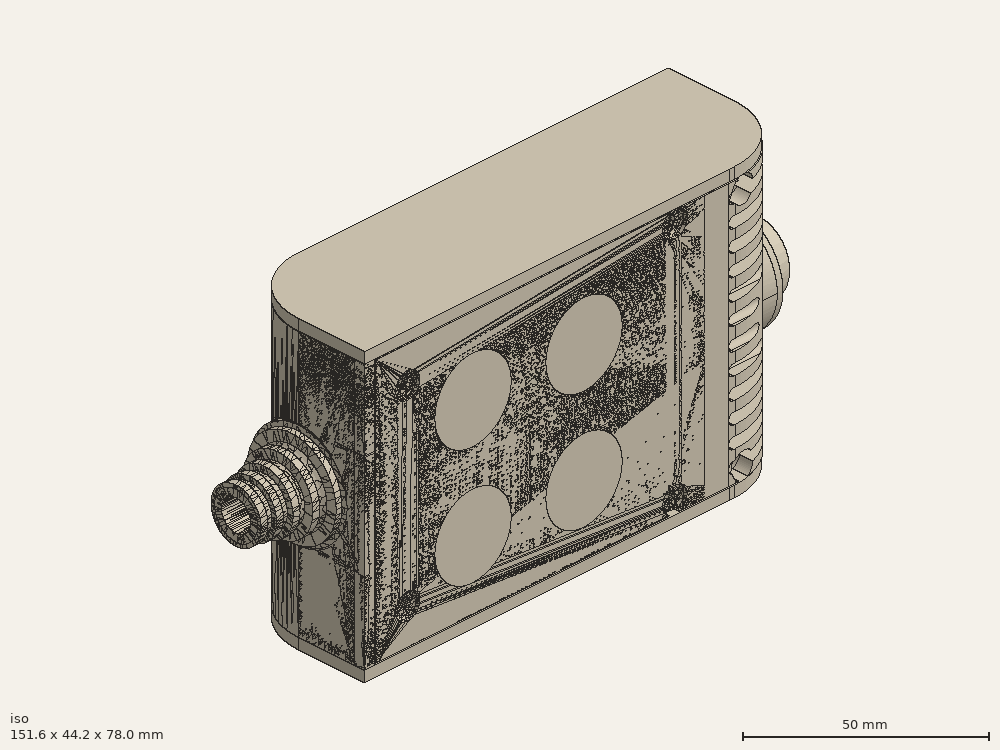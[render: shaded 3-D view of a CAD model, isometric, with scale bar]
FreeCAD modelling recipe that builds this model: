
FCSTD DOCUMENT  (FreeCAD 0.19R0.19.2)
Label: enclosure_195FCStd
License: All rights reserved
LicenseURL: http://en.wikipedia.org/wiki/All_rights_reserved
objects: Part::Revolution×152, Part::MultiFuse×146, Part::Feature×146, Sketcher::SketchObject×84, Part::Cut×70, Part::Cylinder×70, Part::Extrusion×67, Part::Fillet×58, Part::Box×36, App::MeasureDistance×4, PartDesign::Body×2, Image::ImagePlane×1
note: 831 computed .brp shape members not serialized (recipe doc carries the construction recipe); baked Part::Feature solids carry a one-line shape summary decoded from their .brp

FEATURE [Sketcher::SketchObject] Sketch  label="topSketch"
  FullyConstrained = true
  sketch-geometry (20):
    g0: LineSegment StartX=5.21097e-06 StartY=3 StartZ=0 EndX=5.21097e-06 EndY=19 EndZ=0
    g1: ArcOfCircle CenterX=19 CenterY=19 CenterZ=0 NormalX=0 NormalY=0 NormalZ=1 AngleXU=0 Radius=19 StartAngle=1.5708 EndAngle=3.14159
    g2: ArcOfCircle CenterX=19 CenterY=19 CenterZ=0 NormalX=0 NormalY=0 NormalZ=1 AngleXU=0 Radius=16 StartAngle=1.5708 EndAngle=3.14159
    g3: LineSegment StartX=114 StartY=35 StartZ=0 EndX=19 EndY=35 EndZ=0
    g4: LineSegment StartX=5.21097e-06 StartY=3 StartZ=0 EndX=5.21097e-06 EndY=0 EndZ=0
    g5: LineSegment StartX=3 StartY=0 StartZ=0 EndX=5.21097e-06 EndY=0 EndZ=0
    g6: LineSegment StartX=3 StartY=19 StartZ=0 EndX=3 EndY=0 EndZ=0
    g7: LineSegment StartX=19 StartY=38 StartZ=0 EndX=124 EndY=38 EndZ=0
    g8: Circle CenterX=119 CenterY=35 CenterZ=0 NormalX=0 NormalY=0 NormalZ=1 AngleXU=0 Radius=1
    g9: Circle CenterX=121 CenterY=35 CenterZ=0 NormalX=0 NormalY=0 NormalZ=1 AngleXU=0 Radius=1
    g10: Circle CenterX=121 CenterY=33 CenterZ=0 NormalX=0 NormalY=0 NormalZ=1 AngleXU=0 Radius=1
    g11: BSplineCurve PolesCount=3 KnotsCount=2 Degree=2 IsPeriodic=0
    g12: GeomPoint X=119 Y=35 Z=0
    g13: GeomPoint X=121 Y=33 Z=0
    g14: LineSegment StartX=119 StartY=35 StartZ=0 EndX=114 EndY=35 EndZ=0
    g15: ArcOfCircle CenterX=105 CenterY=19 CenterZ=0 NormalX=0 NormalY=0 NormalZ=1 AngleXU=0 Radius=19 StartAngle=5.7297 EndAngle=6.28319
    g16: ArcOfCircle CenterX=105 CenterY=19 CenterZ=0 NormalX=0 NormalY=0 NormalZ=1 AngleXU=0 Radius=16 StartAngle=5.60905 EndAngle=6.28319
    g17: LineSegment StartX=121 StartY=33 StartZ=0 EndX=121 EndY=19 EndZ=0
    g18: LineSegment StartX=124 StartY=38 StartZ=0 EndX=124 EndY=19 EndZ=0
    g19: LineSegment StartX=117.5 StartY=9.01251 StartZ=0 EndX=121.163 EndY=9.0125 EndZ=0
  constraints (46):
    c: Vertical(g0)
    c: Block(g0)
    c: Coincident(g1,g0)
    c: Block(g1)
    c: Coincident(g2,g1)
    c: Block(g2)
    c: Coincident(g3,g2)
    c: Horizontal(g3)
    c: Tangent(g3,g2)
    c: Coincident(g4,g0)
    c: Distance(g4) = 3
    c: Vertical(g4)
    c: Coincident(g5,g4)
    c: Horizontal(g5)
    c: Coincident(g6,g2)
    c: Coincident(g6,g5)
    c: Vertical(g6)
    c: Horizontal(g7)
    c: Distance(g7) = 105
    c: Coincident(g7,g1)
    c: Block(g3)
    c: Weight(g8) = 1
    c: Equal(g8,g9)
    c: Equal(g8,g10)
    c: InternalAlignment(g8,g11)
    c: InternalAlignment(g9,g11)
    c: InternalAlignment(g10,g11)
    c: InternalAlignment(g12,g11)
    c: InternalAlignment(g13,g11)
    c: Block(g11)
    c: Coincident(g14,g11)
    c: Coincident(g14,g3)
    c: Horizontal(g14)
    c: Block(g15)
    c: Coincident(g16,g15)
    c: Block(g16)
    c: Coincident(g17,g11)
    c: Coincident(g17,g16)
    c: Vertical(g17)
    c: Distance(g17) = 14
    c: Coincident(g18,g7)
    c: Coincident(g18,g15)
    c: Vertical(g18)
    c: Distance(g18) = 19
    c: Coincident(g19,g16)
    c: Coincident(g19,g15)
FEATURE [Sketcher::SketchObject] Sketch001  label="bottomSketch"
  FullyConstrained = true
  sketch-geometry (32):
    g0: LineSegment StartX=3.3 StartY=-6.03275e-07 StartZ=0 EndX=98 EndY=-6.03275e-07 EndZ=0
    g1: ArcOfCircle CenterX=98 CenterY=19 CenterZ=0 NormalX=0 NormalY=0 NormalZ=1 AngleXU=0 Radius=19 StartAngle=4.71239 EndAngle=5.71103
    g2: LineSegment StartX=6.3 StartY=8 StartZ=0 EndX=3.3 EndY=8 EndZ=0
    g3: LineSegment StartX=3.3 StartY=8 StartZ=0 EndX=3.3 EndY=-6.03275e-07 EndZ=0
    g4: ArcOfCircle CenterX=8.3 CenterY=5 CenterZ=0 NormalX=0 NormalY=0 NormalZ=1 AngleXU=0 Radius=2 StartAngle=3.14159 EndAngle=4.71239
    g5: LineSegment StartX=6.3 StartY=8 StartZ=0 EndX=6.3 EndY=5 EndZ=0
    g6: ArcOfCircle CenterX=98 CenterY=19 CenterZ=0 NormalX=0 NormalY=0 NormalZ=1 AngleXU=0 Radius=12.7 StartAngle=4.71239 EndAngle=6.28319
    g7: LineSegment StartX=94.7 StartY=3 StartZ=0 EndX=8.3 EndY=3 EndZ=0
    g8-g12: Circle x5 (B-spline internal-alignment scaffolding for g13; pole/knot coordinates omitted)
    g13: BSplineCurve PolesCount=5 KnotsCount=3 Degree=3 IsPeriodic=0
    g14: GeomPoint X=98 Y=6.3 Z=0
    g15: GeomPoint X=96.3938 Y=4.71946 Z=0
    g16: GeomPoint X=94.7 Y=3 Z=0
    g17-g23: Circle x7 (B-spline internal-alignment scaffolding for g24; pole/knot coordinates omitted)
    g24: BSplineCurve PolesCount=7 KnotsCount=5 Degree=3 IsPeriodic=0
    g25-g29: GeomPoint x5 (B-spline internal-alignment scaffolding for g24; pole/knot coordinates omitted)
    g30: ArcOfCircle CenterX=98 CenterY=19 CenterZ=0 NormalX=0 NormalY=0 NormalZ=1 AngleXU=0 Radius=15.7 StartAngle=5.81226 EndAngle=6.28319
    g31: LineSegment StartX=110.7 StartY=19 StartZ=0 EndX=113.7 EndY=19 EndZ=0
  constraints (41):
    c: Horizontal(g0)
    c: Coincident(g1,g0)
    c: Block(g1)
    c: Horizontal(g2)
    c: Distance(g2) = 3
    c: Coincident(g3,g2)
    c: Vertical(g3)
    c: Coincident(g3,g0)
    c: Block(g4)
    c: Block(g2)
    c: Coincident(g5,g2)
    c: Coincident(g5,g4)
    c: Vertical(g5)
    c: Coincident(g6,g1)
    c: Block(g6)
    c: Coincident(g7,g4)
    c: Horizontal(g7)
    c: Block(g0)
    c: Block(g7)
    c: Block(g3)
    c: Coincident(g13,g6)
    c: Weight(g8) = 1
    c: Equal(g8, g9-g12) x4
    c: Coincident(g13,g7)
    c: InternalAlignment(g8-g12 -> g13) x5
    c: InternalAlignment(g14,g13)
    c: InternalAlignment(g15,g13)
    c: InternalAlignment(g16,g13)
    c: Block(g13)
    c: Weight(g17) = 1
    c: Equal(g17, g18-g23) x6
    c: Coincident(g24,g1)
    c: InternalAlignment(g17-g23 -> g24) x7
    c: InternalAlignment(g25-g29 -> g24) x5
    c: Block(g24)
    c: Coincident(g30,g24)
    c: Coincident(g31,g6)
    c: Coincident(g31,g30)
    c: Horizontal(g31)
    c: Block(g31)
    c: Block(g30)
FEATURE [Part::Extrusion] Extrude  label="top"
  Base = -> Sketch
  Dir = (0,0,1)
  DirMode = 2
  FaceMakerClass = Part::FaceMakerBullseye
  LengthFwd = 72
  LengthRev = 0
  Solid = true
  Symmetric = false
FEATURE [Part::Extrusion] Extrude001  label="bottom"
  Base = -> Sketch001
  Dir = (0,0,1)
  DirMode = 2
  FaceMakerClass = Part::FaceMakerBullseye
  LengthFwd = 71.4
  LengthRev = 0
  Placement = pos=(0,0,0.3) rot=(0,0,1;0rad)
  Solid = true
  Symmetric = false
FEATURE [Sketcher::SketchObject] Sketch002  label="topSketch001"
  FullyConstrained = true
  sketch-geometry (8):
    g0: ArcOfCircle CenterX=19 CenterY=19.0975 CenterZ=0 NormalX=0 NormalY=0 NormalZ=1 AngleXU=0 Radius=18.9025 StartAngle=1.5708 EndAngle=3.14674
    g1: LineSegment StartX=0.0977805 StartY=19.0003 StartZ=0 EndX=0.0977805 EndY=0.000251602 EndZ=0
    g2: LineSegment StartX=19 StartY=38 StartZ=0 EndX=124 EndY=38 EndZ=0
    g3: LineSegment StartX=0.0977805 StartY=0.000251602 StartZ=0 EndX=105.098 EndY=0.000251602 EndZ=0
    g4: LineSegment StartX=124 StartY=38 StartZ=0 EndX=125.616 EndY=38 EndZ=0
    g5: LineSegment StartX=105.098 StartY=0.000251602 StartZ=0 EndX=106.713 EndY=0.000251602 EndZ=0
    g6: ArcOfCircle CenterX=106.616 CenterY=19 CenterZ=0 NormalX=0 NormalY=0 NormalZ=1 AngleXU=0 Radius=19 StartAngle=4.71754 EndAngle=6.28319
    g7: LineSegment StartX=125.616 StartY=38 StartZ=0 EndX=125.616 EndY=19 EndZ=0
  constraints (21):
    c: Block(g0)
    c: Coincident(g1,g0)
    c: Vertical(g1)
    c: Horizontal(g2)
    c: Distance(g2) = 105
    c: Coincident(g2,g0)
    c: Distance(g1) = 19
    c: Coincident(g3,g1)
    c: Horizontal(g3)
    c: Distance(g3) = 105
    c: Coincident(g4,g2)
    c: Horizontal(g4)
    c: Distance(g4) = 1.61553
    c: Horizontal(g5)
    c: Equal(g4,g5) = 1.61553
    c: Coincident(g5,g3)
    c: Block(g6)
    c: Coincident(g6,g5)
    c: Coincident(g7,g4)
    c: Coincident(g7,g6)
    c: Vertical(g7)
FEATURE [Part::Extrusion] Extrude002  label="sideA"
  Base = -> Sketch002
  Dir = (0,0,1)
  DirMode = 2
  FaceMakerClass = Part::FaceMakerBullseye
  LengthFwd = 3
  LengthRev = 0
  Placement = pos=(0,0,-3) rot=(0,0,1;0rad)
  Solid = true
  Symmetric = false
FEATURE [Sketcher::SketchObject] Sketch003  label="topSketch002"
  FullyConstrained = true
  sketch-geometry (6):
    g0: LineSegment StartX=19 StartY=38 StartZ=0 EndX=117 EndY=38 EndZ=0
    g1: ArcOfCircle CenterX=19 CenterY=19 CenterZ=0 NormalX=0 NormalY=0 NormalZ=1 AngleXU=0 Radius=19 StartAngle=1.5708 EndAngle=3.14159
    g2: LineSegment StartX=117 StartY=38 StartZ=0 EndX=117 EndY=19 EndZ=0
    g3: LineSegment StartX=98 StartY=1.0161e-12 StartZ=0 EndX=5.22862e-06 EndY=1.0161e-12 EndZ=0
    g4: LineSegment StartX=5.22862e-06 StartY=19 StartZ=0 EndX=5.22862e-06 EndY=1.0161e-12 EndZ=0
    g5: ArcOfCircle CenterX=98 CenterY=19 CenterZ=0 NormalX=0 NormalY=0 NormalZ=1 AngleXU=0 Radius=19 StartAngle=4.71239 EndAngle=6.28319
  constraints (16):
    c: Horizontal(g0)
    c: Distance(g0) = 98
    c: Coincident(g1,g0)
    c: Block(g1)
    c: Coincident(g2,g0)
    c: Vertical(g2)
    c: Distance(g2) = 19
    c: Horizontal(g3)
    c: Coincident(g4,g1)
    c: Vertical(g4)
    c: Coincident(g3,g4)
    c: Block(g3)
    c: Coincident(g5,g2)
    c: Coincident(g5,g3)
    c: Block(g0)
    c: Block(g5)
FEATURE [Sketcher::SketchObject] Sketch004
  FullyConstrained = true
  MapMode = 3
  Placement = pos=(0,0,0) rot=(1,0,0;1.5708rad)
  Support = -> [Extrude]
  sketch-geometry (8):
    g0: Circle CenterX=80.351 CenterY=-67.6202 CenterZ=0 NormalX=0 NormalY=0 NormalZ=1 AngleXU=0 Radius=2
    g1: Circle CenterX=80.351 CenterY=-67.6202 CenterZ=0 NormalX=0 NormalY=0 NormalZ=1 AngleXU=0 Radius=3
    g2: Circle CenterX=80.351 CenterY=-4.92017 CenterZ=0 NormalX=0 NormalY=0 NormalZ=1 AngleXU=0 Radius=2
    g3: Circle CenterX=80.351 CenterY=-4.92017 CenterZ=0 NormalX=0 NormalY=0 NormalZ=1 AngleXU=0 Radius=3
    g4: Circle CenterX=23.851 CenterY=-4.92017 CenterZ=0 NormalX=0 NormalY=0 NormalZ=1 AngleXU=0 Radius=2
    g5: Circle CenterX=23.851 CenterY=-4.92017 CenterZ=0 NormalX=0 NormalY=0 NormalZ=1 AngleXU=0 Radius=3
    g6: Circle CenterX=23.851 CenterY=-67.6202 CenterZ=0 NormalX=0 NormalY=0 NormalZ=1 AngleXU=0 Radius=2
    g7: Circle CenterX=23.851 CenterY=-67.6202 CenterZ=0 NormalX=0 NormalY=0 NormalZ=1 AngleXU=0 Radius=3
  constraints (8):
    c: Block(g3)
    c: Block(g2)
    c: Block(g1)
    c: Block(g0)
    c: Block(g6)
    c: Block(g7)
    c: Block(g4)
    c: Block(g5)
FEATURE [Part::Extrusion] Extrude004
  Base = -> Sketch004
  Dir = (0,-1,2e-16)
  DirMode = 2
  FaceMakerClass = Part::FaceMakerBullseye
  LengthFwd = 6
  LengthRev = 0
  Placement = pos=(0,9,0) rot=(0,0,1;0rad)
  Solid = true
  Symmetric = false
FEATURE [Sketcher::SketchObject] Sketch005
  FullyConstrained = true
  MapMode = 3
  Placement = pos=(0,0,0) rot=(1,0,0;1.5708rad)
  Support = -> [Extrude]
  sketch-geometry (8):
    g0: Circle CenterX=80.351 CenterY=-67.6202 CenterZ=0 NormalX=0 NormalY=0 NormalZ=1 AngleXU=0 Radius=3
    g1: Circle CenterX=80.351 CenterY=-4.92017 CenterZ=0 NormalX=0 NormalY=0 NormalZ=1 AngleXU=0 Radius=3
    g2: Circle CenterX=23.851 CenterY=-4.92017 CenterZ=0 NormalX=0 NormalY=0 NormalZ=1 AngleXU=0 Radius=3
    g3: Circle CenterX=23.851 CenterY=-67.6202 CenterZ=0 NormalX=0 NormalY=0 NormalZ=1 AngleXU=0 Radius=3
    g4: Circle CenterX=23.851 CenterY=-67.6202 CenterZ=0 NormalX=0 NormalY=0 NormalZ=1 AngleXU=0 Radius=5
    g5: Circle CenterX=80.351 CenterY=-67.6202 CenterZ=0 NormalX=0 NormalY=0 NormalZ=1 AngleXU=0 Radius=5
    g6: Circle CenterX=23.851 CenterY=-4.92017 CenterZ=0 NormalX=0 NormalY=0 NormalZ=1 AngleXU=0 Radius=5
    g7: Circle CenterX=80.351 CenterY=-4.92017 CenterZ=0 NormalX=0 NormalY=0 NormalZ=1 AngleXU=0 Radius=5
  constraints (8):
    c: Block(g1)
    c: Block(g0)
    c: Block(g3)
    c: Block(g2)
    c: Block(g5)
    c: Block(g4)
    c: Block(g6)
    c: Block(g7)
FEATURE [Part::Extrusion] Extrude005
  Base = -> Sketch005
  Dir = (0,-1,2e-16)
  DirMode = 2
  FaceMakerClass = Part::FaceMakerBullseye
  LengthFwd = 2
  LengthRev = 0
  Solid = true
  Symmetric = false
FEATURE [Sketcher::SketchObject] Sketch006
  FullyConstrained = true
  MapMode = 3
  Placement = pos=(0,0,0) rot=(1,0,0;1.5708rad)
  sketch-geometry (8):
    g0: Circle CenterX=80.351 CenterY=-67.6202 CenterZ=0 NormalX=0 NormalY=0 NormalZ=1 AngleXU=0 Radius=3
    g1: Circle CenterX=80.351 CenterY=-4.92017 CenterZ=0 NormalX=0 NormalY=0 NormalZ=1 AngleXU=0 Radius=3
    g2: Circle CenterX=23.851 CenterY=-4.92017 CenterZ=0 NormalX=0 NormalY=0 NormalZ=1 AngleXU=0 Radius=3
    g3: Circle CenterX=23.851 CenterY=-67.6202 CenterZ=0 NormalX=0 NormalY=0 NormalZ=1 AngleXU=0 Radius=3
    g4: Circle CenterX=23.851 CenterY=-67.6202 CenterZ=0 NormalX=0 NormalY=0 NormalZ=1 AngleXU=0 Radius=5
    g5: Circle CenterX=80.351 CenterY=-67.6202 CenterZ=0 NormalX=0 NormalY=0 NormalZ=1 AngleXU=0 Radius=5
    g6: Circle CenterX=23.851 CenterY=-4.92017 CenterZ=0 NormalX=0 NormalY=0 NormalZ=1 AngleXU=0 Radius=5
    g7: Circle CenterX=80.351 CenterY=-4.92017 CenterZ=0 NormalX=0 NormalY=0 NormalZ=1 AngleXU=0 Radius=5
  constraints (8):
    c: Block(g1)
    c: Block(g0)
    c: Block(g3)
    c: Block(g2)
    c: Block(g5)
    c: Block(g4)
    c: Block(g6)
    c: Block(g7)
FEATURE [Part::Extrusion] Extrude007
  Base = -> Sketch006
  Dir = (0,-1,2e-16)
  DirMode = 2
  FaceMakerClass = Part::FaceMakerBullseye
  LengthFwd = 2
  LengthRev = 0
  Solid = true
  Symmetric = false
FEATURE [Part::Fillet] Fillet
  Base = -> Extrude007
  Edges = 4 edges r=1.99: [Edge6,Edge12,Edge18,Edge24]
FEATURE [Part::Cut] Cut
  Base = -> Extrude005
  Placement = pos=(0,5,0) rot=(0,0,1;0rad)
  Tool = -> Fillet
FEATURE [Part::MultiFuse] Fusion  label="pCBScrews"
  Placement = pos=(-2.5,0,72.3) rot=(0,0,1;0rad)
  Shapes = -> [Extrude004,Cut]
FEATURE [App::MeasureDistance] Distance  label="Distance: 0.69 mm"
  Distance = 0.685967
  P1 = (24.0138,2.9647,0.3)
  P2 = (23.8901,3,-0.373787)
FEATURE [App::MeasureDistance] Distance001  label="Distance: 0.53 mm"
  Distance = 0.533607
  P1 = (80.2939,3,72.2334)
  P2 = (80.281,2.99661,71.7)
FEATURE [Part::Fillet] Fillet001
  Base = -> Extrude001
  Edges = 1 edges r=2.4: [Edge17]
FEATURE [Part::Fillet] Fillet002  label="bottom001"
  Base = -> Fillet001
  Edges = 1 edges r=2.4: [Edge36]
FEATURE [Part::Fillet] Fillet003  label="top001"
  Base = -> Extrude
  Edges = 1 edges r=2: [Edge1]
FEATURE [Sketcher::SketchObject] Sketch007
  FullyConstrained = true
  sketch-geometry (16):
    g0: LineSegment StartX=4 StartY=0 StartZ=0 EndX=4 EndY=2.4 EndZ=0
    g1: LineSegment StartX=4 StartY=2.4 StartZ=0 EndX=7 EndY=2.4 EndZ=0
    g2: LineSegment StartX=4 StartY=0 StartZ=0 EndX=5.7 EndY=0 EndZ=0
    g3: LineSegment StartX=5.7 StartY=0 StartZ=0 EndX=5.7 EndY=-5.6 EndZ=0
    g4-g8: Circle x5 (B-spline internal-alignment scaffolding for g9; pole/knot coordinates omitted)
    g9: BSplineCurve PolesCount=5 KnotsCount=3 Degree=3 IsPeriodic=0
    g10: GeomPoint X=7 Y=2.4 Z=0
    g11: GeomPoint X=10.4582 Y=-1.55472 Z=0
    g12: GeomPoint X=14 Y=-5.6 Z=0
    g13: LineSegment StartX=14 StartY=-5.6 StartZ=0 EndX=14 EndY=-14.1 EndZ=0
    g14: LineSegment StartX=14 StartY=-14.1 StartZ=0 EndX=6.5 EndY=-14.1 EndZ=0
    g15: LineSegment StartX=5.7 StartY=-5.6 StartZ=0 EndX=6.5 EndY=-14.1 EndZ=0
  constraints (28):
    c: Distance(g0) = 2.4
    c: Vertical(g0)
    c: Block(g0)
    c: Coincident(g1,g0)
    c: Horizontal(g1)
    c: Distance(g1) = 3
    c: Coincident(g2,g0)
    c: Horizontal(g2)
    c: Distance(g2) = 1.7
    c: Coincident(g3,g2)
    c: Vertical(g3)
    c: Distance(g3) = 5.6
    c: Coincident(g9,g1)
    c: Weight(g4) = 1
    c: Equal(g4, g5-g8) x4
    c: InternalAlignment(g4-g8 -> g9) x5
    c: InternalAlignment(g10,g9)
    c: InternalAlignment(g11,g9)
    c: InternalAlignment(g12,g9)
    c: Block(g9)
    c: Coincident(g13,g9)
    c: Vertical(g13)
    c: Distance(g13) = 8.5
    c: Coincident(g14,g13)
    c: Horizontal(g14)
    c: Distance(g14) = 7.5
    c: Coincident(g15,g3)
    c: Coincident(g15,g14)
FEATURE [Part::Feature] Face
  shape: bbox 10 x 16.5 x 2e-07 mm, 1 faces, 0 solids (baked)
FEATURE [Part::Revolution] Revolve  label="plugHousing"
  Angle = 360
  Axis = (0,1,0)
  Base = (0,0,0)
  FaceMakerClass = Part::FaceMakerBullseye
  Placement = pos=(0,0,36.15) rot=(0,0,1;0rad)
  Solid = false
  Source = -> Face
  Symmetric = false
FEATURE [Part::Feature] Face001
  shape: bbox 10 x 16.5 x 2e-07 mm, 1 faces, 0 solids (baked)
FEATURE [Part::Revolution] Revolve001  label="plugHousing001"
  Angle = 360
  Axis = (0,1,0)
  Base = (0,0,0)
  FaceMakerClass = Part::FaceMakerBullseye
  Placement = pos=(0,0,36.15) rot=(0,0,1;0rad)
  Solid = false
  Source = -> Face001
  Symmetric = false
FEATURE [Part::MultiFuse] Fusion001  label="plugHousing002"
  Placement = pos=(0,0,0) rot=(0,0,1;1.5708rad)
  Shapes = -> [Revolve001,Revolve]
FEATURE [Part::Feature] Face002
  shape: bbox 10 x 16.5 x 2e-07 mm, 1 faces, 0 solids (baked)
FEATURE [Part::Revolution] Revolve003  label="plugHousing005"
  Angle = 360
  Axis = (0,1,0)
  Base = (0,0,0)
  FaceMakerClass = Part::FaceMakerBullseye
  Placement = pos=(0,0,36.15) rot=(0,0,1;0rad)
  Solid = false
  Source = -> Face002
  Symmetric = false
FEATURE [Part::Feature] Face003
  shape: bbox 10 x 16.5 x 2e-07 mm, 1 faces, 0 solids (baked)
FEATURE [Part::Revolution] Revolve002  label="plugHousing003"
  Angle = 360
  Axis = (0,1,0)
  Base = (0,0,0)
  FaceMakerClass = Part::FaceMakerBullseye
  Placement = pos=(0,0,36.15) rot=(0,0,1;0rad)
  Solid = false
  Source = -> Face003
  Symmetric = false
FEATURE [Part::MultiFuse] Fusion002  label="plugHousing004"
  Placement = pos=(0,0,0) rot=(0,0,1;1.5708rad)
  Shapes = -> [Revolve002,Revolve003]
FEATURE [Part::MultiFuse] Fusion003  label="plugHousing006"
  Placement = pos=(0,19,0) rot=(0,0,1;3.14159rad)
  Shapes = -> [Fusion002,Fusion001]
FEATURE [Part::Feature] Face004
  shape: bbox 10 x 16.5 x 2e-07 mm, 1 faces, 0 solids (baked)
FEATURE [Part::Revolution] Revolve006  label="plugHousing010"
  Angle = 360
  Axis = (0,1,0)
  Base = (0,0,0)
  FaceMakerClass = Part::FaceMakerBullseye
  Placement = pos=(0,0,36.15) rot=(0,0,1;0rad)
  Solid = false
  Source = -> Face004
  Symmetric = false
FEATURE [Part::Feature] Face005
  shape: bbox 10 x 16.5 x 2e-07 mm, 1 faces, 0 solids (baked)
FEATURE [Part::Revolution] Revolve007  label="plugHousing011"
  Angle = 360
  Axis = (0,1,0)
  Base = (0,0,0)
  FaceMakerClass = Part::FaceMakerBullseye
  Placement = pos=(0,0,36.15) rot=(0,0,1;0rad)
  Solid = false
  Source = -> Face005
  Symmetric = false
FEATURE [Part::Feature] Face006
  shape: bbox 10 x 16.5 x 2e-07 mm, 1 faces, 0 solids (baked)
FEATURE [Part::Revolution] Revolve004  label="plugHousing007"
  Angle = 360
  Axis = (0,1,0)
  Base = (0,0,0)
  FaceMakerClass = Part::FaceMakerBullseye
  Placement = pos=(0,0,36.15) rot=(0,0,1;0rad)
  Solid = false
  Source = -> Face006
  Symmetric = false
FEATURE [Part::MultiFuse] Fusion004  label="plugHousing009"
  Placement = pos=(0,0,0) rot=(0,0,1;1.5708rad)
  Shapes = -> [Revolve004,Revolve007]
FEATURE [Part::Feature] Face007
  shape: bbox 10 x 16.5 x 2e-07 mm, 1 faces, 0 solids (baked)
FEATURE [Part::Revolution] Revolve005  label="plugHousing008"
  Angle = 360
  Axis = (0,1,0)
  Base = (0,0,0)
  FaceMakerClass = Part::FaceMakerBullseye
  Placement = pos=(0,0,36.15) rot=(0,0,1;0rad)
  Solid = false
  Source = -> Face007
  Symmetric = false
FEATURE [Part::MultiFuse] Fusion005  label="plugHousing012"
  Placement = pos=(0,0,0) rot=(0,0,1;1.5708rad)
  Shapes = -> [Revolve006,Revolve005]
FEATURE [Part::MultiFuse] Fusion006  label="plugHousing013"
  Placement = pos=(0,19,0) rot=(0,0,1;3.14159rad)
  Shapes = -> [Fusion005,Fusion004]
FEATURE [Part::MultiFuse] Fusion007  label="plugHousing014"
  Placement = pos=(122.621,0,-0.15) rot=(0,0,1;0rad)
  Shapes = -> [Fusion003,Fusion006]
FEATURE [Part::Cylinder] Cylinder002
  Angle = 360
  AttacherType = Attacher::AttachEngine3D
  Height = 20
  Placement = pos=(0,0,36.15) rot=(0,0,1;0rad)
  Radius = 4
FEATURE [Part::Cylinder] Cylinder003
  Angle = 360
  AttacherType = Attacher::AttachEngine3D
  Height = 10
  Placement = pos=(0,0,36.15) rot=(0,0,1;0rad)
  Radius = 4
FEATURE [Part::MultiFuse] Fusion009  label="removeToCreateHoleForPlugHousing"
  Placement = pos=(70,19,36.15) rot=(0,1,0;1.5708rad)
  Shapes = -> [Cylinder002,Cylinder003]
FEATURE [Part::Cylinder] Cylinder004
  Angle = 360
  AttacherType = Attacher::AttachEngine3D
  Height = 20
  Placement = pos=(0,0,36.15) rot=(0,0,1;0rad)
  Radius = 4
FEATURE [Part::Cylinder] Cylinder005
  Angle = 360
  AttacherType = Attacher::AttachEngine3D
  Height = 10
  Placement = pos=(0,0,36.15) rot=(0,0,1;0rad)
  Radius = 4
FEATURE [Part::MultiFuse] Fusion010  label="removeToCreateHoleForPlugHousing001"
  Placement = pos=(70,19,36.15) rot=(0,1,0;1.5708rad)
  Shapes = -> [Cylinder004,Cylinder005]
FEATURE [Part::Cut] Cut001
  Base = -> Fillet003
  Tool = -> Fusion010
FEATURE [Part::Cut] Cut002  label="Bottom"
  Base = -> Fillet002
  Tool = -> Fusion009
FEATURE [Part::Feature] Face008
  shape: bbox 10 x 16.5 x 2e-07 mm, 1 faces, 0 solids (baked)
FEATURE [Part::Revolution] Revolve011  label="plugHousing021"
  Angle = 360
  Axis = (0,1,0)
  Base = (0,0,0)
  FaceMakerClass = Part::FaceMakerBullseye
  Placement = pos=(0,0,36.15) rot=(0,0,1;0rad)
  Solid = false
  Source = -> Face008
  Symmetric = false
FEATURE [Part::Feature] Face009
  shape: bbox 10 x 16.5 x 2e-07 mm, 1 faces, 0 solids (baked)
FEATURE [Part::Revolution] Revolve012  label="plugHousing022"
  Angle = 360
  Axis = (0,1,0)
  Base = (0,0,0)
  FaceMakerClass = Part::FaceMakerBullseye
  Placement = pos=(0,0,36.15) rot=(0,0,1;0rad)
  Solid = false
  Source = -> Face009
  Symmetric = false
FEATURE [Part::Feature] Face010 .. Face013  x4 (patterned run collapsed; names and placements below)
  shape: bbox 10 x 16.5 x 2e-07 mm, 1 faces, 0 solids (baked)
FEATURE [Part::Revolution] Revolve015  label="plugHousing027"
  Angle = 360
  Axis = (0,1,0)
  Base = (0,0,0)
  FaceMakerClass = Part::FaceMakerBullseye
  Placement = pos=(0,0,36.15) rot=(0,0,1;0rad)
  Solid = false
  Source = -> Face013
  Symmetric = false
FEATURE [Part::Feature] Face014
  shape: bbox 10 x 16.5 x 2e-07 mm, 1 faces, 0 solids (baked)
FEATURE [Part::Feature] Face015
  shape: bbox 10 x 16.5 x 2e-07 mm, 1 faces, 0 solids (baked)
FEATURE [Part::Feature] Face016
  shape: bbox 10 x 16.5 x 2e-07 mm, 1 faces, 0 solids (baked)
FEATURE [Part::Revolution] Revolve019  label="plugHousing033"
  Angle = 360
  Axis = (0,1,0)
  Base = (0,0,0)
  FaceMakerClass = Part::FaceMakerBullseye
  Placement = pos=(0,0,36.15) rot=(0,0,1;0rad)
  Solid = false
  Source = -> Face016
  Symmetric = false
FEATURE [Part::Feature] Face017
  shape: bbox 10 x 16.5 x 2e-07 mm, 1 faces, 0 solids (baked)
FEATURE [Part::Revolution] Revolve020  label="plugHousing034"
  Angle = 360
  Axis = (0,1,0)
  Base = (0,0,0)
  FaceMakerClass = Part::FaceMakerBullseye
  Placement = pos=(0,0,36.15) rot=(0,0,1;0rad)
  Solid = false
  Source = -> Face017
  Symmetric = false
FEATURE [Part::Feature] Face018
  shape: bbox 10 x 16.5 x 2e-07 mm, 1 faces, 0 solids (baked)
FEATURE [Part::Revolution] Revolve016  label="plugHousing030"
  Angle = 360
  Axis = (0,1,0)
  Base = (0,0,0)
  FaceMakerClass = Part::FaceMakerBullseye
  Placement = pos=(0,0,36.15) rot=(0,0,1;0rad)
  Solid = false
  Source = -> Face018
  Symmetric = false
FEATURE [Part::MultiFuse] Fusion020  label="plugHousing038"
  Placement = pos=(0,0,0) rot=(0,0,1;1.5708rad)
  Shapes = -> [Revolve016,Revolve020]
FEATURE [Part::Feature] Face019
  shape: bbox 10 x 16.5 x 2e-07 mm, 1 faces, 0 solids (baked)
FEATURE [Part::Feature] Face020
  shape: bbox 10 x 16.5 x 2e-07 mm, 1 faces, 0 solids (baked)
FEATURE [Part::Revolution] Revolve017  label="plugHousing031"
  Angle = 360
  Axis = (0,1,0)
  Base = (0,0,0)
  FaceMakerClass = Part::FaceMakerBullseye
  Placement = pos=(0,0,36.15) rot=(0,0,1;0rad)
  Solid = false
  Source = -> Face020
  Symmetric = false
FEATURE [Part::MultiFuse] Fusion021  label="plugHousing039"
  Placement = pos=(0,0,0) rot=(0,0,1;1.5708rad)
  Shapes = -> [Revolve019,Revolve017]
FEATURE [Part::MultiFuse] Fusion023  label="plugHousing041"
  Placement = pos=(0,19,0) rot=(0,0,1;3.14159rad)
  Shapes = -> [Fusion021,Fusion020]
FEATURE [Part::Revolution] Revolve022  label="plugHousing043"
  Angle = 360
  Axis = (0,1,0)
  Base = (0,0,0)
  FaceMakerClass = Part::FaceMakerBullseye
  Placement = pos=(0,0,36.15) rot=(0,0,1;0rad)
  Solid = false
  Source = -> Face019
  Symmetric = false
FEATURE [Part::Feature] Face021
  shape: bbox 10 x 16.5 x 2e-07 mm, 1 faces, 0 solids (baked)
FEATURE [Part::Revolution] Revolve023  label="plugHousing044"
  Angle = 360
  Axis = (0,1,0)
  Base = (0,0,0)
  FaceMakerClass = Part::FaceMakerBullseye
  Placement = pos=(0,0,36.15) rot=(0,0,1;0rad)
  Solid = false
  Source = -> Face021
  Symmetric = false
FEATURE [Part::Feature] Face022
  shape: bbox 10 x 16.5 x 2e-07 mm, 1 faces, 0 solids (baked)
FEATURE [Part::Revolution] Revolve018  label="plugHousing032"
  Angle = 360
  Axis = (0,1,0)
  Base = (0,0,0)
  FaceMakerClass = Part::FaceMakerBullseye
  Placement = pos=(0,0,36.15) rot=(0,0,1;0rad)
  Solid = false
  Source = -> Face022
  Symmetric = false
FEATURE [Part::MultiFuse] Fusion022  label="plugHousing040"
  Placement = pos=(0,0,0) rot=(0,0,1;1.5708rad)
  Shapes = -> [Revolve018,Revolve023]
FEATURE [Part::Feature] Face023
  shape: bbox 10 x 16.5 x 2e-07 mm, 1 faces, 0 solids (baked)
FEATURE [Part::Revolution] Revolve021  label="plugHousing035"
  Angle = 360
  Axis = (0,1,0)
  Base = (0,0,0)
  FaceMakerClass = Part::FaceMakerBullseye
  Placement = pos=(0,0,36.15) rot=(0,0,1;0rad)
  Solid = false
  Source = -> Face023
  Symmetric = false
FEATURE [Part::MultiFuse] Fusion018  label="plugHousing036"
  Placement = pos=(0,0,0) rot=(0,0,1;1.5708rad)
  Shapes = -> [Revolve022,Revolve021]
FEATURE [Part::MultiFuse] Fusion019  label="plugHousing037"
  Placement = pos=(0,19,0) rot=(0,0,1;3.14159rad)
  Shapes = -> [Fusion018,Fusion022]
FEATURE [Part::MultiFuse] Fusion024  label="plugHousing042"
  Placement = pos=(122.621,0,-0.15) rot=(0,0,1;0rad)
  Shapes = -> [Fusion023,Fusion019]
FEATURE [Part::Cylinder] Cylinder006
  Angle = 360
  AttacherType = Attacher::AttachEngine3D
  Height = 20
  Placement = pos=(0,0,36.15) rot=(0,0,1;0rad)
  Radius = 14.3
FEATURE [Part::Cylinder] Cylinder007
  Angle = 360
  AttacherType = Attacher::AttachEngine3D
  Height = 10
  Placement = pos=(0,0,36.15) rot=(0,0,1;0rad)
  Radius = 4
FEATURE [Part::MultiFuse] Fusion026  label="removeToCreteHoleForPlugHousing"
  Placement = pos=(70,19,36) rot=(0,1,0;1.5708rad)
  Shapes = -> [Cylinder006,Cylinder007]
FEATURE [Part::Box] Box001  label="Cube001"
  AttacherType = Attacher::AttachEngine3D
  Height = 28
  Length = 3
  Placement = pos=(110.7,19,22) rot=(0,0,1;0rad)
  Width = 15.7
FEATURE [Part::Cut] Cut003  label="top002"
  Base = -> Cut001
  Tool = -> Fusion007
FEATURE [Part::Revolution] Revolve008  label="plugHousing015"
  Angle = 360
  Axis = (0,1,0)
  Base = (0,0,0)
  FaceMakerClass = Part::FaceMakerBullseye
  Placement = pos=(0,0,36.15) rot=(0,0,1;0rad)
  Solid = false
  Source = -> Face010
  Symmetric = false
FEATURE [Part::MultiFuse] Fusion013  label="plugHousing020"
  Placement = pos=(0,0,0) rot=(0,0,1;1.5708rad)
  Shapes = -> [Revolve008,Revolve012]
FEATURE [Part::Cut] Cut004  label="top003"
  Base = -> Cut003
  Placement = pos=(1,0,0) rot=(0,0,1;0rad)
  Tool = -> Fusion026
FEATURE [Part::Cylinder] Cylinder008
  Angle = 360
  AttacherType = Attacher::AttachEngine3D
  Height = 20
  Placement = pos=(0,0,36.15) rot=(0,0,1;0rad)
  Radius = 10.3
FEATURE [Part::Cylinder] Cylinder009
  Angle = 360
  AttacherType = Attacher::AttachEngine3D
  Height = 10
  Placement = pos=(0,0,36.15) rot=(0,0,1;0rad)
  Radius = 4
FEATURE [Part::MultiFuse] Fusion027  label="removeToCreteHoleForPlugHousing001"
  Placement = pos=(70,19,36) rot=(0,1,0;1.5708rad)
  Shapes = -> [Cylinder008,Cylinder009]
FEATURE [Part::Cut] Cut005  label="plugHousingTab"
  Base = -> Box001
  Tool = -> Fusion027
FEATURE [Part::MultiFuse] Fusion028  label="plugHousing045"
  Shapes = -> [Fusion024,Cut005]
FEATURE [Part::Box] Box002  label="Cube002"
  AttacherType = Attacher::AttachEngine3D
  Height = 28.8
  Length = 3
  Placement = pos=(107.3,28,21.6) rot=(0,0,1;0rad)
  Width = 7
FEATURE [Part::Box] Box003  label="Cube003"
  AttacherType = Attacher::AttachEngine3D
  Height = 3
  Length = 6.4
  Placement = pos=(107.3,28,18.6) rot=(0,0,1;0rad)
  Width = 7
FEATURE [Part::Box] Box004  label="Cube004"
  AttacherType = Attacher::AttachEngine3D
  Height = 3
  Length = 6.4
  Placement = pos=(107.3,28,50.4) rot=(0,0,1;0rad)
  Width = 7
FEATURE [Part::MultiFuse] Fusion029  label="plugHousingBracketHolder"
  Shapes = -> [Box004,Box002,Box003]
FEATURE [Part::Cylinder] Cylinder010
  Angle = 360
  AttacherType = Attacher::AttachEngine3D
  Height = 20
  Placement = pos=(0,0,36.15) rot=(0,0,1;0rad)
  Radius = 14.3
FEATURE [Part::Cylinder] Cylinder011
  Angle = 360
  AttacherType = Attacher::AttachEngine3D
  Height = 10
  Placement = pos=(0,0,36.15) rot=(0,0,1;0rad)
  Radius = 4
FEATURE [Part::MultiFuse] Fusion030  label="removeToCreteHoleForPlugHousing002"
  Placement = pos=(70,19,36) rot=(0,1,0;1.5708rad)
  Shapes = -> [Cylinder010,Cylinder011]
FEATURE [Part::Cut] Cut006  label="plugHousingBracketHolder001"
  Base = -> Fusion029
  Tool = -> Fusion030
FEATURE [Part::Cylinder] Cylinder012
  Angle = 360
  AttacherType = Attacher::AttachEngine3D
  Height = 20
  Placement = pos=(0,0,36.15) rot=(0,0,1;0rad)
  Radius = 7
FEATURE [Part::Cylinder] Cylinder013
  Angle = 360
  AttacherType = Attacher::AttachEngine3D
  Height = 10
  Placement = pos=(0,0,36.15) rot=(0,0,1;0rad)
  Radius = 4
FEATURE [Part::MultiFuse] Fusion032  label="removeToCreteHoleForPlugHousing003"
  Placement = pos=(70,19,36) rot=(0,1,0;1.5708rad)
  Shapes = -> [Cylinder012,Cylinder013]
FEATURE [Part::Cut] Cut007  label="bottom002"
  Base = -> Cut002
  Tool = -> Fusion032
FEATURE [Sketcher::SketchObject] Sketch008
  FullyConstrained = true
  sketch-geometry (54):
    g0: LineSegment StartX=-4.2 StartY=0 StartZ=0 EndX=-6.2 EndY=0 EndZ=0
    g1: LineSegment StartX=-14 StartY=-18 StartZ=0 EndX=-14 EndY=-26.5 EndZ=0
    g2: LineSegment StartX=-4.2 StartY=0 StartZ=0 EndX=-4.2 EndY=-13.4877 EndZ=0
    g3: Circle CenterX=-4.2 CenterY=-13.4877 CenterZ=0 NormalX=0 NormalY=0 NormalZ=1 AngleXU=0 Radius=1
    g4: Circle CenterX=-4.2 CenterY=-26.5 CenterZ=0 NormalX=0 NormalY=0 NormalZ=1 AngleXU=0 Radius=1
    g5: Circle CenterX=-8.2 CenterY=-26.5 CenterZ=0 NormalX=0 NormalY=0 NormalZ=1 AngleXU=0 Radius=1
    g6: BSplineCurve PolesCount=3 KnotsCount=2 Degree=2 IsPeriodic=0
    g7: GeomPoint X=-4.2 Y=-13.4877 Z=0
    g8: GeomPoint X=-8.2 Y=-26.5 Z=0
    g9: LineSegment StartX=-14 StartY=-26.5 StartZ=0 EndX=-8.2 EndY=-26.5 EndZ=0
    g10: LineSegment StartX=-10.15 StartY=-12 StartZ=0 EndX=-10.15 EndY=-14 EndZ=0
    g11: LineSegment StartX=-12.8401 StartY=-16 StartZ=0 EndX=-10.1571 EndY=-16 EndZ=0
    g12: LineSegment StartX=-10.15 StartY=-14 StartZ=0 EndX=-8.70761 EndY=-14 EndZ=0
    g13: LineSegment StartX=-12.8401 StartY=-16 StartZ=0 EndX=-12.8401 EndY=-17.6958 EndZ=0
    g14: LineSegment StartX=-10.15 StartY=-12 StartZ=0 EndX=-7.79258 EndY=-12 EndZ=0
    g15: Circle CenterX=-6.2215 CenterY=-2 CenterZ=0 NormalX=0 NormalY=0 NormalZ=1 AngleXU=0 Radius=1
    g16: Circle CenterX=-6.22762 CenterY=-2.58724 CenterZ=0 NormalX=0 NormalY=0 NormalZ=1 AngleXU=0 Radius=1
    g17: Circle CenterX=-6.32538 CenterY=-4 CenterZ=0 NormalX=0 NormalY=0 NormalZ=1 AngleXU=0 Radius=1
    g18: BSplineCurve PolesCount=3 KnotsCount=2 Degree=2 IsPeriodic=0
    g19: GeomPoint X=-6.2215 Y=-2 Z=0
    g20: GeomPoint X=-6.32538 Y=-4 Z=0
    g21: Circle CenterX=-6.48644 CenterY=-5.99526 CenterZ=0 NormalX=0 NormalY=0 NormalZ=1 AngleXU=0 Radius=1
    g22: Circle CenterX=-6.58486 CenterY=-6.99526 CenterZ=0 NormalX=0 NormalY=0 NormalZ=1 AngleXU=0 Radius=1
    g23: Circle CenterX=-6.77343 CenterY=-8 CenterZ=0 NormalX=0 NormalY=0 NormalZ=1 AngleXU=0 Radius=1
    g24: BSplineCurve PolesCount=3 KnotsCount=2 Degree=2 IsPeriodic=0
    g25: GeomPoint X=-6.48644 Y=-5.99526 Z=0
    g26: GeomPoint X=-6.77343 Y=-8 Z=0
    g27: Circle CenterX=-7.19003 CenterY=-10 CenterZ=0 NormalX=0 NormalY=0 NormalZ=1 AngleXU=0 Radius=1
    g28: Circle CenterX=-7.44407 CenterY=-11.0915 CenterZ=0 NormalX=0 NormalY=0 NormalZ=1 AngleXU=0 Radius=1
    g29: Circle CenterX=-7.79258 CenterY=-12 CenterZ=0 NormalX=0 NormalY=0 NormalZ=1 AngleXU=0 Radius=1
    g30: BSplineCurve PolesCount=3 KnotsCount=2 Degree=2 IsPeriodic=0
    g31: GeomPoint X=-7.19003 Y=-10 Z=0
    g32: GeomPoint X=-7.79258 Y=-12 Z=0
    g33: Circle CenterX=-8.70761 CenterY=-14 CenterZ=0 NormalX=0 NormalY=0 NormalZ=1 AngleXU=0 Radius=1
    g34: Circle CenterX=-9.33087 CenterY=-15.1837 CenterZ=0 NormalX=0 NormalY=0 NormalZ=1 AngleXU=0 Radius=1
    g35: Circle CenterX=-10.1571 CenterY=-16 CenterZ=0 NormalX=0 NormalY=0 NormalZ=1 AngleXU=0 Radius=1
    g36: BSplineCurve PolesCount=3 KnotsCount=2 Degree=2 IsPeriodic=0
    g37: GeomPoint X=-8.70761 Y=-14 Z=0
    g38: GeomPoint X=-10.1571 Y=-16 Z=0
    g39: Circle CenterX=-12.8401 CenterY=-17.6958 CenterZ=0 NormalX=0 NormalY=0 NormalZ=1 AngleXU=0 Radius=1
    g40: Circle CenterX=-13.3521 CenterY=-17.9027 CenterZ=0 NormalX=0 NormalY=0 NormalZ=1 AngleXU=0 Radius=1
    g41: Circle CenterX=-14 CenterY=-18 CenterZ=0 NormalX=0 NormalY=0 NormalZ=1 AngleXU=0 Radius=1
    g42: BSplineCurve PolesCount=3 KnotsCount=2 Degree=2 IsPeriodic=0
    g43: GeomPoint X=-12.8401 Y=-17.6958 Z=0
    g44: GeomPoint X=-14 Y=-18 Z=0
    g45: LineSegment StartX=-6.2 StartY=0 StartZ=0 EndX=-7.2 EndY=0 EndZ=0
    g46: LineSegment StartX=-7.2 StartY=0 StartZ=0 EndX=-7.2 EndY=-2 EndZ=0
    g47: LineSegment StartX=-7.2 StartY=-2 StartZ=0 EndX=-6.2215 EndY=-2 EndZ=0
    g48: LineSegment StartX=-6.32538 StartY=-4 StartZ=0 EndX=-7.65538 EndY=-4 EndZ=0
    g49: LineSegment StartX=-7.65538 StartY=-4 StartZ=0 EndX=-7.65538 EndY=-5.99526 EndZ=0
    g50: LineSegment StartX=-7.65538 StartY=-5.99526 StartZ=0 EndX=-6.48644 EndY=-5.99526 EndZ=0
    g51: LineSegment StartX=-6.77343 StartY=-8 StartZ=0 EndX=-8.43343 EndY=-8 EndZ=0
    g52: LineSegment StartX=-8.43343 StartY=-8 StartZ=0 EndX=-8.43343 EndY=-10 EndZ=0
    g53: LineSegment StartX=-8.43343 StartY=-10 StartZ=0 EndX=-7.19003 EndY=-10 EndZ=0
  constraints (112):
    c: Horizontal(g0)
    c: Distance(g0) = 2
    c: Block(g0)
    c: Vertical(g1)
    c: Coincident(g2,g0)
    c: Vertical(g2)
    c: Block(g2)
    c: Coincident(g6,g2)
    c: Weight(g3) = 1
    c: Equal(g3,g4)
    c: Equal(g3,g5)
    c: InternalAlignment(g3,g6)
    c: InternalAlignment(g4,g6)
    c: InternalAlignment(g5,g6)
    c: InternalAlignment(g7,g6)
    c: InternalAlignment(g8,g6)
    c: Block(g6)
    c: Coincident(g9,g1)
    c: Coincident(g9,g6)
    c: Horizontal(g9)
    c: Vertical(g10)
    c: Block(g10)
    c: Horizontal(g11)
    c: Block(g11)
    c: Coincident(g12,g10)
    c: Horizontal(g12)
    c: Block(g12)
    c: Coincident(g13,g11)
    c: Vertical(g13)
    c: Block(g13)
    c: Coincident(g14,g10)
    c: Horizontal(g14)
    c: Block(g14)
    c: Block(g9)
    c: Block(g1)
    c: Weight(g15) = 1
    c: Equal(g15,g16)
    c: Equal(g15,g17)
    c: InternalAlignment(g15,g18)
    c: InternalAlignment(g16,g18)
    c: InternalAlignment(g17,g18)
    c: InternalAlignment(g19,g18)
    c: InternalAlignment(g20,g18)
    c: Weight(g21) = 1
    c: Equal(g21,g22)
    c: Equal(g21,g23)
    c: InternalAlignment(g21,g24)
    c: InternalAlignment(g22,g24)
    c: InternalAlignment(g23,g24)
    c: InternalAlignment(g25,g24)
    c: InternalAlignment(g26,g24)
    c: Weight(g27) = 1
    c: Equal(g27,g28)
    c: Equal(g27,g29)
    c: Coincident(g30,g14)
    c: InternalAlignment(g27,g30)
    c: InternalAlignment(g28,g30)
    c: InternalAlignment(g29,g30)
    c: InternalAlignment(g31,g30)
    c: InternalAlignment(g32,g30)
    c: Coincident(g36,g12)
    c: Weight(g33) = 1
    c: Equal(g33,g34)
    c: Equal(g33,g35)
    c: Coincident(g36,g11)
    c: InternalAlignment(g33,g36)
    c: InternalAlignment(g34,g36)
    c: InternalAlignment(g35,g36)
    c: InternalAlignment(g37,g36)
    c: InternalAlignment(g38,g36)
    c: Coincident(g42,g13)
    c: Weight(g39) = 1
    c: Equal(g39,g40)
    c: Equal(g39,g41)
    c: Coincident(g42,g1)
    c: InternalAlignment(g39,g42)
    c: InternalAlignment(g40,g42)
    c: InternalAlignment(g41,g42)
    c: InternalAlignment(g43,g42)
    c: InternalAlignment(g44,g42)
    c: Block(g18)
    c: Block(g24)
    c: Block(g30)
    c: Block(g36)
    c: Block(g42)
    c: Horizontal(g45)
    c: Coincident(g45,g0)
    c: Vertical(g46)
    c: Coincident(g46,g45)
    c: Coincident(g47,g46)
    c: Coincident(g47,g18)
    c: Horizontal(g47)
    c: Block(g46)
    c: Coincident(g48,g18)
    c: Horizontal(g48)
    c: Distance(g48) = 1.33
    c: Vertical(g49)
    c: Coincident(g49,g48)
    c: Coincident(g50,g49)
    c: Coincident(g50,g24)
    c: Horizontal(g50)
    c: Tangent(g50,g22)
    c: Horizontal(g51)
    c: Coincident(g51,g24)
    c: Block(g51)
    c: Vertical(g52)
    c: Block(g52)
    c: Coincident(g52,g51)
    c: Coincident(g53,g52)
    c: Coincident(g53,g30)
    c: Horizontal(g53)
    c: Distance(g1) = 8.5
FEATURE [Part::Feature] Face024
  shape: bbox 9.8 x 26.5 x 2e-07 mm, 1 faces, 0 solids (baked)
FEATURE [Part::Revolution] Revolve024
  Angle = 360
  Axis = (0,1,0)
  Base = (0,0,0)
  FaceMakerClass = Part::FaceMakerBullseye
  Placement = pos=(0,0,0) rot=(0,0,1;1.5708rad)
  Solid = false
  Source = -> Face024
  Symmetric = false
FEATURE [Part::Feature] Face025
  shape: bbox 9.8 x 26.5 x 2e-07 mm, 1 faces, 0 solids (baked)
FEATURE [Part::Revolution] Revolve025
  Angle = 360
  Axis = (0,1,0)
  Base = (0,0,0)
  FaceMakerClass = Part::FaceMakerBullseye
  Placement = pos=(0,0,0) rot=(0,0,1;1.5708rad)
  Solid = false
  Source = -> Face025
  Symmetric = false
FEATURE [Part::MultiFuse] Fusion033
  Placement = pos=(-18,19,36) rot=(0,0,1;0rad)
  Shapes = -> [Revolve025,Revolve024]
FEATURE [Part::Cylinder] Cylinder014
  Angle = 360
  AttacherType = Attacher::AttachEngine3D
  Height = 20
  Placement = pos=(0,0,36.15) rot=(0,0,1;0rad)
  Radius = 14.3
FEATURE [Part::Cylinder] Cylinder015
  Angle = 360
  AttacherType = Attacher::AttachEngine3D
  Height = 10
  Placement = pos=(0,0,36.15) rot=(0,0,1;0rad)
  Radius = 4
FEATURE [Part::MultiFuse] Fusion034  label="removeToCreteHoleForPlugHousing004"
  Placement = pos=(-42,19,36) rot=(0,1,0;1.5708rad)
  Shapes = -> [Cylinder014,Cylinder015]
FEATURE [Part::Cut] Cut008  label="top004"
  Base = -> Cut004
  Placement = pos=(-1,0,0) rot=(0,0,1;0rad)
  Tool = -> Fusion034
FEATURE [Part::Box] Box005  label="Cube005"
  AttacherType = Attacher::AttachEngine3D
  Height = 28
  Length = 3
  Placement = pos=(110.7,19,22) rot=(0,0,1;0rad)
  Width = 15.7
FEATURE [Part::Cylinder] Cylinder016
  Angle = 360
  AttacherType = Attacher::AttachEngine3D
  Height = 10
  Placement = pos=(0,0,36.15) rot=(0,0,1;0rad)
  Radius = 4
FEATURE [Part::Cylinder] Cylinder017
  Angle = 360
  AttacherType = Attacher::AttachEngine3D
  Height = 20
  Placement = pos=(0,0,36.15) rot=(0,0,1;0rad)
  Radius = 10.3
FEATURE [Part::MultiFuse] Fusion035  label="removeToCreteHoleForPlugHousing005"
  Placement = pos=(70,19,36) rot=(0,1,0;1.5708rad)
  Shapes = -> [Cylinder017,Cylinder016]
FEATURE [Part::Cut] Cut009  label="plugHousingTab001"
  Base = -> Box005
  Placement = pos=(-107.4,-14,0) rot=(0,0,1;0rad)
  Tool = -> Fusion035
FEATURE [Part::Box] Box006  label="Cube006"
  AttacherType = Attacher::AttachEngine3D
  Height = 28
  Length = 3
  Placement = pos=(110.7,19,22) rot=(0,0,1;0rad)
  Width = 15.7
FEATURE [Part::Cylinder] Cylinder018
  Angle = 360
  AttacherType = Attacher::AttachEngine3D
  Height = 10
  Placement = pos=(0,0,36.15) rot=(0,0,1;0rad)
  Radius = 4
FEATURE [Part::Cylinder] Cylinder019
  Angle = 360
  AttacherType = Attacher::AttachEngine3D
  Height = 20
  Placement = pos=(0,0,36.15) rot=(0,0,1;0rad)
  Radius = 10.3
FEATURE [Part::MultiFuse] Fusion036  label="removeToCreteHoleForPlugHousing006"
  Placement = pos=(70,19,36) rot=(0,1,0;1.5708rad)
  Shapes = -> [Cylinder019,Cylinder018]
FEATURE [Part::Cut] Cut010  label="plugHousingTab002"
  Base = -> Box006
  Placement = pos=(-107.4,-14,0) rot=(0,0,1;0rad)
  Tool = -> Fusion036
FEATURE [Part::MultiFuse] Fusion037
  Placement = pos=(9.6,23,0) rot=(0,0,1;3.14159rad)
  Shapes = -> [Cut009,Cut010]
FEATURE [Part::Box] Box  label="Cube"
  AttacherType = Attacher::AttachEngine3D
  Height = 10
  Length = 3
  Placement = pos=(3.3,4,12) rot=(0,0,1;0rad)
  Width = 10
FEATURE [Part::Fillet] Fillet004
  Base = -> Fusion028
  Edges = 1 edges r=2: [Edge25]
FEATURE [Part::Fillet] Fillet005  label="plugHousing046"
  Base = -> Fillet004
  Edges = 1 edges r=2: [Edge8]
FEATURE [Part::Fillet] Fillet006
  Base = -> Box
  Edges = 1 edges r=2: [Edge11]
FEATURE [Part::Box] Box007  label="Cube007"
  AttacherType = Attacher::AttachEngine3D
  Height = 10
  Length = 3
  Placement = pos=(3.3,4,50) rot=(0,0,1;0rad)
  Width = 10
FEATURE [Part::Fillet] Fillet007
  Base = -> Box007
  Edges = 1 edges r=2: [Edge12]
FEATURE [Part::Box] Box008  label="Cube008"
  AttacherType = Attacher::AttachEngine3D
  Height = 28
  Length = 4
  Placement = pos=(5,0,22) rot=(0,0,1;0rad)
  Width = 10
FEATURE [Part::Fillet] Fillet008
  Base = -> Box008
  Edges = 1 edges r=1: [Edge7]
FEATURE [Part::Fillet] Fillet009
  Base = -> Fillet008
  Edges = 1 edges r=2: [Edge5]
FEATURE [Part::Fillet] Fillet010
  Base = -> Fillet009
  Edges = 1 edges r=2: [Edge2]
FEATURE [Sketcher::SketchObject] Sketch009  label="topSketch003"
  FullyConstrained = true
  sketch-geometry (4):
    g0: LineSegment StartX=16.8446 StartY=31.512 StartZ=0 EndX=16.3251 EndY=34.4666 EndZ=0
    g1: ArcOfCircle CenterX=19 CenterY=19.2524 CenterZ=0 NormalX=0 NormalY=0 NormalZ=1 AngleXU=0 Radius=15.4476 StartAngle=1.74483 EndAngle=2.72717
    g2: ArcOfCircle CenterX=19 CenterY=19.2524 CenterZ=0 NormalX=0 NormalY=0 NormalZ=1 AngleXU=0 Radius=12.4476 StartAngle=1.74483 EndAngle=2.73189
    g3: LineSegment StartX=4.86004 StartY=25.4725 StartZ=0 EndX=7.58253 EndY=24.2107 EndZ=0
  constraints (7):
    c: Block(g0)
    c: Coincident(g1,g0)
    c: Coincident(g2,g0)
    c: Coincident(g3,g1)
    c: Coincident(g3,g2)
    c: Block(g1)
    c: Block(g2)
FEATURE [Part::Extrusion] Extrude008
  Base = -> Sketch009
  Dir = (0,0,1)
  DirMode = 2
  FaceMakerClass = Part::FaceMakerBullseye
  LengthFwd = 10
  LengthRev = 0
  Placement = pos=(0,0,31) rot=(0,0,1;0rad)
  Solid = true
  Symmetric = false
FEATURE [Part::Cylinder] Cylinder020
  Angle = 360
  AttacherType = Attacher::AttachEngine3D
  Height = 20
  Placement = pos=(0,0,36.15) rot=(0,0,1;0rad)
  Radius = 8.2
FEATURE [Part::Cylinder] Cylinder021
  Angle = 360
  AttacherType = Attacher::AttachEngine3D
  Height = 10
  Placement = pos=(0,0,36.15) rot=(0,0,1;0rad)
  Radius = 4
FEATURE [Part::MultiFuse] Fusion038  label="removeToCreteHoleForPlugHousing007"
  Placement = pos=(-42,19,36) rot=(0,1,0;1.5708rad)
  Shapes = -> [Cylinder020,Cylinder021]
FEATURE [Part::Cut] Cut011
  Base = -> Extrude008
  Tool = -> Fusion038
FEATURE [Part::Fillet] Fillet011
  Base = -> Cut011
  Edges = 1 edges r=2: [Edge1]
FEATURE [Part::Fillet] Fillet012
  Base = -> Fillet011
  Edges = 1 edges r=2.5: [Edge1]
FEATURE [Part::Fillet] Fillet013
  Base = -> Fillet012
  Edges = 1 edges r=2.5: [Edge2]
FEATURE [Part::Box] Box010  label="Cube010"
  AttacherType = Attacher::AttachEngine3D
  Height = 16
  Length = 8
  Placement = pos=(12.7,31.52,28) rot=(0,0,1;0rad)
  Width = 4
FEATURE [Sketcher::SketchObject] Sketch010  label="topSketch004"
  FullyConstrained = true
  sketch-geometry (4):
    g0: LineSegment StartX=16.8446 StartY=31.512 StartZ=0 EndX=16.3251 EndY=34.4666 EndZ=0
    g1: ArcOfCircle CenterX=19 CenterY=19.2524 CenterZ=0 NormalX=0 NormalY=0 NormalZ=1 AngleXU=0 Radius=15.4476 StartAngle=1.74483 EndAngle=2.72717
    g2: ArcOfCircle CenterX=19 CenterY=19.2524 CenterZ=0 NormalX=0 NormalY=0 NormalZ=1 AngleXU=0 Radius=12.4476 StartAngle=1.74483 EndAngle=2.73189
    g3: LineSegment StartX=4.86004 StartY=25.4725 StartZ=0 EndX=7.58253 EndY=24.2107 EndZ=0
  constraints (7):
    c: Block(g0)
    c: Coincident(g1,g0)
    c: Coincident(g2,g0)
    c: Coincident(g3,g1)
    c: Coincident(g3,g2)
    c: Block(g1)
    c: Block(g2)
FEATURE [Part::Cylinder] Cylinder022
  Angle = 360
  AttacherType = Attacher::AttachEngine3D
  Height = 10
  Placement = pos=(0,0,36.15) rot=(0,0,1;0rad)
  Radius = 4
FEATURE [Sketcher::SketchObject] Sketch011  label="topSketch005"
  FullyConstrained = true
  sketch-geometry (4):
    g0: LineSegment StartX=16.8446 StartY=31.512 StartZ=0 EndX=16.3251 EndY=34.4666 EndZ=0
    g1: ArcOfCircle CenterX=19 CenterY=19.2524 CenterZ=0 NormalX=0 NormalY=0 NormalZ=1 AngleXU=0 Radius=15.4476 StartAngle=1.74483 EndAngle=2.72717
    g2: ArcOfCircle CenterX=19 CenterY=19.2524 CenterZ=0 NormalX=0 NormalY=0 NormalZ=1 AngleXU=0 Radius=12.4476 StartAngle=1.74483 EndAngle=2.73189
    g3: LineSegment StartX=4.86004 StartY=25.4725 StartZ=0 EndX=7.58253 EndY=24.2107 EndZ=0
  constraints (7):
    c: Block(g0)
    c: Coincident(g1,g0)
    c: Coincident(g2,g0)
    c: Coincident(g3,g1)
    c: Coincident(g3,g2)
    c: Block(g1)
    c: Block(g2)
FEATURE [Part::Extrusion] Extrude010
  Base = -> Sketch011
  Dir = (0,0,1)
  DirMode = 2
  FaceMakerClass = Part::FaceMakerBullseye
  LengthFwd = 10.6
  LengthRev = 0
  Placement = pos=(0,0,31) rot=(0,0,1;0rad)
  Solid = true
  Symmetric = false
FEATURE [Part::Cylinder] Cylinder023
  Angle = 360
  AttacherType = Attacher::AttachEngine3D
  Height = 20
  Placement = pos=(0,0,36.15) rot=(0,0,1;0rad)
  Radius = 8.2
FEATURE [Part::MultiFuse] Fusion039  label="removeToCreteHoleForPlugHousing008"
  Placement = pos=(-42,19,36) rot=(0,1,0;1.5708rad)
  Shapes = -> [Cylinder023,Cylinder022]
FEATURE [Part::Cut] Cut012
  Base = -> Extrude010
  Placement = pos=(0,0,-0.3) rot=(0,0,1;0rad)
  Tool = -> Fusion039
FEATURE [Part::Cut] Cut013
  Base = -> Box010
  Tool = -> Cut012
FEATURE [Part::Fillet] Fillet014
  Base = -> Cut013
  Edges = 1 edges r=0.7: [Edge13]
FEATURE [Part::Fillet] Fillet015
  Base = -> Fillet014
  Edges = 1 edges r=0.7: [Edge13]
FEATURE [Part::Fillet] Fillet016
  Base = -> Fillet015
  Edges = 1 edges r=0.7: [Edge16]
FEATURE [Part::Fillet] Fillet017
  Base = -> Fillet016
  Edges = 1 edges r=0.7: [Edge11]
FEATURE [Part::Fillet] Fillet018
  Base = -> Fillet017
  Edges = 1 edges r=0.7: [Edge10]
FEATURE [Part::Fillet] Fillet019
  Base = -> Fillet018
  Edges = 1 edges r=1.2: [Edge5]
FEATURE [Part::Fillet] Fillet020
  Base = -> Fillet019
  Edges = 1 edges r=1.2: [Edge12]
FEATURE [Part::Fillet] Fillet021
  Base = -> Fillet020
  Edges = 1 edges r=2: [Edge1]
  Placement = pos=(0.3,0,0) rot=(0,0,1;0rad)
FEATURE [Part::MultiFuse] Fusion040  label="top005"
  Shapes = -> [Cut008,Fillet021]
FEATURE [Part::MultiFuse] Fusion041  label="wireHolder"
  Shapes = -> [Fusion033,Fillet013]
FEATURE [Part::MultiFuse] Fusion042
  Shapes = -> [Fillet007,Fusion041]
FEATURE [Part::MultiFuse] Fusion043  label="wireHolder001"
  Shapes = -> [Fusion042,Fillet010]
FEATURE [Part::MultiFuse] Fusion044  label="wireHolder002"
  Shapes = -> [Fillet006,Fusion037,Fusion043]
FEATURE [Part::Feature] Face026
  shape: bbox 11 x 6 x 2e-07 mm, 1 faces, 0 solids (baked)
FEATURE [Part::Revolution] Revolve026
  Angle = 360
  Axis = (0,1,0)
  Base = (0,0,0)
  FaceMakerClass = Part::FaceMakerBullseye
  Placement = pos=(30.3,-1,19.7) rot=(0,0,1;0rad)
  Solid = false
  Source = -> Face026
  Symmetric = false
FEATURE [Sketcher::SketchObject] Sketch013  label="topSketch006"
  FullyConstrained = true
  sketch-geometry (13):
    g0: LineSegment StartX=117 StartY=19 StartZ=0 EndX=117 EndY=38 EndZ=0
    g1: ArcOfCircle CenterX=98 CenterY=19 CenterZ=0 NormalX=0 NormalY=0 NormalZ=1 AngleXU=0 Radius=19 StartAngle=5.7297 EndAngle=6.28319
    g2: LineSegment StartX=0 StartY=3 StartZ=0 EndX=0 EndY=19 EndZ=0
    g3: LineSegment StartX=19 StartY=38 StartZ=0 EndX=117 EndY=38 EndZ=0
    g4: ArcOfCircle CenterX=19 CenterY=19 CenterZ=0 NormalX=0 NormalY=0 NormalZ=1 AngleXU=0 Radius=19 StartAngle=1.5708 EndAngle=3.14159
    g5: ArcOfCircle CenterX=19 CenterY=19 CenterZ=0 NormalX=0 NormalY=0 NormalZ=1 AngleXU=0 Radius=16 StartAngle=1.5708 EndAngle=3.14159
    g6: ArcOfCircle CenterX=98 CenterY=19 CenterZ=0 NormalX=0 NormalY=0 NormalZ=1 AngleXU=0 Radius=16 StartAngle=5.60905 EndAngle=6.28319
    g7: LineSegment StartX=114 StartY=19 StartZ=0 EndX=114 EndY=35 EndZ=0
    g8: LineSegment StartX=110.5 StartY=9.01251 StartZ=0 EndX=114.163 EndY=9.01251 EndZ=0
    g9: LineSegment StartX=114 StartY=35 StartZ=0 EndX=19 EndY=35 EndZ=0
    g10: LineSegment StartX=0 StartY=3 StartZ=0 EndX=0 EndY=0 EndZ=0
    g11: LineSegment StartX=3 StartY=0 StartZ=0 EndX=0 EndY=0 EndZ=0
    g12: LineSegment StartX=3 StartY=19 StartZ=0 EndX=3 EndY=0 EndZ=0
  constraints (33):
    c: Vertical(g0)
    c: Distance(g0) = 19
    c: Block(g0)
    c: Coincident(g1,g0)
    c: Block(g1)
    c: Vertical(g2)
    c: Block(g2)
    c: Coincident(g3,g0)
    c: Horizontal(g3)
    c: Distance(g3) = 98
    c: Coincident(g4,g3)
    c: Coincident(g4,g2)
    c: Block(g4)
    c: Coincident(g5,g4)
    c: Coincident(g6,g1)
    c: Block(g6)
    c: Block(g5)
    c: Coincident(g7,g6)
    c: Vertical(g7)
    c: Coincident(g8,g6)
    c: Coincident(g8,g1)
    c: Coincident(g9,g7)
    c: Coincident(g9,g5)
    c: Horizontal(g9)
    c: Tangent(g9,g5)
    c: Coincident(g10,g2)
    c: Distance(g10) = 3
    c: Vertical(g10)
    c: Coincident(g11,g10)
    c: Horizontal(g11)
    c: Coincident(g12,g5)
    c: Coincident(g12,g11)
    c: Vertical(g12)
FEATURE [Part::Extrusion] Extrude011  label="top006"
  Base = -> Sketch013
  Dir = (0,0,1)
  DirMode = 2
  FaceMakerClass = Part::FaceMakerBullseye
  LengthFwd = 72
  LengthRev = 0
  Solid = true
  Symmetric = false
FEATURE [Sketcher::SketchObject] Sketch014
  FullyConstrained = true
  MapMode = 3
  Placement = pos=(0,0,0) rot=(1,0,0;1.5708rad)
  Support = -> [Extrude011]
  sketch-geometry (8):
    g0: Circle CenterX=80.351 CenterY=-67.6202 CenterZ=0 NormalX=0 NormalY=0 NormalZ=1 AngleXU=0 Radius=2
    g1: Circle CenterX=80.351 CenterY=-67.6202 CenterZ=0 NormalX=0 NormalY=0 NormalZ=1 AngleXU=0 Radius=3
    g2: Circle CenterX=80.351 CenterY=-4.92017 CenterZ=0 NormalX=0 NormalY=0 NormalZ=1 AngleXU=0 Radius=2
    g3: Circle CenterX=80.351 CenterY=-4.92017 CenterZ=0 NormalX=0 NormalY=0 NormalZ=1 AngleXU=0 Radius=3
    g4: Circle CenterX=23.851 CenterY=-4.92017 CenterZ=0 NormalX=0 NormalY=0 NormalZ=1 AngleXU=0 Radius=2
    g5: Circle CenterX=23.851 CenterY=-4.92017 CenterZ=0 NormalX=0 NormalY=0 NormalZ=1 AngleXU=0 Radius=3
    g6: Circle CenterX=23.851 CenterY=-67.6202 CenterZ=0 NormalX=0 NormalY=0 NormalZ=1 AngleXU=0 Radius=2
    g7: Circle CenterX=23.851 CenterY=-67.6202 CenterZ=0 NormalX=0 NormalY=0 NormalZ=1 AngleXU=0 Radius=3
  constraints (8):
    c: Block(g3)
    c: Block(g2)
    c: Block(g1)
    c: Block(g0)
    c: Block(g6)
    c: Block(g7)
    c: Block(g4)
    c: Block(g5)
FEATURE [Part::Feature] Face027
  shape: bbox 11 x 6 x 2e-07 mm, 1 faces, 0 solids (baked)
FEATURE [Part::Revolution] Revolve027
  Angle = 360
  Axis = (0,1,0)
  Base = (0,0,0)
  FaceMakerClass = Part::FaceMakerBullseye
  Placement = pos=(30.3,-1,51.7) rot=(0,0,1;0rad)
  Solid = false
  Source = -> Face027
  Symmetric = false
FEATURE [Part::Feature] Face028
  shape: bbox 11 x 6 x 2e-07 mm, 1 faces, 0 solids (baked)
FEATURE [Part::Revolution] Revolve028
  Angle = 360
  Axis = (0,1,0)
  Base = (0,0,0)
  FaceMakerClass = Part::FaceMakerBullseye
  Placement = pos=(62.3,-1,19.7) rot=(0,0,1;0rad)
  Solid = false
  Source = -> Face028
  Symmetric = false
FEATURE [Part::Feature] Face029
  shape: bbox 11 x 6 x 2e-07 mm, 1 faces, 0 solids (baked)
FEATURE [Part::Revolution] Revolve029
  Angle = 360
  Axis = (0,1,0)
  Base = (0,0,0)
  FaceMakerClass = Part::FaceMakerBullseye
  Placement = pos=(62.3,-1,51.7) rot=(0,0,1;0rad)
  Solid = false
  Source = -> Face029
  Symmetric = false
FEATURE [Part::Feature] Wire
  shape: bbox 11 x 5.2 x 2e-07 mm, 0 faces, 0 solids (baked)
FEATURE [Part::Revolution] Revolve030
  Angle = 360
  Axis = (0,1,0)
  Base = (0,0,0)
  FaceMakerClass = Part::FaceMakerBullseye
  Placement = pos=(30.3,38,19.7) rot=(0,0,1;0rad)
  Solid = true
  Source = -> Wire
  Symmetric = false
FEATURE [Part::Feature] Wire001
  shape: bbox 11 x 5.2 x 2e-07 mm, 0 faces, 0 solids (baked)
FEATURE [Part::Revolution] Revolve031
  Angle = 360
  Axis = (0,1,0)
  Base = (0,0,0)
  FaceMakerClass = Part::FaceMakerBullseye
  Placement = pos=(30.3,38,51.7) rot=(0,0,1;0rad)
  Solid = true
  Source = -> Wire001
  Symmetric = false
FEATURE [Part::Feature] Wire002
  shape: bbox 11 x 5.2 x 2e-07 mm, 0 faces, 0 solids (baked)
FEATURE [Part::Revolution] Revolve032
  Angle = 360
  Axis = (0,1,0)
  Base = (0,0,0)
  FaceMakerClass = Part::FaceMakerBullseye
  Placement = pos=(62.3,38,51.7) rot=(0,0,1;0rad)
  Solid = true
  Source = -> Wire002
  Symmetric = false
FEATURE [Part::Feature] Wire003
  shape: bbox 11 x 5.2 x 2e-07 mm, 0 faces, 0 solids (baked)
FEATURE [Part::Revolution] Revolve033
  Angle = 360
  Axis = (0,1,0)
  Base = (0,0,0)
  FaceMakerClass = Part::FaceMakerBullseye
  Placement = pos=(62.3,38,19.7) rot=(0,0,1;0rad)
  Solid = true
  Source = -> Wire003
  Symmetric = false
FEATURE [Part::MultiFuse] Fusion045  label="altRandScrewHousing"
  Shapes = -> [Revolve029,Revolve027,Revolve028,Revolve026]
FEATURE [Part::MultiFuse] Fusion046  label="fanScrewHousing"
  Shapes = -> [Revolve033,Revolve032,Revolve031,Revolve030]
FEATURE [Sketcher::SketchObject] Sketch015
  FullyConstrained = true
  sketch-geometry (17):
    g0: Circle CenterX=-3.5 CenterY=23.5 CenterZ=0 NormalX=0 NormalY=0 NormalZ=1 AngleXU=0 Radius=1
    g1: Circle CenterX=-1 CenterY=15.25 CenterZ=0 NormalX=0 NormalY=0 NormalZ=1 AngleXU=0 Radius=1
    g2: Circle CenterX=-3.5 CenterY=7 CenterZ=0 NormalX=0 NormalY=0 NormalZ=1 AngleXU=0 Radius=1
    g3: BSplineCurve PolesCount=3 KnotsCount=2 Degree=2 IsPeriodic=0
    g4: GeomPoint X=-3.5 Y=23.5 Z=0
    g5: GeomPoint X=-3.5 Y=7 Z=0
    g6: Circle CenterX=-4.8 CenterY=30.5 CenterZ=0 NormalX=0 NormalY=0 NormalZ=1 AngleXU=0 Radius=1
    g7: Circle CenterX=-3.5 CenterY=30.5 CenterZ=0 NormalX=0 NormalY=0 NormalZ=1 AngleXU=0 Radius=1
    g8: Circle CenterX=-3.5 CenterY=29.2 CenterZ=0 NormalX=0 NormalY=0 NormalZ=1 AngleXU=0 Radius=1
    g9: BSplineCurve PolesCount=3 KnotsCount=2 Degree=2 IsPeriodic=0
    g10: GeomPoint X=-4.8 Y=30.5 Z=0
    g11: GeomPoint X=-3.5 Y=29.2 Z=0
    g12: LineSegment StartX=-3.5 StartY=29.2 StartZ=0 EndX=-3.5 EndY=23.5 EndZ=0
    g13: LineSegment StartX=-4.8 StartY=30.5 StartZ=0 EndX=0 EndY=30.5 EndZ=0
    g14: LineSegment StartX=-3.5 StartY=0.3 StartZ=0 EndX=0 EndY=0.3 EndZ=0
    g15: LineSegment StartX=-3.5 StartY=0.3 StartZ=0 EndX=-3.5 EndY=7 EndZ=0
    g16: LineSegment StartX=0 StartY=0.3 StartZ=0 EndX=0 EndY=30.5 EndZ=0
  constraints (33):
    c: Weight(g0) = 1
    c: Equal(g0,g1)
    c: Equal(g0,g2)
    c: InternalAlignment(g0,g3)
    c: InternalAlignment(g1,g3)
    c: InternalAlignment(g2,g3)
    c: InternalAlignment(g4,g3)
    c: InternalAlignment(g5,g3)
    c: Block(g3)
    c: Weight(g6) = 1
    c: Equal(g6,g7)
    c: Equal(g6,g8)
    c: InternalAlignment(g6,g9)
    c: InternalAlignment(g7,g9)
    c: InternalAlignment(g8,g9)
    c: InternalAlignment(g10,g9)
    c: InternalAlignment(g11,g9)
    c: Block(g9)
    c: Coincident(g12,g9)
    c: Coincident(g12,g3)
    c: Vertical(g12)
    c: Coincident(g13,g9)
    c: Horizontal(g13)
    c: Distance(g13) = 4.8
    c: Horizontal(g14)
    c: Block(g14)
    c: Coincident(g15,g14)
    c: Coincident(g15,g3)
    c: Vertical(g15)
    c: Coincident(g16,g14)
    c: Coincident(g16,g13)
    c: Vertical(g16)
    c: Tangent(g16,g1)
FEATURE [Sketcher::SketchObject] Sketch016
  FullyConstrained = true
  sketch-geometry (16):
    g0: Circle CenterX=-3.5 CenterY=23.5 CenterZ=0 NormalX=0 NormalY=0 NormalZ=1 AngleXU=0 Radius=1
    g1: Circle CenterX=-1 CenterY=15.25 CenterZ=0 NormalX=0 NormalY=0 NormalZ=1 AngleXU=0 Radius=1
    g2: Circle CenterX=-3.5 CenterY=7 CenterZ=0 NormalX=0 NormalY=0 NormalZ=1 AngleXU=0 Radius=1
    g3: BSplineCurve PolesCount=3 KnotsCount=2 Degree=2 IsPeriodic=0
    g4: GeomPoint X=-3.5 Y=23.5 Z=0
    g5: GeomPoint X=-3.5 Y=7 Z=0
    g6: LineSegment StartX=-3.5 StartY=28.2 StartZ=0 EndX=-3.5 EndY=23.5 EndZ=0
    g7: LineSegment StartX=0 StartY=29.5 StartZ=0 EndX=0 EndY=30 EndZ=0
    g8: LineSegment StartX=-3.5 StartY=28.2 StartZ=0 EndX=-3.5 EndY=30 EndZ=0
    g9: LineSegment StartX=0 StartY=30 StartZ=0 EndX=0 EndY=30.5 EndZ=0
    g10: LineSegment StartX=0 StartY=30.5 StartZ=0 EndX=-3.5 EndY=30.5 EndZ=0
    g11: LineSegment StartX=-3.5 StartY=30.5 StartZ=0 EndX=-3.5 EndY=30 EndZ=0
    g12: LineSegment StartX=0 StartY=29.5 StartZ=0 EndX=0 EndY=5 EndZ=0
    g13: LineSegment StartX=-3.5 StartY=0.3 StartZ=0 EndX=-3.5 EndY=7 EndZ=0
    g14: LineSegment StartX=-3.5 StartY=0.3 StartZ=0 EndX=0 EndY=0.3 EndZ=0
    g15: LineSegment StartX=0 StartY=5 StartZ=0 EndX=0 EndY=0.3 EndZ=0
  constraints (39):
    c: Weight(g0) = 1
    c: Equal(g0,g1)
    c: Equal(g0,g2)
    c: InternalAlignment(g0,g3)
    c: InternalAlignment(g1,g3)
    c: InternalAlignment(g2,g3)
    c: InternalAlignment(g4,g3)
    c: InternalAlignment(g5,g3)
    c: Block(g3)
    c: Coincident(g6,g3)
    c: Vertical(g6)
    c: Vertical(g7)
    c: Distance(g7) = 0.5
    c: Coincident(g8,g6)
    c: Vertical(g8)
    c: Block(g6)
    c: Block(g7)
    c: Vertical(g9)
    c: Equal(g7,g9) = 0.5
    c: Block(g9)
    c: Coincident(g9,g7)
    c: Horizontal(g10)
    c: Coincident(g10,g9)
    c: Coincident(g11,g10)
    c: Coincident(g11,g8)
    c: Vertical(g11)
    c: Block(g11)
    c: Coincident(g12,g7)
    c: Vertical(g12)
    c: Coincident(g13,g3)
    c: Vertical(g13)
    c: Distance(g13) = 6.7
    c: Coincident(g14,g13)
    c: Horizontal(g14)
    c: Block(g14)
    c: Coincident(g15,g12)
    c: Coincident(g15,g14)
    c: Vertical(g15)
    c: Block(g15)
FEATURE [Sketcher::SketchObject] Sketch017
  FullyConstrained = true
  sketch-geometry (11):
    g0: LineSegment StartX=-3.5 StartY=1e-16 StartZ=0 EndX=-1.6 EndY=1e-16 EndZ=0
    g1: LineSegment StartX=-1.6 StartY=1e-16 StartZ=0 EndX=-1.6 EndY=1.5 EndZ=0
    g2: LineSegment StartX=-3.5 StartY=1.5 StartZ=0 EndX=-1.6 EndY=1.5 EndZ=0
    g3: LineSegment StartX=-3.5 StartY=1e-16 StartZ=0 EndX=-4.8 EndY=1e-16 EndZ=0
    g4: Circle CenterX=-3.5 CenterY=1.3 CenterZ=0 NormalX=0 NormalY=0 NormalZ=1 AngleXU=0 Radius=1
    g5: Circle CenterX=-3.5 CenterY=1e-16 CenterZ=0 NormalX=0 NormalY=0 NormalZ=1 AngleXU=0 Radius=1
    g6: Circle CenterX=-4.8 CenterY=1e-16 CenterZ=0 NormalX=0 NormalY=0 NormalZ=1 AngleXU=0 Radius=1
    g7: BSplineCurve PolesCount=3 KnotsCount=2 Degree=2 IsPeriodic=0
    g8: GeomPoint X=-3.5 Y=1.3 Z=0
    g9: GeomPoint X=-4.8 Y=1e-16 Z=0
    g10: LineSegment StartX=-3.5 StartY=1.3 StartZ=0 EndX=-3.5 EndY=1.5 EndZ=0
  constraints (24):
    c: Horizontal(g0)
    c: Distance(g0) = 1.9
    c: Block(g0)
    c: Coincident(g1,g0)
    c: Vertical(g1)
    c: Coincident(g2,g1)
    c: Horizontal(g2)
    c: Coincident(g3,g0)
    c: Horizontal(g3)
    c: Distance(g3) = 1.3
    c: Weight(g4) = 1
    c: Equal(g4,g5)
    c: Coincident(g5,g0)
    c: Equal(g4,g6)
    c: Coincident(g7,g3)
    c: InternalAlignment(g4,g7)
    c: InternalAlignment(g5,g7)
    c: InternalAlignment(g6,g7)
    c: InternalAlignment(g8,g7)
    c: InternalAlignment(g9,g7)
    c: Coincident(g10,g7)
    c: Coincident(g10,g2)
    c: Vertical(g10)
    c: Block(g10)
FEATURE [Part::Feature] Face035
  shape: bbox 3.2 x 1.5 x 2e-07 mm, 1 faces, 0 solids (baked)
FEATURE [Part::Revolution] Revolve039  label="backCaseScrewRetainer"
  Angle = 360
  Axis = (0,1,0)
  Base = (0,0,0)
  FaceMakerClass = Part::FaceMakerBullseye
  Placement = pos=(12.5,3,62) rot=(0,0,1;0rad)
  Solid = false
  Source = -> Face035
  Symmetric = false
FEATURE [Part::Feature] Face036
  shape: bbox 3.2 x 1.5 x 2e-07 mm, 1 faces, 0 solids (baked)
FEATURE [Part::Feature] Face039
  shape: bbox 4.8 x 30.2 x 2e-07 mm, 1 faces, 0 solids (baked)
FEATURE [Part::Revolution] Revolve043  label="frontCaseScrewPost002"
  Angle = 360
  Axis = (0,1,0)
  Base = (0,0,0)
  FaceMakerClass = Part::FaceMakerBullseye
  Placement = pos=(89.5,4.5,3.5) rot=(0,0,1;0rad)
  Solid = false
  Source = -> Face039
  Symmetric = false
FEATURE [Part::Feature] Face042
  shape: bbox 4.8 x 30.2 x 2e-07 mm, 1 faces, 0 solids (baked)
FEATURE [Part::Revolution] Revolve046  label="frontCaseScrewPost003"
  Angle = 360
  Axis = (0,1,0)
  Base = (0,0,0)
  FaceMakerClass = Part::FaceMakerBullseye
  Placement = pos=(89.5,4.5,68.5) rot=(0,0,1;0rad)
  Solid = false
  Source = -> Face042
  Symmetric = false
FEATURE [Part::Feature] Face043
  shape: bbox 3.2 x 1.5 x 2e-07 mm, 1 faces, 0 solids (baked)
FEATURE [Part::Revolution] Revolve047  label="frontCaseScrewRetainer002"
  Angle = 360
  Axis = (0,1,0)
  Base = (0,0,0)
  FaceMakerClass = Part::FaceMakerBullseye
  Placement = pos=(89.5,3,68.5) rot=(0,0,1;0rad)
  Solid = false
  Source = -> Face043
  Symmetric = false
FEATURE [Part::Feature] Face044
  shape: bbox 3.2 x 1.5 x 2e-07 mm, 1 faces, 0 solids (baked)
FEATURE [Part::Revolution] Revolve048  label="frontCaseScrewRetainer003"
  Angle = 360
  Axis = (0,1,0)
  Base = (0,0,0)
  FaceMakerClass = Part::FaceMakerBullseye
  Placement = pos=(89.5,3,3.5) rot=(0,0,1;0rad)
  Solid = false
  Source = -> Face044
  Symmetric = false
FEATURE [App::MeasureDistance] Distance002  label="Distance: 1.67 mm"
  Distance = 1.66921
  P1 = (99.2361,4.7524,71.7)
  P2 = (99.2347,6.42161,71.7)
FEATURE [Sketcher::SketchObject] Sketch018
  FullyConstrained = true
  sketch-geometry (7):
    g0: LineSegment StartX=0 StartY=0 StartZ=0 EndX=0 EndY=6 EndZ=0
    g1: Circle CenterX=0 CenterY=0 CenterZ=0 NormalX=0 NormalY=0 NormalZ=1 AngleXU=0 Radius=1
    g2: Circle CenterX=8 CenterY=6 CenterZ=0 NormalX=0 NormalY=0 NormalZ=1 AngleXU=0 Radius=1
    g3: BSplineCurve PolesCount=3 KnotsCount=2 Degree=2 IsPeriodic=0
    g4: GeomPoint X=0 Y=0 Z=0
    g5: GeomPoint X=8 Y=6 Z=0
    g6: LineSegment StartX=0 StartY=6 StartZ=0 EndX=8 EndY=6 EndZ=0
  constraints (14):
    c: Coincident(g0,g-1)
    c: Distance(g0) = 6
    c: Vertical(g0)
    c: Coincident(g3,g0)
    c: Weight(g1) = 1
    c: Equal(g1,g2)
    c: InternalAlignment(g1,g3)
    c: InternalAlignment(g2,g3)
    c: InternalAlignment(g4,g3)
    c: InternalAlignment(g5,g3)
    c: Block(g3)
    c: Coincident(g6,g0)
    c: Coincident(g6,g3)
    c: Horizontal(g6)
FEATURE [Part::Extrusion] Extrude012  label="caseScrewPillarBracket"
  Base = -> Sketch018
  Dir = (0,0,1)
  DirMode = 2
  FaceMakerClass = Part::FaceMakerBullseye
  LengthFwd = 2.4
  LengthRev = 0
  Placement = pos=(15.76,29,8.8) rot=(0,1,0;0rad)
  Solid = true
  Symmetric = false
FEATURE [Sketcher::SketchObject] Sketch019
  FullyConstrained = true
  sketch-geometry (7):
    g0: LineSegment StartX=0 StartY=0 StartZ=0 EndX=0 EndY=6 EndZ=0
    g1: Circle CenterX=0 CenterY=0 CenterZ=0 NormalX=0 NormalY=0 NormalZ=1 AngleXU=0 Radius=1
    g2: Circle CenterX=8 CenterY=6 CenterZ=0 NormalX=0 NormalY=0 NormalZ=1 AngleXU=0 Radius=1
    g3: BSplineCurve PolesCount=3 KnotsCount=2 Degree=2 IsPeriodic=0
    g4: GeomPoint X=0 Y=0 Z=0
    g5: GeomPoint X=8 Y=6 Z=0
    g6: LineSegment StartX=0 StartY=6 StartZ=0 EndX=8 EndY=6 EndZ=0
  constraints (14):
    c: Coincident(g0,g-1)
    c: Distance(g0) = 6
    c: Vertical(g0)
    c: Coincident(g3,g0)
    c: Weight(g1) = 1
    c: Equal(g1,g2)
    c: InternalAlignment(g1,g3)
    c: InternalAlignment(g2,g3)
    c: InternalAlignment(g4,g3)
    c: InternalAlignment(g5,g3)
    c: Block(g3)
    c: Coincident(g6,g0)
    c: Coincident(g6,g3)
    c: Horizontal(g6)
FEATURE [Part::Extrusion] Extrude013  label="caseScrewPillarBracket001"
  Base = -> Sketch019
  Dir = (0,0,1)
  DirMode = 2
  FaceMakerClass = Part::FaceMakerBullseye
  LengthFwd = 2.4
  LengthRev = 0
  Placement = pos=(15.76,29,60.8) rot=(0,0,1;0rad)
  Solid = true
  Symmetric = false
FEATURE [Sketcher::SketchObject] Sketch020
  FullyConstrained = true
  sketch-geometry (7):
    g0: LineSegment StartX=0 StartY=0 StartZ=0 EndX=0 EndY=6 EndZ=0
    g1: Circle CenterX=0 CenterY=0 CenterZ=0 NormalX=0 NormalY=0 NormalZ=1 AngleXU=0 Radius=1
    g2: Circle CenterX=8 CenterY=6 CenterZ=0 NormalX=0 NormalY=0 NormalZ=1 AngleXU=0 Radius=1
    g3: BSplineCurve PolesCount=3 KnotsCount=2 Degree=2 IsPeriodic=0
    g4: GeomPoint X=0 Y=0 Z=0
    g5: GeomPoint X=8 Y=6 Z=0
    g6: LineSegment StartX=0 StartY=6 StartZ=0 EndX=8 EndY=6 EndZ=0
  constraints (14):
    c: Coincident(g0,g-1)
    c: Distance(g0) = 6
    c: Vertical(g0)
    c: Coincident(g3,g0)
    c: Weight(g1) = 1
    c: Equal(g1,g2)
    c: InternalAlignment(g1,g3)
    c: InternalAlignment(g2,g3)
    c: InternalAlignment(g4,g3)
    c: InternalAlignment(g5,g3)
    c: Block(g3)
    c: Coincident(g6,g0)
    c: Coincident(g6,g3)
    c: Horizontal(g6)
FEATURE [Part::Extrusion] Extrude014  label="caseScrewPillarBracket002"
  Base = -> Sketch020
  Dir = (0,0,1)
  DirMode = 2
  FaceMakerClass = Part::FaceMakerBullseye
  LengthFwd = 2.4
  LengthRev = 0
  Placement = pos=(13.7,29,13.26) rot=(0,-1,0;1.5708rad)
  Solid = true
  Symmetric = false
FEATURE [Sketcher::SketchObject] Sketch021
  FullyConstrained = true
  sketch-geometry (7):
    g0: LineSegment StartX=0 StartY=0 StartZ=0 EndX=0 EndY=6 EndZ=0
    g1: Circle CenterX=0 CenterY=0 CenterZ=0 NormalX=0 NormalY=0 NormalZ=1 AngleXU=0 Radius=1
    g2: Circle CenterX=8 CenterY=6 CenterZ=0 NormalX=0 NormalY=0 NormalZ=1 AngleXU=0 Radius=1
    g3: BSplineCurve PolesCount=3 KnotsCount=2 Degree=2 IsPeriodic=0
    g4: GeomPoint X=0 Y=0 Z=0
    g5: GeomPoint X=8 Y=6 Z=0
    g6: LineSegment StartX=0 StartY=6 StartZ=0 EndX=8 EndY=6 EndZ=0
  constraints (14):
    c: Coincident(g0,g-1)
    c: Distance(g0) = 6
    c: Vertical(g0)
    c: Coincident(g3,g0)
    c: Weight(g1) = 1
    c: Equal(g1,g2)
    c: InternalAlignment(g1,g3)
    c: InternalAlignment(g2,g3)
    c: InternalAlignment(g4,g3)
    c: InternalAlignment(g5,g3)
    c: Block(g3)
    c: Coincident(g6,g0)
    c: Coincident(g6,g3)
    c: Horizontal(g6)
FEATURE [Part::Extrusion] Extrude015  label="caseScrewPillarBracket003"
  Base = -> Sketch021
  Dir = (0,0,1)
  DirMode = 2
  FaceMakerClass = Part::FaceMakerBullseye
  LengthFwd = 2.4
  LengthRev = 0
  Placement = pos=(11.3,29,58.74) rot=(0,1,0;1.5708rad)
  Solid = true
  Symmetric = false
FEATURE [Sketcher::SketchObject] Sketch022
  FullyConstrained = true
  sketch-geometry (7):
    g0: LineSegment StartX=0 StartY=0 StartZ=0 EndX=0 EndY=6 EndZ=0
    g1: Circle CenterX=0 CenterY=0 CenterZ=0 NormalX=0 NormalY=0 NormalZ=1 AngleXU=0 Radius=1
    g2: Circle CenterX=8 CenterY=6 CenterZ=0 NormalX=0 NormalY=0 NormalZ=1 AngleXU=0 Radius=1
    g3: BSplineCurve PolesCount=3 KnotsCount=2 Degree=2 IsPeriodic=0
    g4: GeomPoint X=0 Y=0 Z=0
    g5: GeomPoint X=8 Y=6 Z=0
    g6: LineSegment StartX=0 StartY=6 StartZ=0 EndX=8 EndY=6 EndZ=0
  constraints (14):
    c: Coincident(g0,g-1)
    c: Distance(g0) = 6
    c: Vertical(g0)
    c: Coincident(g3,g0)
    c: Weight(g1) = 1
    c: Equal(g1,g2)
    c: InternalAlignment(g1,g3)
    c: InternalAlignment(g2,g3)
    c: InternalAlignment(g4,g3)
    c: InternalAlignment(g5,g3)
    c: Block(g3)
    c: Coincident(g6,g0)
    c: Coincident(g6,g3)
    c: Horizontal(g6)
FEATURE [Part::Extrusion] Extrude016  label="caseScrewPillarBracket004"
  Base = -> Sketch022
  Dir = (0,0,1)
  DirMode = 2
  FaceMakerClass = Part::FaceMakerBullseye
  LengthFwd = 2.4
  LengthRev = 0
  Placement = pos=(88.3,29,65.23) rot=(0,1,0;1.5708rad)
  Solid = true
  Symmetric = false
FEATURE [Sketcher::SketchObject] Sketch023
  FullyConstrained = true
  sketch-geometry (7):
    g0: LineSegment StartX=0 StartY=0 StartZ=0 EndX=0 EndY=6 EndZ=0
    g1: Circle CenterX=0 CenterY=0 CenterZ=0 NormalX=0 NormalY=0 NormalZ=1 AngleXU=0 Radius=1
    g2: Circle CenterX=8 CenterY=6 CenterZ=0 NormalX=0 NormalY=0 NormalZ=1 AngleXU=0 Radius=1
    g3: BSplineCurve PolesCount=3 KnotsCount=2 Degree=2 IsPeriodic=0
    g4: GeomPoint X=0 Y=0 Z=0
    g5: GeomPoint X=8 Y=6 Z=0
    g6: LineSegment StartX=0 StartY=6 StartZ=0 EndX=8 EndY=6 EndZ=0
  constraints (14):
    c: Coincident(g0,g-1)
    c: Distance(g0) = 6
    c: Vertical(g0)
    c: Coincident(g3,g0)
    c: Weight(g1) = 1
    c: Equal(g1,g2)
    c: InternalAlignment(g1,g3)
    c: InternalAlignment(g2,g3)
    c: InternalAlignment(g4,g3)
    c: InternalAlignment(g5,g3)
    c: Block(g3)
    c: Coincident(g6,g0)
    c: Coincident(g6,g3)
    c: Horizontal(g6)
FEATURE [Part::Extrusion] Extrude017  label="caseScrewPillarBracket005"
  Base = -> Sketch023
  Dir = (0,0,1)
  DirMode = 2
  FaceMakerClass = Part::FaceMakerBullseye
  LengthFwd = 2.4
  LengthRev = 0
  Placement = pos=(90.7,29,6.77) rot=(0,-1,0;1.5708rad)
  Solid = true
  Symmetric = false
FEATURE [Sketcher::SketchObject] Sketch024
  FullyConstrained = true
  sketch-geometry (7):
    g0: LineSegment StartX=0 StartY=0 StartZ=0 EndX=0 EndY=6 EndZ=0
    g1: Circle CenterX=0 CenterY=0 CenterZ=0 NormalX=0 NormalY=0 NormalZ=1 AngleXU=0 Radius=1
    g2: Circle CenterX=8 CenterY=6 CenterZ=0 NormalX=0 NormalY=0 NormalZ=1 AngleXU=0 Radius=1
    g3: BSplineCurve PolesCount=3 KnotsCount=2 Degree=2 IsPeriodic=0
    g4: GeomPoint X=0 Y=0 Z=0
    g5: GeomPoint X=8 Y=6 Z=0
    g6: LineSegment StartX=0 StartY=6 StartZ=0 EndX=8 EndY=6 EndZ=0
  constraints (14):
    c: Coincident(g0,g-1)
    c: Distance(g0) = 6
    c: Vertical(g0)
    c: Coincident(g3,g0)
    c: Weight(g1) = 1
    c: Equal(g1,g2)
    c: InternalAlignment(g1,g3)
    c: InternalAlignment(g2,g3)
    c: InternalAlignment(g4,g3)
    c: InternalAlignment(g5,g3)
    c: Block(g3)
    c: Coincident(g6,g0)
    c: Coincident(g6,g3)
    c: Horizontal(g6)
FEATURE [Part::Extrusion] Extrude018  label="caseScrewPillarBracket006"
  Base = -> Sketch024
  Dir = (0,0,1)
  DirMode = 2
  FaceMakerClass = Part::FaceMakerBullseye
  LengthFwd = 2.4
  LengthRev = 0
  Placement = pos=(103.7,29,6.77) rot=(0,-1,0;1.5708rad)
  Solid = true
  Symmetric = false
FEATURE [Sketcher::SketchObject] Sketch025
  FullyConstrained = true
  sketch-geometry (7):
    g0: LineSegment StartX=0 StartY=0 StartZ=0 EndX=0 EndY=6 EndZ=0
    g1: Circle CenterX=0 CenterY=0 CenterZ=0 NormalX=0 NormalY=0 NormalZ=1 AngleXU=0 Radius=1
    g2: Circle CenterX=8 CenterY=6 CenterZ=0 NormalX=0 NormalY=0 NormalZ=1 AngleXU=0 Radius=1
    g3: BSplineCurve PolesCount=3 KnotsCount=2 Degree=2 IsPeriodic=0
    g4: GeomPoint X=0 Y=0 Z=0
    g5: GeomPoint X=8 Y=6 Z=0
    g6: LineSegment StartX=0 StartY=6 StartZ=0 EndX=8 EndY=6 EndZ=0
  constraints (14):
    c: Coincident(g0,g-1)
    c: Distance(g0) = 6
    c: Vertical(g0)
    c: Coincident(g3,g0)
    c: Weight(g1) = 1
    c: Equal(g1,g2)
    c: InternalAlignment(g1,g3)
    c: InternalAlignment(g2,g3)
    c: InternalAlignment(g4,g3)
    c: InternalAlignment(g5,g3)
    c: Block(g3)
    c: Coincident(g6,g0)
    c: Coincident(g6,g3)
    c: Horizontal(g6)
FEATURE [Part::Extrusion] Extrude019  label="caseScrewPillarBracket007"
  Base = -> Sketch025
  Dir = (0,0,1)
  DirMode = 2
  FaceMakerClass = Part::FaceMakerBullseye
  LengthFwd = 2.4
  LengthRev = 0
  Placement = pos=(101.3,29,65.23) rot=(0,1,0;1.5708rad)
  Solid = true
  Symmetric = false
FEATURE [Part::Box] Box011  label="frontCaseScrewPillarBracket"
  AttacherType = Attacher::AttachEngine3D
  Height = 2.4
  Length = 16
  Placement = pos=(87,28,2.3) rot=(0,0,1;0rad)
  Width = 7
FEATURE [Part::Box] Box012  label="frontCaseScrewPillarBracket001"
  AttacherType = Attacher::AttachEngine3D
  Height = 2.4
  Length = 16
  Placement = pos=(87,28,67.3) rot=(0,0,1;0rad)
  Width = 7
FEATURE [Sketcher::SketchObject] Sketch026
  FullyConstrained = true
  sketch-geometry (17):
    g0: Circle CenterX=-3.5 CenterY=23.5 CenterZ=0 NormalX=0 NormalY=0 NormalZ=1 AngleXU=0 Radius=1
    g1: Circle CenterX=-1 CenterY=15.25 CenterZ=0 NormalX=0 NormalY=0 NormalZ=1 AngleXU=0 Radius=1
    g2: Circle CenterX=-3.5 CenterY=7 CenterZ=0 NormalX=0 NormalY=0 NormalZ=1 AngleXU=0 Radius=1
    g3: BSplineCurve PolesCount=3 KnotsCount=2 Degree=2 IsPeriodic=0
    g4: GeomPoint X=-3.5 Y=23.5 Z=0
    g5: GeomPoint X=-3.5 Y=7 Z=0
    g6: Circle CenterX=-4.8 CenterY=30.5 CenterZ=0 NormalX=0 NormalY=0 NormalZ=1 AngleXU=0 Radius=1
    g7: Circle CenterX=-3.5 CenterY=30.5 CenterZ=0 NormalX=0 NormalY=0 NormalZ=1 AngleXU=0 Radius=1
    g8: Circle CenterX=-3.5 CenterY=29.2 CenterZ=0 NormalX=0 NormalY=0 NormalZ=1 AngleXU=0 Radius=1
    g9: BSplineCurve PolesCount=3 KnotsCount=2 Degree=2 IsPeriodic=0
    g10: GeomPoint X=-4.8 Y=30.5 Z=0
    g11: GeomPoint X=-3.5 Y=29.2 Z=0
    g12: LineSegment StartX=-3.5 StartY=29.2 StartZ=0 EndX=-3.5 EndY=23.5 EndZ=0
    g13: LineSegment StartX=-4.8 StartY=30.5 StartZ=0 EndX=0 EndY=30.5 EndZ=0
    g14: LineSegment StartX=-3.5 StartY=5 StartZ=0 EndX=-3.5 EndY=7 EndZ=0
    g15: LineSegment StartX=0 StartY=5 StartZ=0 EndX=0 EndY=30.5 EndZ=0
    g16: LineSegment StartX=-3.5 StartY=5 StartZ=0 EndX=0 EndY=5 EndZ=0
  constraints (33):
    c: Weight(g0) = 1
    c: Equal(g0,g1)
    c: Equal(g0,g2)
    c: InternalAlignment(g0,g3)
    c: InternalAlignment(g1,g3)
    c: InternalAlignment(g2,g3)
    c: InternalAlignment(g4,g3)
    c: InternalAlignment(g5,g3)
    c: Block(g3)
    c: Weight(g6) = 1
    c: Equal(g6,g7)
    c: Equal(g6,g8)
    c: InternalAlignment(g6,g9)
    c: InternalAlignment(g7,g9)
    c: InternalAlignment(g8,g9)
    c: InternalAlignment(g10,g9)
    c: InternalAlignment(g11,g9)
    c: Block(g9)
    c: Coincident(g12,g9)
    c: Coincident(g12,g3)
    c: Vertical(g12)
    c: Coincident(g13,g9)
    c: Horizontal(g13)
    c: Distance(g13) = 4.8
    c: Coincident(g14,g3)
    c: Vertical(g14)
    c: Coincident(g15,g13)
    c: Vertical(g15)
    c: Tangent(g15,g1)
    c: Distance(g14) = 2
    c: Coincident(g16,g14)
    c: Horizontal(g16)
    c: Coincident(g15,g16)
FEATURE [Part::Feature] Face050
  shape: bbox 4.8 x 25.5 x 2e-07 mm, 1 faces, 0 solids (baked)
FEATURE [Part::Revolution] Revolve054  label="moreFrontCaseScrewPost001"
  Angle = 360
  Axis = (0,1,0)
  Base = (0,0,0)
  FaceMakerClass = Part::FaceMakerBullseye
  Placement = pos=(102.5,4.5,3.5) rot=(0,0,1;0rad)
  Solid = false
  Source = -> Face050
  Symmetric = false
FEATURE [Part::Feature] Face051
  shape: bbox 4.8 x 25.5 x 2e-07 mm, 1 faces, 0 solids (baked)
FEATURE [Part::Revolution] Revolve055  label="moreFrontCaseScrewPost002"
  Angle = 360
  Axis = (0,1,0)
  Base = (0,0,0)
  FaceMakerClass = Part::FaceMakerBullseye
  Placement = pos=(102.5,4.5,68.5) rot=(0,0,1;0rad)
  Solid = false
  Source = -> Face051
  Symmetric = false
FEATURE [Sketcher::SketchObject] Sketch027
  FullyConstrained = true
  sketch-geometry (10):
    g0: LineSegment StartX=-1.6 StartY=4.7 StartZ=0 EndX=-1.6 EndY=1.7 EndZ=0
    g1: LineSegment StartX=-3.5 StartY=4.7 StartZ=0 EndX=-1.6 EndY=4.7 EndZ=0
    g2: LineSegment StartX=-1.6 StartY=1.7 StartZ=0 EndX=-1.6 EndY=1.5 EndZ=0
    g3: LineSegment StartX=-1.6 StartY=1.5 StartZ=0 EndX=-5.2 EndY=1.5 EndZ=0
    g4: Circle CenterX=-3.5 CenterY=4.7 CenterZ=0 NormalX=0 NormalY=0 NormalZ=1 AngleXU=0 Radius=1
    g5: Circle CenterX=-3.59627 CenterY=2.99743 CenterZ=0 NormalX=0 NormalY=0 NormalZ=1 AngleXU=0 Radius=1
    g6: Circle CenterX=-5.2 CenterY=1.5 CenterZ=0 NormalX=0 NormalY=0 NormalZ=1 AngleXU=0 Radius=1
    g7: BSplineCurve PolesCount=3 KnotsCount=2 Degree=2 IsPeriodic=0
    g8: GeomPoint X=-3.5 Y=4.7 Z=0
    g9: GeomPoint X=-5.2 Y=1.5 Z=0
  constraints (23):
    c: Vertical(g0)
    c: Distance(g0) = 3
    c: Coincident(g1,g0)
    c: Horizontal(g1)
    c: Block(g0)
    c: Block(g1)
    c: Coincident(g2,g0)
    c: Vertical(g2)
    c: Distance(g2) = 0.2
    c: Coincident(g3,g2)
    c: Horizontal(g3)
    c: Block(g3)
    c: Coincident(g7,g1)
    c: Weight(g4) = 1
    c: Equal(g4,g5)
    c: Equal(g4,g6)
    c: Coincident(g7,g3)
    c: InternalAlignment(g4,g7)
    c: InternalAlignment(g5,g7)
    c: InternalAlignment(g6,g7)
    c: InternalAlignment(g8,g7)
    c: InternalAlignment(g9,g7)
    c: Block(g7)
FEATURE [Sketcher::SketchObject] Sketch028
  FullyConstrained = true
  sketch-geometry (18):
    g0: LineSegment StartX=0 StartY=3e-16 StartZ=0 EndX=0 EndY=1.7 EndZ=0
    g1: LineSegment StartX=-3.5 StartY=0 StartZ=0 EndX=-3.5 EndY=0.9 EndZ=0
    g2: Circle CenterX=-2.7 CenterY=1.7 CenterZ=0 NormalX=0 NormalY=0 NormalZ=1 AngleXU=0 Radius=1
    g3: Circle CenterX=-3.5 CenterY=1.7 CenterZ=0 NormalX=0 NormalY=0 NormalZ=1 AngleXU=0 Radius=1
    g4: Circle CenterX=-3.5 CenterY=0.9 CenterZ=0 NormalX=0 NormalY=0 NormalZ=1 AngleXU=0 Radius=1
    g5: BSplineCurve PolesCount=3 KnotsCount=2 Degree=2 IsPeriodic=0
    g6: GeomPoint X=-2.7 Y=1.7 Z=0
    g7: GeomPoint X=-3.5 Y=0.9 Z=0
    g8: LineSegment StartX=-3.5 StartY=0 StartZ=0 EndX=-3.5 EndY=-7 EndZ=0
    g9: LineSegment StartX=0 StartY=3e-16 StartZ=0 EndX=0 EndY=-7 EndZ=0
    g10: LineSegment StartX=-3.5 StartY=-7 StartZ=0 EndX=0 EndY=-7 EndZ=0
    g11: LineSegment StartX=-2.7 StartY=1.7 StartZ=0 EndX=-1.6 EndY=1.7 EndZ=0
    g12: LineSegment StartX=0 StartY=1.7 StartZ=0 EndX=0 EndY=4.5 EndZ=0
    g13: LineSegment StartX=0 StartY=4.5 StartZ=0 EndX=0 EndY=10.8 EndZ=0
    g14: LineSegment StartX=0 StartY=10.8 StartZ=0 EndX=-2 EndY=10.8 EndZ=0
    g15: LineSegment StartX=-1.6 StartY=4.7 StartZ=0 EndX=-1.6 EndY=1.7 EndZ=0
    g16: LineSegment StartX=-1.6 StartY=4.7 StartZ=0 EndX=-2 EndY=4.7 EndZ=0
    g17: LineSegment StartX=-2 StartY=4.7 StartZ=0 EndX=-2 EndY=10.8 EndZ=0
  constraints (44):
    c: Vertical(g0)
    c: Vertical(g1)
    c: Distance(g1) = 0.9
    c: Block(g0)
    c: Distance(g0) = 1.7
    c: Weight(g2) = 1
    c: Equal(g2,g3)
    c: Equal(g2,g4)
    c: Coincident(g5,g1)
    c: InternalAlignment(g2,g5)
    c: InternalAlignment(g3,g5)
    c: InternalAlignment(g4,g5)
    c: InternalAlignment(g6,g5)
    c: InternalAlignment(g7,g5)
    c: Block(g5)
    c: Coincident(g8,g1)
    c: Vertical(g8)
    c: Distance(g8) = 7
    c: Vertical(g9)
    c: Equal(g8,g9) = 7
    c: Coincident(g9,g0)
    c: Coincident(g10,g8)
    c: Coincident(g10,g9)
    c: Horizontal(g10)
    c: Coincident(g11,g5)
    c: Horizontal(g11)
    c: Coincident(g12,g0)
    c: Vertical(g12)
    c: Distance(g12) = 2.8
    c: Coincident(g13,g12)
    c: Vertical(g13)
    c: Distance(g13) = 6.3
    c: Coincident(g14,g13)
    c: Horizontal(g14)
    c: Distance(g14) = 2
    c: Vertical(g15)
    c: Distance(g15) = 3
    c: Block(g11)
    c: Coincident(g15,g11)
    c: Coincident(g16,g15)
    c: Horizontal(g16)
    c: Coincident(g17,g16)
    c: Coincident(g17,g14)
    c: Vertical(g17)
FEATURE [Part::Revolution] Revolve040  label="backCaseScrewRetainer001"
  Angle = 360
  Axis = (0,1,0)
  Base = (0,0,0)
  FaceMakerClass = Part::FaceMakerBullseye
  Placement = pos=(12.5,3,10) rot=(0,0,1;0rad)
  Solid = false
  Source = -> Face036
  Symmetric = false
FEATURE [Part::Feature] Face055
  shape: bbox 3.5 x 30.2 x 2e-07 mm, 1 faces, 0 solids (baked)
FEATURE [Part::Revolution] Revolve059  label="backCaseScrewPost"
  Angle = 360
  Axis = (0,1,0)
  Base = (0,0,0)
  FaceMakerClass = Part::FaceMakerBullseye
  Placement = pos=(12.5,4.5,10) rot=(0,0,1;0rad)
  Solid = false
  Source = -> Face055
  Symmetric = false
FEATURE [Part::Feature] Face056
  shape: bbox 3.5 x 30.2 x 2e-07 mm, 1 faces, 0 solids (baked)
FEATURE [Part::Revolution] Revolve060  label="backCaseScrewPost001"
  Angle = 360
  Axis = (0,1,0)
  Base = (0,0,0)
  FaceMakerClass = Part::FaceMakerBullseye
  Placement = pos=(12.5,4.5,62) rot=(0,0,1;0rad)
  Solid = false
  Source = -> Face056
  Symmetric = false
FEATURE [Part::Feature] Face057
  shape: bbox 3.5 x 17.8 x 2e-07 mm, 1 faces, 0 solids (baked)
FEATURE [Part::Revolution] Revolve061  label="removeToCreateScrewAndThreadedInsertHole"
  Angle = 360
  Axis = (0,1,0)
  Base = (0,0,0)
  FaceMakerClass = Part::FaceMakerBullseye
  Placement = pos=(12.5,0,10) rot=(0,0,1;0rad)
  Solid = false
  Source = -> Face057
  Symmetric = false
FEATURE [Part::Feature] Face058
  shape: bbox 3.5 x 17.8 x 2e-07 mm, 1 faces, 0 solids (baked)
FEATURE [Part::Revolution] Revolve062  label="removeToCreateScrewAndThreadedInsertHole001"
  Angle = 360
  Axis = (0,1,0)
  Base = (0,0,0)
  FaceMakerClass = Part::FaceMakerBullseye
  Placement = pos=(12.5,0,62) rot=(0,0,1;0rad)
  Solid = false
  Source = -> Face058
  Symmetric = false
FEATURE [Part::Feature] Face059
  shape: bbox 3.5 x 17.8 x 2e-07 mm, 1 faces, 0 solids (baked)
FEATURE [Part::Revolution] Revolve063  label="removeToCreateScrewAndThreadedInsertHole002"
  Angle = 360
  Axis = (0,1,0)
  Base = (0,0,0)
  FaceMakerClass = Part::FaceMakerBullseye
  Placement = pos=(89.5,0,68.5) rot=(0,0,1;0rad)
  Solid = false
  Source = -> Face059
  Symmetric = false
FEATURE [Part::Feature] Face060
  shape: bbox 3.5 x 17.8 x 2e-07 mm, 1 faces, 0 solids (baked)
FEATURE [Part::Revolution] Revolve064  label="removeToCreateScrewAndThreadedInsertHole003"
  Angle = 360
  Axis = (0,1,0)
  Base = (0,0,0)
  FaceMakerClass = Part::FaceMakerBullseye
  Placement = pos=(89.5,0,3.5) rot=(0,0,1;0rad)
  Solid = false
  Source = -> Face060
  Symmetric = false
FEATURE [Part::Feature] Face061
  shape: bbox 3.5 x 17.8 x 2e-07 mm, 1 faces, 0 solids (baked)
FEATURE [Part::Revolution] Revolve065  label="removeToCreateScrewAndThreadedInsertHole004"
  Angle = 360
  Axis = (0,1,0)
  Base = (0,0,0)
  FaceMakerClass = Part::FaceMakerBullseye
  Placement = pos=(102.5,4.7,3.5) rot=(0,0,1;0rad)
  Solid = false
  Source = -> Face061
  Symmetric = false
FEATURE [Part::Feature] Face062
  shape: bbox 3.5 x 17.8 x 2e-07 mm, 1 faces, 0 solids (baked)
FEATURE [Part::Revolution] Revolve066  label="removeToCreateScrewAndThreadedInsertHole005"
  Angle = 360
  Axis = (0,1,0)
  Base = (0,0,0)
  FaceMakerClass = Part::FaceMakerBullseye
  Placement = pos=(102.5,4.7,68.5) rot=(0,0,1;0rad)
  Solid = false
  Source = -> Face062
  Symmetric = false
FEATURE [Part::MultiFuse] Fusion047  label="makeHoles"
  Shapes = -> [Revolve066,Revolve065,Revolve064,Revolve063,Revolve062,Revolve061]
FEATURE [Part::Feature] Face063
  shape: bbox 3.6 x 3.2 x 2e-07 mm, 1 faces, 0 solids (baked)
FEATURE [Part::Revolution] Revolve067  label="moreFrontCaseScrewRetainer002"
  Angle = 360
  Axis = (0,1,0)
  Base = (0,0,0)
  FaceMakerClass = Part::FaceMakerBullseye
  Placement = pos=(102.5,4.5,68.5) rot=(0,0,1;0rad)
  Solid = false
  Source = -> Face063
  Symmetric = false
FEATURE [Part::Feature] Face064
  shape: bbox 3.6 x 3.2 x 2e-07 mm, 1 faces, 0 solids (baked)
FEATURE [Part::Revolution] Revolve068  label="moreFrontCaseScrewRetainer003"
  Angle = 360
  Axis = (0,1,0)
  Base = (0,0,0)
  FaceMakerClass = Part::FaceMakerBullseye
  Placement = pos=(102.5,4.5,3.5) rot=(0,0,1;0rad)
  Solid = false
  Source = -> Face064
  Symmetric = false
FEATURE [Part::Feature] Face065
  shape: bbox 3.5 x 17.8 x 2e-07 mm, 1 faces, 0 solids (baked)
FEATURE [Part::Revolution] Revolve069  label="removeToCreateScrewAndThreadedInsertHole006"
  Angle = 360
  Axis = (0,1,0)
  Base = (0,0,0)
  FaceMakerClass = Part::FaceMakerBullseye
  Placement = pos=(12.5,0,10) rot=(0,0,1;0rad)
  Solid = false
  Source = -> Face065
  Symmetric = false
FEATURE [Part::Feature] Face066
  shape: bbox 3.5 x 17.8 x 2e-07 mm, 1 faces, 0 solids (baked)
FEATURE [Part::Revolution] Revolve070  label="removeToCreateScrewAndThreadedInsertHole007"
  Angle = 360
  Axis = (0,1,0)
  Base = (0,0,0)
  FaceMakerClass = Part::FaceMakerBullseye
  Placement = pos=(12.5,0,62) rot=(0,0,1;0rad)
  Solid = false
  Source = -> Face066
  Symmetric = false
FEATURE [Part::Feature] Face067
  shape: bbox 3.5 x 17.8 x 2e-07 mm, 1 faces, 0 solids (baked)
FEATURE [Part::Revolution] Revolve071  label="removeToCreateScrewAndThreadedInsertHole008"
  Angle = 360
  Axis = (0,1,0)
  Base = (0,0,0)
  FaceMakerClass = Part::FaceMakerBullseye
  Placement = pos=(89.5,0,68.5) rot=(0,0,1;0rad)
  Solid = false
  Source = -> Face067
  Symmetric = false
FEATURE [Part::Feature] Face068
  shape: bbox 3.5 x 17.8 x 2e-07 mm, 1 faces, 0 solids (baked)
FEATURE [Part::Revolution] Revolve072  label="removeToCreateScrewAndThreadedInsertHole009"
  Angle = 360
  Axis = (0,1,0)
  Base = (0,0,0)
  FaceMakerClass = Part::FaceMakerBullseye
  Placement = pos=(89.5,0,3.5) rot=(0,0,1;0rad)
  Solid = false
  Source = -> Face068
  Symmetric = false
FEATURE [Part::Feature] Face069
  shape: bbox 3.5 x 17.8 x 2e-07 mm, 1 faces, 0 solids (baked)
FEATURE [Part::Feature] Face070
  shape: bbox 3.5 x 17.8 x 2e-07 mm, 1 faces, 0 solids (baked)
FEATURE [Part::Revolution] Revolve073  label="removeToCreateScrewAndThreadedInsertHole010"
  Angle = 360
  Axis = (0,1,0)
  Base = (0,0,0)
  FaceMakerClass = Part::FaceMakerBullseye
  Placement = pos=(102.5,4.7,3.5) rot=(0,0,1;0rad)
  Solid = false
  Source = -> Face069
  Symmetric = false
FEATURE [Part::Revolution] Revolve074  label="removeToCreateScrewAndThreadedInsertHole011"
  Angle = 360
  Axis = (0,1,0)
  Base = (0,0,0)
  FaceMakerClass = Part::FaceMakerBullseye
  Placement = pos=(102.5,4.7,68.5) rot=(0,0,1;0rad)
  Solid = false
  Source = -> Face070
  Symmetric = false
FEATURE [Part::MultiFuse] Fusion048  label="makeHoles001"
  Shapes = -> [Revolve074,Revolve073,Revolve072,Revolve071,Revolve070,Revolve069]
FEATURE [Part::MultiFuse] Fusion049  label="caseScrewRetainers"
  Shapes = -> [Revolve067,Revolve068,Revolve048,Revolve047,Revolve039,Revolve040]
FEATURE [Part::Cut] Cut015  label="caseScrewRetainers001"
  Base = -> Fusion049
  Tool = -> Fusion048
FEATURE [Part::MultiFuse] Fusion050  label="casePillars"
  Shapes = -> [Revolve055,Revolve054,Revolve043,Revolve046,Revolve059,Revolve060]
FEATURE [Part::Feature] Face071 .. Face076  x6 (patterned run collapsed; names and placements below)
  shape: bbox 3.5 x 17.8 x 2e-07 mm, 1 faces, 0 solids (baked)
FEATURE [Part::Revolution] Revolve075  label="removeToCreateScrewAndThreadedInsertHole012"
  Angle = 360
  Axis = (0,1,0)
  Base = (0,0,0)
  FaceMakerClass = Part::FaceMakerBullseye
  Placement = pos=(12.5,0,10) rot=(0,0,1;0rad)
  Solid = false
  Source = -> Face071
  Symmetric = false
FEATURE [Part::Revolution] Revolve076  label="removeToCreateScrewAndThreadedInsertHole013"
  Angle = 360
  Axis = (0,1,0)
  Base = (0,0,0)
  FaceMakerClass = Part::FaceMakerBullseye
  Placement = pos=(12.5,0,62) rot=(0,0,1;0rad)
  Solid = false
  Source = -> Face072
  Symmetric = false
FEATURE [Part::Revolution] Revolve077  label="removeToCreateScrewAndThreadedInsertHole014"
  Angle = 360
  Axis = (0,1,0)
  Base = (0,0,0)
  FaceMakerClass = Part::FaceMakerBullseye
  Placement = pos=(89.5,0,68.5) rot=(0,0,1;0rad)
  Solid = false
  Source = -> Face073
  Symmetric = false
FEATURE [Part::Revolution] Revolve078  label="removeToCreateScrewAndThreadedInsertHole015"
  Angle = 360
  Axis = (0,1,0)
  Base = (0,0,0)
  FaceMakerClass = Part::FaceMakerBullseye
  Placement = pos=(89.5,0,3.5) rot=(0,0,1;0rad)
  Solid = false
  Source = -> Face074
  Symmetric = false
FEATURE [Part::Revolution] Revolve079  label="removeToCreateScrewAndThreadedInsertHole016"
  Angle = 360
  Axis = (0,1,0)
  Base = (0,0,0)
  FaceMakerClass = Part::FaceMakerBullseye
  Placement = pos=(102.5,4.7,3.5) rot=(0,0,1;0rad)
  Solid = false
  Source = -> Face075
  Symmetric = false
FEATURE [Part::Revolution] Revolve080  label="removeToCreateScrewAndThreadedInsertHole017"
  Angle = 360
  Axis = (0,1,0)
  Base = (0,0,0)
  FaceMakerClass = Part::FaceMakerBullseye
  Placement = pos=(102.5,4.7,68.5) rot=(0,0,1;0rad)
  Solid = false
  Source = -> Face076
  Symmetric = false
FEATURE [Part::MultiFuse] Fusion051  label="makeHoles002"
  Shapes = -> [Revolve080,Revolve079,Revolve078,Revolve077,Revolve076,Revolve075]
FEATURE [Part::Cut] Cut016  label="caesPillars"
  Base = -> Fusion050
  Tool = -> Fusion051
FEATURE [Part::Revolution] Revolve009  label="plugHousing016"
  Angle = 360
  Axis = (0,1,0)
  Base = (0,0,0)
  FaceMakerClass = Part::FaceMakerBullseye
  Placement = pos=(0,0,36.15) rot=(0,0,1;0rad)
  Solid = false
  Source = -> Face012
  Symmetric = false
FEATURE [Part::MultiFuse] Fusion014  label="plugHousing023"
  Placement = pos=(0,0,0) rot=(0,0,1;1.5708rad)
  Shapes = -> [Revolve011,Revolve009]
FEATURE [Part::Revolution] Revolve010  label="plugHousing017"
  Angle = 360
  Axis = (0,1,0)
  Base = (0,0,0)
  FaceMakerClass = Part::FaceMakerBullseye
  Placement = pos=(0,0,36.15) rot=(0,0,1;0rad)
  Solid = false
  Source = -> Face014
  Symmetric = false
FEATURE [Part::MultiFuse] Fusion015  label="plugHousing024"
  Placement = pos=(0,0,0) rot=(0,0,1;1.5708rad)
  Shapes = -> [Revolve010,Revolve015]
FEATURE [Part::Revolution] Revolve014  label="plugHousing026"
  Angle = 360
  Axis = (0,1,0)
  Base = (0,0,0)
  FaceMakerClass = Part::FaceMakerBullseye
  Placement = pos=(0,0,36.15) rot=(0,0,1;0rad)
  Solid = false
  Source = -> Face011
  Symmetric = false
FEATURE [Part::Revolution] Revolve013  label="plugHousing025"
  Angle = 360
  Axis = (0,1,0)
  Base = (0,0,0)
  FaceMakerClass = Part::FaceMakerBullseye
  Placement = pos=(0,0,36.15) rot=(0,0,1;0rad)
  Solid = false
  Source = -> Face015
  Symmetric = false
FEATURE [Part::MultiFuse] Fusion016  label="plugHousing028"
  Placement = pos=(0,19,0) rot=(0,0,1;3.14159rad)
  Shapes = -> [Fusion014,Fusion013]
FEATURE [Part::MultiFuse] Fusion011  label="plugHousing018"
  Placement = pos=(0,0,0) rot=(0,0,1;1.5708rad)
  Shapes = -> [Revolve014,Revolve013]
FEATURE [Part::MultiFuse] Fusion012  label="plugHousing019"
  Placement = pos=(0,19,0) rot=(0,0,1;3.14159rad)
  Shapes = -> [Fusion011,Fusion015]
FEATURE [Part::MultiFuse] Fusion017  label="plugHousing029"
  Placement = pos=(122.621,0,-0.15) rot=(0,0,1;0rad)
  Shapes = -> [Fusion016,Fusion012]
FEATURE [Part::MultiFuse] Fusion052  label="casePillarRetainers"
  Shapes = -> [Extrude012,Extrude013,Extrude014,Extrude015,Extrude016,Extrude017,Extrude018,Extrude019,Box011,Box012]
FEATURE [Part::Feature] Face077
  shape: bbox 3.5 x 17.8 x 2e-07 mm, 1 faces, 0 solids (baked)
FEATURE [Part::Revolution] Revolve081  label="removeToCreateScrewAndThreadedInsertHole018"
  Angle = 360
  Axis = (0,1,0)
  Base = (0,0,0)
  FaceMakerClass = Part::FaceMakerBullseye
  Placement = pos=(62.3,30.3,19.7) rot=(0,0,1;0rad)
  Solid = false
  Source = -> Face077
  Symmetric = false
FEATURE [Part::Feature] Face078
  shape: bbox 3.5 x 17.8 x 2e-07 mm, 1 faces, 0 solids (baked)
FEATURE [Part::Revolution] Revolve082  label="removeToCreateScrewAndThreadedInsertHole019"
  Angle = 360
  Axis = (0,1,0)
  Base = (0,0,0)
  FaceMakerClass = Part::FaceMakerBullseye
  Placement = pos=(62.3,30.3,51.7) rot=(0,0,1;0rad)
  Solid = false
  Source = -> Face078
  Symmetric = false
FEATURE [Part::Feature] Face079
  shape: bbox 3.5 x 17.8 x 2e-07 mm, 1 faces, 0 solids (baked)
FEATURE [Part::Revolution] Revolve083  label="removeToCreateScrewAndThreadedInsertHole020"
  Angle = 360
  Axis = (0,1,0)
  Base = (0,0,0)
  FaceMakerClass = Part::FaceMakerBullseye
  Placement = pos=(30.3,30.3,19.7) rot=(0,0,1;0rad)
  Solid = false
  Source = -> Face079
  Symmetric = false
FEATURE [Part::Feature] Face080
  shape: bbox 3.5 x 17.8 x 2e-07 mm, 1 faces, 0 solids (baked)
FEATURE [Part::Revolution] Revolve084  label="removeToCreateScrewAndThreadedInsertHole021"
  Angle = 360
  Axis = (0,1,0)
  Base = (0,0,0)
  FaceMakerClass = Part::FaceMakerBullseye
  Placement = pos=(30.3,30.3,51.7) rot=(0,0,1;0rad)
  Solid = false
  Source = -> Face080
  Symmetric = false
FEATURE [Part::MultiFuse] Fusion053  label="createThreadedInsertHolesForFan"
  Shapes = -> [Revolve081,Revolve082,Revolve083,Revolve084]
FEATURE [Part::Cut] Cut017  label="fanScrewHousing001"
  Base = -> Fusion046
  Tool = -> Fusion053
FEATURE [Part::Feature] Face081
  shape: bbox 3.5 x 17.8 x 2e-07 mm, 1 faces, 0 solids (baked)
FEATURE [Part::Revolution] Revolve085  label="removeToCreateScrewAndThreadedInsertHole022"
  Angle = 360
  Axis = (0,1,0)
  Base = (0,0,0)
  FaceMakerClass = Part::FaceMakerBullseye
  Placement = pos=(62.3,30.3,19.7) rot=(0,0,1;0rad)
  Solid = false
  Source = -> Face081
  Symmetric = false
FEATURE [Part::Feature] Face082
  shape: bbox 3.5 x 17.8 x 2e-07 mm, 1 faces, 0 solids (baked)
FEATURE [Part::Revolution] Revolve086  label="removeToCreateScrewAndThreadedInsertHole023"
  Angle = 360
  Axis = (0,1,0)
  Base = (0,0,0)
  FaceMakerClass = Part::FaceMakerBullseye
  Placement = pos=(62.3,30.3,51.7) rot=(0,0,1;0rad)
  Solid = false
  Source = -> Face082
  Symmetric = false
FEATURE [Part::Feature] Face083
  shape: bbox 3.5 x 17.8 x 2e-07 mm, 1 faces, 0 solids (baked)
FEATURE [Part::Revolution] Revolve087  label="removeToCreateScrewAndThreadedInsertHole024"
  Angle = 360
  Axis = (0,1,0)
  Base = (0,0,0)
  FaceMakerClass = Part::FaceMakerBullseye
  Placement = pos=(30.3,30.3,19.7) rot=(0,0,1;0rad)
  Solid = false
  Source = -> Face083
  Symmetric = false
FEATURE [Part::Feature] Face084
  shape: bbox 3.5 x 17.8 x 2e-07 mm, 1 faces, 0 solids (baked)
FEATURE [Part::Revolution] Revolve088  label="removeToCreateScrewAndThreadedInsertHole025"
  Angle = 360
  Axis = (0,1,0)
  Base = (0,0,0)
  FaceMakerClass = Part::FaceMakerBullseye
  Placement = pos=(30.3,30.3,51.7) rot=(0,0,1;0rad)
  Solid = false
  Source = -> Face084
  Symmetric = false
FEATURE [Part::MultiFuse] Fusion054  label="createThreadedInsertHolesForFan001"
  Shapes = -> [Revolve085,Revolve086,Revolve087,Revolve088]
FEATURE [Part::Cut] Cut018  label="top007"
  Base = -> Fusion040
  Tool = -> Fusion054
FEATURE [Sketcher::SketchObject] Sketch029
  FullyConstrained = false
  Placement = pos=(0,0,0) rot=(1,0,0;1.5708rad)
  sketch-geometry (24):
    g0: ArcOfCircle CenterX=-4 CenterY=-10.5 CenterZ=0 NormalX=0 NormalY=0 NormalZ=1 AngleXU=0 Radius=1.5 StartAngle=6e-16 EndAngle=3.14159
    g1: ArcOfCircle CenterX=-34.2 CenterY=-10.5 CenterZ=0 NormalX=0 NormalY=0 NormalZ=1 AngleXU=0 Radius=1.5 StartAngle=0 EndAngle=3.14159
    g2: ArcOfCircle CenterX=-34.2 CenterY=-27.7 CenterZ=0 NormalX=0 NormalY=0 NormalZ=1 AngleXU=0 Radius=1.5 StartAngle=3.14159 EndAngle=6.28319
    g3: ArcOfCircle CenterX=-4 CenterY=-27.7 CenterZ=0 NormalX=0 NormalY=0 NormalZ=1 AngleXU=0 Radius=1.5 StartAngle=3.1416 EndAngle=6.28319
    g4: ArcOfCircle CenterX=-10 CenterY=-4.3 CenterZ=0 NormalX=0 NormalY=0 NormalZ=1 AngleXU=0 Radius=1.5 StartAngle=2e-16 EndAngle=3.14159
    g5: ArcOfCircle CenterX=-16.1 CenterY=-1.8 CenterZ=0 NormalX=0 NormalY=0 NormalZ=1 AngleXU=0 Radius=1.5 StartAngle=5e-16 EndAngle=3.14159
    g6: ArcOfCircle CenterX=-22.1 CenterY=-1.8 CenterZ=0 NormalX=0 NormalY=0 NormalZ=1 AngleXU=0 Radius=1.5 StartAngle=5e-16 EndAngle=3.14159
    g7: ArcOfCircle CenterX=-28.2 CenterY=-4.3 CenterZ=0 NormalX=0 NormalY=0 NormalZ=1 AngleXU=0 Radius=1.5 StartAngle=2e-16 EndAngle=3.14159
    g8: ArcOfCircle CenterX=-10 CenterY=-33.9 CenterZ=0 NormalX=0 NormalY=0 NormalZ=1 AngleXU=0 Radius=1.5 StartAngle=3.14159 EndAngle=6.28319
    g9: ArcOfCircle CenterX=-16.1 CenterY=-36.4 CenterZ=0 NormalX=0 NormalY=0 NormalZ=1 AngleXU=0 Radius=1.5 StartAngle=3.14159 EndAngle=6.28319
    g10: ArcOfCircle CenterX=-22.1 CenterY=-36.4 CenterZ=0 NormalX=0 NormalY=0 NormalZ=1 AngleXU=0 Radius=1.5 StartAngle=3.14159 EndAngle=6.28319
    g11: ArcOfCircle CenterX=-28.2 CenterY=-33.9 CenterZ=0 NormalX=0 NormalY=0 NormalZ=1 AngleXU=0 Radius=1.5 StartAngle=3.14159 EndAngle=6.28319
    g12: LineSegment StartX=-35.7 StartY=-10.5 StartZ=0 EndX=-35.7 EndY=-27.7 EndZ=0
    g13: LineSegment StartX=-32.7 StartY=-10.5 StartZ=0 EndX=-32.7 EndY=-27.7 EndZ=0
    g14: LineSegment StartX=-29.7 StartY=-33.9 StartZ=0 EndX=-29.7 EndY=-4.3 EndZ=0
    g15: LineSegment StartX=-26.7 StartY=-33.9 StartZ=0 EndX=-26.7 EndY=-4.3 EndZ=0
    g16: LineSegment StartX=-2.5 StartY=-10.5 StartZ=0 EndX=-2.5 EndY=-27.7 EndZ=0
    g17: LineSegment StartX=-8.5 StartY=-4.3 StartZ=0 EndX=-8.5 EndY=-33.9 EndZ=0
    g18: LineSegment StartX=-5.5 StartY=-10.5 StartZ=0 EndX=-5.5 EndY=-27.7 EndZ=0
    g19: LineSegment StartX=-11.5 StartY=-4.3 StartZ=0 EndX=-11.5 EndY=-33.9 EndZ=0
    g20: LineSegment StartX=-14.6 StartY=-1.8 StartZ=0 EndX=-14.6 EndY=-36.4 EndZ=0
    g21: LineSegment StartX=-17.6 StartY=-1.8 StartZ=0 EndX=-17.6 EndY=-36.4 EndZ=0
    g22: LineSegment StartX=-20.6 StartY=-36.4 StartZ=0 EndX=-20.6 EndY=-1.8 EndZ=0
    g23: LineSegment StartX=-23.6 StartY=-1.8 StartZ=0 EndX=-23.6 EndY=-36.4 EndZ=0
  constraints (48):
    c: Block(g0)
    c: Block(g1)
    c: Block(g2)
    c: Block(g3)
    c: Block(g4)
    c: Block(g5)
    c: Block(g6)
    c: Block(g7)
    c: Block(g8)
    c: Block(g9)
    c: Block(g10)
    c: Block(g11)
    c: Coincident(g12,g1)
    c: Coincident(g12,g2)
    c: Vertical(g12)
    c: Coincident(g13,g1)
    c: Coincident(g13,g2)
    c: Vertical(g13)
    c: Coincident(g14,g11)
    c: Coincident(g14,g7)
    c: Vertical(g14)
    c: Coincident(g15,g11)
    c: Coincident(g15,g7)
    c: Vertical(g15)
    c: Coincident(g16,g0)
    c: Coincident(g16,g3)
    c: Vertical(g16)
    c: Coincident(g17,g4)
    c: Coincident(g17,g8)
    c: Vertical(g17)
    c: Coincident(g18,g0)
    c: Coincident(g18,g3)
    c: Vertical(g18)
    c: Coincident(g19,g4)
    c: Coincident(g19,g8)
    c: Vertical(g19)
    c: Coincident(g20,g5)
    c: Coincident(g20,g9)
    c: Vertical(g20)
    c: Coincident(g21,g5)
    c: Coincident(g21,g9)
    c: Vertical(g21)
    c: Coincident(g22,g10)
    c: Coincident(g22,g6)
    c: Vertical(g22)
    c: Coincident(g23,g6)
    c: Coincident(g23,g10)
    c: Vertical(g23)
FEATURE [Part::Extrusion] Extrude020  label="removeToCreateFanGrillHoles"
  Base = -> Sketch029
  Dir = (0,-1,6e-16)
  DirMode = 2
  FaceMakerClass = Part::FaceMakerBullseye
  LengthFwd = 10
  LengthRev = 0
  Placement = pos=(65.4,44,54.82) rot=(0,0,1;0rad)
  Solid = true
  Symmetric = false
FEATURE [Part::MultiFuse] Fusion055  label="top008"
  Shapes = -> [Cut017,Cut018]
FEATURE [Part::Cut] Cut019  label="top009"
  Base = -> Fusion055
  Tool = -> Extrude020
FEATURE [App::MeasureDistance] Distance003  label="Distance: 71.95 mm"
  Distance = 71.9513
  P1 = (117,38,72)
  P2 = (117,38,0.0487319)
FEATURE [Sketcher::SketchObject] Sketch030
  FullyConstrained = true
  Placement = pos=(117,19,0) rot=(0.57735,0.57735,0.57735;2.0944rad)
  sketch-geometry (48):
    g0: LineSegment StartX=-49.19 StartY=69.25 StartZ=0 EndX=-49.19 EndY=66.25 EndZ=0
    g1: LineSegment StartX=-49.19 StartY=63.5 StartZ=0 EndX=-49.19 EndY=60.5 EndZ=0
    g2: LineSegment StartX=-49.19 StartY=57.75 StartZ=0 EndX=-49.19 EndY=54.75 EndZ=0
    g3: LineSegment StartX=-49.19 StartY=52 StartZ=0 EndX=-49.19 EndY=49 EndZ=0
    g4: LineSegment StartX=-49.19 StartY=46.25 StartZ=0 EndX=-49.19 EndY=43.25 EndZ=0
    g5: LineSegment StartX=-49.19 StartY=40.5 StartZ=0 EndX=-49.19 EndY=37.5 EndZ=0
    g6: LineSegment StartX=-49.19 StartY=34.5 StartZ=0 EndX=-49.19 EndY=31.5 EndZ=0
    g7: LineSegment StartX=-49.19 StartY=28.75 StartZ=0 EndX=-49.19 EndY=25.75 EndZ=0
    g8: LineSegment StartX=-49.19 StartY=23 StartZ=0 EndX=-49.19 EndY=20 EndZ=0
    g9: LineSegment StartX=-49.19 StartY=17.25 StartZ=0 EndX=-49.19 EndY=14.25 EndZ=0
    g10: LineSegment StartX=-49.19 StartY=11.5 StartZ=0 EndX=-49.19 EndY=8.5 EndZ=0
    g11: LineSegment StartX=-49.19 StartY=5.75 StartZ=0 EndX=-49.19 EndY=2.75 EndZ=0
    g12: ArcOfCircle CenterX=-1.5 CenterY=67.75 CenterZ=0 NormalX=0 NormalY=0 NormalZ=1 AngleXU=0 Radius=1.5 StartAngle=4.71239 EndAngle=7.85398
    g13: ArcOfCircle CenterX=-1.5 CenterY=62 CenterZ=0 NormalX=0 NormalY=0 NormalZ=1 AngleXU=0 Radius=1.5 StartAngle=4.71239 EndAngle=7.85398
    g14: ArcOfCircle CenterX=-1.5 CenterY=56.25 CenterZ=0 NormalX=0 NormalY=0 NormalZ=1 AngleXU=0 Radius=1.5 StartAngle=4.71239 EndAngle=7.85398
    g15: ArcOfCircle CenterX=-11.49 CenterY=50.5 CenterZ=0 NormalX=0 NormalY=0 NormalZ=1 AngleXU=0 Radius=1.5 StartAngle=4.71239 EndAngle=7.85398
    g16: ArcOfCircle CenterX=-16.28 CenterY=44.75 CenterZ=0 NormalX=0 NormalY=0 NormalZ=1 AngleXU=0 Radius=1.5 StartAngle=4.71239 EndAngle=7.85398
    g17: ArcOfCircle CenterX=-18.2337 CenterY=39 CenterZ=0 NormalX=0 NormalY=0 NormalZ=1 AngleXU=0 Radius=1.5 StartAngle=4.71485 EndAngle=7.85398
    g18: ArcOfCircle CenterX=-16.2837 CenterY=27.25 CenterZ=0 NormalX=0 NormalY=0 NormalZ=1 AngleXU=0 Radius=1.5 StartAngle=4.71485 EndAngle=7.85398
    g19: ArcOfCircle CenterX=-18.2337 CenterY=33 CenterZ=0 NormalX=0 NormalY=0 NormalZ=1 AngleXU=0 Radius=1.5 StartAngle=4.71485 EndAngle=7.85398
    g20: ArcOfCircle CenterX=-11.49 CenterY=21.5 CenterZ=0 NormalX=0 NormalY=0 NormalZ=1 AngleXU=0 Radius=1.5 StartAngle=4.71239 EndAngle=7.85398
    g21: ArcOfCircle CenterX=-1.5 CenterY=4.25 CenterZ=0 NormalX=0 NormalY=0 NormalZ=1 AngleXU=0 Radius=1.5 StartAngle=4.71239 EndAngle=7.85398
    g22: ArcOfCircle CenterX=-1.5 CenterY=10 CenterZ=0 NormalX=0 NormalY=0 NormalZ=1 AngleXU=0 Radius=1.5 StartAngle=4.71239 EndAngle=7.85398
    g23: ArcOfCircle CenterX=-1.5 CenterY=15.75 CenterZ=0 NormalX=0 NormalY=0 NormalZ=1 AngleXU=0 Radius=1.5 StartAngle=4.71239 EndAngle=7.85398
    g24: LineSegment StartX=-49.19 StartY=69.25 StartZ=0 EndX=-1.5 EndY=69.25 EndZ=0
    g25: LineSegment StartX=-49.19 StartY=66.25 StartZ=0 EndX=-1.5 EndY=66.25 EndZ=0
    g26: LineSegment StartX=-49.19 StartY=63.5 StartZ=0 EndX=-1.5 EndY=63.5 EndZ=0
    g27: LineSegment StartX=-49.19 StartY=60.5 StartZ=0 EndX=-1.5 EndY=60.5 EndZ=0
    g28: LineSegment StartX=-49.19 StartY=57.75 StartZ=0 EndX=-1.5 EndY=57.75 EndZ=0
    g29: LineSegment StartX=-49.19 StartY=54.75 StartZ=0 EndX=-1.5 EndY=54.75 EndZ=0
    g30: LineSegment StartX=-49.19 StartY=52 StartZ=0 EndX=-11.49 EndY=52 EndZ=0
    g31: LineSegment StartX=-49.19 StartY=49 StartZ=0 EndX=-11.49 EndY=49 EndZ=0
    g32: LineSegment StartX=-49.19 StartY=46.25 StartZ=0 EndX=-16.28 EndY=46.25 EndZ=0
    g33: LineSegment StartX=-49.19 StartY=43.25 StartZ=0 EndX=-16.28 EndY=43.25 EndZ=0
    g34: LineSegment StartX=-49.19 StartY=40.5 StartZ=0 EndX=-18.2337 EndY=40.5 EndZ=0
    g35: LineSegment StartX=-49.19 StartY=37.5 StartZ=0 EndX=-18.23 EndY=37.5 EndZ=0
    g36: LineSegment StartX=-49.19 StartY=34.5 StartZ=0 EndX=-18.2337 EndY=34.5 EndZ=0
    g37: LineSegment StartX=-49.19 StartY=31.5 StartZ=0 EndX=-18.23 EndY=31.5 EndZ=0
    g38: LineSegment StartX=-49.19 StartY=28.75 StartZ=0 EndX=-16.2837 EndY=28.75 EndZ=0
    g39: LineSegment StartX=-49.19 StartY=25.75 StartZ=0 EndX=-16.28 EndY=25.75 EndZ=0
    g40: LineSegment StartX=-49.19 StartY=23 StartZ=0 EndX=-11.49 EndY=23 EndZ=0
    g41: LineSegment StartX=-49.19 StartY=20 StartZ=0 EndX=-11.49 EndY=20 EndZ=0
    g42: LineSegment StartX=-49.19 StartY=17.25 StartZ=0 EndX=-1.5 EndY=17.25 EndZ=0
    g43: LineSegment StartX=-49.19 StartY=14.25 StartZ=0 EndX=-1.5 EndY=14.25 EndZ=0
    g44: LineSegment StartX=-49.19 StartY=11.5 StartZ=0 EndX=-1.5 EndY=11.5 EndZ=0
    g45: LineSegment StartX=-49.19 StartY=8.5 StartZ=0 EndX=-1.5 EndY=8.5 EndZ=0
    g46: LineSegment StartX=-49.19 StartY=5.75 StartZ=0 EndX=-1.5 EndY=5.75 EndZ=0
    g47: LineSegment StartX=-49.19 StartY=2.75 StartZ=0 EndX=-1.5 EndY=2.75 EndZ=0
  constraints (120):
    c: Vertical(g0)
    c: Distance(g0) = 3
    c: Block(g0)
    c: Vertical(g1)
    c: Distance(g1) = 3
    c: Vertical(g2)
    c: Equal(g0,g2) = 3
    c: Block(g2)
    c: Vertical(g3)
    c: Equal(g1,g3) = 3
    c: Vertical(g4)
    c: Equal(g0,g4) = 3
    c: Block(g4)
    c: Vertical(g5)
    c: Equal(g1,g5) = 3
    c: Vertical(g6)
    c: Equal(g0,g6) = 3
    c: Block(g6)
    c: Vertical(g7)
    c: Equal(g1,g7) = 3
    c: Vertical(g8)
    c: Equal(g0,g8) = 3
    c: Block(g8)
    c: Vertical(g9)
    c: Equal(g1,g9) = 3
    c: Vertical(g10)
    c: Equal(g0,g10) = 3
    c: Block(g10)
    c: Vertical(g11)
    c: Equal(g1,g11) = 3
    c: Block(g12)
    c: Block(g13)
    c: Block(g14)
    c: Block(g15)
    c: Block(g16)
    c: Block(g17)
    c: Block(g18)
    c: Block(g19)
    c: Block(g20)
    c: Block(g21)
    c: Block(g22)
    c: Block(g23)
    c: Block(g11)
    c: Block(g9)
    c: Block(g7)
    c: Block(g5)
    c: Block(g3)
    c: Block(g1)
    c: Coincident(g24,g0)
    c: Coincident(g24,g12)
    c: Horizontal(g24)
    c: Coincident(g25,g0)
    c: Coincident(g25,g12)
    c: Horizontal(g25)
    c: Coincident(g26,g1)
    c: Coincident(g26,g13)
    c: Horizontal(g26)
    c: Coincident(g27,g1)
    c: Coincident(g27,g13)
    c: Horizontal(g27)
    c: Coincident(g28,g2)
    c: Coincident(g28,g14)
    c: Horizontal(g28)
    c: Coincident(g29,g2)
    c: Coincident(g29,g14)
    c: Horizontal(g29)
    c: Coincident(g30,g3)
    c: Coincident(g30,g15)
    c: Horizontal(g30)
    c: Coincident(g31,g3)
    c: Coincident(g31,g15)
    c: Horizontal(g31)
    c: Coincident(g32,g4)
    c: Coincident(g32,g16)
    c: Horizontal(g32)
    c: Coincident(g33,g4)
    c: Coincident(g33,g16)
    c: Horizontal(g33)
    c: Coincident(g34,g5)
    c: Coincident(g34,g17)
    c: Horizontal(g34)
    c: Coincident(g35,g5)
    c: Coincident(g35,g17)
    c: Horizontal(g35)
    c: Coincident(g36,g6)
    c: Coincident(g36,g19)
    c: Horizontal(g36)
    c: Coincident(g37,g6)
    c: Coincident(g37,g19)
    c: Horizontal(g37)
    c: Coincident(g38,g7)
    c: Coincident(g38,g18)
    c: Horizontal(g38)
    c: Coincident(g39,g7)
    c: Coincident(g39,g18)
    c: Horizontal(g39)
    c: Coincident(g40,g8)
    c: Coincident(g40,g20)
    c: Horizontal(g40)
    c: Coincident(g41,g8)
    c: Coincident(g41,g20)
    c: Horizontal(g41)
    c: Coincident(g42,g9)
    c: Coincident(g42,g23)
    c: Horizontal(g42)
    c: Coincident(g43,g9)
    c: Coincident(g43,g23)
    c: Horizontal(g43)
    c: Coincident(g44,g10)
    c: Coincident(g44,g22)
    c: Horizontal(g44)
    c: Coincident(g45,g10)
    c: Coincident(g45,g22)
    c: Horizontal(g45)
    c: Coincident(g46,g11)
    c: Coincident(g46,g21)
    c: Horizontal(g46)
    c: Coincident(g47,g11)
    c: Coincident(g47,g21)
    c: Horizontal(g47)
FEATURE [Sketcher::SketchObject] Sketch031
  FullyConstrained = true
  Placement = pos=(117,19,0) rot=(0.57735,0.57735,0.57735;2.0944rad)
  sketch-geometry (24):
    g0: ArcOfCircle CenterX=-49.19 CenterY=67.75 CenterZ=0 NormalX=0 NormalY=0 NormalZ=1 AngleXU=0 Radius=1.5 StartAngle=1.5708 EndAngle=4.71239
    g1: ArcOfCircle CenterX=-49.19 CenterY=62 CenterZ=0 NormalX=0 NormalY=0 NormalZ=1 AngleXU=0 Radius=1.5 StartAngle=1.5708 EndAngle=4.71239
    g2: ArcOfCircle CenterX=-49.19 CenterY=56.25 CenterZ=0 NormalX=0 NormalY=0 NormalZ=1 AngleXU=0 Radius=1.5 StartAngle=1.5708 EndAngle=4.71239
    g3: ArcOfCircle CenterX=-49.19 CenterY=50.5 CenterZ=0 NormalX=0 NormalY=0 NormalZ=1 AngleXU=0 Radius=1.5 StartAngle=1.5708 EndAngle=4.71239
    g4: ArcOfCircle CenterX=-49.19 CenterY=44.75 CenterZ=0 NormalX=0 NormalY=0 NormalZ=1 AngleXU=0 Radius=1.5 StartAngle=1.5708 EndAngle=4.71239
    g5: ArcOfCircle CenterX=-49.19 CenterY=39 CenterZ=0 NormalX=0 NormalY=0 NormalZ=1 AngleXU=0 Radius=1.5 StartAngle=1.5708 EndAngle=4.71239
    g6: ArcOfCircle CenterX=-49.19 CenterY=33 CenterZ=0 NormalX=0 NormalY=0 NormalZ=1 AngleXU=0 Radius=1.5 StartAngle=1.5708 EndAngle=4.71239
    g7: ArcOfCircle CenterX=-49.19 CenterY=27.25 CenterZ=0 NormalX=0 NormalY=0 NormalZ=1 AngleXU=0 Radius=1.5 StartAngle=1.5708 EndAngle=4.71239
    g8: ArcOfCircle CenterX=-49.19 CenterY=21.5 CenterZ=0 NormalX=0 NormalY=0 NormalZ=1 AngleXU=0 Radius=1.5 StartAngle=1.5708 EndAngle=4.71239
    g9: ArcOfCircle CenterX=-49.19 CenterY=15.75 CenterZ=0 NormalX=0 NormalY=0 NormalZ=1 AngleXU=0 Radius=1.5 StartAngle=1.5708 EndAngle=4.71239
    g10: ArcOfCircle CenterX=-49.19 CenterY=10 CenterZ=0 NormalX=0 NormalY=0 NormalZ=1 AngleXU=0 Radius=1.5 StartAngle=1.5708 EndAngle=4.71239
    g11: ArcOfCircle CenterX=-49.19 CenterY=4.25 CenterZ=0 NormalX=0 NormalY=0 NormalZ=1 AngleXU=0 Radius=1.5 StartAngle=1.5708 EndAngle=4.71239
    g12: LineSegment StartX=-49.19 StartY=69.25 StartZ=0 EndX=-49.19 EndY=66.25 EndZ=0
    g13: LineSegment StartX=-49.19 StartY=63.5 StartZ=0 EndX=-49.19 EndY=60.5 EndZ=0
    g14: LineSegment StartX=-49.19 StartY=57.75 StartZ=0 EndX=-49.19 EndY=54.75 EndZ=0
    g15: LineSegment StartX=-49.19 StartY=52 StartZ=0 EndX=-49.19 EndY=49 EndZ=0
    g16: LineSegment StartX=-49.19 StartY=46.25 StartZ=0 EndX=-49.19 EndY=43.25 EndZ=0
    g17: LineSegment StartX=-49.19 StartY=40.5 StartZ=0 EndX=-49.19 EndY=37.5 EndZ=0
    g18: LineSegment StartX=-49.19 StartY=34.5 StartZ=0 EndX=-49.19 EndY=31.5 EndZ=0
    g19: LineSegment StartX=-49.19 StartY=28.75 StartZ=0 EndX=-49.19 EndY=25.75 EndZ=0
    g20: LineSegment StartX=-49.19 StartY=23 StartZ=0 EndX=-49.19 EndY=20 EndZ=0
    g21: LineSegment StartX=-49.19 StartY=17.25 StartZ=0 EndX=-49.19 EndY=14.25 EndZ=0
    g22: LineSegment StartX=-49.19 StartY=11.5 StartZ=0 EndX=-49.19 EndY=8.5 EndZ=0
    g23: LineSegment StartX=-49.19 StartY=5.75 StartZ=0 EndX=-49.19 EndY=2.75 EndZ=0
  constraints (48):
    c: Block(g0)
    c: Block(g1)
    c: Block(g2)
    c: Block(g3)
    c: Block(g4)
    c: Block(g5)
    c: Block(g6)
    c: Block(g7)
    c: Block(g8)
    c: Block(g9)
    c: Block(g10)
    c: Block(g11)
    c: Coincident(g12,g0)
    c: Coincident(g12,g0)
    c: Vertical(g12)
    c: Vertical(g13)
    c: Coincident(g13,g1)
    c: Vertical(g14)
    c: Coincident(g14,g2)
    c: Vertical(g15)
    c: Coincident(g15,g3)
    c: Vertical(g16)
    c: Coincident(g16,g4)
    c: Vertical(g17)
    c: Coincident(g17,g5)
    c: Vertical(g18)
    c: Coincident(g18,g6)
    c: Vertical(g19)
    c: Coincident(g19,g7)
    c: Vertical(g20)
    c: Coincident(g20,g8)
    c: Vertical(g21)
    c: Coincident(g21,g9)
    c: Vertical(g22)
    c: Coincident(g22,g10)
    c: Vertical(g23)
    c: Coincident(g23,g11)
    c: Block(g23)
    c: Block(g22)
    c: Block(g21)
    c: Block(g20)
    c: Block(g13)
    c: Block(g14)
    c: Block(g15)
    c: Block(g16)
    c: Block(g17)
    c: Block(g18)
    c: Block(g19)
FEATURE [Part::Extrusion] Extrude022
  Base = -> Sketch030
  Dir = (1,-2e-16,2e-16)
  DirMode = 2
  FaceMakerClass = Part::FaceMakerBullseye
  LengthFwd = 19
  LengthRev = 0
  Placement = pos=(-19,0,0) rot=(0,0,1;0rad)
  Solid = true
  Symmetric = false
FEATURE [Part::Fillet] Fillet022
  Base = -> Extrude022
  Edges = 24 edges r=1.49: [Edge6,Edge11,Edge18,Edge23,Edge30,Edge35,Edge42,Edge47,Edge54,Edge59,Edge66,Edge71,Edge78,Edge83,Edge90,Edge95,Edge102,Edge107,Edge114,Edge119,Edge126,Edge131,Edge138,Edge143]
FEATURE [Part::Cut] Cut020  label="top010"
  Base = -> Cut019
  Tool = -> Fillet022
FEATURE [Sketcher::SketchObject] Sketch032
  FullyConstrained = true
  Placement = pos=(117,19,0) rot=(0.57735,0.57735,0.57735;2.0944rad)
  sketch-geometry (48):
    g0: LineSegment StartX=-49.19 StartY=69.25 StartZ=0 EndX=-49.19 EndY=66.25 EndZ=0
    g1: LineSegment StartX=-49.19 StartY=63.5 StartZ=0 EndX=-49.19 EndY=60.5 EndZ=0
    g2: LineSegment StartX=-49.19 StartY=57.75 StartZ=0 EndX=-49.19 EndY=54.75 EndZ=0
    g3: LineSegment StartX=-49.19 StartY=52 StartZ=0 EndX=-49.19 EndY=49 EndZ=0
    g4: LineSegment StartX=-49.19 StartY=46.25 StartZ=0 EndX=-49.19 EndY=43.25 EndZ=0
    g5: LineSegment StartX=-49.19 StartY=40.5 StartZ=0 EndX=-49.19 EndY=37.5 EndZ=0
    g6: LineSegment StartX=-49.19 StartY=34.5 StartZ=0 EndX=-49.19 EndY=31.5 EndZ=0
    g7: LineSegment StartX=-49.19 StartY=28.75 StartZ=0 EndX=-49.19 EndY=25.75 EndZ=0
    g8: LineSegment StartX=-49.19 StartY=23 StartZ=0 EndX=-49.19 EndY=20 EndZ=0
    g9: LineSegment StartX=-49.19 StartY=17.25 StartZ=0 EndX=-49.19 EndY=14.25 EndZ=0
    g10: LineSegment StartX=-49.19 StartY=11.5 StartZ=0 EndX=-49.19 EndY=8.5 EndZ=0
    g11: LineSegment StartX=-49.19 StartY=5.75 StartZ=0 EndX=-49.19 EndY=2.75 EndZ=0
    g12: ArcOfCircle CenterX=-1.5 CenterY=67.75 CenterZ=0 NormalX=0 NormalY=0 NormalZ=1 AngleXU=0 Radius=1.5 StartAngle=4.71239 EndAngle=7.85398
    g13: ArcOfCircle CenterX=-1.5 CenterY=62 CenterZ=0 NormalX=0 NormalY=0 NormalZ=1 AngleXU=0 Radius=1.5 StartAngle=4.71239 EndAngle=7.85398
    g14: ArcOfCircle CenterX=-1.5 CenterY=56.25 CenterZ=0 NormalX=0 NormalY=0 NormalZ=1 AngleXU=0 Radius=1.5 StartAngle=4.71239 EndAngle=7.85398
    g15: ArcOfCircle CenterX=-11.49 CenterY=50.5 CenterZ=0 NormalX=0 NormalY=0 NormalZ=1 AngleXU=0 Radius=1.5 StartAngle=4.71239 EndAngle=7.85398
    g16: ArcOfCircle CenterX=-16.28 CenterY=44.75 CenterZ=0 NormalX=0 NormalY=0 NormalZ=1 AngleXU=0 Radius=1.5 StartAngle=4.71239 EndAngle=7.85398
    g17: ArcOfCircle CenterX=-18.2337 CenterY=39 CenterZ=0 NormalX=0 NormalY=0 NormalZ=1 AngleXU=0 Radius=1.5 StartAngle=4.71485 EndAngle=7.85398
    g18: ArcOfCircle CenterX=-16.2837 CenterY=27.25 CenterZ=0 NormalX=0 NormalY=0 NormalZ=1 AngleXU=0 Radius=1.5 StartAngle=4.71485 EndAngle=7.85398
    g19: ArcOfCircle CenterX=-18.2337 CenterY=33 CenterZ=0 NormalX=0 NormalY=0 NormalZ=1 AngleXU=0 Radius=1.5 StartAngle=4.71485 EndAngle=7.85398
    g20: ArcOfCircle CenterX=-11.49 CenterY=21.5 CenterZ=0 NormalX=0 NormalY=0 NormalZ=1 AngleXU=0 Radius=1.5 StartAngle=4.71239 EndAngle=7.85398
    g21: ArcOfCircle CenterX=-1.5 CenterY=4.25 CenterZ=0 NormalX=0 NormalY=0 NormalZ=1 AngleXU=0 Radius=1.5 StartAngle=4.71239 EndAngle=7.85398
    g22: ArcOfCircle CenterX=-1.5 CenterY=10 CenterZ=0 NormalX=0 NormalY=0 NormalZ=1 AngleXU=0 Radius=1.5 StartAngle=4.71239 EndAngle=7.85398
    g23: ArcOfCircle CenterX=-1.5 CenterY=15.75 CenterZ=0 NormalX=0 NormalY=0 NormalZ=1 AngleXU=0 Radius=1.5 StartAngle=4.71239 EndAngle=7.85398
    g24: LineSegment StartX=-49.19 StartY=69.25 StartZ=0 EndX=-1.5 EndY=69.25 EndZ=0
    g25: LineSegment StartX=-49.19 StartY=66.25 StartZ=0 EndX=-1.5 EndY=66.25 EndZ=0
    g26: LineSegment StartX=-49.19 StartY=63.5 StartZ=0 EndX=-1.5 EndY=63.5 EndZ=0
    g27: LineSegment StartX=-49.19 StartY=60.5 StartZ=0 EndX=-1.5 EndY=60.5 EndZ=0
    g28: LineSegment StartX=-49.19 StartY=57.75 StartZ=0 EndX=-1.5 EndY=57.75 EndZ=0
    g29: LineSegment StartX=-49.19 StartY=54.75 StartZ=0 EndX=-1.5 EndY=54.75 EndZ=0
    g30: LineSegment StartX=-49.19 StartY=52 StartZ=0 EndX=-11.49 EndY=52 EndZ=0
    g31: LineSegment StartX=-49.19 StartY=49 StartZ=0 EndX=-11.49 EndY=49 EndZ=0
    g32: LineSegment StartX=-49.19 StartY=46.25 StartZ=0 EndX=-16.28 EndY=46.25 EndZ=0
    g33: LineSegment StartX=-49.19 StartY=43.25 StartZ=0 EndX=-16.28 EndY=43.25 EndZ=0
    g34: LineSegment StartX=-49.19 StartY=40.5 StartZ=0 EndX=-18.2337 EndY=40.5 EndZ=0
    g35: LineSegment StartX=-49.19 StartY=37.5 StartZ=0 EndX=-18.23 EndY=37.5 EndZ=0
    g36: LineSegment StartX=-49.19 StartY=34.5 StartZ=0 EndX=-18.2337 EndY=34.5 EndZ=0
    g37: LineSegment StartX=-49.19 StartY=31.5 StartZ=0 EndX=-18.23 EndY=31.5 EndZ=0
    g38: LineSegment StartX=-49.19 StartY=28.75 StartZ=0 EndX=-16.2837 EndY=28.75 EndZ=0
    g39: LineSegment StartX=-49.19 StartY=25.75 StartZ=0 EndX=-16.28 EndY=25.75 EndZ=0
    g40: LineSegment StartX=-49.19 StartY=23 StartZ=0 EndX=-11.49 EndY=23 EndZ=0
    g41: LineSegment StartX=-49.19 StartY=20 StartZ=0 EndX=-11.49 EndY=20 EndZ=0
    g42: LineSegment StartX=-49.19 StartY=17.25 StartZ=0 EndX=-1.5 EndY=17.25 EndZ=0
    g43: LineSegment StartX=-49.19 StartY=14.25 StartZ=0 EndX=-1.5 EndY=14.25 EndZ=0
    g44: LineSegment StartX=-49.19 StartY=11.5 StartZ=0 EndX=-1.5 EndY=11.5 EndZ=0
    g45: LineSegment StartX=-49.19 StartY=8.5 StartZ=0 EndX=-1.5 EndY=8.5 EndZ=0
    g46: LineSegment StartX=-49.19 StartY=5.75 StartZ=0 EndX=-1.5 EndY=5.75 EndZ=0
    g47: LineSegment StartX=-49.19 StartY=2.75 StartZ=0 EndX=-1.5 EndY=2.75 EndZ=0
  constraints (120):
    c: Vertical(g0)
    c: Distance(g0) = 3
    c: Block(g0)
    c: Vertical(g1)
    c: Distance(g1) = 3
    c: Vertical(g2)
    c: Equal(g0,g2) = 3
    c: Block(g2)
    c: Vertical(g3)
    c: Equal(g1,g3) = 3
    c: Vertical(g4)
    c: Equal(g0,g4) = 3
    c: Block(g4)
    c: Vertical(g5)
    c: Equal(g1,g5) = 3
    c: Vertical(g6)
    c: Equal(g0,g6) = 3
    c: Block(g6)
    c: Vertical(g7)
    c: Equal(g1,g7) = 3
    c: Vertical(g8)
    c: Equal(g0,g8) = 3
    c: Block(g8)
    c: Vertical(g9)
    c: Equal(g1,g9) = 3
    c: Vertical(g10)
    c: Equal(g0,g10) = 3
    c: Block(g10)
    c: Vertical(g11)
    c: Equal(g1,g11) = 3
    c: Block(g12)
    c: Block(g13)
    c: Block(g14)
    c: Block(g15)
    c: Block(g16)
    c: Block(g17)
    c: Block(g18)
    c: Block(g19)
    c: Block(g20)
    c: Block(g21)
    c: Block(g22)
    c: Block(g23)
    c: Block(g11)
    c: Block(g9)
    c: Block(g7)
    c: Block(g5)
    c: Block(g3)
    c: Block(g1)
    c: Coincident(g24,g0)
    c: Coincident(g24,g12)
    c: Horizontal(g24)
    c: Coincident(g25,g0)
    c: Coincident(g25,g12)
    c: Horizontal(g25)
    c: Coincident(g26,g1)
    c: Coincident(g26,g13)
    c: Horizontal(g26)
    c: Coincident(g27,g1)
    c: Coincident(g27,g13)
    c: Horizontal(g27)
    c: Coincident(g28,g2)
    c: Coincident(g28,g14)
    c: Horizontal(g28)
    c: Coincident(g29,g2)
    c: Coincident(g29,g14)
    c: Horizontal(g29)
    c: Coincident(g30,g3)
    c: Coincident(g30,g15)
    c: Horizontal(g30)
    c: Coincident(g31,g3)
    c: Coincident(g31,g15)
    c: Horizontal(g31)
    c: Coincident(g32,g4)
    c: Coincident(g32,g16)
    c: Horizontal(g32)
    c: Coincident(g33,g4)
    c: Coincident(g33,g16)
    c: Horizontal(g33)
    c: Coincident(g34,g5)
    c: Coincident(g34,g17)
    c: Horizontal(g34)
    c: Coincident(g35,g5)
    c: Coincident(g35,g17)
    c: Horizontal(g35)
    c: Coincident(g36,g6)
    c: Coincident(g36,g19)
    c: Horizontal(g36)
    c: Coincident(g37,g6)
    c: Coincident(g37,g19)
    c: Horizontal(g37)
    c: Coincident(g38,g7)
    c: Coincident(g38,g18)
    c: Horizontal(g38)
    c: Coincident(g39,g7)
    c: Coincident(g39,g18)
    c: Horizontal(g39)
    c: Coincident(g40,g8)
    c: Coincident(g40,g20)
    c: Horizontal(g40)
    c: Coincident(g41,g8)
    c: Coincident(g41,g20)
    c: Horizontal(g41)
    c: Coincident(g42,g9)
    c: Coincident(g42,g23)
    c: Horizontal(g42)
    c: Coincident(g43,g9)
    c: Coincident(g43,g23)
    c: Horizontal(g43)
    c: Coincident(g44,g10)
    c: Coincident(g44,g22)
    c: Horizontal(g44)
    c: Coincident(g45,g10)
    c: Coincident(g45,g22)
    c: Horizontal(g45)
    c: Coincident(g46,g11)
    c: Coincident(g46,g21)
    c: Horizontal(g46)
    c: Coincident(g47,g11)
    c: Coincident(g47,g21)
    c: Horizontal(g47)
FEATURE [Part::Extrusion] Extrude023
  Base = -> Sketch032
  Dir = (1,-2e-16,2e-16)
  DirMode = 2
  FaceMakerClass = Part::FaceMakerBullseye
  LengthFwd = 19
  LengthRev = 0
  Placement = pos=(-19,0,0) rot=(0,0,1;0rad)
  Solid = true
  Symmetric = false
FEATURE [Part::Fillet] Fillet023
  Base = -> Extrude023
  Edges = <same value as first occurrence — deduplicated (x6 in doc)>
  Placement = pos=(0,0.05,0) rot=(0,0,1;0rad)
FEATURE [Part::Cut] Cut014  label="bottom003"
  Base = -> Cut007
  Tool = -> Fusion047
FEATURE [Part::Cut] Cut021  label="bottom004"
  Base = -> Cut014
  Tool = -> Fillet023
FEATURE [Sketcher::SketchObject] Sketch033
  FullyConstrained = true
  Placement = pos=(117,19,0) rot=(0.57735,0.57735,0.57735;2.0944rad)
  sketch-geometry (8):
    g0: LineSegment StartX=-49.19 StartY=69.25 StartZ=0 EndX=-49.19 EndY=66.25 EndZ=0
    g1: LineSegment StartX=-49.19 StartY=5.75 StartZ=0 EndX=-49.19 EndY=2.75 EndZ=0
    g2: ArcOfCircle CenterX=-1.5 CenterY=67.75 CenterZ=0 NormalX=0 NormalY=0 NormalZ=1 AngleXU=0 Radius=1.5 StartAngle=4.71239 EndAngle=7.85398
    g3: ArcOfCircle CenterX=-1.5 CenterY=4.25 CenterZ=0 NormalX=0 NormalY=0 NormalZ=1 AngleXU=0 Radius=1.5 StartAngle=4.71239 EndAngle=7.85398
    g4: LineSegment StartX=-49.19 StartY=69.25 StartZ=0 EndX=-1.5 EndY=69.25 EndZ=0
    g5: LineSegment StartX=-49.19 StartY=66.25 StartZ=0 EndX=-1.5 EndY=66.25 EndZ=0
    g6: LineSegment StartX=-49.19 StartY=5.75 StartZ=0 EndX=-1.5 EndY=5.75 EndZ=0
    g7: LineSegment StartX=-49.19 StartY=2.75 StartZ=0 EndX=-1.5 EndY=2.75 EndZ=0
  constraints (19):
    c: Vertical(g0)
    c: Distance(g0) = 3
    c: Block(g0)
    c: Vertical(g1)
    c: Block(g2)
    c: Block(g3)
    c: Block(g1)
    c: Coincident(g4,g0)
    c: Coincident(g4,g2)
    c: Horizontal(g4)
    c: Coincident(g5,g0)
    c: Coincident(g5,g2)
    c: Horizontal(g5)
    c: Coincident(g6,g1)
    c: Coincident(g6,g3)
    c: Horizontal(g6)
    c: Coincident(g7,g1)
    c: Coincident(g7,g3)
    c: Horizontal(g7)
FEATURE [Sketcher::SketchObject] Sketch034
  FullyConstrained = true
  Placement = pos=(117,19,0) rot=(0.57735,0.57735,0.57735;2.0944rad)
  sketch-geometry (8):
    g0: LineSegment StartX=-49.19 StartY=63.5 StartZ=0 EndX=-49.19 EndY=60.5 EndZ=0
    g1: LineSegment StartX=-49.19 StartY=11.5 StartZ=0 EndX=-49.19 EndY=8.5 EndZ=0
    g2: ArcOfCircle CenterX=-1.5 CenterY=62 CenterZ=0 NormalX=0 NormalY=0 NormalZ=1 AngleXU=0 Radius=1.5 StartAngle=4.71239 EndAngle=7.85398
    g3: ArcOfCircle CenterX=-1.5 CenterY=10 CenterZ=0 NormalX=0 NormalY=0 NormalZ=1 AngleXU=0 Radius=1.5 StartAngle=4.71239 EndAngle=7.85398
    g4: LineSegment StartX=-49.19 StartY=63.5 StartZ=0 EndX=-1.5 EndY=63.5 EndZ=0
    g5: LineSegment StartX=-49.19 StartY=60.5 StartZ=0 EndX=-1.5 EndY=60.5 EndZ=0
    g6: LineSegment StartX=-49.19 StartY=11.5 StartZ=0 EndX=-1.5 EndY=11.5 EndZ=0
    g7: LineSegment StartX=-49.19 StartY=8.5 StartZ=0 EndX=-1.5 EndY=8.5 EndZ=0
  constraints (19):
    c: Vertical(g0)
    c: Distance(g0) = 3
    c: Vertical(g1)
    c: Block(g1)
    c: Block(g2)
    c: Block(g3)
    c: Block(g0)
    c: Coincident(g4,g0)
    c: Coincident(g4,g2)
    c: Horizontal(g4)
    c: Coincident(g5,g0)
    c: Coincident(g5,g2)
    c: Horizontal(g5)
    c: Coincident(g6,g1)
    c: Coincident(g6,g3)
    c: Horizontal(g6)
    c: Coincident(g7,g1)
    c: Coincident(g7,g3)
    c: Horizontal(g7)
FEATURE [Part::Extrusion] Extrude024
  Base = -> Sketch033
  Dir = (1,0,0)
  DirMode = 2
  FaceMakerClass = Part::FaceMakerBullseye
  LengthFwd = 10
  LengthRev = 0
  Solid = true
  Symmetric = false
FEATURE [Part::Extrusion] Extrude025
  Base = -> Sketch034
  Dir = (1,0,0)
  DirMode = 2
  FaceMakerClass = Part::FaceMakerBullseye
  LengthFwd = 10
  LengthRev = 0
  Solid = true
  Symmetric = false
FEATURE [Part::Fillet] Fillet024  label="removeFromtMoreFrontCaseScrewRetainers"
  Base = -> Extrude024
  Edges = 4 edges r=1.49: [Edge6,Edge11,Edge18,Edge23]
  Placement = pos=(-11,0,0) rot=(0,0,1;0rad)
FEATURE [Part::Fillet] Fillet025  label="removeFromtMoreFrontCaseScrewRetainers001"
  Base = -> Extrude025
  Edges = 4 edges r=1.49: [Edge6,Edge11,Edge18,Edge23]
  Placement = pos=(-19,0,0) rot=(0,0,1;0rad)
FEATURE [Part::Cut] Cut022
  Base = -> Cut015
  Tool = -> Fillet025
FEATURE [Part::Cut] Cut023  label="screwRetainers"
  Base = -> Cut022
  Tool = -> Fillet024
FEATURE [Part::MultiFuse] Fusion056  label="bottom005"
  Shapes = -> [Fusion044,Cut021]
FEATURE [Part::MultiFuse] Fusion057  label="casePillars001"
  Shapes = -> [Cut016,Fusion052]
FEATURE [Part::MultiFuse] Fusion058  label="bottom006"
  Shapes = -> [Fusion056,Cut023]
FEATURE [Part::MultiFuse] Fusion059  label="bottom007"
  Shapes = -> [Fusion058,Fillet005]
FEATURE [Part::MultiFuse] Fusion060  label="bottom008"
  Shapes = -> [Fusion059,Fusion]
FEATURE [Part::MultiFuse] Fusion061  label="top011"
  Shapes = -> [Cut006,Cut020]
FEATURE [Part::MultiFuse] Fusion062  label="top012"
  Shapes = -> [Fusion057,Fusion061]
FEATURE [Sketcher::SketchObject] Sketch035  label="topSketch007"
  FullyConstrained = true
  sketch-geometry (6):
    g0: LineSegment StartX=19 StartY=38 StartZ=0 EndX=117 EndY=38 EndZ=0
    g1: ArcOfCircle CenterX=19 CenterY=19 CenterZ=0 NormalX=0 NormalY=0 NormalZ=1 AngleXU=0 Radius=19 StartAngle=1.5708 EndAngle=3.14159
    g2: LineSegment StartX=117 StartY=38 StartZ=0 EndX=117 EndY=19 EndZ=0
    g3: LineSegment StartX=98 StartY=1.0161e-12 StartZ=0 EndX=5.22862e-06 EndY=1.0161e-12 EndZ=0
    g4: LineSegment StartX=5.22862e-06 StartY=19 StartZ=0 EndX=5.22862e-06 EndY=1.0161e-12 EndZ=0
    g5: ArcOfCircle CenterX=98 CenterY=19 CenterZ=0 NormalX=0 NormalY=0 NormalZ=1 AngleXU=0 Radius=19 StartAngle=4.71239 EndAngle=6.28319
  constraints (16):
    c: Horizontal(g0)
    c: Distance(g0) = 98
    c: Coincident(g1,g0)
    c: Block(g1)
    c: Coincident(g2,g0)
    c: Vertical(g2)
    c: Distance(g2) = 19
    c: Horizontal(g3)
    c: Coincident(g4,g1)
    c: Vertical(g4)
    c: Coincident(g3,g4)
    c: Block(g3)
    c: Coincident(g5,g2)
    c: Coincident(g5,g3)
    c: Block(g0)
    c: Block(g5)
FEATURE [Part::Extrusion] Extrude026  label="sideA001"
  Base = -> Sketch035
  Dir = (0,0,1)
  DirMode = 2
  FaceMakerClass = Part::FaceMakerBullseye
  LengthFwd = 3
  LengthRev = 0
  Placement = pos=(0,0,-2.7) rot=(0,0,1;0rad)
  Solid = true
  Symmetric = false
FEATURE [Sketcher::SketchObject] Sketch036  label="topSketch008"
  FullyConstrained = true
  sketch-geometry (6):
    g0: LineSegment StartX=19 StartY=38 StartZ=0 EndX=117 EndY=38 EndZ=0
    g1: ArcOfCircle CenterX=19 CenterY=19 CenterZ=0 NormalX=0 NormalY=0 NormalZ=1 AngleXU=0 Radius=19 StartAngle=1.5708 EndAngle=3.14159
    g2: LineSegment StartX=117 StartY=38 StartZ=0 EndX=117 EndY=19 EndZ=0
    g3: LineSegment StartX=98 StartY=1.0161e-12 StartZ=0 EndX=5.22862e-06 EndY=1.0161e-12 EndZ=0
    g4: LineSegment StartX=5.22862e-06 StartY=19 StartZ=0 EndX=5.22862e-06 EndY=1.0161e-12 EndZ=0
    g5: ArcOfCircle CenterX=98 CenterY=19 CenterZ=0 NormalX=0 NormalY=0 NormalZ=1 AngleXU=0 Radius=19 StartAngle=4.71239 EndAngle=6.28319
  constraints (16):
    c: Horizontal(g0)
    c: Distance(g0) = 98
    c: Coincident(g1,g0)
    c: Block(g1)
    c: Coincident(g2,g0)
    c: Vertical(g2)
    c: Distance(g2) = 19
    c: Horizontal(g3)
    c: Coincident(g4,g1)
    c: Vertical(g4)
    c: Coincident(g3,g4)
    c: Block(g3)
    c: Coincident(g5,g2)
    c: Coincident(g5,g3)
    c: Block(g0)
    c: Block(g5)
FEATURE [Part::Extrusion] Extrude027  label="sideB001"
  Base = -> Sketch036
  Dir = (0,0,1)
  DirMode = 2
  FaceMakerClass = Part::FaceMakerBullseye
  LengthFwd = 3
  LengthRev = 0
  Placement = pos=(0,0,71.7) rot=(0,0,1;0rad)
  Solid = true
  Symmetric = false
FEATURE [Part::MultiFuse] Fusion064  label="removeFromBottom"
  Shapes = -> [Extrude026,Extrude027]
FEATURE [Part::Cut] Cut024  label="bottom009"
  Base = -> Fusion060
  Tool = -> Fusion064
FEATURE [Sketcher::SketchObject] Sketch037  label="topSketch009"
  FullyConstrained = true
  sketch-geometry (8):
    g0: ArcOfCircle CenterX=19 CenterY=19.1201 CenterZ=0 NormalX=0 NormalY=0 NormalZ=1 AngleXU=0 Radius=18.8799 StartAngle=1.5708 EndAngle=3.14793
    g1: LineSegment StartX=0.120501 StartY=19.0004 StartZ=0 EndX=0.120501 EndY=0.000382114 EndZ=0
    g2: LineSegment StartX=19 StartY=38 StartZ=0 EndX=124 EndY=38 EndZ=0
    g3: LineSegment StartX=0.120501 StartY=0.000382114 StartZ=0 EndX=105.121 EndY=0.000382114 EndZ=0
    g4: LineSegment StartX=124 StartY=38 StartZ=0 EndX=125.616 EndY=38 EndZ=0
    g5: LineSegment StartX=105.121 StartY=0.000382114 StartZ=0 EndX=106.736 EndY=0.000382114 EndZ=0
    g6: ArcOfCircle CenterX=106.616 CenterY=19 CenterZ=0 NormalX=0 NormalY=0 NormalZ=1 AngleXU=0 Radius=19 StartAngle=4.71873 EndAngle=6.28319
    g7: LineSegment StartX=125.616 StartY=38 StartZ=0 EndX=125.616 EndY=19 EndZ=0
  constraints (21):
    c: Block(g0)
    c: Coincident(g1,g0)
    c: Vertical(g1)
    c: Horizontal(g2)
    c: Distance(g2) = 105
    c: Coincident(g2,g0)
    c: Distance(g1) = 19
    c: Coincident(g3,g1)
    c: Horizontal(g3)
    c: Distance(g3) = 105
    c: Coincident(g4,g2)
    c: Horizontal(g4)
    c: Distance(g4) = 1.61553
    c: Horizontal(g5)
    c: Equal(g4,g5) = 1.61553
    c: Coincident(g5,g3)
    c: Block(g6)
    c: Coincident(g6,g5)
    c: Coincident(g7,g4)
    c: Coincident(g7,g6)
    c: Vertical(g7)
FEATURE [Part::Extrusion] Extrude028  label="sideB"
  Base = -> Sketch037
  Dir = (0,0,1)
  DirMode = 2
  FaceMakerClass = Part::FaceMakerBullseye
  LengthFwd = 3
  LengthRev = 0
  Placement = pos=(0,0,72) rot=(0,0,1;0rad)
  Solid = true
  Symmetric = false
FEATURE [Sketcher::SketchObject] Sketch038  label="topSketch010"
  FullyConstrained = true
  sketch-geometry (22):
    g0: LineSegment StartX=5.21097e-06 StartY=3 StartZ=0 EndX=5.21097e-06 EndY=19 EndZ=0
    g1: ArcOfCircle CenterX=19 CenterY=19 CenterZ=0 NormalX=0 NormalY=0 NormalZ=1 AngleXU=0 Radius=19 StartAngle=1.5708 EndAngle=3.14159
    g2: ArcOfCircle CenterX=19 CenterY=19 CenterZ=0 NormalX=0 NormalY=0 NormalZ=1 AngleXU=0 Radius=16 StartAngle=1.5708 EndAngle=3.14159
    g3: LineSegment StartX=114 StartY=35 StartZ=0 EndX=19 EndY=35 EndZ=0
    g4: LineSegment StartX=5.21097e-06 StartY=3 StartZ=0 EndX=5.21097e-06 EndY=0 EndZ=0
    g5: LineSegment StartX=3 StartY=0 StartZ=0 EndX=5.21097e-06 EndY=0 EndZ=0
    g6: LineSegment StartX=3 StartY=19 StartZ=0 EndX=3 EndY=0 EndZ=0
    g7: LineSegment StartX=19 StartY=38 StartZ=0 EndX=124 EndY=38 EndZ=0
    g8: Circle CenterX=119 CenterY=35 CenterZ=0 NormalX=0 NormalY=0 NormalZ=1 AngleXU=0 Radius=1
    g9: Circle CenterX=121 CenterY=35 CenterZ=0 NormalX=0 NormalY=0 NormalZ=1 AngleXU=0 Radius=1
    g10: Circle CenterX=121 CenterY=33 CenterZ=0 NormalX=0 NormalY=0 NormalZ=1 AngleXU=0 Radius=1
    g11: BSplineCurve PolesCount=3 KnotsCount=2 Degree=2 IsPeriodic=0
    g12: GeomPoint X=119 Y=35 Z=0
    g13: GeomPoint X=121 Y=33 Z=0
    g14: LineSegment StartX=119 StartY=35 StartZ=0 EndX=114 EndY=35 EndZ=0
    g15: ArcOfCircle CenterX=105 CenterY=19 CenterZ=0 NormalX=0 NormalY=0 NormalZ=1 AngleXU=0 Radius=16 StartAngle=5.60905 EndAngle=6.28319
    g16: LineSegment StartX=121 StartY=33 StartZ=0 EndX=121 EndY=19 EndZ=0
    g17: LineSegment StartX=117.5 StartY=9.01251 StartZ=0 EndX=121.163 EndY=9.0125 EndZ=0
    g18: ArcOfCircle CenterX=105 CenterY=19 CenterZ=0 NormalX=0 NormalY=0 NormalZ=1 AngleXU=0 Radius=20.6155 StartAngle=5.7297 EndAngle=6.28319
    g19: LineSegment StartX=121.163 StartY=9.0125 StartZ=0 EndX=122.538 EndY=8.16329 EndZ=0
    g20: LineSegment StartX=124 StartY=38 StartZ=0 EndX=125.616 EndY=38 EndZ=0
    g21: LineSegment StartX=125.616 StartY=19 StartZ=0 EndX=125.616 EndY=38 EndZ=0
  constraints (49):
    c: Vertical(g0)
    c: Block(g0)
    c: Coincident(g1,g0)
    c: Block(g1)
    c: Coincident(g2,g1)
    c: Block(g2)
    c: Coincident(g3,g2)
    c: Horizontal(g3)
    c: Tangent(g3,g2)
    c: Coincident(g4,g0)
    c: Distance(g4) = 3
    c: Vertical(g4)
    c: Coincident(g5,g4)
    c: Horizontal(g5)
    c: Coincident(g6,g2)
    c: Coincident(g6,g5)
    c: Vertical(g6)
    c: Horizontal(g7)
    c: Distance(g7) = 105
    c: Coincident(g7,g1)
    c: Block(g3)
    c: Weight(g8) = 1
    c: Equal(g8,g9)
    c: Equal(g8,g10)
    c: InternalAlignment(g8,g11)
    c: InternalAlignment(g9,g11)
    c: InternalAlignment(g10,g11)
    c: InternalAlignment(g12,g11)
    c: InternalAlignment(g13,g11)
    c: Block(g11)
    c: Coincident(g14,g11)
    c: Coincident(g14,g3)
    c: Horizontal(g14)
    c: Block(g15)
    c: Coincident(g16,g11)
    c: Coincident(g16,g15)
    c: Vertical(g16)
    c: Distance(g16) = 14
    c: Coincident(g17,g15)
    c: Block(g18)
    c: Coincident(g19,g18)
    c: Coincident(g20,g7)
    c: Horizontal(g20)
    c: Vertical(g21)
    c: Coincident(g20,g21)
    c: Block(g20)
    c: Block(g21)
    c: Block(g19)
    c: Block(g17)
FEATURE [Part::Extrusion] Extrude029
  Base = -> Sketch038
  Dir = (0,0,1)
  DirMode = 2
  FaceMakerClass = Part::FaceMakerBullseye
  LengthFwd = 72
  LengthRev = 0
  Solid = true
  Symmetric = false
FEATURE [Part::Feature] Face085
  shape: bbox 4.8 x 25.5 x 2e-07 mm, 1 faces, 0 solids (baked)
FEATURE [Part::Revolution] Revolve089  label="moreFrontCaseScrewPost003"
  Angle = 360
  Axis = (0,1,0)
  Base = (0,0,0)
  FaceMakerClass = Part::FaceMakerBullseye
  Placement = pos=(109.5,4.5,3.5) rot=(0,0,1;0rad)
  Solid = false
  Source = -> Face085
  Symmetric = false
FEATURE [Part::Feature] Face086
  shape: bbox 4.8 x 25.5 x 2e-07 mm, 1 faces, 0 solids (baked)
FEATURE [Part::Revolution] Revolve090  label="moreFrontCaseScrewPost004"
  Angle = 360
  Axis = (0,1,0)
  Base = (0,0,0)
  FaceMakerClass = Part::FaceMakerBullseye
  Placement = pos=(109.5,4.5,68.5) rot=(0,0,1;0rad)
  Solid = false
  Source = -> Face086
  Symmetric = false
FEATURE [Part::Fillet] Fillet026  label="top013"
  Base = -> Extrude029
  Edges = 1 edges r=2: [Edge35]
FEATURE [Sketcher::SketchObject] Sketch039
  FullyConstrained = true
  sketch-geometry (7):
    g0: LineSegment StartX=0 StartY=0 StartZ=0 EndX=0 EndY=6 EndZ=0
    g1: Circle CenterX=0 CenterY=0 CenterZ=0 NormalX=0 NormalY=0 NormalZ=1 AngleXU=0 Radius=1
    g2: Circle CenterX=8 CenterY=6 CenterZ=0 NormalX=0 NormalY=0 NormalZ=1 AngleXU=0 Radius=1
    g3: BSplineCurve PolesCount=3 KnotsCount=2 Degree=2 IsPeriodic=0
    g4: GeomPoint X=0 Y=0 Z=0
    g5: GeomPoint X=8 Y=6 Z=0
    g6: LineSegment StartX=0 StartY=6 StartZ=0 EndX=8 EndY=6 EndZ=0
  constraints (14):
    c: Coincident(g0,g-1)
    c: Distance(g0) = 6
    c: Vertical(g0)
    c: Coincident(g3,g0)
    c: Weight(g1) = 1
    c: Equal(g1,g2)
    c: InternalAlignment(g1,g3)
    c: InternalAlignment(g2,g3)
    c: InternalAlignment(g4,g3)
    c: InternalAlignment(g5,g3)
    c: Block(g3)
    c: Coincident(g6,g0)
    c: Coincident(g6,g3)
    c: Horizontal(g6)
FEATURE [Sketcher::SketchObject] Sketch040
  FullyConstrained = true
  sketch-geometry (7):
    g0: LineSegment StartX=0 StartY=0 StartZ=0 EndX=0 EndY=6 EndZ=0
    g1: Circle CenterX=0 CenterY=0 CenterZ=0 NormalX=0 NormalY=0 NormalZ=1 AngleXU=0 Radius=1
    g2: Circle CenterX=8 CenterY=6 CenterZ=0 NormalX=0 NormalY=0 NormalZ=1 AngleXU=0 Radius=1
    g3: BSplineCurve PolesCount=3 KnotsCount=2 Degree=2 IsPeriodic=0
    g4: GeomPoint X=0 Y=0 Z=0
    g5: GeomPoint X=8 Y=6 Z=0
    g6: LineSegment StartX=0 StartY=6 StartZ=0 EndX=8 EndY=6 EndZ=0
  constraints (14):
    c: Coincident(g0,g-1)
    c: Distance(g0) = 6
    c: Vertical(g0)
    c: Coincident(g3,g0)
    c: Weight(g1) = 1
    c: Equal(g1,g2)
    c: InternalAlignment(g1,g3)
    c: InternalAlignment(g2,g3)
    c: InternalAlignment(g4,g3)
    c: InternalAlignment(g5,g3)
    c: Block(g3)
    c: Coincident(g6,g0)
    c: Coincident(g6,g3)
    c: Horizontal(g6)
FEATURE [Sketcher::SketchObject] Sketch041
  FullyConstrained = true
  sketch-geometry (7):
    g0: LineSegment StartX=0 StartY=0 StartZ=0 EndX=0 EndY=6 EndZ=0
    g1: Circle CenterX=0 CenterY=0 CenterZ=0 NormalX=0 NormalY=0 NormalZ=1 AngleXU=0 Radius=1
    g2: Circle CenterX=8 CenterY=6 CenterZ=0 NormalX=0 NormalY=0 NormalZ=1 AngleXU=0 Radius=1
    g3: BSplineCurve PolesCount=3 KnotsCount=2 Degree=2 IsPeriodic=0
    g4: GeomPoint X=0 Y=0 Z=0
    g5: GeomPoint X=8 Y=6 Z=0
    g6: LineSegment StartX=0 StartY=6 StartZ=0 EndX=8 EndY=6 EndZ=0
  constraints (14):
    c: Coincident(g0,g-1)
    c: Distance(g0) = 6
    c: Vertical(g0)
    c: Coincident(g3,g0)
    c: Weight(g1) = 1
    c: Equal(g1,g2)
    c: InternalAlignment(g1,g3)
    c: InternalAlignment(g2,g3)
    c: InternalAlignment(g4,g3)
    c: InternalAlignment(g5,g3)
    c: Block(g3)
    c: Coincident(g6,g0)
    c: Coincident(g6,g3)
    c: Horizontal(g6)
FEATURE [Sketcher::SketchObject] Sketch042
  FullyConstrained = true
  sketch-geometry (7):
    g0: LineSegment StartX=0 StartY=0 StartZ=0 EndX=0 EndY=6 EndZ=0
    g1: Circle CenterX=0 CenterY=0 CenterZ=0 NormalX=0 NormalY=0 NormalZ=1 AngleXU=0 Radius=1
    g2: Circle CenterX=8 CenterY=6 CenterZ=0 NormalX=0 NormalY=0 NormalZ=1 AngleXU=0 Radius=1
    g3: BSplineCurve PolesCount=3 KnotsCount=2 Degree=2 IsPeriodic=0
    g4: GeomPoint X=0 Y=0 Z=0
    g5: GeomPoint X=8 Y=6 Z=0
    g6: LineSegment StartX=0 StartY=6 StartZ=0 EndX=8 EndY=6 EndZ=0
  constraints (14):
    c: Coincident(g0,g-1)
    c: Distance(g0) = 6
    c: Vertical(g0)
    c: Coincident(g3,g0)
    c: Weight(g1) = 1
    c: Equal(g1,g2)
    c: InternalAlignment(g1,g3)
    c: InternalAlignment(g2,g3)
    c: InternalAlignment(g4,g3)
    c: InternalAlignment(g5,g3)
    c: Block(g3)
    c: Coincident(g6,g0)
    c: Coincident(g6,g3)
    c: Horizontal(g6)
FEATURE [Part::Extrusion] Extrude030  label="caseScrewPillarBracket008"
  Base = -> Sketch039
  Dir = (0,0,1)
  DirMode = 2
  FaceMakerClass = Part::FaceMakerBullseye
  LengthFwd = 2.4
  LengthRev = 0
  Placement = pos=(15.76,29,8.8) rot=(0,1,0;0rad)
  Solid = true
  Symmetric = false
FEATURE [Part::Extrusion] Extrude031  label="caseScrewPillarBracket009"
  Base = -> Sketch040
  Dir = (0,0,1)
  DirMode = 2
  FaceMakerClass = Part::FaceMakerBullseye
  LengthFwd = 2.4
  LengthRev = 0
  Placement = pos=(15.76,29,60.8) rot=(0,0,1;0rad)
  Solid = true
  Symmetric = false
FEATURE [Part::Extrusion] Extrude032  label="caseScrewPillarBracket010"
  Base = -> Sketch041
  Dir = (0,0,1)
  DirMode = 2
  FaceMakerClass = Part::FaceMakerBullseye
  LengthFwd = 2.4
  LengthRev = 0
  Placement = pos=(13.7,29,13.26) rot=(0,-1,0;1.5708rad)
  Solid = true
  Symmetric = false
FEATURE [Part::Extrusion] Extrude033  label="caseScrewPillarBracket011"
  Base = -> Sketch042
  Dir = (0,0,1)
  DirMode = 2
  FaceMakerClass = Part::FaceMakerBullseye
  LengthFwd = 2.4
  LengthRev = 0
  Placement = pos=(11.3,29,58.74) rot=(0,1,0;1.5708rad)
  Solid = true
  Symmetric = false
FEATURE [Sketcher::SketchObject] Sketch043
  FullyConstrained = true
  sketch-geometry (7):
    g0: LineSegment StartX=0 StartY=0 StartZ=0 EndX=0 EndY=6 EndZ=0
    g1: Circle CenterX=0 CenterY=0 CenterZ=0 NormalX=0 NormalY=0 NormalZ=1 AngleXU=0 Radius=1
    g2: Circle CenterX=8 CenterY=6 CenterZ=0 NormalX=0 NormalY=0 NormalZ=1 AngleXU=0 Radius=1
    g3: BSplineCurve PolesCount=3 KnotsCount=2 Degree=2 IsPeriodic=0
    g4: GeomPoint X=0 Y=0 Z=0
    g5: GeomPoint X=8 Y=6 Z=0
    g6: LineSegment StartX=0 StartY=6 StartZ=0 EndX=8 EndY=6 EndZ=0
  constraints (14):
    c: Coincident(g0,g-1)
    c: Distance(g0) = 6
    c: Vertical(g0)
    c: Coincident(g3,g0)
    c: Weight(g1) = 1
    c: Equal(g1,g2)
    c: InternalAlignment(g1,g3)
    c: InternalAlignment(g2,g3)
    c: InternalAlignment(g4,g3)
    c: InternalAlignment(g5,g3)
    c: Block(g3)
    c: Coincident(g6,g0)
    c: Coincident(g6,g3)
    c: Horizontal(g6)
FEATURE [Part::Extrusion] Extrude034  label="caseScrewPillarBracket012"
  Base = -> Sketch043
  Dir = (0,0,1)
  DirMode = 2
  FaceMakerClass = Part::FaceMakerBullseye
  LengthFwd = 2.4
  LengthRev = 0
  Placement = pos=(88.3,29,65.23) rot=(0,1,0;1.5708rad)
  Solid = true
  Symmetric = false
FEATURE [Sketcher::SketchObject] Sketch044
  FullyConstrained = true
  sketch-geometry (7):
    g0: LineSegment StartX=0 StartY=0 StartZ=0 EndX=0 EndY=6 EndZ=0
    g1: Circle CenterX=0 CenterY=0 CenterZ=0 NormalX=0 NormalY=0 NormalZ=1 AngleXU=0 Radius=1
    g2: Circle CenterX=8 CenterY=6 CenterZ=0 NormalX=0 NormalY=0 NormalZ=1 AngleXU=0 Radius=1
    g3: BSplineCurve PolesCount=3 KnotsCount=2 Degree=2 IsPeriodic=0
    g4: GeomPoint X=0 Y=0 Z=0
    g5: GeomPoint X=8 Y=6 Z=0
    g6: LineSegment StartX=0 StartY=6 StartZ=0 EndX=8 EndY=6 EndZ=0
  constraints (14):
    c: Coincident(g0,g-1)
    c: Distance(g0) = 6
    c: Vertical(g0)
    c: Coincident(g3,g0)
    c: Weight(g1) = 1
    c: Equal(g1,g2)
    c: InternalAlignment(g1,g3)
    c: InternalAlignment(g2,g3)
    c: InternalAlignment(g4,g3)
    c: InternalAlignment(g5,g3)
    c: Block(g3)
    c: Coincident(g6,g0)
    c: Coincident(g6,g3)
    c: Horizontal(g6)
FEATURE [Part::Extrusion] Extrude035  label="caseScrewPillarBracket013"
  Base = -> Sketch044
  Dir = (0,0,1)
  DirMode = 2
  FaceMakerClass = Part::FaceMakerBullseye
  LengthFwd = 2.4
  LengthRev = 0
  Placement = pos=(90.7,29,6.77) rot=(0,-1,0;1.5708rad)
  Solid = true
  Symmetric = false
FEATURE [Sketcher::SketchObject] Sketch045
  FullyConstrained = true
  sketch-geometry (7):
    g0: LineSegment StartX=0 StartY=0 StartZ=0 EndX=0 EndY=6 EndZ=0
    g1: Circle CenterX=0 CenterY=0 CenterZ=0 NormalX=0 NormalY=0 NormalZ=1 AngleXU=0 Radius=1
    g2: Circle CenterX=8 CenterY=6 CenterZ=0 NormalX=0 NormalY=0 NormalZ=1 AngleXU=0 Radius=1
    g3: BSplineCurve PolesCount=3 KnotsCount=2 Degree=2 IsPeriodic=0
    g4: GeomPoint X=0 Y=0 Z=0
    g5: GeomPoint X=8 Y=6 Z=0
    g6: LineSegment StartX=0 StartY=6 StartZ=0 EndX=8 EndY=6 EndZ=0
  constraints (14):
    c: Coincident(g0,g-1)
    c: Distance(g0) = 6
    c: Vertical(g0)
    c: Coincident(g3,g0)
    c: Weight(g1) = 1
    c: Equal(g1,g2)
    c: InternalAlignment(g1,g3)
    c: InternalAlignment(g2,g3)
    c: InternalAlignment(g4,g3)
    c: InternalAlignment(g5,g3)
    c: Block(g3)
    c: Coincident(g6,g0)
    c: Coincident(g6,g3)
    c: Horizontal(g6)
FEATURE [Sketcher::SketchObject] Sketch046
  FullyConstrained = true
  sketch-geometry (7):
    g0: LineSegment StartX=0 StartY=0 StartZ=0 EndX=0 EndY=6 EndZ=0
    g1: Circle CenterX=0 CenterY=0 CenterZ=0 NormalX=0 NormalY=0 NormalZ=1 AngleXU=0 Radius=1
    g2: Circle CenterX=8 CenterY=6 CenterZ=0 NormalX=0 NormalY=0 NormalZ=1 AngleXU=0 Radius=1
    g3: BSplineCurve PolesCount=3 KnotsCount=2 Degree=2 IsPeriodic=0
    g4: GeomPoint X=0 Y=0 Z=0
    g5: GeomPoint X=8 Y=6 Z=0
    g6: LineSegment StartX=0 StartY=6 StartZ=0 EndX=8 EndY=6 EndZ=0
  constraints (14):
    c: Coincident(g0,g-1)
    c: Distance(g0) = 6
    c: Vertical(g0)
    c: Coincident(g3,g0)
    c: Weight(g1) = 1
    c: Equal(g1,g2)
    c: InternalAlignment(g1,g3)
    c: InternalAlignment(g2,g3)
    c: InternalAlignment(g4,g3)
    c: InternalAlignment(g5,g3)
    c: Block(g3)
    c: Coincident(g6,g0)
    c: Coincident(g6,g3)
    c: Horizontal(g6)
FEATURE [Part::Extrusion] Extrude036  label="caseScrewPillarBracket014"
  Base = -> Sketch045
  Dir = (0,0,1)
  DirMode = 2
  FaceMakerClass = Part::FaceMakerBullseye
  LengthFwd = 2.4
  LengthRev = 0
  Placement = pos=(110.7,29,6.77) rot=(0,-1,0;1.5708rad)
  Solid = true
  Symmetric = false
FEATURE [Part::Extrusion] Extrude037  label="caseScrewPillarBracket015"
  Base = -> Sketch046
  Dir = (0,0,1)
  DirMode = 2
  FaceMakerClass = Part::FaceMakerBullseye
  LengthFwd = 2.4
  LengthRev = 0
  Placement = pos=(108.3,29,65.23) rot=(0,1,0;1.5708rad)
  Solid = true
  Symmetric = false
FEATURE [Part::Box] Box013  label="frontCaseScrewPillarBracket002"
  AttacherType = Attacher::AttachEngine3D
  Height = 2.4
  Length = 22
  Placement = pos=(87,28,2.3) rot=(0,0,1;0rad)
  Width = 7
FEATURE [Part::Box] Box014  label="frontCaseScrewPillarBracket003"
  AttacherType = Attacher::AttachEngine3D
  Height = 2.4
  Length = 22
  Placement = pos=(87,28,67.3) rot=(0,0,1;0rad)
  Width = 7
FEATURE [Part::Feature] Face087
  shape: bbox 4.8 x 30.2 x 2e-07 mm, 1 faces, 0 solids (baked)
FEATURE [Part::Revolution] Revolve091  label="frontCaseScrewPost004"
  Angle = 360
  Axis = (0,1,0)
  Base = (0,0,0)
  FaceMakerClass = Part::FaceMakerBullseye
  Placement = pos=(89.5,4.5,3.5) rot=(0,0,1;0rad)
  Solid = false
  Source = -> Face087
  Symmetric = false
FEATURE [Part::Feature] Face088
  shape: bbox 4.8 x 30.2 x 2e-07 mm, 1 faces, 0 solids (baked)
FEATURE [Part::Revolution] Revolve092  label="frontCaseScrewPost005"
  Angle = 360
  Axis = (0,1,0)
  Base = (0,0,0)
  FaceMakerClass = Part::FaceMakerBullseye
  Placement = pos=(89.5,4.5,68.5) rot=(0,0,1;0rad)
  Solid = false
  Source = -> Face088
  Symmetric = false
FEATURE [Part::Feature] Face089
  shape: bbox 3.5 x 30.2 x 2e-07 mm, 1 faces, 0 solids (baked)
FEATURE [Part::Revolution] Revolve093  label="backCaseScrewPost002"
  Angle = 360
  Axis = (0,1,0)
  Base = (0,0,0)
  FaceMakerClass = Part::FaceMakerBullseye
  Placement = pos=(12.5,4.5,10) rot=(0,0,1;0rad)
  Solid = false
  Source = -> Face089
  Symmetric = false
FEATURE [Part::Feature] Face090
  shape: bbox 3.5 x 30.2 x 2e-07 mm, 1 faces, 0 solids (baked)
FEATURE [Part::Revolution] Revolve094  label="backCaseScrewPost003"
  Angle = 360
  Axis = (0,1,0)
  Base = (0,0,0)
  FaceMakerClass = Part::FaceMakerBullseye
  Placement = pos=(12.5,4.5,62) rot=(0,0,1;0rad)
  Solid = false
  Source = -> Face090
  Symmetric = false
FEATURE [Part::Box] Box015  label="Cube011"
  AttacherType = Attacher::AttachEngine3D
  Height = 28.8
  Length = 3
  Placement = pos=(107.3,28,21.6) rot=(0,0,1;0rad)
  Width = 7
FEATURE [Part::Box] Box016  label="Cube012"
  AttacherType = Attacher::AttachEngine3D
  Height = 3
  Length = 7.4
  Placement = pos=(107.3,28,18.6) rot=(0,0,1;0rad)
  Width = 7
FEATURE [Part::Box] Box017  label="Cube013"
  AttacherType = Attacher::AttachEngine3D
  Height = 3
  Length = 7.4
  Placement = pos=(107.3,28,50.4) rot=(0,0,1;0rad)
  Width = 7
FEATURE [Part::Cylinder] Cylinder024
  Angle = 360
  AttacherType = Attacher::AttachEngine3D
  Height = 20
  Placement = pos=(0,0,36.15) rot=(0,0,1;0rad)
  Radius = 14.3
FEATURE [Part::Cylinder] Cylinder025
  Angle = 360
  AttacherType = Attacher::AttachEngine3D
  Height = 10
  Placement = pos=(0,0,36.15) rot=(0,0,1;0rad)
  Radius = 4
FEATURE [Part::MultiFuse] Fusion066  label="removeToCreteHoleForPlugHousing009"
  Placement = pos=(70,19,36) rot=(0,1,0;1.5708rad)
  Shapes = -> [Cylinder024,Cylinder025]
FEATURE [Part::MultiFuse] Fusion065  label="plugHousingBracketHolder002"
  Shapes = -> [Box017,Box015,Box016]
FEATURE [Part::Cut] Cut025  label="plugHousingBracketHolder003"
  Base = -> Fusion065
  Placement = pos=(7,0,0) rot=(0,0,1;0rad)
  Tool = -> Fusion066
FEATURE [Sketcher::SketchObject] Sketch047
  FullyConstrained = false
  Placement = pos=(0,0,0) rot=(1,0,0;1.5708rad)
  sketch-geometry (24):
    g0: ArcOfCircle CenterX=-4 CenterY=-10.5 CenterZ=0 NormalX=0 NormalY=0 NormalZ=1 AngleXU=0 Radius=1.5 StartAngle=6e-16 EndAngle=3.14159
    g1: ArcOfCircle CenterX=-34.2 CenterY=-10.5 CenterZ=0 NormalX=0 NormalY=0 NormalZ=1 AngleXU=0 Radius=1.5 StartAngle=0 EndAngle=3.14159
    g2: ArcOfCircle CenterX=-34.2 CenterY=-27.7 CenterZ=0 NormalX=0 NormalY=0 NormalZ=1 AngleXU=0 Radius=1.5 StartAngle=3.14159 EndAngle=6.28319
    g3: ArcOfCircle CenterX=-4 CenterY=-27.7 CenterZ=0 NormalX=0 NormalY=0 NormalZ=1 AngleXU=0 Radius=1.5 StartAngle=3.1416 EndAngle=6.28319
    g4: ArcOfCircle CenterX=-10 CenterY=-4.3 CenterZ=0 NormalX=0 NormalY=0 NormalZ=1 AngleXU=0 Radius=1.5 StartAngle=2e-16 EndAngle=3.14159
    g5: ArcOfCircle CenterX=-16.1 CenterY=-1.8 CenterZ=0 NormalX=0 NormalY=0 NormalZ=1 AngleXU=0 Radius=1.5 StartAngle=5e-16 EndAngle=3.14159
    g6: ArcOfCircle CenterX=-22.1 CenterY=-1.8 CenterZ=0 NormalX=0 NormalY=0 NormalZ=1 AngleXU=0 Radius=1.5 StartAngle=5e-16 EndAngle=3.14159
    g7: ArcOfCircle CenterX=-28.2 CenterY=-4.3 CenterZ=0 NormalX=0 NormalY=0 NormalZ=1 AngleXU=0 Radius=1.5 StartAngle=2e-16 EndAngle=3.14159
    g8: ArcOfCircle CenterX=-10 CenterY=-33.9 CenterZ=0 NormalX=0 NormalY=0 NormalZ=1 AngleXU=0 Radius=1.5 StartAngle=3.14159 EndAngle=6.28319
    g9: ArcOfCircle CenterX=-16.1 CenterY=-36.4 CenterZ=0 NormalX=0 NormalY=0 NormalZ=1 AngleXU=0 Radius=1.5 StartAngle=3.14159 EndAngle=6.28319
    g10: ArcOfCircle CenterX=-22.1 CenterY=-36.4 CenterZ=0 NormalX=0 NormalY=0 NormalZ=1 AngleXU=0 Radius=1.5 StartAngle=3.14159 EndAngle=6.28319
    g11: ArcOfCircle CenterX=-28.2 CenterY=-33.9 CenterZ=0 NormalX=0 NormalY=0 NormalZ=1 AngleXU=0 Radius=1.5 StartAngle=3.14159 EndAngle=6.28319
    g12: LineSegment StartX=-35.7 StartY=-10.5 StartZ=0 EndX=-35.7 EndY=-27.7 EndZ=0
    g13: LineSegment StartX=-32.7 StartY=-10.5 StartZ=0 EndX=-32.7 EndY=-27.7 EndZ=0
    g14: LineSegment StartX=-29.7 StartY=-33.9 StartZ=0 EndX=-29.7 EndY=-4.3 EndZ=0
    g15: LineSegment StartX=-26.7 StartY=-33.9 StartZ=0 EndX=-26.7 EndY=-4.3 EndZ=0
    g16: LineSegment StartX=-2.5 StartY=-10.5 StartZ=0 EndX=-2.5 EndY=-27.7 EndZ=0
    g17: LineSegment StartX=-8.5 StartY=-4.3 StartZ=0 EndX=-8.5 EndY=-33.9 EndZ=0
    g18: LineSegment StartX=-5.5 StartY=-10.5 StartZ=0 EndX=-5.5 EndY=-27.7 EndZ=0
    g19: LineSegment StartX=-11.5 StartY=-4.3 StartZ=0 EndX=-11.5 EndY=-33.9 EndZ=0
    g20: LineSegment StartX=-14.6 StartY=-1.8 StartZ=0 EndX=-14.6 EndY=-36.4 EndZ=0
    g21: LineSegment StartX=-17.6 StartY=-1.8 StartZ=0 EndX=-17.6 EndY=-36.4 EndZ=0
    g22: LineSegment StartX=-20.6 StartY=-36.4 StartZ=0 EndX=-20.6 EndY=-1.8 EndZ=0
    g23: LineSegment StartX=-23.6 StartY=-1.8 StartZ=0 EndX=-23.6 EndY=-36.4 EndZ=0
  constraints (48):
    c: Block(g0)
    c: Block(g1)
    c: Block(g2)
    c: Block(g3)
    c: Block(g4)
    c: Block(g5)
    c: Block(g6)
    c: Block(g7)
    c: Block(g8)
    c: Block(g9)
    c: Block(g10)
    c: Block(g11)
    c: Coincident(g12,g1)
    c: Coincident(g12,g2)
    c: Vertical(g12)
    c: Coincident(g13,g1)
    c: Coincident(g13,g2)
    c: Vertical(g13)
    c: Coincident(g14,g11)
    c: Coincident(g14,g7)
    c: Vertical(g14)
    c: Coincident(g15,g11)
    c: Coincident(g15,g7)
    c: Vertical(g15)
    c: Coincident(g16,g0)
    c: Coincident(g16,g3)
    c: Vertical(g16)
    c: Coincident(g17,g4)
    c: Coincident(g17,g8)
    c: Vertical(g17)
    c: Coincident(g18,g0)
    c: Coincident(g18,g3)
    c: Vertical(g18)
    c: Coincident(g19,g4)
    c: Coincident(g19,g8)
    c: Vertical(g19)
    c: Coincident(g20,g5)
    c: Coincident(g20,g9)
    c: Vertical(g20)
    c: Coincident(g21,g5)
    c: Coincident(g21,g9)
    c: Vertical(g21)
    c: Coincident(g22,g10)
    c: Coincident(g22,g6)
    c: Vertical(g22)
    c: Coincident(g23,g6)
    c: Coincident(g23,g10)
    c: Vertical(g23)
FEATURE [Part::Extrusion] Extrude038  label="removeToCreateFanGrillHoles001"
  Base = -> Sketch047
  Dir = (0,-1,6e-16)
  DirMode = 2
  FaceMakerClass = Part::FaceMakerBullseye
  LengthFwd = 10
  LengthRev = 0
  Placement = pos=(65.4,44,54.82) rot=(0,0,1;0rad)
  Solid = true
  Symmetric = false
FEATURE [Part::Feature] Wire004
  shape: bbox 11 x 5.2 x 2e-07 mm, 0 faces, 0 solids (baked)
FEATURE [Part::Revolution] Revolve095
  Angle = 360
  Axis = (0,1,0)
  Base = (0,0,0)
  FaceMakerClass = Part::FaceMakerBullseye
  Placement = pos=(30.3,38,19.7) rot=(0,0,1;0rad)
  Solid = true
  Source = -> Wire004
  Symmetric = false
FEATURE [Part::Feature] Wire005
  shape: bbox 11 x 5.2 x 2e-07 mm, 0 faces, 0 solids (baked)
FEATURE [Part::Revolution] Revolve096
  Angle = 360
  Axis = (0,1,0)
  Base = (0,0,0)
  FaceMakerClass = Part::FaceMakerBullseye
  Placement = pos=(30.3,38,51.7) rot=(0,0,1;0rad)
  Solid = true
  Source = -> Wire005
  Symmetric = false
FEATURE [Part::Feature] Wire006
  shape: bbox 11 x 5.2 x 2e-07 mm, 0 faces, 0 solids (baked)
FEATURE [Part::Revolution] Revolve097
  Angle = 360
  Axis = (0,1,0)
  Base = (0,0,0)
  FaceMakerClass = Part::FaceMakerBullseye
  Placement = pos=(62.3,38,51.7) rot=(0,0,1;0rad)
  Solid = true
  Source = -> Wire006
  Symmetric = false
FEATURE [Part::Feature] Wire007
  shape: bbox 11 x 5.2 x 2e-07 mm, 0 faces, 0 solids (baked)
FEATURE [Part::Revolution] Revolve098
  Angle = 360
  Axis = (0,1,0)
  Base = (0,0,0)
  FaceMakerClass = Part::FaceMakerBullseye
  Placement = pos=(62.3,38,19.7) rot=(0,0,1;0rad)
  Solid = true
  Source = -> Wire007
  Symmetric = false
FEATURE [Part::MultiFuse] Fusion067  label="fanScrewHousing002"
  Shapes = -> [Revolve098,Revolve097,Revolve096,Revolve095]
FEATURE [Part::Feature] Face091 .. Face094  x4 (patterned run collapsed; names and placements below)
  shape: bbox 3.5 x 17.8 x 2e-07 mm, 1 faces, 0 solids (baked)
FEATURE [Part::Revolution] Revolve099  label="removeToCreateScrewAndThreadedInsertHole026"
  Angle = 360
  Axis = (0,1,0)
  Base = (0,0,0)
  FaceMakerClass = Part::FaceMakerBullseye
  Placement = pos=(62.3,30.3,19.7) rot=(0,0,1;0rad)
  Solid = false
  Source = -> Face091
  Symmetric = false
FEATURE [Part::Revolution] Revolve100  label="removeToCreateScrewAndThreadedInsertHole027"
  Angle = 360
  Axis = (0,1,0)
  Base = (0,0,0)
  FaceMakerClass = Part::FaceMakerBullseye
  Placement = pos=(62.3,30.3,51.7) rot=(0,0,1;0rad)
  Solid = false
  Source = -> Face092
  Symmetric = false
FEATURE [Part::Revolution] Revolve101  label="removeToCreateScrewAndThreadedInsertHole028"
  Angle = 360
  Axis = (0,1,0)
  Base = (0,0,0)
  FaceMakerClass = Part::FaceMakerBullseye
  Placement = pos=(30.3,30.3,19.7) rot=(0,0,1;0rad)
  Solid = false
  Source = -> Face093
  Symmetric = false
FEATURE [Part::Revolution] Revolve102  label="removeToCreateScrewAndThreadedInsertHole029"
  Angle = 360
  Axis = (0,1,0)
  Base = (0,0,0)
  FaceMakerClass = Part::FaceMakerBullseye
  Placement = pos=(30.3,30.3,51.7) rot=(0,0,1;0rad)
  Solid = false
  Source = -> Face094
  Symmetric = false
FEATURE [Part::MultiFuse] Fusion068  label="createThreadedInsertHolesForFan002"
  Shapes = -> [Revolve099,Revolve100,Revolve101,Revolve102]
FEATURE [Part::Cut] Cut026  label="fanScrewHousing003"
  Base = -> Fusion067
  Tool = -> Fusion068
FEATURE [Sketcher::SketchObject] Sketch048
  FullyConstrained = false
  Placement = pos=(0,0,0) rot=(1,0,0;1.5708rad)
  sketch-geometry (24):
    g0: ArcOfCircle CenterX=-4 CenterY=-10.5 CenterZ=0 NormalX=0 NormalY=0 NormalZ=1 AngleXU=0 Radius=1.5 StartAngle=6e-16 EndAngle=3.14159
    g1: ArcOfCircle CenterX=-34.2 CenterY=-10.5 CenterZ=0 NormalX=0 NormalY=0 NormalZ=1 AngleXU=0 Radius=1.5 StartAngle=0 EndAngle=3.14159
    g2: ArcOfCircle CenterX=-34.2 CenterY=-27.7 CenterZ=0 NormalX=0 NormalY=0 NormalZ=1 AngleXU=0 Radius=1.5 StartAngle=3.14159 EndAngle=6.28319
    g3: ArcOfCircle CenterX=-4 CenterY=-27.7 CenterZ=0 NormalX=0 NormalY=0 NormalZ=1 AngleXU=0 Radius=1.5 StartAngle=3.1416 EndAngle=6.28319
    g4: ArcOfCircle CenterX=-10 CenterY=-4.3 CenterZ=0 NormalX=0 NormalY=0 NormalZ=1 AngleXU=0 Radius=1.5 StartAngle=2e-16 EndAngle=3.14159
    g5: ArcOfCircle CenterX=-16.1 CenterY=-1.8 CenterZ=0 NormalX=0 NormalY=0 NormalZ=1 AngleXU=0 Radius=1.5 StartAngle=5e-16 EndAngle=3.14159
    g6: ArcOfCircle CenterX=-22.1 CenterY=-1.8 CenterZ=0 NormalX=0 NormalY=0 NormalZ=1 AngleXU=0 Radius=1.5 StartAngle=5e-16 EndAngle=3.14159
    g7: ArcOfCircle CenterX=-28.2 CenterY=-4.3 CenterZ=0 NormalX=0 NormalY=0 NormalZ=1 AngleXU=0 Radius=1.5 StartAngle=2e-16 EndAngle=3.14159
    g8: ArcOfCircle CenterX=-10 CenterY=-33.9 CenterZ=0 NormalX=0 NormalY=0 NormalZ=1 AngleXU=0 Radius=1.5 StartAngle=3.14159 EndAngle=6.28319
    g9: ArcOfCircle CenterX=-16.1 CenterY=-36.4 CenterZ=0 NormalX=0 NormalY=0 NormalZ=1 AngleXU=0 Radius=1.5 StartAngle=3.14159 EndAngle=6.28319
    g10: ArcOfCircle CenterX=-22.1 CenterY=-36.4 CenterZ=0 NormalX=0 NormalY=0 NormalZ=1 AngleXU=0 Radius=1.5 StartAngle=3.14159 EndAngle=6.28319
    g11: ArcOfCircle CenterX=-28.2 CenterY=-33.9 CenterZ=0 NormalX=0 NormalY=0 NormalZ=1 AngleXU=0 Radius=1.5 StartAngle=3.14159 EndAngle=6.28319
    g12: LineSegment StartX=-35.7 StartY=-10.5 StartZ=0 EndX=-35.7 EndY=-27.7 EndZ=0
    g13: LineSegment StartX=-32.7 StartY=-10.5 StartZ=0 EndX=-32.7 EndY=-27.7 EndZ=0
    g14: LineSegment StartX=-29.7 StartY=-33.9 StartZ=0 EndX=-29.7 EndY=-4.3 EndZ=0
    g15: LineSegment StartX=-26.7 StartY=-33.9 StartZ=0 EndX=-26.7 EndY=-4.3 EndZ=0
    g16: LineSegment StartX=-2.5 StartY=-10.5 StartZ=0 EndX=-2.5 EndY=-27.7 EndZ=0
    g17: LineSegment StartX=-8.5 StartY=-4.3 StartZ=0 EndX=-8.5 EndY=-33.9 EndZ=0
    g18: LineSegment StartX=-5.5 StartY=-10.5 StartZ=0 EndX=-5.5 EndY=-27.7 EndZ=0
    g19: LineSegment StartX=-11.5 StartY=-4.3 StartZ=0 EndX=-11.5 EndY=-33.9 EndZ=0
    g20: LineSegment StartX=-14.6 StartY=-1.8 StartZ=0 EndX=-14.6 EndY=-36.4 EndZ=0
    g21: LineSegment StartX=-17.6 StartY=-1.8 StartZ=0 EndX=-17.6 EndY=-36.4 EndZ=0
    g22: LineSegment StartX=-20.6 StartY=-36.4 StartZ=0 EndX=-20.6 EndY=-1.8 EndZ=0
    g23: LineSegment StartX=-23.6 StartY=-1.8 StartZ=0 EndX=-23.6 EndY=-36.4 EndZ=0
  constraints (48):
    c: Block(g0)
    c: Block(g1)
    c: Block(g2)
    c: Block(g3)
    c: Block(g4)
    c: Block(g5)
    c: Block(g6)
    c: Block(g7)
    c: Block(g8)
    c: Block(g9)
    c: Block(g10)
    c: Block(g11)
    c: Coincident(g12,g1)
    c: Coincident(g12,g2)
    c: Vertical(g12)
    c: Coincident(g13,g1)
    c: Coincident(g13,g2)
    c: Vertical(g13)
    c: Coincident(g14,g11)
    c: Coincident(g14,g7)
    c: Vertical(g14)
    c: Coincident(g15,g11)
    c: Coincident(g15,g7)
    c: Vertical(g15)
    c: Coincident(g16,g0)
    c: Coincident(g16,g3)
    c: Vertical(g16)
    c: Coincident(g17,g4)
    c: Coincident(g17,g8)
    c: Vertical(g17)
    c: Coincident(g18,g0)
    c: Coincident(g18,g3)
    c: Vertical(g18)
    c: Coincident(g19,g4)
    c: Coincident(g19,g8)
    c: Vertical(g19)
    c: Coincident(g20,g5)
    c: Coincident(g20,g9)
    c: Vertical(g20)
    c: Coincident(g21,g5)
    c: Coincident(g21,g9)
    c: Vertical(g21)
    c: Coincident(g22,g10)
    c: Coincident(g22,g6)
    c: Vertical(g22)
    c: Coincident(g23,g6)
    c: Coincident(g23,g10)
    c: Vertical(g23)
FEATURE [Part::Extrusion] Extrude039  label="removeToCreateFanGrillHoles002"
  Base = -> Sketch048
  Dir = (0,-1,6e-16)
  DirMode = 2
  FaceMakerClass = Part::FaceMakerBullseye
  LengthFwd = 10
  LengthRev = 0
  Placement = pos=(65.4,44,54.82) rot=(0,0,1;0rad)
  Solid = true
  Symmetric = false
FEATURE [Part::Cut] Cut027  label="fanScrewHousing004"
  Base = -> Cut026
  Tool = -> Extrude038
FEATURE [Part::Cut] Cut028  label="top014"
  Base = -> Fillet026
  Tool = -> Extrude039
FEATURE [Part::Feature] Face095 .. Face098  x4 (patterned run collapsed; names and placements below)
  shape: bbox 3.5 x 17.8 x 2e-07 mm, 1 faces, 0 solids (baked)
FEATURE [Part::Revolution] Revolve103  label="removeToCreateScrewAndThreadedInsertHole030"
  Angle = 360
  Axis = (0,1,0)
  Base = (0,0,0)
  FaceMakerClass = Part::FaceMakerBullseye
  Placement = pos=(62.3,30.3,19.7) rot=(0,0,1;0rad)
  Solid = false
  Source = -> Face095
  Symmetric = false
FEATURE [Part::Revolution] Revolve104  label="removeToCreateScrewAndThreadedInsertHole031"
  Angle = 360
  Axis = (0,1,0)
  Base = (0,0,0)
  FaceMakerClass = Part::FaceMakerBullseye
  Placement = pos=(62.3,30.3,51.7) rot=(0,0,1;0rad)
  Solid = false
  Source = -> Face096
  Symmetric = false
FEATURE [Part::Revolution] Revolve105  label="removeToCreateScrewAndThreadedInsertHole032"
  Angle = 360
  Axis = (0,1,0)
  Base = (0,0,0)
  FaceMakerClass = Part::FaceMakerBullseye
  Placement = pos=(30.3,30.3,19.7) rot=(0,0,1;0rad)
  Solid = false
  Source = -> Face097
  Symmetric = false
FEATURE [Part::Revolution] Revolve106  label="removeToCreateScrewAndThreadedInsertHole033"
  Angle = 360
  Axis = (0,1,0)
  Base = (0,0,0)
  FaceMakerClass = Part::FaceMakerBullseye
  Placement = pos=(30.3,30.3,51.7) rot=(0,0,1;0rad)
  Solid = false
  Source = -> Face098
  Symmetric = false
FEATURE [Part::MultiFuse] Fusion069  label="createThreadedInsertHolesForFan003"
  Shapes = -> [Revolve103,Revolve104,Revolve105,Revolve106]
FEATURE [Part::Cut] Cut029  label="top015"
  Base = -> Cut028
  Tool = -> Fusion054
FEATURE [Part::Cut] Cut030  label="fanScrewHousing005"
  Base = -> Cut027
  Tool = -> Fusion069
FEATURE [Part::Cylinder] Cylinder026  label="removeToCreteHoleForPlugHousing010"
  Angle = 360
  AttacherType = Attacher::AttachEngine3D
  Height = 20
  Placement = pos=(-2,19,36) rot=(0,1,0;1.5708rad)
  Radius = 14.3
FEATURE [Part::Box] Box018  label="removeToCreteHoleForPlugHousing011"
  AttacherType = Attacher::AttachEngine3D
  Height = 28.6
  Length = 10
  Placement = pos=(-2,0,21.7) rot=(0,0,1;0rad)
  Width = 19
FEATURE [Part::Box] Box019  label="wireHolderBottomCaseBit"
  AttacherType = Attacher::AttachEngine3D
  Height = 28
  Length = 3
  Placement = pos=(0,0,22) rot=(0,0,1;0rad)
  Width = 21
FEATURE [Part::Cylinder] Cylinder027  label="removeToCreteHoleForPlugHousing012"
  Angle = 360
  AttacherType = Attacher::AttachEngine3D
  Height = 20
  Placement = pos=(-2,19,36) rot=(0,1,0;1.5708rad)
  Radius = 14.3
FEATURE [Part::Cut] Cut031  label="wireHolderBottomCaseBit001"
  Base = -> Box019
  Tool = -> Cylinder027
FEATURE [Part::MultiFuse] Fusion070  label="removeToCreteHoleForPlugHousing013"
  Shapes = -> [Box018,Cylinder026]
FEATURE [Part::Cut] Cut032  label="top016"
  Base = -> Cut029
  Tool = -> Fusion070
FEATURE [Part::Cylinder] Cylinder028
  Angle = 360
  AttacherType = Attacher::AttachEngine3D
  Height = 20
  Placement = pos=(0,0,36.15) rot=(0,0,1;0rad)
  Radius = 14.3
FEATURE [Part::Cylinder] Cylinder029
  Angle = 360
  AttacherType = Attacher::AttachEngine3D
  Height = 10
  Placement = pos=(0,0,36.15) rot=(0,0,1;0rad)
  Radius = 4
FEATURE [Part::MultiFuse] Fusion071  label="removeToCreteHoleForPlugHousing014"
  Placement = pos=(70,19,36) rot=(0,1,0;1.5708rad)
  Shapes = -> [Cylinder028,Cylinder029]
FEATURE [Sketcher::SketchObject] Sketch049  label="topSketch011"
  FullyConstrained = true
  sketch-geometry (4):
    g0: ArcOfCircle CenterX=105 CenterY=19 CenterZ=0 NormalX=0 NormalY=0 NormalZ=1 AngleXU=0 Radius=20.6155 StartAngle=5.54125 EndAngle=6.28319
    g1: ArcOfCircle CenterX=105 CenterY=19 CenterZ=0 NormalX=0 NormalY=0 NormalZ=1 AngleXU=0 Radius=13 StartAngle=5.54125 EndAngle=6.28319
    g2: LineSegment StartX=118 StartY=19 StartZ=0 EndX=125.616 EndY=19 EndZ=0
    g3: LineSegment StartX=114.583 StartY=10.2157 StartZ=0 EndX=120.197 EndY=5.06982 EndZ=0
  constraints (7):
    c: Block(g0)
    c: Block(g1)
    c: Coincident(g2,g1)
    c: Coincident(g2,g0)
    c: Horizontal(g2)
    c: Coincident(g3,g1)
    c: Coincident(g3,g0)
FEATURE [Part::Box] Box020  label="removeToCreteHoleForPlugHousing015"
  AttacherType = Attacher::AttachEngine3D
  Height = 28.6
  Length = 20
  Placement = pos=(106.15,0,21.7) rot=(0,0,1;0rad)
  Width = 19
FEATURE [Part::MultiFuse] Fusion072  label="removeToCreteHoleForPlugHousing016"
  Shapes = -> [Box020,Fusion071]
FEATURE [Part::Cut] Cut033  label="removeToCreteHoleForPlugHousing017"
  Base = -> Cut032
  Tool = -> Fusion072
FEATURE [Part::Cylinder] Cylinder030
  Angle = 360
  AttacherType = Attacher::AttachEngine3D
  Height = 20
  Placement = pos=(0,0,36.15) rot=(0,0,1;0rad)
  Radius = 14.3
FEATURE [Part::Cylinder] Cylinder031
  Angle = 360
  AttacherType = Attacher::AttachEngine3D
  Height = 10
  Placement = pos=(0,0,36.15) rot=(0,0,1;0rad)
  Radius = 4
FEATURE [Part::Box] Box021  label="removeToCreteHoleForPlugHousing019"
  AttacherType = Attacher::AttachEngine3D
  Height = 28.6
  Length = 20
  Placement = pos=(106.15,0,21.7) rot=(0,0,1;0rad)
  Width = 19
FEATURE [Part::MultiFuse] Fusion074  label="removeToCreteHoleForPlugHousing020"
  Placement = pos=(70,19,36) rot=(0,1,0;1.5708rad)
  Shapes = -> [Cylinder030,Cylinder031]
FEATURE [Part::MultiFuse] Fusion073  label="removeToCreteHoleForPlugHousing018"
  Placement = pos=(0,0,28.3) rot=(0,0,1;0rad)
  Shapes = -> [Box021,Fusion074]
FEATURE [Part::Cylinder] Cylinder032
  Angle = 360
  AttacherType = Attacher::AttachEngine3D
  Height = 20
  Placement = pos=(0,0,36.15) rot=(0,0,1;0rad)
  Radius = 14.3
FEATURE [Part::Cylinder] Cylinder033
  Angle = 360
  AttacherType = Attacher::AttachEngine3D
  Height = 10
  Placement = pos=(0,0,36.15) rot=(0,0,1;0rad)
  Radius = 4
FEATURE [Part::Box] Box022  label="removeToCreteHoleForPlugHousing021"
  AttacherType = Attacher::AttachEngine3D
  Height = 28.6
  Length = 20
  Placement = pos=(106.15,0,21.7) rot=(0,0,1;0rad)
  Width = 19
FEATURE [Part::MultiFuse] Fusion076  label="removeToCreteHoleForPlugHousing023"
  Placement = pos=(70,19,36) rot=(0,1,0;1.5708rad)
  Shapes = -> [Cylinder032,Cylinder033]
FEATURE [Part::MultiFuse] Fusion075  label="removeToCreteHoleForPlugHousing022"
  Placement = pos=(0,0,-28.3) rot=(0,0,1;0rad)
  Shapes = -> [Box022,Fusion076]
FEATURE [Part::MultiFuse] Fusion077  label="removeToCreatePlugHousingBottomBit"
  Shapes = -> [Fusion075,Fusion073]
FEATURE [Part::Cylinder] Cylinder034
  Angle = 360
  AttacherType = Attacher::AttachEngine3D
  Height = 20
  Placement = pos=(0,0,36.15) rot=(0,0,1;0rad)
  Radius = 14
FEATURE [Part::Cylinder] Cylinder035
  Angle = 360
  AttacherType = Attacher::AttachEngine3D
  Height = 10
  Placement = pos=(0,0,36.15) rot=(0,0,1;0rad)
  Radius = 4
FEATURE [Part::MultiFuse] Fusion078  label="removeToCreteHoleForPlugHousing024"
  Placement = pos=(70,19,36) rot=(0,1,0;1.5708rad)
  Shapes = -> [Cylinder034,Cylinder035]
FEATURE [Part::MultiFuse] Fusion079  label="removeToCreatePlugHousingBottomBit001"
  Shapes = -> [Fusion078,Fusion077]
FEATURE [Part::Extrusion] Extrude040  label="bottomPlugHousingBit"
  Base = -> Sketch049
  Dir = (0,0,1)
  DirMode = 2
  FaceMakerClass = Part::FaceMakerBullseye
  LengthFwd = 72
  LengthRev = 0
  Solid = true
  Symmetric = false
FEATURE [Part::Cut] Cut034  label="bottomPlugHousingBit001"
  Base = -> Extrude040
  Placement = pos=(-0.09,0,0) rot=(0,0,1;0rad)
  Tool = -> Fusion079
FEATURE [Part::Box] Box023  label="Cube014"
  AttacherType = Attacher::AttachEngine3D
  Height = 16
  Length = 8
  Placement = pos=(12.7,31.52,28) rot=(0,0,1;0rad)
  Width = 4
FEATURE [Part::Cylinder] Cylinder036
  Angle = 360
  AttacherType = Attacher::AttachEngine3D
  Height = 10
  Placement = pos=(0,0,36.15) rot=(0,0,1;0rad)
  Radius = 4
FEATURE [Part::Cylinder] Cylinder037
  Angle = 360
  AttacherType = Attacher::AttachEngine3D
  Height = 20
  Placement = pos=(0,0,36.15) rot=(0,0,1;0rad)
  Radius = 8.2
FEATURE [Part::MultiFuse] Fusion080  label="removeToCreteHoleForPlugHousing025"
  Placement = pos=(-42,19,36) rot=(0,1,0;1.5708rad)
  Shapes = -> [Cylinder037,Cylinder036]
FEATURE [Sketcher::SketchObject] Sketch050  label="topSketch012"
  FullyConstrained = true
  sketch-geometry (4):
    g0: LineSegment StartX=16.8446 StartY=31.512 StartZ=0 EndX=16.3251 EndY=34.4666 EndZ=0
    g1: ArcOfCircle CenterX=19 CenterY=19.2524 CenterZ=0 NormalX=0 NormalY=0 NormalZ=1 AngleXU=0 Radius=15.4476 StartAngle=1.74483 EndAngle=2.72717
    g2: ArcOfCircle CenterX=19 CenterY=19.2524 CenterZ=0 NormalX=0 NormalY=0 NormalZ=1 AngleXU=0 Radius=12.4476 StartAngle=1.74483 EndAngle=2.73189
    g3: LineSegment StartX=4.86004 StartY=25.4725 StartZ=0 EndX=7.58253 EndY=24.2107 EndZ=0
  constraints (7):
    c: Block(g0)
    c: Coincident(g1,g0)
    c: Coincident(g2,g0)
    c: Coincident(g3,g1)
    c: Coincident(g3,g2)
    c: Block(g1)
    c: Block(g2)
FEATURE [Part::Extrusion] Extrude041
  Base = -> Sketch050
  Dir = (0,0,1)
  DirMode = 2
  FaceMakerClass = Part::FaceMakerBullseye
  LengthFwd = 10.6
  LengthRev = 0
  Placement = pos=(0,0,31) rot=(0,0,1;0rad)
  Solid = true
  Symmetric = false
FEATURE [Part::Cut] Cut035
  Base = -> Extrude041
  Placement = pos=(0,0,-0.3) rot=(0,0,1;0rad)
  Tool = -> Fusion080
FEATURE [Part::Cut] Cut036
  Base = -> Box023
  Tool = -> Cut035
FEATURE [Part::Fillet] Fillet027
  Base = -> Cut036
  Edges = 1 edges r=0.7: [Edge13]
FEATURE [Part::Fillet] Fillet028
  Base = -> Fillet027
  Edges = 1 edges r=0.7: [Edge13]
FEATURE [Part::Fillet] Fillet029
  Base = -> Fillet028
  Edges = 1 edges r=0.7: [Edge16]
FEATURE [Part::Fillet] Fillet030
  Base = -> Fillet029
  Edges = 1 edges r=0.7: [Edge11]
FEATURE [Part::Fillet] Fillet031
  Base = -> Fillet030
  Edges = 1 edges r=0.7: [Edge10]
FEATURE [Part::Fillet] Fillet032
  Base = -> Fillet031
  Edges = 1 edges r=1.2: [Edge5]
FEATURE [Part::Fillet] Fillet033
  Base = -> Fillet032
  Edges = 1 edges r=1.2: [Edge12]
FEATURE [Part::Fillet] Fillet034  label="wireHousingRetainer"
  Base = -> Fillet033
  Edges = 1 edges r=2: [Edge1]
  Placement = pos=(0.3,0,0) rot=(0,0,1;0rad)
FEATURE [Part::Feature] Face099
  shape: bbox 3.5 x 17.8 x 2e-07 mm, 1 faces, 0 solids (baked)
FEATURE [Part::Revolution] Revolve107  label="removeToCreateScrewAndThreadedInsertHole034"
  Angle = 360
  Axis = (0,1,0)
  Base = (0,0,0)
  FaceMakerClass = Part::FaceMakerBullseye
  Placement = pos=(12.5,0,10) rot=(0,0,1;0rad)
  Solid = false
  Source = -> Face099
  Symmetric = false
FEATURE [Part::Feature] Face100
  shape: bbox 3.5 x 17.8 x 2e-07 mm, 1 faces, 0 solids (baked)
FEATURE [Part::Revolution] Revolve108  label="removeToCreateScrewAndThreadedInsertHole035"
  Angle = 360
  Axis = (0,1,0)
  Base = (0,0,0)
  FaceMakerClass = Part::FaceMakerBullseye
  Placement = pos=(12.5,0,62) rot=(0,0,1;0rad)
  Solid = false
  Source = -> Face100
  Symmetric = false
FEATURE [Part::Feature] Face101
  shape: bbox 3.5 x 17.8 x 2e-07 mm, 1 faces, 0 solids (baked)
FEATURE [Part::Revolution] Revolve109  label="removeToCreateScrewAndThreadedInsertHole036"
  Angle = 360
  Axis = (0,1,0)
  Base = (0,0,0)
  FaceMakerClass = Part::FaceMakerBullseye
  Placement = pos=(89.5,0,68.5) rot=(0,0,1;0rad)
  Solid = false
  Source = -> Face101
  Symmetric = false
FEATURE [Part::Feature] Face102
  shape: bbox 3.5 x 17.8 x 2e-07 mm, 1 faces, 0 solids (baked)
FEATURE [Part::Revolution] Revolve110  label="removeToCreateScrewAndThreadedInsertHole037"
  Angle = 360
  Axis = (0,1,0)
  Base = (0,0,0)
  FaceMakerClass = Part::FaceMakerBullseye
  Placement = pos=(89.5,0,3.5) rot=(0,0,1;0rad)
  Solid = false
  Source = -> Face102
  Symmetric = false
FEATURE [Part::Feature] Face103
  shape: bbox 3.5 x 17.8 x 2e-07 mm, 1 faces, 0 solids (baked)
FEATURE [Part::Revolution] Revolve111  label="removeToCreateScrewAndThreadedInsertHole038"
  Angle = 360
  Axis = (0,1,0)
  Base = (0,0,0)
  FaceMakerClass = Part::FaceMakerBullseye
  Placement = pos=(109.5,4.7,3.5) rot=(0,0,1;0rad)
  Solid = false
  Source = -> Face103
  Symmetric = false
FEATURE [Part::Feature] Face104
  shape: bbox 3.5 x 17.8 x 2e-07 mm, 1 faces, 0 solids (baked)
FEATURE [Part::Revolution] Revolve112  label="removeToCreateScrewAndThreadedInsertHole039"
  Angle = 360
  Axis = (0,1,0)
  Base = (0,0,0)
  FaceMakerClass = Part::FaceMakerBullseye
  Placement = pos=(109.5,4.7,68.5) rot=(0,0,1;0rad)
  Solid = false
  Source = -> Face104
  Symmetric = false
FEATURE [Part::MultiFuse] Fusion081  label="removeToCreateScrewAndThreadedInsertHole040"
  Shapes = -> [Revolve107,Revolve108,Revolve109,Revolve110,Revolve111,Revolve112]
FEATURE [Part::MultiFuse] Fusion082  label="casePillars002"
  Shapes = -> [Revolve094,Revolve092,Revolve090,Revolve089,Revolve091,Revolve093]
FEATURE [Part::Cut] Cut037  label="casePillars003"
  Base = -> Fusion082
  Tool = -> Fusion081
FEATURE [Sketcher::SketchObject] Sketch051
  FullyConstrained = true
  Placement = pos=(117,19,0) rot=(0.57735,0.57735,0.57735;2.0944rad)
  sketch-geometry (48):
    g0: LineSegment StartX=-49.19 StartY=69.25 StartZ=0 EndX=-49.19 EndY=66.25 EndZ=0
    g1: LineSegment StartX=-49.19 StartY=63.5 StartZ=0 EndX=-49.19 EndY=60.5 EndZ=0
    g2: LineSegment StartX=-49.19 StartY=57.75 StartZ=0 EndX=-49.19 EndY=54.75 EndZ=0
    g3: LineSegment StartX=-49.19 StartY=52 StartZ=0 EndX=-49.19 EndY=49 EndZ=0
    g4: LineSegment StartX=-49.19 StartY=46.25 StartZ=0 EndX=-49.19 EndY=43.25 EndZ=0
    g5: LineSegment StartX=-49.19 StartY=40.5 StartZ=0 EndX=-49.19 EndY=37.5 EndZ=0
    g6: LineSegment StartX=-49.19 StartY=34.5 StartZ=0 EndX=-49.19 EndY=31.5 EndZ=0
    g7: LineSegment StartX=-49.19 StartY=28.75 StartZ=0 EndX=-49.19 EndY=25.75 EndZ=0
    g8: LineSegment StartX=-49.19 StartY=23 StartZ=0 EndX=-49.19 EndY=20 EndZ=0
    g9: LineSegment StartX=-49.19 StartY=17.25 StartZ=0 EndX=-49.19 EndY=14.25 EndZ=0
    g10: LineSegment StartX=-49.19 StartY=11.5 StartZ=0 EndX=-49.19 EndY=8.5 EndZ=0
    g11: LineSegment StartX=-49.19 StartY=5.75 StartZ=0 EndX=-49.19 EndY=2.75 EndZ=0
    g12: ArcOfCircle CenterX=-1.5 CenterY=67.75 CenterZ=0 NormalX=0 NormalY=0 NormalZ=1 AngleXU=0 Radius=1.5 StartAngle=4.71239 EndAngle=7.85398
    g13: ArcOfCircle CenterX=-1.5 CenterY=62 CenterZ=0 NormalX=0 NormalY=0 NormalZ=1 AngleXU=0 Radius=1.5 StartAngle=4.71239 EndAngle=7.85398
    g14: ArcOfCircle CenterX=-1.5 CenterY=56.25 CenterZ=0 NormalX=0 NormalY=0 NormalZ=1 AngleXU=0 Radius=1.5 StartAngle=4.71239 EndAngle=7.85398
    g15: ArcOfCircle CenterX=-11.49 CenterY=50.5 CenterZ=0 NormalX=0 NormalY=0 NormalZ=1 AngleXU=0 Radius=1.5 StartAngle=4.71239 EndAngle=7.85398
    g16: ArcOfCircle CenterX=-16.28 CenterY=44.75 CenterZ=0 NormalX=0 NormalY=0 NormalZ=1 AngleXU=0 Radius=1.5 StartAngle=4.71239 EndAngle=7.85398
    g17: ArcOfCircle CenterX=-18.2337 CenterY=39 CenterZ=0 NormalX=0 NormalY=0 NormalZ=1 AngleXU=0 Radius=1.5 StartAngle=4.71485 EndAngle=7.85398
    g18: ArcOfCircle CenterX=-16.2837 CenterY=27.25 CenterZ=0 NormalX=0 NormalY=0 NormalZ=1 AngleXU=0 Radius=1.5 StartAngle=4.71485 EndAngle=7.85398
    g19: ArcOfCircle CenterX=-18.2337 CenterY=33 CenterZ=0 NormalX=0 NormalY=0 NormalZ=1 AngleXU=0 Radius=1.5 StartAngle=4.71485 EndAngle=7.85398
    g20: ArcOfCircle CenterX=-11.49 CenterY=21.5 CenterZ=0 NormalX=0 NormalY=0 NormalZ=1 AngleXU=0 Radius=1.5 StartAngle=4.71239 EndAngle=7.85398
    g21: ArcOfCircle CenterX=-1.5 CenterY=4.25 CenterZ=0 NormalX=0 NormalY=0 NormalZ=1 AngleXU=0 Radius=1.5 StartAngle=4.71239 EndAngle=7.85398
    g22: ArcOfCircle CenterX=-1.5 CenterY=10 CenterZ=0 NormalX=0 NormalY=0 NormalZ=1 AngleXU=0 Radius=1.5 StartAngle=4.71239 EndAngle=7.85398
    g23: ArcOfCircle CenterX=-1.5 CenterY=15.75 CenterZ=0 NormalX=0 NormalY=0 NormalZ=1 AngleXU=0 Radius=1.5 StartAngle=4.71239 EndAngle=7.85398
    g24: LineSegment StartX=-49.19 StartY=69.25 StartZ=0 EndX=-1.5 EndY=69.25 EndZ=0
    g25: LineSegment StartX=-49.19 StartY=66.25 StartZ=0 EndX=-1.5 EndY=66.25 EndZ=0
    g26: LineSegment StartX=-49.19 StartY=63.5 StartZ=0 EndX=-1.5 EndY=63.5 EndZ=0
    g27: LineSegment StartX=-49.19 StartY=60.5 StartZ=0 EndX=-1.5 EndY=60.5 EndZ=0
    g28: LineSegment StartX=-49.19 StartY=57.75 StartZ=0 EndX=-1.5 EndY=57.75 EndZ=0
    g29: LineSegment StartX=-49.19 StartY=54.75 StartZ=0 EndX=-1.5 EndY=54.75 EndZ=0
    g30: LineSegment StartX=-49.19 StartY=52 StartZ=0 EndX=-11.49 EndY=52 EndZ=0
    g31: LineSegment StartX=-49.19 StartY=49 StartZ=0 EndX=-11.49 EndY=49 EndZ=0
    g32: LineSegment StartX=-49.19 StartY=46.25 StartZ=0 EndX=-16.28 EndY=46.25 EndZ=0
    g33: LineSegment StartX=-49.19 StartY=43.25 StartZ=0 EndX=-16.28 EndY=43.25 EndZ=0
    g34: LineSegment StartX=-49.19 StartY=40.5 StartZ=0 EndX=-18.2337 EndY=40.5 EndZ=0
    g35: LineSegment StartX=-49.19 StartY=37.5 StartZ=0 EndX=-18.23 EndY=37.5 EndZ=0
    g36: LineSegment StartX=-49.19 StartY=34.5 StartZ=0 EndX=-18.2337 EndY=34.5 EndZ=0
    g37: LineSegment StartX=-49.19 StartY=31.5 StartZ=0 EndX=-18.23 EndY=31.5 EndZ=0
    g38: LineSegment StartX=-49.19 StartY=28.75 StartZ=0 EndX=-16.2837 EndY=28.75 EndZ=0
    g39: LineSegment StartX=-49.19 StartY=25.75 StartZ=0 EndX=-16.28 EndY=25.75 EndZ=0
    g40: LineSegment StartX=-49.19 StartY=23 StartZ=0 EndX=-11.49 EndY=23 EndZ=0
    g41: LineSegment StartX=-49.19 StartY=20 StartZ=0 EndX=-11.49 EndY=20 EndZ=0
    g42: LineSegment StartX=-49.19 StartY=17.25 StartZ=0 EndX=-1.5 EndY=17.25 EndZ=0
    g43: LineSegment StartX=-49.19 StartY=14.25 StartZ=0 EndX=-1.5 EndY=14.25 EndZ=0
    g44: LineSegment StartX=-49.19 StartY=11.5 StartZ=0 EndX=-1.5 EndY=11.5 EndZ=0
    g45: LineSegment StartX=-49.19 StartY=8.5 StartZ=0 EndX=-1.5 EndY=8.5 EndZ=0
    g46: LineSegment StartX=-49.19 StartY=5.75 StartZ=0 EndX=-1.5 EndY=5.75 EndZ=0
    g47: LineSegment StartX=-49.19 StartY=2.75 StartZ=0 EndX=-1.5 EndY=2.75 EndZ=0
  constraints (120):
    c: Vertical(g0)
    c: Distance(g0) = 3
    c: Block(g0)
    c: Vertical(g1)
    c: Distance(g1) = 3
    c: Vertical(g2)
    c: Equal(g0,g2) = 3
    c: Block(g2)
    c: Vertical(g3)
    c: Equal(g1,g3) = 3
    c: Vertical(g4)
    c: Equal(g0,g4) = 3
    c: Block(g4)
    c: Vertical(g5)
    c: Equal(g1,g5) = 3
    c: Vertical(g6)
    c: Equal(g0,g6) = 3
    c: Block(g6)
    c: Vertical(g7)
    c: Equal(g1,g7) = 3
    c: Vertical(g8)
    c: Equal(g0,g8) = 3
    c: Block(g8)
    c: Vertical(g9)
    c: Equal(g1,g9) = 3
    c: Vertical(g10)
    c: Equal(g0,g10) = 3
    c: Block(g10)
    c: Vertical(g11)
    c: Equal(g1,g11) = 3
    c: Block(g12)
    c: Block(g13)
    c: Block(g14)
    c: Block(g15)
    c: Block(g16)
    c: Block(g17)
    c: Block(g18)
    c: Block(g19)
    c: Block(g20)
    c: Block(g21)
    c: Block(g22)
    c: Block(g23)
    c: Block(g11)
    c: Block(g9)
    c: Block(g7)
    c: Block(g5)
    c: Block(g3)
    c: Block(g1)
    c: Coincident(g24,g0)
    c: Coincident(g24,g12)
    c: Horizontal(g24)
    c: Coincident(g25,g0)
    c: Coincident(g25,g12)
    c: Horizontal(g25)
    c: Coincident(g26,g1)
    c: Coincident(g26,g13)
    c: Horizontal(g26)
    c: Coincident(g27,g1)
    c: Coincident(g27,g13)
    c: Horizontal(g27)
    c: Coincident(g28,g2)
    c: Coincident(g28,g14)
    c: Horizontal(g28)
    c: Coincident(g29,g2)
    c: Coincident(g29,g14)
    c: Horizontal(g29)
    c: Coincident(g30,g3)
    c: Coincident(g30,g15)
    c: Horizontal(g30)
    c: Coincident(g31,g3)
    c: Coincident(g31,g15)
    c: Horizontal(g31)
    c: Coincident(g32,g4)
    c: Coincident(g32,g16)
    c: Horizontal(g32)
    c: Coincident(g33,g4)
    c: Coincident(g33,g16)
    c: Horizontal(g33)
    c: Coincident(g34,g5)
    c: Coincident(g34,g17)
    c: Horizontal(g34)
    c: Coincident(g35,g5)
    c: Coincident(g35,g17)
    c: Horizontal(g35)
    c: Coincident(g36,g6)
    c: Coincident(g36,g19)
    c: Horizontal(g36)
    c: Coincident(g37,g6)
    c: Coincident(g37,g19)
    c: Horizontal(g37)
    c: Coincident(g38,g7)
    c: Coincident(g38,g18)
    c: Horizontal(g38)
    c: Coincident(g39,g7)
    c: Coincident(g39,g18)
    c: Horizontal(g39)
    c: Coincident(g40,g8)
    c: Coincident(g40,g20)
    c: Horizontal(g40)
    c: Coincident(g41,g8)
    c: Coincident(g41,g20)
    c: Horizontal(g41)
    c: Coincident(g42,g9)
    c: Coincident(g42,g23)
    c: Horizontal(g42)
    c: Coincident(g43,g9)
    c: Coincident(g43,g23)
    c: Horizontal(g43)
    c: Coincident(g44,g10)
    c: Coincident(g44,g22)
    c: Horizontal(g44)
    c: Coincident(g45,g10)
    c: Coincident(g45,g22)
    c: Horizontal(g45)
    c: Coincident(g46,g11)
    c: Coincident(g46,g21)
    c: Horizontal(g46)
    c: Coincident(g47,g11)
    c: Coincident(g47,g21)
    c: Horizontal(g47)
FEATURE [Part::Extrusion] Extrude042
  Base = -> Sketch051
  Dir = (1,-2e-16,2e-16)
  DirMode = 2
  FaceMakerClass = Part::FaceMakerBullseye
  LengthFwd = 19
  LengthRev = 0
  Placement = pos=(-19,0,0) rot=(0,0,1;0rad)
  Solid = true
  Symmetric = false
FEATURE [Part::Fillet] Fillet035  label="removeToCreateVentalationHoles"
  Base = -> Extrude042
  Edges = <same value as first occurrence — deduplicated (x6 in doc)>
  Placement = pos=(7,0,0) rot=(0,0,1;0rad)
FEATURE [Part::Cut] Cut038  label="top017"
  Base = -> Cut033
  Tool = -> Fillet035
FEATURE [Sketcher::SketchObject] Sketch052  label="bottomSketch001"
  FullyConstrained = true
  sketch-geometry (45):
    g0: LineSegment StartX=6.29999 StartY=8 StartZ=0 EndX=3.29999 EndY=8 EndZ=0
    g1: LineSegment StartX=3.29999 StartY=8 StartZ=0 EndX=3.29999 EndY=-6.03275e-07 EndZ=0
    g2: ArcOfCircle CenterX=8.29999 CenterY=5 CenterZ=0 NormalX=0 NormalY=0 NormalZ=1 AngleXU=0 Radius=2 StartAngle=3.14159 EndAngle=4.71239
    g3: LineSegment StartX=6.29999 StartY=8 StartZ=0 EndX=6.29999 EndY=5 EndZ=0
    g4: ArcOfCircle CenterX=105 CenterY=19 CenterZ=0 NormalX=0 NormalY=0 NormalZ=1 AngleXU=0 Radius=12.7 StartAngle=4.71239 EndAngle=5.94289
    g5-g11: Circle x7 (B-spline internal-alignment scaffolding for g12; pole/knot coordinates omitted)
    g12: BSplineCurve PolesCount=7 KnotsCount=5 Degree=3 IsPeriodic=0
    g13-g17: GeomPoint x5 (B-spline internal-alignment scaffolding for g12; pole/knot coordinates omitted)
    g18: ArcOfCircle CenterX=105 CenterY=19 CenterZ=0 NormalX=0 NormalY=0 NormalZ=1 AngleXU=0 Radius=15.7 StartAngle=5.81226 EndAngle=6.28319
    g19: BSplineCurve PolesCount=5 KnotsCount=3 Degree=3 IsPeriodic=0
    g20: LineSegment StartX=8.29999 StartY=3 StartZ=0 EndX=101.7 EndY=3 EndZ=0
    g21: LineSegment StartX=3.29999 StartY=-6.03275e-07 StartZ=0 EndX=105 EndY=-6.03275e-07 EndZ=0
    g22: LineSegment StartX=120.974 StartY=8.71251 StartZ=0 EndX=122.332 EndY=7.83778 EndZ=0
    g23: LineSegment StartX=105 StartY=-6.03274e-07 StartZ=0 EndX=113 EndY=-6.03274e-07 EndZ=0
    g24: ArcOfCircle CenterX=105 CenterY=19 CenterZ=0 NormalX=0 NormalY=0 NormalZ=1 AngleXU=0 Radius=20.6155 StartAngle=5.11091 EndAngle=5.71103
    g25: ArcOfCircle CenterX=117.7 CenterY=19 CenterZ=0 NormalX=0 NormalY=0 NormalZ=1 AngleXU=0 Radius=3 StartAngle=1.2e-15 EndAngle=2.10468
    g26: Circle CenterX=116.345 CenterY=16.3232 CenterZ=0 NormalX=0 NormalY=0 NormalZ=1 AngleXU=0 Radius=1
    g27: Circle CenterX=117.24 CenterY=15.7584 CenterZ=0 NormalX=0 NormalY=0 NormalZ=1 AngleXU=0 Radius=1
    g28: Circle CenterX=116.972 CenterY=14.7612 CenterZ=0 NormalX=0 NormalY=0 NormalZ=1 AngleXU=0 Radius=1
    g29: BSplineCurve PolesCount=3 KnotsCount=2 Degree=2 IsPeriodic=0
    g30: GeomPoint X=116.345 Y=16.3232 Z=0
    g31: GeomPoint X=116.972 Y=14.7612 Z=0
    g32: Circle CenterX=115.828 CenterY=17.157 CenterZ=0 NormalX=0 NormalY=0 NormalZ=1 AngleXU=0 Radius=1
    g33: Circle CenterX=115.841 CenterY=16.639 CenterZ=0 NormalX=0 NormalY=0 NormalZ=1 AngleXU=0 Radius=1
    g34: Circle CenterX=116.345 CenterY=16.3232 CenterZ=0 NormalX=0 NormalY=0 NormalZ=1 AngleXU=0 Radius=1
    g35: BSplineCurve PolesCount=3 KnotsCount=2 Degree=2 IsPeriodic=0
    g36: GeomPoint X=115.828 Y=17.157 Z=0
    g37: GeomPoint X=116.345 Y=16.3232 Z=0
    g38: LineSegment StartX=115.828 StartY=17.157 StartZ=0 EndX=115.828 EndY=20.8307 EndZ=0
    g39: Circle CenterX=115.828 CenterY=20.8307 CenterZ=0 NormalX=0 NormalY=0 NormalZ=1 AngleXU=0 Radius=1
    g40: Circle CenterX=115.831 CenterY=21.3396 CenterZ=0 NormalX=0 NormalY=0 NormalZ=1 AngleXU=0 Radius=1
    g41: Circle CenterX=116.173 CenterY=21.5825 CenterZ=0 NormalX=0 NormalY=0 NormalZ=1 AngleXU=0 Radius=1
    g42: BSplineCurve PolesCount=3 KnotsCount=2 Degree=2 IsPeriodic=0
    g43: GeomPoint X=115.828 Y=20.8307 Z=0
    g44: GeomPoint X=116.173 Y=21.5825 Z=0
  constraints (70):
    c: Horizontal(g0)
    c: Distance(g0) = 3
    c: Coincident(g1,g0)
    c: Vertical(g1)
    c: Block(g2)
    c: Block(g0)
    c: Coincident(g3,g0)
    c: Coincident(g3,g2)
    c: Vertical(g3)
    c: Block(g1)
    c: Block(g4)
    c: Coincident(g19,g4)
    c: Block(g19)
    c: Equal(g5, g6-g11) x6
    c: InternalAlignment(g5-g11 -> g12) x7
    c: InternalAlignment(g13-g17 -> g12) x5
    c: Block(g12)
    c: Coincident(g18,g12)
    c: Block(g18)
    c: Coincident(g20,g2)
    c: Coincident(g20,g19)
    c: Horizontal(g20)
    c: Distance(g20) = 93.4
    c: Coincident(g21,g1)
    c: Horizontal(g21)
    c: Distance(g21) = 101.7
    c: Horizontal(g23)
    c: Distance(g23) = 8
    c: Coincident(g24,g23)
    c: Block(g23)
    c: Coincident(g22,g24)
    c: Block(g24)
    c: Block(g22)
    c: Distance(g22) = 1.61553
    c: Coincident(g25,g18)
    c: Block(g25)
    c: Weight(g26) = 1
    c: Equal(g26,g27)
    c: Equal(g26,g28)
    c: Coincident(g29,g4)
    c: InternalAlignment(g26,g29)
    c: InternalAlignment(g27,g29)
    c: InternalAlignment(g28,g29)
    c: InternalAlignment(g30,g29)
    c: InternalAlignment(g31,g29)
    c: Block(g29)
    c: Weight(g32) = 1
    c: Equal(g32,g33)
    c: Equal(g32,g34)
    c: Coincident(g35,g29)
    c: InternalAlignment(g32,g35)
    c: InternalAlignment(g33,g35)
    c: InternalAlignment(g34,g35)
    c: InternalAlignment(g36,g35)
    c: InternalAlignment(g37,g35)
    c: Block(g35)
    c: Coincident(g38,g35)
    c: Vertical(g38)
    c: Block(g38)
    c: Coincident(g42,g38)
    c: Weight(g39) = 1
    c: Equal(g39,g40)
    c: Equal(g39,g41)
    c: Coincident(g42,g25)
    c: InternalAlignment(g39,g42)
    c: InternalAlignment(g40,g42)
    c: InternalAlignment(g41,g42)
    c: InternalAlignment(g43,g42)
    c: InternalAlignment(g44,g42)
    c: Block(g42)
FEATURE [Part::Extrusion] Extrude043  label="bottom010"
  Base = -> Sketch052
  Dir = (0,0,1)
  DirMode = 2
  FaceMakerClass = Part::FaceMakerBullseye
  LengthFwd = 71.4
  LengthRev = 0
  Placement = pos=(0,0,0.3) rot=(0,0,1;0rad)
  Solid = true
  Symmetric = false
FEATURE [Sketcher::SketchObject] Sketch053  label="topSketch013"
  FullyConstrained = true
  sketch-geometry (22):
    g0: LineSegment StartX=5.21097e-06 StartY=3 StartZ=0 EndX=5.21097e-06 EndY=19 EndZ=0
    g1: ArcOfCircle CenterX=19 CenterY=19 CenterZ=0 NormalX=0 NormalY=0 NormalZ=1 AngleXU=0 Radius=19 StartAngle=1.5708 EndAngle=3.14159
    g2: ArcOfCircle CenterX=19 CenterY=19 CenterZ=0 NormalX=0 NormalY=0 NormalZ=1 AngleXU=0 Radius=16 StartAngle=1.5708 EndAngle=3.14159
    g3: LineSegment StartX=114 StartY=35 StartZ=0 EndX=19 EndY=35 EndZ=0
    g4: LineSegment StartX=5.21097e-06 StartY=3 StartZ=0 EndX=5.21097e-06 EndY=0 EndZ=0
    g5: LineSegment StartX=3 StartY=0 StartZ=0 EndX=5.21097e-06 EndY=0 EndZ=0
    g6: LineSegment StartX=3 StartY=19 StartZ=0 EndX=3 EndY=0 EndZ=0
    g7: LineSegment StartX=19 StartY=38 StartZ=0 EndX=124 EndY=38 EndZ=0
    g8: Circle CenterX=119 CenterY=35 CenterZ=0 NormalX=0 NormalY=0 NormalZ=1 AngleXU=0 Radius=1
    g9: Circle CenterX=121 CenterY=35 CenterZ=0 NormalX=0 NormalY=0 NormalZ=1 AngleXU=0 Radius=1
    g10: Circle CenterX=121 CenterY=33 CenterZ=0 NormalX=0 NormalY=0 NormalZ=1 AngleXU=0 Radius=1
    g11: BSplineCurve PolesCount=3 KnotsCount=2 Degree=2 IsPeriodic=0
    g12: GeomPoint X=119 Y=35 Z=0
    g13: GeomPoint X=121 Y=33 Z=0
    g14: LineSegment StartX=119 StartY=35 StartZ=0 EndX=114 EndY=35 EndZ=0
    g15: ArcOfCircle CenterX=105 CenterY=19 CenterZ=0 NormalX=0 NormalY=0 NormalZ=1 AngleXU=0 Radius=16 StartAngle=5.60905 EndAngle=6.28319
    g16: LineSegment StartX=121 StartY=33 StartZ=0 EndX=121 EndY=19 EndZ=0
    g17: LineSegment StartX=117.5 StartY=9.01251 StartZ=0 EndX=121.163 EndY=9.0125 EndZ=0
    g18: ArcOfCircle CenterX=105 CenterY=19 CenterZ=0 NormalX=0 NormalY=0 NormalZ=1 AngleXU=0 Radius=20.6155 StartAngle=5.7297 EndAngle=6.28319
    g19: LineSegment StartX=121.163 StartY=9.0125 StartZ=0 EndX=122.538 EndY=8.16329 EndZ=0
    g20: LineSegment StartX=124 StartY=38 StartZ=0 EndX=125.616 EndY=38 EndZ=0
    g21: LineSegment StartX=125.616 StartY=19 StartZ=0 EndX=125.616 EndY=38 EndZ=0
  constraints (50):
    c: Vertical(g0)
    c: Block(g0)
    c: Coincident(g1,g0)
    c: Block(g1)
    c: Coincident(g2,g1)
    c: Block(g2)
    c: Coincident(g3,g2)
    c: Horizontal(g3)
    c: Tangent(g3,g2)
    c: Coincident(g4,g0)
    c: Distance(g4) = 3
    c: Vertical(g4)
    c: Coincident(g5,g4)
    c: Horizontal(g5)
    c: Coincident(g6,g2)
    c: Coincident(g6,g5)
    c: Vertical(g6)
    c: Horizontal(g7)
    c: Distance(g7) = 105
    c: Coincident(g7,g1)
    c: Block(g3)
    c: Weight(g8) = 1
    c: Equal(g8,g9)
    c: Equal(g8,g10)
    c: InternalAlignment(g8,g11)
    c: InternalAlignment(g9,g11)
    c: InternalAlignment(g10,g11)
    c: InternalAlignment(g12,g11)
    c: InternalAlignment(g13,g11)
    c: Block(g11)
    c: Coincident(g14,g11)
    c: Coincident(g14,g3)
    c: Horizontal(g14)
    c: Block(g15)
    c: Coincident(g16,g11)
    c: Coincident(g16,g15)
    c: Vertical(g16)
    c: Distance(g16) = 14
    c: Coincident(g17,g15)
    c: Block(g18)
    c: Coincident(g19,g18)
    c: Coincident(g20,g7)
    c: Horizontal(g20)
    c: Vertical(g21)
    c: Coincident(g20,g21)
    c: Block(g20)
    c: Block(g21)
    c: Block(g19)
    c: Block(g17)
    c: Distance(g20) = 1.61553
FEATURE [Part::Extrusion] Extrude044
  Base = -> Sketch053
  Dir = (0,0,1)
  DirMode = 2
  FaceMakerClass = Part::FaceMakerBullseye
  LengthFwd = 72
  LengthRev = 0
  Solid = true
  Symmetric = false
FEATURE [Part::Fillet] Fillet036  label="top018"
  Base = -> Extrude044
  Edges = 1 edges r=2: [Edge41]
FEATURE [Sketcher::SketchObject] Sketch054
  FullyConstrained = false
  Placement = pos=(0,0,0) rot=(1,0,0;1.5708rad)
  sketch-geometry (24):
    g0: ArcOfCircle CenterX=-4 CenterY=-10.5 CenterZ=0 NormalX=0 NormalY=0 NormalZ=1 AngleXU=0 Radius=1.5 StartAngle=6e-16 EndAngle=3.14159
    g1: ArcOfCircle CenterX=-34.2 CenterY=-10.5 CenterZ=0 NormalX=0 NormalY=0 NormalZ=1 AngleXU=0 Radius=1.5 StartAngle=0 EndAngle=3.14159
    g2: ArcOfCircle CenterX=-34.2 CenterY=-27.7 CenterZ=0 NormalX=0 NormalY=0 NormalZ=1 AngleXU=0 Radius=1.5 StartAngle=3.14159 EndAngle=6.28319
    g3: ArcOfCircle CenterX=-4 CenterY=-27.7 CenterZ=0 NormalX=0 NormalY=0 NormalZ=1 AngleXU=0 Radius=1.5 StartAngle=3.1416 EndAngle=6.28319
    g4: ArcOfCircle CenterX=-10 CenterY=-4.3 CenterZ=0 NormalX=0 NormalY=0 NormalZ=1 AngleXU=0 Radius=1.5 StartAngle=2e-16 EndAngle=3.14159
    g5: ArcOfCircle CenterX=-16.1 CenterY=-1.8 CenterZ=0 NormalX=0 NormalY=0 NormalZ=1 AngleXU=0 Radius=1.5 StartAngle=5e-16 EndAngle=3.14159
    g6: ArcOfCircle CenterX=-22.1 CenterY=-1.8 CenterZ=0 NormalX=0 NormalY=0 NormalZ=1 AngleXU=0 Radius=1.5 StartAngle=5e-16 EndAngle=3.14159
    g7: ArcOfCircle CenterX=-28.2 CenterY=-4.3 CenterZ=0 NormalX=0 NormalY=0 NormalZ=1 AngleXU=0 Radius=1.5 StartAngle=2e-16 EndAngle=3.14159
    g8: ArcOfCircle CenterX=-10 CenterY=-33.9 CenterZ=0 NormalX=0 NormalY=0 NormalZ=1 AngleXU=0 Radius=1.5 StartAngle=3.14159 EndAngle=6.28319
    g9: ArcOfCircle CenterX=-16.1 CenterY=-36.4 CenterZ=0 NormalX=0 NormalY=0 NormalZ=1 AngleXU=0 Radius=1.5 StartAngle=3.14159 EndAngle=6.28319
    g10: ArcOfCircle CenterX=-22.1 CenterY=-36.4 CenterZ=0 NormalX=0 NormalY=0 NormalZ=1 AngleXU=0 Radius=1.5 StartAngle=3.14159 EndAngle=6.28319
    g11: ArcOfCircle CenterX=-28.2 CenterY=-33.9 CenterZ=0 NormalX=0 NormalY=0 NormalZ=1 AngleXU=0 Radius=1.5 StartAngle=3.14159 EndAngle=6.28319
    g12: LineSegment StartX=-35.7 StartY=-10.5 StartZ=0 EndX=-35.7 EndY=-27.7 EndZ=0
    g13: LineSegment StartX=-32.7 StartY=-10.5 StartZ=0 EndX=-32.7 EndY=-27.7 EndZ=0
    g14: LineSegment StartX=-29.7 StartY=-33.9 StartZ=0 EndX=-29.7 EndY=-4.3 EndZ=0
    g15: LineSegment StartX=-26.7 StartY=-33.9 StartZ=0 EndX=-26.7 EndY=-4.3 EndZ=0
    g16: LineSegment StartX=-2.5 StartY=-10.5 StartZ=0 EndX=-2.5 EndY=-27.7 EndZ=0
    g17: LineSegment StartX=-8.5 StartY=-4.3 StartZ=0 EndX=-8.5 EndY=-33.9 EndZ=0
    g18: LineSegment StartX=-5.5 StartY=-10.5 StartZ=0 EndX=-5.5 EndY=-27.7 EndZ=0
    g19: LineSegment StartX=-11.5 StartY=-4.3 StartZ=0 EndX=-11.5 EndY=-33.9 EndZ=0
    g20: LineSegment StartX=-14.6 StartY=-1.8 StartZ=0 EndX=-14.6 EndY=-36.4 EndZ=0
    g21: LineSegment StartX=-17.6 StartY=-1.8 StartZ=0 EndX=-17.6 EndY=-36.4 EndZ=0
    g22: LineSegment StartX=-20.6 StartY=-36.4 StartZ=0 EndX=-20.6 EndY=-1.8 EndZ=0
    g23: LineSegment StartX=-23.6 StartY=-1.8 StartZ=0 EndX=-23.6 EndY=-36.4 EndZ=0
  constraints (48):
    c: Block(g0)
    c: Block(g1)
    c: Block(g2)
    c: Block(g3)
    c: Block(g4)
    c: Block(g5)
    c: Block(g6)
    c: Block(g7)
    c: Block(g8)
    c: Block(g9)
    c: Block(g10)
    c: Block(g11)
    c: Coincident(g12,g1)
    c: Coincident(g12,g2)
    c: Vertical(g12)
    c: Coincident(g13,g1)
    c: Coincident(g13,g2)
    c: Vertical(g13)
    c: Coincident(g14,g11)
    c: Coincident(g14,g7)
    c: Vertical(g14)
    c: Coincident(g15,g11)
    c: Coincident(g15,g7)
    c: Vertical(g15)
    c: Coincident(g16,g0)
    c: Coincident(g16,g3)
    c: Vertical(g16)
    c: Coincident(g17,g4)
    c: Coincident(g17,g8)
    c: Vertical(g17)
    c: Coincident(g18,g0)
    c: Coincident(g18,g3)
    c: Vertical(g18)
    c: Coincident(g19,g4)
    c: Coincident(g19,g8)
    c: Vertical(g19)
    c: Coincident(g20,g5)
    c: Coincident(g20,g9)
    c: Vertical(g20)
    c: Coincident(g21,g5)
    c: Coincident(g21,g9)
    c: Vertical(g21)
    c: Coincident(g22,g10)
    c: Coincident(g22,g6)
    c: Vertical(g22)
    c: Coincident(g23,g6)
    c: Coincident(g23,g10)
    c: Vertical(g23)
FEATURE [Part::Extrusion] Extrude045  label="removeToCreateFanGrillHoles003"
  Base = -> Sketch054
  Dir = (0,-1,6e-16)
  DirMode = 2
  FaceMakerClass = Part::FaceMakerBullseye
  LengthFwd = 10
  LengthRev = 0
  Placement = pos=(65.4,44,54.82) rot=(0,0,1;0rad)
  Solid = true
  Symmetric = false
FEATURE [Part::Feature] Face105 .. Face108  x4 (patterned run collapsed; names and placements below)
  shape: bbox 3.5 x 17.8 x 2e-07 mm, 1 faces, 0 solids (baked)
FEATURE [Part::Revolution] Revolve113  label="removeToCreateScrewAndThreadedInsertHole041"
  Angle = 360
  Axis = (0,1,0)
  Base = (0,0,0)
  FaceMakerClass = Part::FaceMakerBullseye
  Placement = pos=(62.3,30.3,19.7) rot=(0,0,1;0rad)
  Solid = false
  Source = -> Face105
  Symmetric = false
FEATURE [Part::Revolution] Revolve114  label="removeToCreateScrewAndThreadedInsertHole042"
  Angle = 360
  Axis = (0,1,0)
  Base = (0,0,0)
  FaceMakerClass = Part::FaceMakerBullseye
  Placement = pos=(62.3,30.3,51.7) rot=(0,0,1;0rad)
  Solid = false
  Source = -> Face106
  Symmetric = false
FEATURE [Part::Revolution] Revolve115  label="removeToCreateScrewAndThreadedInsertHole043"
  Angle = 360
  Axis = (0,1,0)
  Base = (0,0,0)
  FaceMakerClass = Part::FaceMakerBullseye
  Placement = pos=(30.3,30.3,19.7) rot=(0,0,1;0rad)
  Solid = false
  Source = -> Face107
  Symmetric = false
FEATURE [Part::Revolution] Revolve116  label="removeToCreateScrewAndThreadedInsertHole044"
  Angle = 360
  Axis = (0,1,0)
  Base = (0,0,0)
  FaceMakerClass = Part::FaceMakerBullseye
  Placement = pos=(30.3,30.3,51.7) rot=(0,0,1;0rad)
  Solid = false
  Source = -> Face108
  Symmetric = false
FEATURE [Part::MultiFuse] Fusion083  label="createThreadedInsertHolesForFan004"
  Shapes = -> [Revolve113,Revolve114,Revolve115,Revolve116]
FEATURE [Part::Box] Box024  label="removeToCreteHoleForPlugHousing026"
  AttacherType = Attacher::AttachEngine3D
  Height = 28.6
  Length = 10
  Placement = pos=(-2,0,21.7) rot=(0,0,1;0rad)
  Width = 19
FEATURE [Part::Cylinder] Cylinder038  label="removeToCreteHoleForPlugHousing027"
  Angle = 360
  AttacherType = Attacher::AttachEngine3D
  Height = 20
  Placement = pos=(-2,19,36) rot=(0,1,0;1.5708rad)
  Radius = 14.3
FEATURE [Part::MultiFuse] Fusion084  label="removeToCreteHoleForPlugHousing028"
  Shapes = -> [Box024,Cylinder038]
FEATURE [Part::Cylinder] Cylinder039
  Angle = 360
  AttacherType = Attacher::AttachEngine3D
  Height = 20
  Placement = pos=(0,0,36.15) rot=(0,0,1;0rad)
  Radius = 14.3
FEATURE [Part::Cylinder] Cylinder040
  Angle = 360
  AttacherType = Attacher::AttachEngine3D
  Height = 10
  Placement = pos=(0,0,36.15) rot=(0,0,1;0rad)
  Radius = 4
FEATURE [Part::Box] Box025  label="removeToCreteHoleForPlugHousing030"
  AttacherType = Attacher::AttachEngine3D
  Height = 28.6
  Length = 20
  Placement = pos=(106.15,0,21.7) rot=(0,0,1;0rad)
  Width = 19
FEATURE [Part::MultiFuse] Fusion086  label="removeToCreteHoleForPlugHousing031"
  Placement = pos=(70,19,36) rot=(0,1,0;1.5708rad)
  Shapes = -> [Cylinder039,Cylinder040]
FEATURE [Part::MultiFuse] Fusion085  label="removeToCreteHoleForPlugHousing029"
  Shapes = -> [Box025,Fusion086]
FEATURE [Sketcher::SketchObject] Sketch055
  FullyConstrained = true
  Placement = pos=(117,19,0) rot=(0.57735,0.57735,0.57735;2.0944rad)
  sketch-geometry (48):
    g0: LineSegment StartX=-49.19 StartY=69.25 StartZ=0 EndX=-49.19 EndY=66.25 EndZ=0
    g1: LineSegment StartX=-49.19 StartY=63.5 StartZ=0 EndX=-49.19 EndY=60.5 EndZ=0
    g2: LineSegment StartX=-49.19 StartY=57.75 StartZ=0 EndX=-49.19 EndY=54.75 EndZ=0
    g3: LineSegment StartX=-49.19 StartY=52 StartZ=0 EndX=-49.19 EndY=49 EndZ=0
    g4: LineSegment StartX=-49.19 StartY=46.25 StartZ=0 EndX=-49.19 EndY=43.25 EndZ=0
    g5: LineSegment StartX=-49.19 StartY=40.5 StartZ=0 EndX=-49.19 EndY=37.5 EndZ=0
    g6: LineSegment StartX=-49.19 StartY=34.5 StartZ=0 EndX=-49.19 EndY=31.5 EndZ=0
    g7: LineSegment StartX=-49.19 StartY=28.75 StartZ=0 EndX=-49.19 EndY=25.75 EndZ=0
    g8: LineSegment StartX=-49.19 StartY=23 StartZ=0 EndX=-49.19 EndY=20 EndZ=0
    g9: LineSegment StartX=-49.19 StartY=17.25 StartZ=0 EndX=-49.19 EndY=14.25 EndZ=0
    g10: LineSegment StartX=-49.19 StartY=11.5 StartZ=0 EndX=-49.19 EndY=8.5 EndZ=0
    g11: LineSegment StartX=-49.19 StartY=5.75 StartZ=0 EndX=-49.19 EndY=2.75 EndZ=0
    g12: ArcOfCircle CenterX=-1.5 CenterY=67.75 CenterZ=0 NormalX=0 NormalY=0 NormalZ=1 AngleXU=0 Radius=1.5 StartAngle=4.71239 EndAngle=7.85398
    g13: ArcOfCircle CenterX=-1.5 CenterY=62 CenterZ=0 NormalX=0 NormalY=0 NormalZ=1 AngleXU=0 Radius=1.5 StartAngle=4.71239 EndAngle=7.85398
    g14: ArcOfCircle CenterX=-1.5 CenterY=56.25 CenterZ=0 NormalX=0 NormalY=0 NormalZ=1 AngleXU=0 Radius=1.5 StartAngle=4.71239 EndAngle=7.85398
    g15: ArcOfCircle CenterX=-11.49 CenterY=50.5 CenterZ=0 NormalX=0 NormalY=0 NormalZ=1 AngleXU=0 Radius=1.5 StartAngle=4.71239 EndAngle=7.85398
    g16: ArcOfCircle CenterX=-16.28 CenterY=44.75 CenterZ=0 NormalX=0 NormalY=0 NormalZ=1 AngleXU=0 Radius=1.5 StartAngle=4.71239 EndAngle=7.85398
    g17: ArcOfCircle CenterX=-18.2337 CenterY=39 CenterZ=0 NormalX=0 NormalY=0 NormalZ=1 AngleXU=0 Radius=1.5 StartAngle=4.71485 EndAngle=7.85398
    g18: ArcOfCircle CenterX=-16.2837 CenterY=27.25 CenterZ=0 NormalX=0 NormalY=0 NormalZ=1 AngleXU=0 Radius=1.5 StartAngle=4.71485 EndAngle=7.85398
    g19: ArcOfCircle CenterX=-18.2337 CenterY=33 CenterZ=0 NormalX=0 NormalY=0 NormalZ=1 AngleXU=0 Radius=1.5 StartAngle=4.71485 EndAngle=7.85398
    g20: ArcOfCircle CenterX=-11.49 CenterY=21.5 CenterZ=0 NormalX=0 NormalY=0 NormalZ=1 AngleXU=0 Radius=1.5 StartAngle=4.71239 EndAngle=7.85398
    g21: ArcOfCircle CenterX=-1.5 CenterY=4.25 CenterZ=0 NormalX=0 NormalY=0 NormalZ=1 AngleXU=0 Radius=1.5 StartAngle=4.71239 EndAngle=7.85398
    g22: ArcOfCircle CenterX=-1.5 CenterY=10 CenterZ=0 NormalX=0 NormalY=0 NormalZ=1 AngleXU=0 Radius=1.5 StartAngle=4.71239 EndAngle=7.85398
    g23: ArcOfCircle CenterX=-1.5 CenterY=15.75 CenterZ=0 NormalX=0 NormalY=0 NormalZ=1 AngleXU=0 Radius=1.5 StartAngle=4.71239 EndAngle=7.85398
    g24: LineSegment StartX=-49.19 StartY=69.25 StartZ=0 EndX=-1.5 EndY=69.25 EndZ=0
    g25: LineSegment StartX=-49.19 StartY=66.25 StartZ=0 EndX=-1.5 EndY=66.25 EndZ=0
    g26: LineSegment StartX=-49.19 StartY=63.5 StartZ=0 EndX=-1.5 EndY=63.5 EndZ=0
    g27: LineSegment StartX=-49.19 StartY=60.5 StartZ=0 EndX=-1.5 EndY=60.5 EndZ=0
    g28: LineSegment StartX=-49.19 StartY=57.75 StartZ=0 EndX=-1.5 EndY=57.75 EndZ=0
    g29: LineSegment StartX=-49.19 StartY=54.75 StartZ=0 EndX=-1.5 EndY=54.75 EndZ=0
    g30: LineSegment StartX=-49.19 StartY=52 StartZ=0 EndX=-11.49 EndY=52 EndZ=0
    g31: LineSegment StartX=-49.19 StartY=49 StartZ=0 EndX=-11.49 EndY=49 EndZ=0
    g32: LineSegment StartX=-49.19 StartY=46.25 StartZ=0 EndX=-16.28 EndY=46.25 EndZ=0
    g33: LineSegment StartX=-49.19 StartY=43.25 StartZ=0 EndX=-16.28 EndY=43.25 EndZ=0
    g34: LineSegment StartX=-49.19 StartY=40.5 StartZ=0 EndX=-18.2337 EndY=40.5 EndZ=0
    g35: LineSegment StartX=-49.19 StartY=37.5 StartZ=0 EndX=-18.23 EndY=37.5 EndZ=0
    g36: LineSegment StartX=-49.19 StartY=34.5 StartZ=0 EndX=-18.2337 EndY=34.5 EndZ=0
    g37: LineSegment StartX=-49.19 StartY=31.5 StartZ=0 EndX=-18.23 EndY=31.5 EndZ=0
    g38: LineSegment StartX=-49.19 StartY=28.75 StartZ=0 EndX=-16.2837 EndY=28.75 EndZ=0
    g39: LineSegment StartX=-49.19 StartY=25.75 StartZ=0 EndX=-16.28 EndY=25.75 EndZ=0
    g40: LineSegment StartX=-49.19 StartY=23 StartZ=0 EndX=-11.49 EndY=23 EndZ=0
    g41: LineSegment StartX=-49.19 StartY=20 StartZ=0 EndX=-11.49 EndY=20 EndZ=0
    g42: LineSegment StartX=-49.19 StartY=17.25 StartZ=0 EndX=-1.5 EndY=17.25 EndZ=0
    g43: LineSegment StartX=-49.19 StartY=14.25 StartZ=0 EndX=-1.5 EndY=14.25 EndZ=0
    g44: LineSegment StartX=-49.19 StartY=11.5 StartZ=0 EndX=-1.5 EndY=11.5 EndZ=0
    g45: LineSegment StartX=-49.19 StartY=8.5 StartZ=0 EndX=-1.5 EndY=8.5 EndZ=0
    g46: LineSegment StartX=-49.19 StartY=5.75 StartZ=0 EndX=-1.5 EndY=5.75 EndZ=0
    g47: LineSegment StartX=-49.19 StartY=2.75 StartZ=0 EndX=-1.5 EndY=2.75 EndZ=0
  constraints (120):
    c: Vertical(g0)
    c: Distance(g0) = 3
    c: Block(g0)
    c: Vertical(g1)
    c: Distance(g1) = 3
    c: Vertical(g2)
    c: Equal(g0,g2) = 3
    c: Block(g2)
    c: Vertical(g3)
    c: Equal(g1,g3) = 3
    c: Vertical(g4)
    c: Equal(g0,g4) = 3
    c: Block(g4)
    c: Vertical(g5)
    c: Equal(g1,g5) = 3
    c: Vertical(g6)
    c: Equal(g0,g6) = 3
    c: Block(g6)
    c: Vertical(g7)
    c: Equal(g1,g7) = 3
    c: Vertical(g8)
    c: Equal(g0,g8) = 3
    c: Block(g8)
    c: Vertical(g9)
    c: Equal(g1,g9) = 3
    c: Vertical(g10)
    c: Equal(g0,g10) = 3
    c: Block(g10)
    c: Vertical(g11)
    c: Equal(g1,g11) = 3
    c: Block(g12)
    c: Block(g13)
    c: Block(g14)
    c: Block(g15)
    c: Block(g16)
    c: Block(g17)
    c: Block(g18)
    c: Block(g19)
    c: Block(g20)
    c: Block(g21)
    c: Block(g22)
    c: Block(g23)
    c: Block(g11)
    c: Block(g9)
    c: Block(g7)
    c: Block(g5)
    c: Block(g3)
    c: Block(g1)
    c: Coincident(g24,g0)
    c: Coincident(g24,g12)
    c: Horizontal(g24)
    c: Coincident(g25,g0)
    c: Coincident(g25,g12)
    c: Horizontal(g25)
    c: Coincident(g26,g1)
    c: Coincident(g26,g13)
    c: Horizontal(g26)
    c: Coincident(g27,g1)
    c: Coincident(g27,g13)
    c: Horizontal(g27)
    c: Coincident(g28,g2)
    c: Coincident(g28,g14)
    c: Horizontal(g28)
    c: Coincident(g29,g2)
    c: Coincident(g29,g14)
    c: Horizontal(g29)
    c: Coincident(g30,g3)
    c: Coincident(g30,g15)
    c: Horizontal(g30)
    c: Coincident(g31,g3)
    c: Coincident(g31,g15)
    c: Horizontal(g31)
    c: Coincident(g32,g4)
    c: Coincident(g32,g16)
    c: Horizontal(g32)
    c: Coincident(g33,g4)
    c: Coincident(g33,g16)
    c: Horizontal(g33)
    c: Coincident(g34,g5)
    c: Coincident(g34,g17)
    c: Horizontal(g34)
    c: Coincident(g35,g5)
    c: Coincident(g35,g17)
    c: Horizontal(g35)
    c: Coincident(g36,g6)
    c: Coincident(g36,g19)
    c: Horizontal(g36)
    c: Coincident(g37,g6)
    c: Coincident(g37,g19)
    c: Horizontal(g37)
    c: Coincident(g38,g7)
    c: Coincident(g38,g18)
    c: Horizontal(g38)
    c: Coincident(g39,g7)
    c: Coincident(g39,g18)
    c: Horizontal(g39)
    c: Coincident(g40,g8)
    c: Coincident(g40,g20)
    c: Horizontal(g40)
    c: Coincident(g41,g8)
    c: Coincident(g41,g20)
    c: Horizontal(g41)
    c: Coincident(g42,g9)
    c: Coincident(g42,g23)
    c: Horizontal(g42)
    c: Coincident(g43,g9)
    c: Coincident(g43,g23)
    c: Horizontal(g43)
    c: Coincident(g44,g10)
    c: Coincident(g44,g22)
    c: Horizontal(g44)
    c: Coincident(g45,g10)
    c: Coincident(g45,g22)
    c: Horizontal(g45)
    c: Coincident(g46,g11)
    c: Coincident(g46,g21)
    c: Horizontal(g46)
    c: Coincident(g47,g11)
    c: Coincident(g47,g21)
    c: Horizontal(g47)
FEATURE [Part::Extrusion] Extrude046
  Base = -> Sketch055
  Dir = (1,0,0)
  DirMode = 2
  FaceMakerClass = Part::FaceMakerBullseye
  LengthFwd = 23
  LengthRev = 0
  Placement = pos=(-19,0,0) rot=(0,0,1;0rad)
  Solid = true
  Symmetric = false
FEATURE [Part::Fillet] Fillet038  label="removeToCreateVentalationHoles001"
  Base = -> Extrude046
  Edges = <same value as first occurrence — deduplicated (x6 in doc)>
  Placement = pos=(7,0,0) rot=(0,0,1;0rad)
FEATURE [Sketcher::SketchObject] Sketch056  label="topSketch014"
  FullyConstrained = true
  sketch-geometry (22):
    g0: LineSegment StartX=5.21097e-06 StartY=3 StartZ=0 EndX=5.21097e-06 EndY=19 EndZ=0
    g1: ArcOfCircle CenterX=19 CenterY=19 CenterZ=0 NormalX=0 NormalY=0 NormalZ=1 AngleXU=0 Radius=19 StartAngle=1.5708 EndAngle=3.14159
    g2: ArcOfCircle CenterX=19 CenterY=19 CenterZ=0 NormalX=0 NormalY=0 NormalZ=1 AngleXU=0 Radius=16 StartAngle=1.5708 EndAngle=3.14159
    g3: LineSegment StartX=114 StartY=35 StartZ=0 EndX=19 EndY=35 EndZ=0
    g4: LineSegment StartX=5.21097e-06 StartY=3 StartZ=0 EndX=5.21097e-06 EndY=0 EndZ=0
    g5: LineSegment StartX=3 StartY=0 StartZ=0 EndX=5.21097e-06 EndY=0 EndZ=0
    g6: LineSegment StartX=3 StartY=19 StartZ=0 EndX=3 EndY=0 EndZ=0
    g7: LineSegment StartX=19 StartY=38 StartZ=0 EndX=124 EndY=38 EndZ=0
    g8: Circle CenterX=119 CenterY=35 CenterZ=0 NormalX=0 NormalY=0 NormalZ=1 AngleXU=0 Radius=1
    g9: Circle CenterX=121 CenterY=35 CenterZ=0 NormalX=0 NormalY=0 NormalZ=1 AngleXU=0 Radius=1
    g10: Circle CenterX=121 CenterY=33 CenterZ=0 NormalX=0 NormalY=0 NormalZ=1 AngleXU=0 Radius=1
    g11: BSplineCurve PolesCount=3 KnotsCount=2 Degree=2 IsPeriodic=0
    g12: GeomPoint X=119 Y=35 Z=0
    g13: GeomPoint X=121 Y=33 Z=0
    g14: LineSegment StartX=119 StartY=35 StartZ=0 EndX=114 EndY=35 EndZ=0
    g15: ArcOfCircle CenterX=105 CenterY=19 CenterZ=0 NormalX=0 NormalY=0 NormalZ=1 AngleXU=0 Radius=16 StartAngle=5.60905 EndAngle=6.28319
    g16: LineSegment StartX=121 StartY=33 StartZ=0 EndX=121 EndY=19 EndZ=0
    g17: LineSegment StartX=117.5 StartY=9.01251 StartZ=0 EndX=121.163 EndY=9.0125 EndZ=0
    g18: ArcOfCircle CenterX=105 CenterY=19 CenterZ=0 NormalX=0 NormalY=0 NormalZ=1 AngleXU=0 Radius=20.6155 StartAngle=5.7297 EndAngle=6.28319
    g19: LineSegment StartX=121.163 StartY=9.0125 StartZ=0 EndX=122.538 EndY=8.16329 EndZ=0
    g20: LineSegment StartX=124 StartY=38 StartZ=0 EndX=125.616 EndY=38 EndZ=0
    g21: LineSegment StartX=125.616 StartY=19 StartZ=0 EndX=125.616 EndY=38 EndZ=0
  constraints (49):
    c: Vertical(g0)
    c: Block(g0)
    c: Coincident(g1,g0)
    c: Block(g1)
    c: Coincident(g2,g1)
    c: Block(g2)
    c: Coincident(g3,g2)
    c: Horizontal(g3)
    c: Tangent(g3,g2)
    c: Coincident(g4,g0)
    c: Distance(g4) = 3
    c: Vertical(g4)
    c: Coincident(g5,g4)
    c: Horizontal(g5)
    c: Coincident(g6,g2)
    c: Coincident(g6,g5)
    c: Vertical(g6)
    c: Horizontal(g7)
    c: Distance(g7) = 105
    c: Coincident(g7,g1)
    c: Block(g3)
    c: Weight(g8) = 1
    c: Equal(g8,g9)
    c: Equal(g8,g10)
    c: InternalAlignment(g8,g11)
    c: InternalAlignment(g9,g11)
    c: InternalAlignment(g10,g11)
    c: InternalAlignment(g12,g11)
    c: InternalAlignment(g13,g11)
    c: Block(g11)
    c: Coincident(g14,g11)
    c: Coincident(g14,g3)
    c: Horizontal(g14)
    c: Block(g15)
    c: Coincident(g16,g11)
    c: Coincident(g16,g15)
    c: Vertical(g16)
    c: Distance(g16) = 14
    c: Coincident(g17,g15)
    c: Block(g18)
    c: Coincident(g19,g18)
    c: Coincident(g20,g7)
    c: Horizontal(g20)
    c: Vertical(g21)
    c: Coincident(g20,g21)
    c: Block(g20)
    c: Block(g21)
    c: Block(g19)
    c: Block(g17)
FEATURE [Part::Box] Box026  label="removeToCreteHoleForPlugHousing032"
  AttacherType = Attacher::AttachEngine3D
  Height = 28.6
  Length = 10
  Placement = pos=(-2,0,21.7) rot=(0,0,1;0rad)
  Width = 19
FEATURE [Part::Feature] Face109 .. Face112  x4 (patterned run collapsed; names and placements below)
  shape: bbox 3.5 x 17.8 x 2e-07 mm, 1 faces, 0 solids (baked)
FEATURE [Part::Revolution] Revolve117  label="removeToCreateScrewAndThreadedInsertHole045"
  Angle = 360
  Axis = (0,1,0)
  Base = (0,0,0)
  FaceMakerClass = Part::FaceMakerBullseye
  Placement = pos=(62.3,30.3,19.7) rot=(0,0,1;0rad)
  Solid = false
  Source = -> Face109
  Symmetric = false
FEATURE [Part::Revolution] Revolve118  label="removeToCreateScrewAndThreadedInsertHole046"
  Angle = 360
  Axis = (0,1,0)
  Base = (0,0,0)
  FaceMakerClass = Part::FaceMakerBullseye
  Placement = pos=(62.3,30.3,51.7) rot=(0,0,1;0rad)
  Solid = false
  Source = -> Face110
  Symmetric = false
FEATURE [Part::Revolution] Revolve119  label="removeToCreateScrewAndThreadedInsertHole047"
  Angle = 360
  Axis = (0,1,0)
  Base = (0,0,0)
  FaceMakerClass = Part::FaceMakerBullseye
  Placement = pos=(30.3,30.3,19.7) rot=(0,0,1;0rad)
  Solid = false
  Source = -> Face111
  Symmetric = false
FEATURE [Part::Revolution] Revolve120  label="removeToCreateScrewAndThreadedInsertHole048"
  Angle = 360
  Axis = (0,1,0)
  Base = (0,0,0)
  FaceMakerClass = Part::FaceMakerBullseye
  Placement = pos=(30.3,30.3,51.7) rot=(0,0,1;0rad)
  Solid = false
  Source = -> Face112
  Symmetric = false
FEATURE [Part::MultiFuse] Fusion087  label="createThreadedInsertHolesForFan005"
  Shapes = -> [Revolve117,Revolve118,Revolve119,Revolve120]
FEATURE [Part::Extrusion] Extrude047
  Base = -> Sketch056
  Dir = (0,0,1)
  DirMode = 2
  FaceMakerClass = Part::FaceMakerBullseye
  LengthFwd = 72
  LengthRev = 0
  Solid = true
  Symmetric = false
FEATURE [Part::Fillet] Fillet039  label="top019"
  Base = -> Extrude047
  Edges = 1 edges r=2: [Edge35]
FEATURE [Sketcher::SketchObject] Sketch057
  FullyConstrained = false
  Placement = pos=(0,0,0) rot=(1,0,0;1.5708rad)
  sketch-geometry (24):
    g0: ArcOfCircle CenterX=-4 CenterY=-10.5 CenterZ=0 NormalX=0 NormalY=0 NormalZ=1 AngleXU=0 Radius=1.5 StartAngle=6e-16 EndAngle=3.14159
    g1: ArcOfCircle CenterX=-34.2 CenterY=-10.5 CenterZ=0 NormalX=0 NormalY=0 NormalZ=1 AngleXU=0 Radius=1.5 StartAngle=0 EndAngle=3.14159
    g2: ArcOfCircle CenterX=-34.2 CenterY=-27.7 CenterZ=0 NormalX=0 NormalY=0 NormalZ=1 AngleXU=0 Radius=1.5 StartAngle=3.14159 EndAngle=6.28319
    g3: ArcOfCircle CenterX=-4 CenterY=-27.7 CenterZ=0 NormalX=0 NormalY=0 NormalZ=1 AngleXU=0 Radius=1.5 StartAngle=3.1416 EndAngle=6.28319
    g4: ArcOfCircle CenterX=-10 CenterY=-4.3 CenterZ=0 NormalX=0 NormalY=0 NormalZ=1 AngleXU=0 Radius=1.5 StartAngle=2e-16 EndAngle=3.14159
    g5: ArcOfCircle CenterX=-16.1 CenterY=-1.8 CenterZ=0 NormalX=0 NormalY=0 NormalZ=1 AngleXU=0 Radius=1.5 StartAngle=5e-16 EndAngle=3.14159
    g6: ArcOfCircle CenterX=-22.1 CenterY=-1.8 CenterZ=0 NormalX=0 NormalY=0 NormalZ=1 AngleXU=0 Radius=1.5 StartAngle=5e-16 EndAngle=3.14159
    g7: ArcOfCircle CenterX=-28.2 CenterY=-4.3 CenterZ=0 NormalX=0 NormalY=0 NormalZ=1 AngleXU=0 Radius=1.5 StartAngle=2e-16 EndAngle=3.14159
    g8: ArcOfCircle CenterX=-10 CenterY=-33.9 CenterZ=0 NormalX=0 NormalY=0 NormalZ=1 AngleXU=0 Radius=1.5 StartAngle=3.14159 EndAngle=6.28319
    g9: ArcOfCircle CenterX=-16.1 CenterY=-36.4 CenterZ=0 NormalX=0 NormalY=0 NormalZ=1 AngleXU=0 Radius=1.5 StartAngle=3.14159 EndAngle=6.28319
    g10: ArcOfCircle CenterX=-22.1 CenterY=-36.4 CenterZ=0 NormalX=0 NormalY=0 NormalZ=1 AngleXU=0 Radius=1.5 StartAngle=3.14159 EndAngle=6.28319
    g11: ArcOfCircle CenterX=-28.2 CenterY=-33.9 CenterZ=0 NormalX=0 NormalY=0 NormalZ=1 AngleXU=0 Radius=1.5 StartAngle=3.14159 EndAngle=6.28319
    g12: LineSegment StartX=-35.7 StartY=-10.5 StartZ=0 EndX=-35.7 EndY=-27.7 EndZ=0
    g13: LineSegment StartX=-32.7 StartY=-10.5 StartZ=0 EndX=-32.7 EndY=-27.7 EndZ=0
    g14: LineSegment StartX=-29.7 StartY=-33.9 StartZ=0 EndX=-29.7 EndY=-4.3 EndZ=0
    g15: LineSegment StartX=-26.7 StartY=-33.9 StartZ=0 EndX=-26.7 EndY=-4.3 EndZ=0
    g16: LineSegment StartX=-2.5 StartY=-10.5 StartZ=0 EndX=-2.5 EndY=-27.7 EndZ=0
    g17: LineSegment StartX=-8.5 StartY=-4.3 StartZ=0 EndX=-8.5 EndY=-33.9 EndZ=0
    g18: LineSegment StartX=-5.5 StartY=-10.5 StartZ=0 EndX=-5.5 EndY=-27.7 EndZ=0
    g19: LineSegment StartX=-11.5 StartY=-4.3 StartZ=0 EndX=-11.5 EndY=-33.9 EndZ=0
    g20: LineSegment StartX=-14.6 StartY=-1.8 StartZ=0 EndX=-14.6 EndY=-36.4 EndZ=0
    g21: LineSegment StartX=-17.6 StartY=-1.8 StartZ=0 EndX=-17.6 EndY=-36.4 EndZ=0
    g22: LineSegment StartX=-20.6 StartY=-36.4 StartZ=0 EndX=-20.6 EndY=-1.8 EndZ=0
    g23: LineSegment StartX=-23.6 StartY=-1.8 StartZ=0 EndX=-23.6 EndY=-36.4 EndZ=0
  constraints (48):
    c: Block(g0)
    c: Block(g1)
    c: Block(g2)
    c: Block(g3)
    c: Block(g4)
    c: Block(g5)
    c: Block(g6)
    c: Block(g7)
    c: Block(g8)
    c: Block(g9)
    c: Block(g10)
    c: Block(g11)
    c: Coincident(g12,g1)
    c: Coincident(g12,g2)
    c: Vertical(g12)
    c: Coincident(g13,g1)
    c: Coincident(g13,g2)
    c: Vertical(g13)
    c: Coincident(g14,g11)
    c: Coincident(g14,g7)
    c: Vertical(g14)
    c: Coincident(g15,g11)
    c: Coincident(g15,g7)
    c: Vertical(g15)
    c: Coincident(g16,g0)
    c: Coincident(g16,g3)
    c: Vertical(g16)
    c: Coincident(g17,g4)
    c: Coincident(g17,g8)
    c: Vertical(g17)
    c: Coincident(g18,g0)
    c: Coincident(g18,g3)
    c: Vertical(g18)
    c: Coincident(g19,g4)
    c: Coincident(g19,g8)
    c: Vertical(g19)
    c: Coincident(g20,g5)
    c: Coincident(g20,g9)
    c: Vertical(g20)
    c: Coincident(g21,g5)
    c: Coincident(g21,g9)
    c: Vertical(g21)
    c: Coincident(g22,g10)
    c: Coincident(g22,g6)
    c: Vertical(g22)
    c: Coincident(g23,g6)
    c: Coincident(g23,g10)
    c: Vertical(g23)
FEATURE [Part::Extrusion] Extrude048  label="removeToCreateFanGrillHoles004"
  Base = -> Sketch057
  Dir = (0,-1,6e-16)
  DirMode = 2
  FaceMakerClass = Part::FaceMakerBullseye
  LengthFwd = 10
  LengthRev = 0
  Placement = pos=(65.4,44,54.82) rot=(0,0,1;0rad)
  Solid = true
  Symmetric = false
FEATURE [Part::Cut] Cut040  label="top021"
  Base = -> Fillet039
  Tool = -> Extrude048
FEATURE [Part::Cylinder] Cylinder041  label="removeToCreteHoleForPlugHousing034"
  Angle = 360
  AttacherType = Attacher::AttachEngine3D
  Height = 20
  Placement = pos=(-2,19,36) rot=(0,1,0;1.5708rad)
  Radius = 14.3
FEATURE [Part::MultiFuse] Fusion089  label="removeToCreteHoleForPlugHousing035"
  Shapes = -> [Box026,Cylinder041]
FEATURE [Part::Cylinder] Cylinder042
  Angle = 360
  AttacherType = Attacher::AttachEngine3D
  Height = 20
  Placement = pos=(0,0,36.15) rot=(0,0,1;0rad)
  Radius = 14.3
FEATURE [Part::Cylinder] Cylinder043
  Angle = 360
  AttacherType = Attacher::AttachEngine3D
  Height = 10
  Placement = pos=(0,0,36.15) rot=(0,0,1;0rad)
  Radius = 4
FEATURE [Part::Box] Box027  label="removeToCreteHoleForPlugHousing036"
  AttacherType = Attacher::AttachEngine3D
  Height = 28.6
  Length = 20
  Placement = pos=(106.15,0,21.7) rot=(0,0,1;0rad)
  Width = 19
FEATURE [Part::Cut] Cut041  label="top022"
  Base = -> Cut040
  Tool = -> Fusion087
FEATURE [Part::Cut] Cut039  label="top020"
  Base = -> Cut041
  Tool = -> Fusion089
FEATURE [Part::MultiFuse] Fusion090  label="removeToCreteHoleForPlugHousing037"
  Placement = pos=(70,19,36) rot=(0,1,0;1.5708rad)
  Shapes = -> [Cylinder042,Cylinder043]
FEATURE [Part::MultiFuse] Fusion088  label="removeToCreteHoleForPlugHousing033"
  Shapes = -> [Box027,Fusion090]
FEATURE [Part::Cut] Cut042  label="removeToCreteHoleForPlugHousing038"
  Base = -> Cut039
  Tool = -> Fusion088
FEATURE [Part::MultiFuse] Fusion091  label="removeFromTop"
  Shapes = -> [Fillet038,Fusion085,Fusion084,Fusion083,Extrude045]
FEATURE [Part::Cut] Cut043  label="REAL TOP ====="
  Base = -> Fillet036
  Tool = -> Fusion091
FEATURE [Part::MultiFuse] Fusion092  label="caseScrewPillarBracket016"
  Shapes = -> [Extrude030,Extrude031,Extrude032,Extrude033,Extrude034,Extrude035,Extrude036,Extrude037,Box013,Box014]
FEATURE [Sketcher::SketchObject] Sketch058  label="topSketch015"
  FullyConstrained = true
  sketch-geometry (20):
    g0: LineSegment StartX=5.21097e-06 StartY=3 StartZ=0 EndX=5.21097e-06 EndY=19 EndZ=0
    g1: ArcOfCircle CenterX=19 CenterY=19 CenterZ=0 NormalX=0 NormalY=0 NormalZ=1 AngleXU=0 Radius=19 StartAngle=1.5708 EndAngle=3.14159
    g2: ArcOfCircle CenterX=19 CenterY=19 CenterZ=0 NormalX=0 NormalY=0 NormalZ=1 AngleXU=0 Radius=16 StartAngle=1.5708 EndAngle=3.14159
    g3: LineSegment StartX=114 StartY=35 StartZ=0 EndX=19 EndY=35 EndZ=0
    g4: LineSegment StartX=5.21097e-06 StartY=3 StartZ=0 EndX=5.21097e-06 EndY=0 EndZ=0
    g5: LineSegment StartX=3 StartY=0 StartZ=0 EndX=5.21097e-06 EndY=0 EndZ=0
    g6: LineSegment StartX=3 StartY=19 StartZ=0 EndX=3 EndY=0 EndZ=0
    g7: LineSegment StartX=19 StartY=38 StartZ=0 EndX=124 EndY=38 EndZ=0
    g8: Circle CenterX=119 CenterY=35 CenterZ=0 NormalX=0 NormalY=0 NormalZ=1 AngleXU=0 Radius=1
    g9: Circle CenterX=121 CenterY=35 CenterZ=0 NormalX=0 NormalY=0 NormalZ=1 AngleXU=0 Radius=1
    g10: Circle CenterX=121 CenterY=33 CenterZ=0 NormalX=0 NormalY=0 NormalZ=1 AngleXU=0 Radius=1
    g11: BSplineCurve PolesCount=3 KnotsCount=2 Degree=2 IsPeriodic=0
    g12: GeomPoint X=119 Y=35 Z=0
    g13: GeomPoint X=121 Y=33 Z=0
    g14: LineSegment StartX=119 StartY=35 StartZ=0 EndX=114 EndY=35 EndZ=0
    g15: ArcOfCircle CenterX=105 CenterY=19 CenterZ=0 NormalX=0 NormalY=0 NormalZ=1 AngleXU=0 Radius=19 StartAngle=5.7297 EndAngle=6.28319
    g16: ArcOfCircle CenterX=105 CenterY=19 CenterZ=0 NormalX=0 NormalY=0 NormalZ=1 AngleXU=0 Radius=16 StartAngle=5.60905 EndAngle=6.28319
    g17: LineSegment StartX=121 StartY=33 StartZ=0 EndX=121 EndY=19 EndZ=0
    g18: LineSegment StartX=124 StartY=38 StartZ=0 EndX=124 EndY=19 EndZ=0
    g19: LineSegment StartX=117.5 StartY=9.01251 StartZ=0 EndX=121.163 EndY=9.0125 EndZ=0
  constraints (46):
    c: Vertical(g0)
    c: Block(g0)
    c: Coincident(g1,g0)
    c: Block(g1)
    c: Coincident(g2,g1)
    c: Block(g2)
    c: Coincident(g3,g2)
    c: Horizontal(g3)
    c: Tangent(g3,g2)
    c: Coincident(g4,g0)
    c: Distance(g4) = 3
    c: Vertical(g4)
    c: Coincident(g5,g4)
    c: Horizontal(g5)
    c: Coincident(g6,g2)
    c: Coincident(g6,g5)
    c: Vertical(g6)
    c: Horizontal(g7)
    c: Distance(g7) = 105
    c: Coincident(g7,g1)
    c: Block(g3)
    c: Weight(g8) = 1
    c: Equal(g8,g9)
    c: Equal(g8,g10)
    c: InternalAlignment(g8,g11)
    c: InternalAlignment(g9,g11)
    c: InternalAlignment(g10,g11)
    c: InternalAlignment(g12,g11)
    c: InternalAlignment(g13,g11)
    c: Block(g11)
    c: Coincident(g14,g11)
    c: Coincident(g14,g3)
    c: Horizontal(g14)
    c: Block(g15)
    c: Coincident(g16,g15)
    c: Block(g16)
    c: Coincident(g17,g11)
    c: Coincident(g17,g16)
    c: Vertical(g17)
    c: Distance(g17) = 14
    c: Coincident(g18,g7)
    c: Coincident(g18,g15)
    c: Vertical(g18)
    c: Distance(g18) = 19
    c: Coincident(g19,g16)
    c: Coincident(g19,g15)
FEATURE [Part::Extrusion] Extrude049  label="top023"
  Base = -> Sketch058
  Dir = (0,0,1)
  DirMode = 2
  FaceMakerClass = Part::FaceMakerBullseye
  LengthFwd = 72
  LengthRev = 0
  Solid = true
  Symmetric = false
FEATURE [Sketcher::SketchObject] Sketch059
  FullyConstrained = true
  MapMode = 3
  Placement = pos=(0,0,0) rot=(1,0,0;1.5708rad)
  Support = -> [Extrude049]
  sketch-geometry (8):
    g0: Circle CenterX=80.351 CenterY=-67.6202 CenterZ=0 NormalX=0 NormalY=0 NormalZ=1 AngleXU=0 Radius=2
    g1: Circle CenterX=80.351 CenterY=-67.6202 CenterZ=0 NormalX=0 NormalY=0 NormalZ=1 AngleXU=0 Radius=3
    g2: Circle CenterX=80.351 CenterY=-4.92017 CenterZ=0 NormalX=0 NormalY=0 NormalZ=1 AngleXU=0 Radius=2
    g3: Circle CenterX=80.351 CenterY=-4.92017 CenterZ=0 NormalX=0 NormalY=0 NormalZ=1 AngleXU=0 Radius=3
    g4: Circle CenterX=23.851 CenterY=-4.92017 CenterZ=0 NormalX=0 NormalY=0 NormalZ=1 AngleXU=0 Radius=2
    g5: Circle CenterX=23.851 CenterY=-4.92017 CenterZ=0 NormalX=0 NormalY=0 NormalZ=1 AngleXU=0 Radius=3
    g6: Circle CenterX=23.851 CenterY=-67.6202 CenterZ=0 NormalX=0 NormalY=0 NormalZ=1 AngleXU=0 Radius=2
    g7: Circle CenterX=23.851 CenterY=-67.6202 CenterZ=0 NormalX=0 NormalY=0 NormalZ=1 AngleXU=0 Radius=3
  constraints (8):
    c: Block(g3)
    c: Block(g2)
    c: Block(g1)
    c: Block(g0)
    c: Block(g6)
    c: Block(g7)
    c: Block(g4)
    c: Block(g5)
FEATURE [Sketcher::SketchObject] Sketch060
  FullyConstrained = true
  MapMode = 3
  Placement = pos=(0,0,0) rot=(1,0,0;1.5708rad)
  Support = -> [Extrude049]
  sketch-geometry (8):
    g0: Circle CenterX=80.351 CenterY=-67.6202 CenterZ=0 NormalX=0 NormalY=0 NormalZ=1 AngleXU=0 Radius=3
    g1: Circle CenterX=80.351 CenterY=-4.92017 CenterZ=0 NormalX=0 NormalY=0 NormalZ=1 AngleXU=0 Radius=3
    g2: Circle CenterX=23.851 CenterY=-4.92017 CenterZ=0 NormalX=0 NormalY=0 NormalZ=1 AngleXU=0 Radius=3
    g3: Circle CenterX=23.851 CenterY=-67.6202 CenterZ=0 NormalX=0 NormalY=0 NormalZ=1 AngleXU=0 Radius=3
    g4: Circle CenterX=23.851 CenterY=-67.6202 CenterZ=0 NormalX=0 NormalY=0 NormalZ=1 AngleXU=0 Radius=5
    g5: Circle CenterX=80.351 CenterY=-67.6202 CenterZ=0 NormalX=0 NormalY=0 NormalZ=1 AngleXU=0 Radius=5
    g6: Circle CenterX=23.851 CenterY=-4.92017 CenterZ=0 NormalX=0 NormalY=0 NormalZ=1 AngleXU=0 Radius=5
    g7: Circle CenterX=80.351 CenterY=-4.92017 CenterZ=0 NormalX=0 NormalY=0 NormalZ=1 AngleXU=0 Radius=5
  constraints (8):
    c: Block(g1)
    c: Block(g0)
    c: Block(g3)
    c: Block(g2)
    c: Block(g5)
    c: Block(g4)
    c: Block(g6)
    c: Block(g7)
FEATURE [Sketcher::SketchObject] Sketch061
  FullyConstrained = true
  MapMode = 3
  Placement = pos=(0,0,0) rot=(1,0,0;1.5708rad)
  sketch-geometry (8):
    g0: Circle CenterX=80.351 CenterY=-67.6202 CenterZ=0 NormalX=0 NormalY=0 NormalZ=1 AngleXU=0 Radius=3
    g1: Circle CenterX=80.351 CenterY=-4.92017 CenterZ=0 NormalX=0 NormalY=0 NormalZ=1 AngleXU=0 Radius=3
    g2: Circle CenterX=23.851 CenterY=-4.92017 CenterZ=0 NormalX=0 NormalY=0 NormalZ=1 AngleXU=0 Radius=3
    g3: Circle CenterX=23.851 CenterY=-67.6202 CenterZ=0 NormalX=0 NormalY=0 NormalZ=1 AngleXU=0 Radius=3
    g4: Circle CenterX=23.851 CenterY=-67.6202 CenterZ=0 NormalX=0 NormalY=0 NormalZ=1 AngleXU=0 Radius=5
    g5: Circle CenterX=80.351 CenterY=-67.6202 CenterZ=0 NormalX=0 NormalY=0 NormalZ=1 AngleXU=0 Radius=5
    g6: Circle CenterX=23.851 CenterY=-4.92017 CenterZ=0 NormalX=0 NormalY=0 NormalZ=1 AngleXU=0 Radius=5
    g7: Circle CenterX=80.351 CenterY=-4.92017 CenterZ=0 NormalX=0 NormalY=0 NormalZ=1 AngleXU=0 Radius=5
  constraints (8):
    c: Block(g1)
    c: Block(g0)
    c: Block(g3)
    c: Block(g2)
    c: Block(g5)
    c: Block(g4)
    c: Block(g6)
    c: Block(g7)
FEATURE [Sketcher::SketchObject] Sketch062  label="topSketch016"
  FullyConstrained = true
  sketch-geometry (20):
    g0: LineSegment StartX=5.21097e-06 StartY=3 StartZ=0 EndX=5.21097e-06 EndY=19 EndZ=0
    g1: ArcOfCircle CenterX=19 CenterY=19 CenterZ=0 NormalX=0 NormalY=0 NormalZ=1 AngleXU=0 Radius=19 StartAngle=1.5708 EndAngle=3.14159
    g2: ArcOfCircle CenterX=19 CenterY=19 CenterZ=0 NormalX=0 NormalY=0 NormalZ=1 AngleXU=0 Radius=16 StartAngle=1.5708 EndAngle=3.14159
    g3: LineSegment StartX=114 StartY=35 StartZ=0 EndX=19 EndY=35 EndZ=0
    g4: LineSegment StartX=5.21097e-06 StartY=3 StartZ=0 EndX=5.21097e-06 EndY=0 EndZ=0
    g5: LineSegment StartX=3 StartY=0 StartZ=0 EndX=5.21097e-06 EndY=0 EndZ=0
    g6: LineSegment StartX=3 StartY=19 StartZ=0 EndX=3 EndY=0 EndZ=0
    g7: LineSegment StartX=19 StartY=38 StartZ=0 EndX=124 EndY=38 EndZ=0
    g8: Circle CenterX=119 CenterY=35 CenterZ=0 NormalX=0 NormalY=0 NormalZ=1 AngleXU=0 Radius=1
    g9: Circle CenterX=121 CenterY=35 CenterZ=0 NormalX=0 NormalY=0 NormalZ=1 AngleXU=0 Radius=1
    g10: Circle CenterX=121 CenterY=33 CenterZ=0 NormalX=0 NormalY=0 NormalZ=1 AngleXU=0 Radius=1
    g11: BSplineCurve PolesCount=3 KnotsCount=2 Degree=2 IsPeriodic=0
    g12: GeomPoint X=119 Y=35 Z=0
    g13: GeomPoint X=121 Y=33 Z=0
    g14: LineSegment StartX=119 StartY=35 StartZ=0 EndX=114 EndY=35 EndZ=0
    g15: ArcOfCircle CenterX=105 CenterY=19 CenterZ=0 NormalX=0 NormalY=0 NormalZ=1 AngleXU=0 Radius=19 StartAngle=5.7297 EndAngle=6.28319
    g16: ArcOfCircle CenterX=105 CenterY=19 CenterZ=0 NormalX=0 NormalY=0 NormalZ=1 AngleXU=0 Radius=16 StartAngle=5.60905 EndAngle=6.28319
    g17: LineSegment StartX=121 StartY=33 StartZ=0 EndX=121 EndY=19 EndZ=0
    g18: LineSegment StartX=124 StartY=38 StartZ=0 EndX=124 EndY=19 EndZ=0
    g19: LineSegment StartX=117.5 StartY=9.01251 StartZ=0 EndX=121.163 EndY=9.0125 EndZ=0
  constraints (46):
    c: Vertical(g0)
    c: Block(g0)
    c: Coincident(g1,g0)
    c: Block(g1)
    c: Coincident(g2,g1)
    c: Block(g2)
    c: Coincident(g3,g2)
    c: Horizontal(g3)
    c: Tangent(g3,g2)
    c: Coincident(g4,g0)
    c: Distance(g4) = 3
    c: Vertical(g4)
    c: Coincident(g5,g4)
    c: Horizontal(g5)
    c: Coincident(g6,g2)
    c: Coincident(g6,g5)
    c: Vertical(g6)
    c: Horizontal(g7)
    c: Distance(g7) = 105
    c: Coincident(g7,g1)
    c: Block(g3)
    c: Weight(g8) = 1
    c: Equal(g8,g9)
    c: Equal(g8,g10)
    c: InternalAlignment(g8,g11)
    c: InternalAlignment(g9,g11)
    c: InternalAlignment(g10,g11)
    c: InternalAlignment(g12,g11)
    c: InternalAlignment(g13,g11)
    c: Block(g11)
    c: Coincident(g14,g11)
    c: Coincident(g14,g3)
    c: Horizontal(g14)
    c: Block(g15)
    c: Coincident(g16,g15)
    c: Block(g16)
    c: Coincident(g17,g11)
    c: Coincident(g17,g16)
    c: Vertical(g17)
    c: Distance(g17) = 14
    c: Coincident(g18,g7)
    c: Coincident(g18,g15)
    c: Vertical(g18)
    c: Distance(g18) = 19
    c: Coincident(g19,g16)
    c: Coincident(g19,g15)
FEATURE [Part::Extrusion] Extrude053  label="top024"
  Base = -> Sketch062
  Dir = (0,0,1)
  DirMode = 2
  FaceMakerClass = Part::FaceMakerBullseye
  LengthFwd = 72
  LengthRev = 0
  Solid = true
  Symmetric = false
FEATURE [Sketcher::SketchObject] Sketch063
  FullyConstrained = true
  MapMode = 3
  Placement = pos=(0,0,0) rot=(1,0,0;1.5708rad)
  Support = -> [Extrude053]
  sketch-geometry (8):
    g0: Circle CenterX=80.351 CenterY=-67.6202 CenterZ=0 NormalX=0 NormalY=0 NormalZ=1 AngleXU=0 Radius=2
    g1: Circle CenterX=80.351 CenterY=-67.6202 CenterZ=0 NormalX=0 NormalY=0 NormalZ=1 AngleXU=0 Radius=3
    g2: Circle CenterX=80.351 CenterY=-4.92017 CenterZ=0 NormalX=0 NormalY=0 NormalZ=1 AngleXU=0 Radius=2
    g3: Circle CenterX=80.351 CenterY=-4.92017 CenterZ=0 NormalX=0 NormalY=0 NormalZ=1 AngleXU=0 Radius=3
    g4: Circle CenterX=23.851 CenterY=-4.92017 CenterZ=0 NormalX=0 NormalY=0 NormalZ=1 AngleXU=0 Radius=2
    g5: Circle CenterX=23.851 CenterY=-4.92017 CenterZ=0 NormalX=0 NormalY=0 NormalZ=1 AngleXU=0 Radius=3
    g6: Circle CenterX=23.851 CenterY=-67.6202 CenterZ=0 NormalX=0 NormalY=0 NormalZ=1 AngleXU=0 Radius=2
    g7: Circle CenterX=23.851 CenterY=-67.6202 CenterZ=0 NormalX=0 NormalY=0 NormalZ=1 AngleXU=0 Radius=3
  constraints (8):
    c: Block(g3)
    c: Block(g2)
    c: Block(g1)
    c: Block(g0)
    c: Block(g6)
    c: Block(g7)
    c: Block(g4)
    c: Block(g5)
FEATURE [Part::Extrusion] Extrude054
  Base = -> Sketch063
  Dir = (0,-1,2e-16)
  DirMode = 2
  FaceMakerClass = Part::FaceMakerBullseye
  LengthFwd = 6
  LengthRev = 0
  Placement = pos=(0,9,0) rot=(0,0,1;0rad)
  Solid = true
  Symmetric = false
FEATURE [Sketcher::SketchObject] Sketch064  label="topSketch017"
  FullyConstrained = true
  sketch-geometry (20):
    g0: LineSegment StartX=5.21097e-06 StartY=3 StartZ=0 EndX=5.21097e-06 EndY=19 EndZ=0
    g1: ArcOfCircle CenterX=19 CenterY=19 CenterZ=0 NormalX=0 NormalY=0 NormalZ=1 AngleXU=0 Radius=19 StartAngle=1.5708 EndAngle=3.14159
    g2: ArcOfCircle CenterX=19 CenterY=19 CenterZ=0 NormalX=0 NormalY=0 NormalZ=1 AngleXU=0 Radius=16 StartAngle=1.5708 EndAngle=3.14159
    g3: LineSegment StartX=114 StartY=35 StartZ=0 EndX=19 EndY=35 EndZ=0
    g4: LineSegment StartX=5.21097e-06 StartY=3 StartZ=0 EndX=5.21097e-06 EndY=0 EndZ=0
    g5: LineSegment StartX=3 StartY=0 StartZ=0 EndX=5.21097e-06 EndY=0 EndZ=0
    g6: LineSegment StartX=3 StartY=19 StartZ=0 EndX=3 EndY=0 EndZ=0
    g7: LineSegment StartX=19 StartY=38 StartZ=0 EndX=124 EndY=38 EndZ=0
    g8: Circle CenterX=119 CenterY=35 CenterZ=0 NormalX=0 NormalY=0 NormalZ=1 AngleXU=0 Radius=1
    g9: Circle CenterX=121 CenterY=35 CenterZ=0 NormalX=0 NormalY=0 NormalZ=1 AngleXU=0 Radius=1
    g10: Circle CenterX=121 CenterY=33 CenterZ=0 NormalX=0 NormalY=0 NormalZ=1 AngleXU=0 Radius=1
    g11: BSplineCurve PolesCount=3 KnotsCount=2 Degree=2 IsPeriodic=0
    g12: GeomPoint X=119 Y=35 Z=0
    g13: GeomPoint X=121 Y=33 Z=0
    g14: LineSegment StartX=119 StartY=35 StartZ=0 EndX=114 EndY=35 EndZ=0
    g15: ArcOfCircle CenterX=105 CenterY=19 CenterZ=0 NormalX=0 NormalY=0 NormalZ=1 AngleXU=0 Radius=19 StartAngle=5.7297 EndAngle=6.28319
    g16: ArcOfCircle CenterX=105 CenterY=19 CenterZ=0 NormalX=0 NormalY=0 NormalZ=1 AngleXU=0 Radius=16 StartAngle=5.60905 EndAngle=6.28319
    g17: LineSegment StartX=121 StartY=33 StartZ=0 EndX=121 EndY=19 EndZ=0
    g18: LineSegment StartX=124 StartY=38 StartZ=0 EndX=124 EndY=19 EndZ=0
    g19: LineSegment StartX=117.5 StartY=9.01251 StartZ=0 EndX=121.163 EndY=9.0125 EndZ=0
  constraints (46):
    c: Vertical(g0)
    c: Block(g0)
    c: Coincident(g1,g0)
    c: Block(g1)
    c: Coincident(g2,g1)
    c: Block(g2)
    c: Coincident(g3,g2)
    c: Horizontal(g3)
    c: Tangent(g3,g2)
    c: Coincident(g4,g0)
    c: Distance(g4) = 3
    c: Vertical(g4)
    c: Coincident(g5,g4)
    c: Horizontal(g5)
    c: Coincident(g6,g2)
    c: Coincident(g6,g5)
    c: Vertical(g6)
    c: Horizontal(g7)
    c: Distance(g7) = 105
    c: Coincident(g7,g1)
    c: Block(g3)
    c: Weight(g8) = 1
    c: Equal(g8,g9)
    c: Equal(g8,g10)
    c: InternalAlignment(g8,g11)
    c: InternalAlignment(g9,g11)
    c: InternalAlignment(g10,g11)
    c: InternalAlignment(g12,g11)
    c: InternalAlignment(g13,g11)
    c: Block(g11)
    c: Coincident(g14,g11)
    c: Coincident(g14,g3)
    c: Horizontal(g14)
    c: Block(g15)
    c: Coincident(g16,g15)
    c: Block(g16)
    c: Coincident(g17,g11)
    c: Coincident(g17,g16)
    c: Vertical(g17)
    c: Distance(g17) = 14
    c: Coincident(g18,g7)
    c: Coincident(g18,g15)
    c: Vertical(g18)
    c: Distance(g18) = 19
    c: Coincident(g19,g16)
    c: Coincident(g19,g15)
FEATURE [Sketcher::SketchObject] Sketch065
  FullyConstrained = true
  MapMode = 3
  Placement = pos=(0,0,0) rot=(1,0,0;1.5708rad)
  sketch-geometry (8):
    g0: Circle CenterX=80.351 CenterY=-67.6202 CenterZ=0 NormalX=0 NormalY=0 NormalZ=1 AngleXU=0 Radius=3
    g1: Circle CenterX=80.351 CenterY=-4.92017 CenterZ=0 NormalX=0 NormalY=0 NormalZ=1 AngleXU=0 Radius=3
    g2: Circle CenterX=23.851 CenterY=-4.92017 CenterZ=0 NormalX=0 NormalY=0 NormalZ=1 AngleXU=0 Radius=3
    g3: Circle CenterX=23.851 CenterY=-67.6202 CenterZ=0 NormalX=0 NormalY=0 NormalZ=1 AngleXU=0 Radius=3
    g4: Circle CenterX=23.851 CenterY=-67.6202 CenterZ=0 NormalX=0 NormalY=0 NormalZ=1 AngleXU=0 Radius=5
    g5: Circle CenterX=80.351 CenterY=-67.6202 CenterZ=0 NormalX=0 NormalY=0 NormalZ=1 AngleXU=0 Radius=5
    g6: Circle CenterX=23.851 CenterY=-4.92017 CenterZ=0 NormalX=0 NormalY=0 NormalZ=1 AngleXU=0 Radius=5
    g7: Circle CenterX=80.351 CenterY=-4.92017 CenterZ=0 NormalX=0 NormalY=0 NormalZ=1 AngleXU=0 Radius=5
  constraints (8):
    c: Block(g1)
    c: Block(g0)
    c: Block(g3)
    c: Block(g2)
    c: Block(g5)
    c: Block(g4)
    c: Block(g6)
    c: Block(g7)
FEATURE [Part::Extrusion] Extrude056
  Base = -> Sketch065
  Dir = (0,-1,2e-16)
  DirMode = 2
  FaceMakerClass = Part::FaceMakerBullseye
  LengthFwd = 2
  LengthRev = 0
  Solid = true
  Symmetric = false
FEATURE [Part::Extrusion] Extrude057  label="top025"
  Base = -> Sketch064
  Dir = (0,0,1)
  DirMode = 2
  FaceMakerClass = Part::FaceMakerBullseye
  LengthFwd = 72
  LengthRev = 0
  Solid = true
  Symmetric = false
FEATURE [Sketcher::SketchObject] Sketch066
  FullyConstrained = true
  MapMode = 3
  Placement = pos=(0,0,0) rot=(1,0,0;1.5708rad)
  Support = -> [Extrude057]
  sketch-geometry (8):
    g0: Circle CenterX=80.351 CenterY=-67.6202 CenterZ=0 NormalX=0 NormalY=0 NormalZ=1 AngleXU=0 Radius=3
    g1: Circle CenterX=80.351 CenterY=-4.92017 CenterZ=0 NormalX=0 NormalY=0 NormalZ=1 AngleXU=0 Radius=3
    g2: Circle CenterX=23.851 CenterY=-4.92017 CenterZ=0 NormalX=0 NormalY=0 NormalZ=1 AngleXU=0 Radius=3
    g3: Circle CenterX=23.851 CenterY=-67.6202 CenterZ=0 NormalX=0 NormalY=0 NormalZ=1 AngleXU=0 Radius=3
    g4: Circle CenterX=23.851 CenterY=-67.6202 CenterZ=0 NormalX=0 NormalY=0 NormalZ=1 AngleXU=0 Radius=5
    g5: Circle CenterX=80.351 CenterY=-67.6202 CenterZ=0 NormalX=0 NormalY=0 NormalZ=1 AngleXU=0 Radius=5
    g6: Circle CenterX=23.851 CenterY=-4.92017 CenterZ=0 NormalX=0 NormalY=0 NormalZ=1 AngleXU=0 Radius=5
    g7: Circle CenterX=80.351 CenterY=-4.92017 CenterZ=0 NormalX=0 NormalY=0 NormalZ=1 AngleXU=0 Radius=5
  constraints (8):
    c: Block(g1)
    c: Block(g0)
    c: Block(g3)
    c: Block(g2)
    c: Block(g5)
    c: Block(g4)
    c: Block(g6)
    c: Block(g7)
FEATURE [Part::Extrusion] Extrude055
  Base = -> Sketch066
  Dir = (0,-1,2e-16)
  DirMode = 2
  FaceMakerClass = Part::FaceMakerBullseye
  LengthFwd = 2
  LengthRev = 0
  Solid = true
  Symmetric = false
FEATURE [Part::Fillet] Fillet041
  Base = -> Extrude056
  Edges = 4 edges r=1.99: [Edge6,Edge12,Edge18,Edge24]
FEATURE [Part::Cut] Cut045
  Base = -> Extrude055
  Placement = pos=(0,6,0) rot=(0,0,1;0rad)
  Tool = -> Fillet041
FEATURE [Part::MultiFuse] Fusion095  label="pcbScrewPillars"
  Placement = pos=(-3.2,-1,72.3) rot=(0,0,1;0rad)
  Shapes = -> [Cut045,Extrude054]
FEATURE [Part::Feature] Face113
  shape: bbox 3.2 x 1.5 x 2e-07 mm, 1 faces, 0 solids (baked)
FEATURE [Part::Revolution] Revolve121  label="backCaseScrewRetainer002"
  Angle = 360
  Axis = (0,1,0)
  Base = (0,0,0)
  FaceMakerClass = Part::FaceMakerBullseye
  Placement = pos=(12.5,3,62) rot=(0,0,1;0rad)
  Solid = false
  Source = -> Face113
  Symmetric = false
FEATURE [Part::Feature] Face114
  shape: bbox 3.2 x 1.5 x 2e-07 mm, 1 faces, 0 solids (baked)
FEATURE [Part::Feature] Face115
  shape: bbox 3.2 x 1.5 x 2e-07 mm, 1 faces, 0 solids (baked)
FEATURE [Part::Feature] Face116
  shape: bbox 3.2 x 1.5 x 2e-07 mm, 1 faces, 0 solids (baked)
FEATURE [Part::Revolution] Revolve122  label="frontCaseScrewRetainer004"
  Angle = 360
  Axis = (0,1,0)
  Base = (0,0,0)
  FaceMakerClass = Part::FaceMakerBullseye
  Placement = pos=(89.5,3,68.5) rot=(0,0,1;0rad)
  Solid = false
  Source = -> Face115
  Symmetric = false
FEATURE [Part::Revolution] Revolve123  label="frontCaseScrewRetainer005"
  Angle = 360
  Axis = (0,1,0)
  Base = (0,0,0)
  FaceMakerClass = Part::FaceMakerBullseye
  Placement = pos=(89.5,3,3.5) rot=(0,0,1;0rad)
  Solid = false
  Source = -> Face116
  Symmetric = false
FEATURE [Part::Revolution] Revolve124  label="backCaseScrewRetainer003"
  Angle = 360
  Axis = (0,1,0)
  Base = (0,0,0)
  FaceMakerClass = Part::FaceMakerBullseye
  Placement = pos=(12.5,3,10) rot=(0,0,1;0rad)
  Solid = false
  Source = -> Face114
  Symmetric = false
FEATURE [Part::Feature] Face117
  shape: bbox 3.6 x 3.2 x 2e-07 mm, 1 faces, 0 solids (baked)
FEATURE [Part::Revolution] Revolve125  label="moreFrontCaseScrewRetainer004"
  Angle = 360
  Axis = (0,1,0)
  Base = (0,0,0)
  FaceMakerClass = Part::FaceMakerBullseye
  Placement = pos=(109.5,4.5,68.5) rot=(0,0,1;0rad)
  Solid = false
  Source = -> Face117
  Symmetric = false
FEATURE [Part::Feature] Face118
  shape: bbox 3.6 x 3.2 x 2e-07 mm, 1 faces, 0 solids (baked)
FEATURE [Part::Revolution] Revolve126  label="moreFrontCaseScrewRetainer005"
  Angle = 360
  Axis = (0,1,0)
  Base = (0,0,0)
  FaceMakerClass = Part::FaceMakerBullseye
  Placement = pos=(109.5,4.5,3.5) rot=(0,0,1;0rad)
  Solid = false
  Source = -> Face118
  Symmetric = false
FEATURE [Part::MultiFuse] Fusion096  label="screwRetainers001"
  Shapes = -> [Revolve126,Revolve125,Revolve124,Revolve123,Revolve122,Revolve121]
FEATURE [Part::Feature] Face119
  shape: bbox 10 x 16.5 x 2e-07 mm, 1 faces, 0 solids (baked)
FEATURE [Part::Revolution] Revolve130  label="plugHousing050"
  Angle = 360
  Axis = (0,1,0)
  Base = (0,0,0)
  FaceMakerClass = Part::FaceMakerBullseye
  Placement = pos=(0,0,36.15) rot=(0,0,1;0rad)
  Solid = false
  Source = -> Face119
  Symmetric = false
FEATURE [Part::Feature] Face120
  shape: bbox 10 x 16.5 x 2e-07 mm, 1 faces, 0 solids (baked)
FEATURE [Part::Feature] Face121
  shape: bbox 10 x 16.5 x 2e-07 mm, 1 faces, 0 solids (baked)
FEATURE [Part::Revolution] Revolve127  label="plugHousing047"
  Angle = 360
  Axis = (0,1,0)
  Base = (0,0,0)
  FaceMakerClass = Part::FaceMakerBullseye
  Placement = pos=(0,0,36.15) rot=(0,0,1;0rad)
  Solid = false
  Source = -> Face121
  Symmetric = false
FEATURE [Part::Feature] Face122
  shape: bbox 10 x 16.5 x 2e-07 mm, 1 faces, 0 solids (baked)
FEATURE [Part::Feature] Face123
  shape: bbox 10 x 16.5 x 2e-07 mm, 1 faces, 0 solids (baked)
FEATURE [Part::Revolution] Revolve128  label="plugHousing048"
  Angle = 360
  Axis = (0,1,0)
  Base = (0,0,0)
  FaceMakerClass = Part::FaceMakerBullseye
  Placement = pos=(0,0,36.15) rot=(0,0,1;0rad)
  Solid = false
  Source = -> Face123
  Symmetric = false
FEATURE [Part::MultiFuse] Fusion100  label="plugHousing054"
  Placement = pos=(0,0,0) rot=(0,0,1;1.5708rad)
  Shapes = -> [Revolve130,Revolve128]
FEATURE [Part::Feature] Face124
  shape: bbox 10 x 16.5 x 2e-07 mm, 1 faces, 0 solids (baked)
FEATURE [Part::Feature] Face125
  shape: bbox 10 x 16.5 x 2e-07 mm, 1 faces, 0 solids (baked)
FEATURE [Part::Revolution] Revolve129  label="plugHousing049"
  Angle = 360
  Axis = (0,1,0)
  Base = (0,0,0)
  FaceMakerClass = Part::FaceMakerBullseye
  Placement = pos=(0,0,36.15) rot=(0,0,1;0rad)
  Solid = false
  Source = -> Face125
  Symmetric = false
FEATURE [Part::Feature] Face126
  shape: bbox 10 x 16.5 x 2e-07 mm, 1 faces, 0 solids (baked)
FEATURE [Part::Revolution] Revolve131  label="plugHousing058"
  Angle = 360
  Axis = (0,1,0)
  Base = (0,0,0)
  FaceMakerClass = Part::FaceMakerBullseye
  Placement = pos=(0,0,36.15) rot=(0,0,1;0rad)
  Solid = false
  Source = -> Face120
  Symmetric = false
FEATURE [Part::MultiFuse] Fusion099  label="plugHousing053"
  Placement = pos=(0,0,0) rot=(0,0,1;1.5708rad)
  Shapes = -> [Revolve127,Revolve131]
FEATURE [Part::MultiFuse] Fusion102  label="plugHousing056"
  Placement = pos=(0,19,0) rot=(0,0,1;3.14159rad)
  Shapes = -> [Fusion100,Fusion099]
FEATURE [Part::Revolution] Revolve132  label="plugHousing059"
  Angle = 360
  Axis = (0,1,0)
  Base = (0,0,0)
  FaceMakerClass = Part::FaceMakerBullseye
  Placement = pos=(0,0,36.15) rot=(0,0,1;0rad)
  Solid = false
  Source = -> Face126
  Symmetric = false
FEATURE [Part::Revolution] Revolve133  label="plugHousing060"
  Angle = 360
  Axis = (0,1,0)
  Base = (0,0,0)
  FaceMakerClass = Part::FaceMakerBullseye
  Placement = pos=(0,0,36.15) rot=(0,0,1;0rad)
  Solid = false
  Source = -> Face122
  Symmetric = false
FEATURE [Part::MultiFuse] Fusion097  label="plugHousing051"
  Placement = pos=(0,0,0) rot=(0,0,1;1.5708rad)
  Shapes = -> [Revolve133,Revolve132]
FEATURE [Part::Revolution] Revolve134  label="plugHousing061"
  Angle = 360
  Axis = (0,1,0)
  Base = (0,0,0)
  FaceMakerClass = Part::FaceMakerBullseye
  Placement = pos=(0,0,36.15) rot=(0,0,1;0rad)
  Solid = false
  Source = -> Face124
  Symmetric = false
FEATURE [Part::MultiFuse] Fusion101  label="plugHousing055"
  Placement = pos=(0,0,0) rot=(0,0,1;1.5708rad)
  Shapes = -> [Revolve129,Revolve134]
FEATURE [Part::MultiFuse] Fusion098  label="plugHousing052"
  Placement = pos=(0,19,0) rot=(0,0,1;3.14159rad)
  Shapes = -> [Fusion097,Fusion101]
FEATURE [Part::MultiFuse] Fusion103  label="plugHousing057"
  Placement = pos=(122.621,0,-0.15) rot=(0,0,1;0rad)
  Shapes = -> [Fusion102,Fusion098]
FEATURE [Part::Box] Box028  label="Cube015"
  AttacherType = Attacher::AttachEngine3D
  Height = 28
  Length = 3
  Placement = pos=(110.7,19,22) rot=(0,0,1;0rad)
  Width = 15.7
FEATURE [Part::Cylinder] Cylinder044
  Angle = 360
  AttacherType = Attacher::AttachEngine3D
  Height = 20
  Placement = pos=(0,0,36.15) rot=(0,0,1;0rad)
  Radius = 10.3
FEATURE [Part::Cylinder] Cylinder045
  Angle = 360
  AttacherType = Attacher::AttachEngine3D
  Height = 10
  Placement = pos=(0,0,36.15) rot=(0,0,1;0rad)
  Radius = 4
FEATURE [Part::MultiFuse] Fusion104  label="removeToCreteHoleForPlugHousing040"
  Placement = pos=(70,19,36) rot=(0,1,0;1.5708rad)
  Shapes = -> [Cylinder044,Cylinder045]
FEATURE [Part::Cut] Cut046  label="plugHousingTab003"
  Base = -> Box028
  Tool = -> Fusion104
FEATURE [Part::MultiFuse] Fusion105  label="plugHousing062"
  Shapes = -> [Fusion103,Cut046]
FEATURE [Part::Fillet] Fillet042
  Base = -> Fusion105
  Edges = 1 edges r=2: [Edge25]
FEATURE [Part::Fillet] Fillet043  label="plugHousing063"
  Base = -> Fillet042
  Edges = 1 edges r=2: [Edge8]
  Placement = pos=(7,0,0) rot=(0,0,1;0rad)
FEATURE [Part::Feature] Face127
  shape: bbox 10 x 16.5 x 2e-07 mm, 1 faces, 0 solids (baked)
FEATURE [Part::Feature] Face128
  shape: bbox 10 x 16.5 x 2e-07 mm, 1 faces, 0 solids (baked)
FEATURE [Part::Revolution] Revolve137  label="plugHousing070"
  Angle = 360
  Axis = (0,1,0)
  Base = (0,0,0)
  FaceMakerClass = Part::FaceMakerBullseye
  Placement = pos=(0,0,36.15) rot=(0,0,1;0rad)
  Solid = false
  Source = -> Face127
  Symmetric = false
FEATURE [Part::Revolution] Revolve140  label="plugHousing073"
  Angle = 360
  Axis = (0,1,0)
  Base = (0,0,0)
  FaceMakerClass = Part::FaceMakerBullseye
  Placement = pos=(0,0,36.15) rot=(0,0,1;0rad)
  Solid = false
  Source = -> Face128
  Symmetric = false
FEATURE [Part::Feature] Face129
  shape: bbox 10 x 16.5 x 2e-07 mm, 1 faces, 0 solids (baked)
FEATURE [Part::Revolution] Revolve138  label="plugHousing071"
  Angle = 360
  Axis = (0,1,0)
  Base = (0,0,0)
  FaceMakerClass = Part::FaceMakerBullseye
  Placement = pos=(0,0,36.15) rot=(0,0,1;0rad)
  Solid = false
  Source = -> Face129
  Symmetric = false
FEATURE [Part::Feature] Face130
  shape: bbox 10 x 16.5 x 2e-07 mm, 1 faces, 0 solids (baked)
FEATURE [Part::Revolution] Revolve139  label="plugHousing072"
  Angle = 360
  Axis = (0,1,0)
  Base = (0,0,0)
  FaceMakerClass = Part::FaceMakerBullseye
  Placement = pos=(0,0,36.15) rot=(0,0,1;0rad)
  Solid = false
  Source = -> Face130
  Symmetric = false
FEATURE [Part::Feature] Face131
  shape: bbox 10 x 16.5 x 2e-07 mm, 1 faces, 0 solids (baked)
FEATURE [Part::Revolution] Revolve135  label="plugHousing068"
  Angle = 360
  Axis = (0,1,0)
  Base = (0,0,0)
  FaceMakerClass = Part::FaceMakerBullseye
  Placement = pos=(0,0,36.15) rot=(0,0,1;0rad)
  Solid = false
  Source = -> Face131
  Symmetric = false
FEATURE [Part::MultiFuse] Fusion112  label="plugHousing078"
  Placement = pos=(0,0,0) rot=(0,0,1;1.5708rad)
  Shapes = -> [Revolve135,Revolve139]
FEATURE [Part::Feature] Face132
  shape: bbox 10 x 16.5 x 2e-07 mm, 1 faces, 0 solids (baked)
FEATURE [Part::Revolution] Revolve141  label="plugHousing074"
  Angle = 360
  Axis = (0,1,0)
  Base = (0,0,0)
  FaceMakerClass = Part::FaceMakerBullseye
  Placement = pos=(0,0,36.15) rot=(0,0,1;0rad)
  Solid = false
  Source = -> Face132
  Symmetric = false
FEATURE [Part::MultiFuse] Fusion110  label="plugHousing076"
  Placement = pos=(0,0,0) rot=(0,0,1;1.5708rad)
  Shapes = -> [Revolve141,Revolve140]
FEATURE [Part::Feature] Face133
  shape: bbox 10 x 16.5 x 2e-07 mm, 1 faces, 0 solids (baked)
FEATURE [Part::Revolution] Revolve136  label="plugHousing069"
  Angle = 360
  Axis = (0,1,0)
  Base = (0,0,0)
  FaceMakerClass = Part::FaceMakerBullseye
  Placement = pos=(0,0,36.15) rot=(0,0,1;0rad)
  Solid = false
  Source = -> Face133
  Symmetric = false
FEATURE [Part::MultiFuse] Fusion106  label="plugHousing064"
  Placement = pos=(0,0,0) rot=(0,0,1;1.5708rad)
  Shapes = -> [Revolve138,Revolve136]
FEATURE [Part::MultiFuse] Fusion108  label="plugHousing066"
  Placement = pos=(0,19,0) rot=(0,0,1;3.14159rad)
  Shapes = -> [Fusion106,Fusion112]
FEATURE [Part::Feature] Face134
  shape: bbox 10 x 16.5 x 2e-07 mm, 1 faces, 0 solids (baked)
FEATURE [Part::Revolution] Revolve142  label="plugHousing075"
  Angle = 360
  Axis = (0,1,0)
  Base = (0,0,0)
  FaceMakerClass = Part::FaceMakerBullseye
  Placement = pos=(0,0,36.15) rot=(0,0,1;0rad)
  Solid = false
  Source = -> Face134
  Symmetric = false
FEATURE [Part::MultiFuse] Fusion107  label="plugHousing065"
  Placement = pos=(0,0,0) rot=(0,0,1;1.5708rad)
  Shapes = -> [Revolve137,Revolve142]
FEATURE [Part::MultiFuse] Fusion111  label="plugHousing077"
  Placement = pos=(0,19,0) rot=(0,0,1;3.14159rad)
  Shapes = -> [Fusion110,Fusion107]
FEATURE [Part::MultiFuse] Fusion109  label="plugHousing067"
  Placement = pos=(131.236,0,-0.15) rot=(0,0,1;0rad)
  Shapes = -> [Fusion108,Fusion111]
FEATURE [Part::MultiFuse] Fusion113  label="plugHousing079"
  Shapes = -> [Fillet043,Fusion109]
FEATURE [Part::Feature] Face135
  shape: bbox 3.5 x 17.8 x 2e-07 mm, 1 faces, 0 solids (baked)
FEATURE [Part::Revolution] Revolve143  label="removeToCreateScrewAndThreadedInsertHole049"
  Angle = 360
  Axis = (0,1,0)
  Base = (0,0,0)
  FaceMakerClass = Part::FaceMakerBullseye
  Placement = pos=(12.5,0,10) rot=(0,0,1;0rad)
  Solid = false
  Source = -> Face135
  Symmetric = false
FEATURE [Part::Feature] Face136
  shape: bbox 3.5 x 17.8 x 2e-07 mm, 1 faces, 0 solids (baked)
FEATURE [Part::Revolution] Revolve144  label="removeToCreateScrewAndThreadedInsertHole050"
  Angle = 360
  Axis = (0,1,0)
  Base = (0,0,0)
  FaceMakerClass = Part::FaceMakerBullseye
  Placement = pos=(12.5,0,62) rot=(0,0,1;0rad)
  Solid = false
  Source = -> Face136
  Symmetric = false
FEATURE [Part::Feature] Face137
  shape: bbox 3.5 x 17.8 x 2e-07 mm, 1 faces, 0 solids (baked)
FEATURE [Part::Revolution] Revolve145  label="removeToCreateScrewAndThreadedInsertHole051"
  Angle = 360
  Axis = (0,1,0)
  Base = (0,0,0)
  FaceMakerClass = Part::FaceMakerBullseye
  Placement = pos=(89.5,0,68.5) rot=(0,0,1;0rad)
  Solid = false
  Source = -> Face137
  Symmetric = false
FEATURE [Part::Feature] Face138
  shape: bbox 3.5 x 17.8 x 2e-07 mm, 1 faces, 0 solids (baked)
FEATURE [Part::Revolution] Revolve146  label="removeToCreateScrewAndThreadedInsertHole052"
  Angle = 360
  Axis = (0,1,0)
  Base = (0,0,0)
  FaceMakerClass = Part::FaceMakerBullseye
  Placement = pos=(89.5,0,3.5) rot=(0,0,1;0rad)
  Solid = false
  Source = -> Face138
  Symmetric = false
FEATURE [Part::Feature] Face139
  shape: bbox 3.5 x 17.8 x 2e-07 mm, 1 faces, 0 solids (baked)
FEATURE [Part::Revolution] Revolve147  label="removeToCreateScrewAndThreadedInsertHole053"
  Angle = 360
  Axis = (0,1,0)
  Base = (0,0,0)
  FaceMakerClass = Part::FaceMakerBullseye
  Placement = pos=(109.5,4.7,3.5) rot=(0,0,1;0rad)
  Solid = false
  Source = -> Face139
  Symmetric = false
FEATURE [Part::Feature] Face140
  shape: bbox 3.5 x 17.8 x 2e-07 mm, 1 faces, 0 solids (baked)
FEATURE [Part::Revolution] Revolve148  label="removeToCreateScrewAndThreadedInsertHole054"
  Angle = 360
  Axis = (0,1,0)
  Base = (0,0,0)
  FaceMakerClass = Part::FaceMakerBullseye
  Placement = pos=(109.5,4.7,68.5) rot=(0,0,1;0rad)
  Solid = false
  Source = -> Face140
  Symmetric = false
FEATURE [Part::MultiFuse] Fusion114  label="removeToCreateScrewAndThreadedInsertHole055"
  Shapes = -> [Revolve148,Revolve147,Revolve146,Revolve145,Revolve144,Revolve143]
FEATURE [Part::Cut] Cut047  label="casePillars004"
  Base = -> Cut037
  Tool = -> Fusion114
FEATURE [Part::Feature] Face141
  shape: bbox 3.5 x 17.8 x 2e-07 mm, 1 faces, 0 solids (baked)
FEATURE [Part::Feature] Face142
  shape: bbox 3.5 x 17.8 x 2e-07 mm, 1 faces, 0 solids (baked)
FEATURE [Part::Feature] Face143
  shape: bbox 3.5 x 17.8 x 2e-07 mm, 1 faces, 0 solids (baked)
FEATURE [Part::Revolution] Revolve149  label="removeToCreateScrewAndThreadedInsertHole057"
  Angle = 360
  Axis = (0,1,0)
  Base = (0,0,0)
  FaceMakerClass = Part::FaceMakerBullseye
  Placement = pos=(12.5,0,10) rot=(0,0,1;0rad)
  Solid = false
  Source = -> Face141
  Symmetric = false
FEATURE [Part::Feature] Face144
  shape: bbox 3.5 x 17.8 x 2e-07 mm, 1 faces, 0 solids (baked)
FEATURE [Part::Feature] Face145
  shape: bbox 3.5 x 17.8 x 2e-07 mm, 1 faces, 0 solids (baked)
FEATURE [Part::Feature] Face146
  shape: bbox 3.5 x 17.8 x 2e-07 mm, 1 faces, 0 solids (baked)
FEATURE [Part::Revolution] Revolve150  label="removeToCreateScrewAndThreadedInsertHole058"
  Angle = 360
  Axis = (0,1,0)
  Base = (0,0,0)
  FaceMakerClass = Part::FaceMakerBullseye
  Placement = pos=(12.5,0,62) rot=(0,0,1;0rad)
  Solid = false
  Source = -> Face146
  Symmetric = false
FEATURE [Part::Revolution] Revolve151  label="removeToCreateScrewAndThreadedInsertHole059"
  Angle = 360
  Axis = (0,1,0)
  Base = (0,0,0)
  FaceMakerClass = Part::FaceMakerBullseye
  Placement = pos=(89.5,0,68.5) rot=(0,0,1;0rad)
  Solid = false
  Source = -> Face143
  Symmetric = false
FEATURE [Part::Revolution] Revolve152  label="removeToCreateScrewAndThreadedInsertHole060"
  Angle = 360
  Axis = (0,1,0)
  Base = (0,0,0)
  FaceMakerClass = Part::FaceMakerBullseye
  Placement = pos=(89.5,0,3.5) rot=(0,0,1;0rad)
  Solid = false
  Source = -> Face142
  Symmetric = false
FEATURE [Part::Revolution] Revolve153  label="removeToCreateScrewAndThreadedInsertHole061"
  Angle = 360
  Axis = (0,1,0)
  Base = (0,0,0)
  FaceMakerClass = Part::FaceMakerBullseye
  Placement = pos=(109.5,4.7,3.5) rot=(0,0,1;0rad)
  Solid = false
  Source = -> Face145
  Symmetric = false
FEATURE [Part::Revolution] Revolve154  label="removeToCreateScrewAndThreadedInsertHole062"
  Angle = 360
  Axis = (0,1,0)
  Base = (0,0,0)
  FaceMakerClass = Part::FaceMakerBullseye
  Placement = pos=(109.5,4.7,68.5) rot=(0,0,1;0rad)
  Solid = false
  Source = -> Face144
  Symmetric = false
FEATURE [Part::MultiFuse] Fusion115  label="removeToCreateScrewAndThreadedInsertHole056"
  Shapes = -> [Revolve154,Revolve153,Revolve152,Revolve151,Revolve150,Revolve149]
FEATURE [Part::Feature] Face147
  shape: bbox 9.8 x 26.5 x 2e-07 mm, 1 faces, 0 solids (baked)
FEATURE [Part::Revolution] Revolve155
  Angle = 360
  Axis = (0,1,0)
  Base = (0,0,0)
  FaceMakerClass = Part::FaceMakerBullseye
  Placement = pos=(0,0,0) rot=(0,0,1;1.5708rad)
  Solid = false
  Source = -> Face147
  Symmetric = false
FEATURE [Part::Feature] Face148
  shape: bbox 9.8 x 26.5 x 2e-07 mm, 1 faces, 0 solids (baked)
FEATURE [Part::Revolution] Revolve156
  Angle = 360
  Axis = (0,1,0)
  Base = (0,0,0)
  FaceMakerClass = Part::FaceMakerBullseye
  Placement = pos=(0,0,0) rot=(0,0,1;1.5708rad)
  Solid = false
  Source = -> Face148
  Symmetric = false
FEATURE [Part::MultiFuse] Fusion116
  Placement = pos=(-18,19,36) rot=(0,0,1;0rad)
  Shapes = -> [Revolve156,Revolve155]
FEATURE [Part::Box] Box029  label="Cube016"
  AttacherType = Attacher::AttachEngine3D
  Height = 28
  Length = 3
  Placement = pos=(110.7,19,22) rot=(0,0,1;0rad)
  Width = 15.7
FEATURE [Part::Cylinder] Cylinder046
  Angle = 360
  AttacherType = Attacher::AttachEngine3D
  Height = 10
  Placement = pos=(0,0,36.15) rot=(0,0,1;0rad)
  Radius = 4
FEATURE [Part::Cylinder] Cylinder047
  Angle = 360
  AttacherType = Attacher::AttachEngine3D
  Height = 20
  Placement = pos=(0,0,36.15) rot=(0,0,1;0rad)
  Radius = 10.3
FEATURE [Part::MultiFuse] Fusion117  label="removeToCreteHoleForPlugHousing041"
  Placement = pos=(70,19,36) rot=(0,1,0;1.5708rad)
  Shapes = -> [Cylinder047,Cylinder046]
FEATURE [Part::Cut] Cut049  label="plugHousingTab004"
  Base = -> Box029
  Placement = pos=(-107.4,-14,0) rot=(0,0,1;0rad)
  Tool = -> Fusion117
FEATURE [Part::Box] Box030  label="Cube017"
  AttacherType = Attacher::AttachEngine3D
  Height = 28
  Length = 3
  Placement = pos=(110.7,19,22) rot=(0,0,1;0rad)
  Width = 15.7
FEATURE [Part::Cylinder] Cylinder048
  Angle = 360
  AttacherType = Attacher::AttachEngine3D
  Height = 10
  Placement = pos=(0,0,36.15) rot=(0,0,1;0rad)
  Radius = 4
FEATURE [Part::Cylinder] Cylinder049
  Angle = 360
  AttacherType = Attacher::AttachEngine3D
  Height = 20
  Placement = pos=(0,0,36.15) rot=(0,0,1;0rad)
  Radius = 10.3
FEATURE [Part::MultiFuse] Fusion118  label="removeToCreteHoleForPlugHousing042"
  Placement = pos=(70,19,36) rot=(0,1,0;1.5708rad)
  Shapes = -> [Cylinder049,Cylinder048]
FEATURE [Part::Cut] Cut050  label="plugHousingTab005"
  Base = -> Box030
  Placement = pos=(-107.4,-14,0) rot=(0,0,1;0rad)
  Tool = -> Fusion118
FEATURE [Part::MultiFuse] Fusion119
  Placement = pos=(9.6,23,0) rot=(0,0,1;3.14159rad)
  Shapes = -> [Cut049,Cut050]
FEATURE [Part::Box] Box031  label="Cube018"
  AttacherType = Attacher::AttachEngine3D
  Height = 10
  Length = 3
  Placement = pos=(3.3,4,12) rot=(0,0,1;0rad)
  Width = 10
FEATURE [Part::Fillet] Fillet044
  Base = -> Box031
  Edges = 1 edges r=2: [Edge11]
FEATURE [Part::Box] Box032  label="Cube019"
  AttacherType = Attacher::AttachEngine3D
  Height = 10
  Length = 3
  Placement = pos=(3.3,4,50) rot=(0,0,1;0rad)
  Width = 10
FEATURE [Part::Fillet] Fillet045
  Base = -> Box032
  Edges = 1 edges r=2: [Edge12]
FEATURE [Part::Box] Box033  label="Cube020"
  AttacherType = Attacher::AttachEngine3D
  Height = 28
  Length = 4
  Placement = pos=(5,0,22) rot=(0,0,1;0rad)
  Width = 10
FEATURE [Part::Fillet] Fillet046
  Base = -> Box033
  Edges = 1 edges r=1: [Edge7]
FEATURE [Part::Fillet] Fillet047
  Base = -> Fillet046
  Edges = 1 edges r=2: [Edge5]
FEATURE [Part::Fillet] Fillet048
  Base = -> Fillet047
  Edges = 1 edges r=2: [Edge2]
FEATURE [Part::Cylinder] Cylinder050
  Angle = 360
  AttacherType = Attacher::AttachEngine3D
  Height = 20
  Placement = pos=(0,0,36.15) rot=(0,0,1;0rad)
  Radius = 8.2
FEATURE [Part::Cylinder] Cylinder051
  Angle = 360
  AttacherType = Attacher::AttachEngine3D
  Height = 10
  Placement = pos=(0,0,36.15) rot=(0,0,1;0rad)
  Radius = 4
FEATURE [Part::MultiFuse] Fusion120  label="removeToCreteHoleForPlugHousing043"
  Placement = pos=(-42,19,36) rot=(0,1,0;1.5708rad)
  Shapes = -> [Cylinder050,Cylinder051]
FEATURE [Sketcher::SketchObject] Sketch067  label="topSketch018"
  FullyConstrained = true
  sketch-geometry (4):
    g0: LineSegment StartX=16.8446 StartY=31.512 StartZ=0 EndX=16.3251 EndY=34.4666 EndZ=0
    g1: ArcOfCircle CenterX=19 CenterY=19.2524 CenterZ=0 NormalX=0 NormalY=0 NormalZ=1 AngleXU=0 Radius=15.4476 StartAngle=1.74483 EndAngle=2.72717
    g2: ArcOfCircle CenterX=19 CenterY=19.2524 CenterZ=0 NormalX=0 NormalY=0 NormalZ=1 AngleXU=0 Radius=12.4476 StartAngle=1.74483 EndAngle=2.73189
    g3: LineSegment StartX=4.86004 StartY=25.4725 StartZ=0 EndX=7.58253 EndY=24.2107 EndZ=0
  constraints (7):
    c: Block(g0)
    c: Coincident(g1,g0)
    c: Coincident(g2,g0)
    c: Coincident(g3,g1)
    c: Coincident(g3,g2)
    c: Block(g1)
    c: Block(g2)
FEATURE [Part::Extrusion] Extrude058
  Base = -> Sketch067
  Dir = (0,0,1)
  DirMode = 2
  FaceMakerClass = Part::FaceMakerBullseye
  LengthFwd = 10
  LengthRev = 0
  Placement = pos=(0,0,31) rot=(0,0,1;0rad)
  Solid = true
  Symmetric = false
FEATURE [Part::Cut] Cut051
  Base = -> Extrude058
  Tool = -> Fusion120
FEATURE [Part::Fillet] Fillet049
  Base = -> Cut051
  Edges = 1 edges r=2: [Edge1]
FEATURE [Part::Fillet] Fillet050
  Base = -> Fillet049
  Edges = 1 edges r=2.5: [Edge1]
FEATURE [Part::Fillet] Fillet051
  Base = -> Fillet050
  Edges = 1 edges r=2.5: [Edge2]
FEATURE [Part::MultiFuse] Fusion121  label="wireHolder003"
  Shapes = -> [Fusion116,Fillet051]
FEATURE [Part::MultiFuse] Fusion122
  Shapes = -> [Fillet045,Fusion121]
FEATURE [Part::MultiFuse] Fusion123  label="wireHolder004"
  Shapes = -> [Fusion122,Fillet048]
FEATURE [Part::MultiFuse] Fusion124  label="wireHolder005"
  Shapes = -> [Fillet044,Fusion119,Fusion123]
FEATURE [Sketcher::SketchObject] Sketch068  label="topSketch019"
  FullyConstrained = true
  sketch-geometry (6):
    g0: LineSegment StartX=19 StartY=38 StartZ=0 EndX=117 EndY=38 EndZ=0
    g1: ArcOfCircle CenterX=19 CenterY=19 CenterZ=0 NormalX=0 NormalY=0 NormalZ=1 AngleXU=0 Radius=19 StartAngle=1.5708 EndAngle=3.14159
    g2: LineSegment StartX=117 StartY=38 StartZ=0 EndX=117 EndY=19 EndZ=0
    g3: LineSegment StartX=98 StartY=1.0161e-12 StartZ=0 EndX=5.22862e-06 EndY=1.0161e-12 EndZ=0
    g4: LineSegment StartX=5.22862e-06 StartY=19 StartZ=0 EndX=5.22862e-06 EndY=1.0161e-12 EndZ=0
    g5: ArcOfCircle CenterX=98 CenterY=19 CenterZ=0 NormalX=0 NormalY=0 NormalZ=1 AngleXU=0 Radius=19 StartAngle=4.71239 EndAngle=6.28319
  constraints (16):
    c: Horizontal(g0)
    c: Distance(g0) = 98
    c: Coincident(g1,g0)
    c: Block(g1)
    c: Coincident(g2,g0)
    c: Vertical(g2)
    c: Distance(g2) = 19
    c: Horizontal(g3)
    c: Coincident(g4,g1)
    c: Vertical(g4)
    c: Coincident(g3,g4)
    c: Block(g3)
    c: Coincident(g5,g2)
    c: Coincident(g5,g3)
    c: Block(g0)
    c: Block(g5)
FEATURE [Part::Extrusion] Extrude059  label="sideA002"
  Base = -> Sketch068
  Dir = (0,0,1)
  DirMode = 2
  FaceMakerClass = Part::FaceMakerBullseye
  LengthFwd = 3
  LengthRev = 0
  Placement = pos=(0,0,-2.7) rot=(0,0,1;0rad)
  Solid = true
  Symmetric = false
FEATURE [Sketcher::SketchObject] Sketch069  label="topSketch020"
  FullyConstrained = true
  sketch-geometry (6):
    g0: LineSegment StartX=19 StartY=38 StartZ=0 EndX=117 EndY=38 EndZ=0
    g1: ArcOfCircle CenterX=19 CenterY=19 CenterZ=0 NormalX=0 NormalY=0 NormalZ=1 AngleXU=0 Radius=19 StartAngle=1.5708 EndAngle=3.14159
    g2: LineSegment StartX=117 StartY=38 StartZ=0 EndX=117 EndY=19 EndZ=0
    g3: LineSegment StartX=98 StartY=1.0161e-12 StartZ=0 EndX=5.22862e-06 EndY=1.0161e-12 EndZ=0
    g4: LineSegment StartX=5.22862e-06 StartY=19 StartZ=0 EndX=5.22862e-06 EndY=1.0161e-12 EndZ=0
    g5: ArcOfCircle CenterX=98 CenterY=19 CenterZ=0 NormalX=0 NormalY=0 NormalZ=1 AngleXU=0 Radius=19 StartAngle=4.71239 EndAngle=6.28319
  constraints (16):
    c: Horizontal(g0)
    c: Distance(g0) = 98
    c: Coincident(g1,g0)
    c: Block(g1)
    c: Coincident(g2,g0)
    c: Vertical(g2)
    c: Distance(g2) = 19
    c: Horizontal(g3)
    c: Coincident(g4,g1)
    c: Vertical(g4)
    c: Coincident(g3,g4)
    c: Block(g3)
    c: Coincident(g5,g2)
    c: Coincident(g5,g3)
    c: Block(g0)
    c: Block(g5)
FEATURE [Part::Extrusion] Extrude060  label="sideB002"
  Base = -> Sketch069
  Dir = (0,0,1)
  DirMode = 2
  FaceMakerClass = Part::FaceMakerBullseye
  LengthFwd = 3
  LengthRev = 0
  Placement = pos=(0,0,71.7) rot=(0,0,1;0rad)
  Solid = true
  Symmetric = false
FEATURE [Part::MultiFuse] Fusion127  label="removeFromBottom001"
  Placement = pos=(2,0,0) rot=(0,0,1;0rad)
  Shapes = -> [Extrude059,Extrude060]
FEATURE [Part::Cylinder] Cylinder052
  Angle = 360
  AttacherType = Attacher::AttachEngine3D
  Height = 20
  Placement = pos=(0,0,36.15) rot=(0,0,1;0rad)
  Radius = 14
FEATURE [Part::Cylinder] Cylinder053
  Angle = 360
  AttacherType = Attacher::AttachEngine3D
  Height = 10
  Placement = pos=(0,0,36.15) rot=(0,0,1;0rad)
  Radius = 4
FEATURE [Part::MultiFuse] Fusion128  label="removeToCreteHoleForPlugHousing044"
  Placement = pos=(70,19,36) rot=(0,1,0;1.5708rad)
  Shapes = -> [Cylinder052,Cylinder053]
FEATURE [Part::Cut] Cut052  label="bottom011"
  Base = -> Extrude043
  Tool = -> Fusion128
FEATURE [Part::Cut] Cut054  label="bottom012"
  Base = -> Cut052
  Tool = -> Fusion115
FEATURE [Sketcher::SketchObject] Sketch070
  FullyConstrained = true
  Placement = pos=(117,19,0) rot=(0.57735,0.57735,0.57735;2.0944rad)
  sketch-geometry (48):
    g0: LineSegment StartX=-49.19 StartY=69.25 StartZ=0 EndX=-49.19 EndY=66.25 EndZ=0
    g1: LineSegment StartX=-49.19 StartY=63.5 StartZ=0 EndX=-49.19 EndY=60.5 EndZ=0
    g2: LineSegment StartX=-49.19 StartY=57.75 StartZ=0 EndX=-49.19 EndY=54.75 EndZ=0
    g3: LineSegment StartX=-49.19 StartY=52 StartZ=0 EndX=-49.19 EndY=49 EndZ=0
    g4: LineSegment StartX=-49.19 StartY=46.25 StartZ=0 EndX=-49.19 EndY=43.25 EndZ=0
    g5: LineSegment StartX=-49.19 StartY=40.5 StartZ=0 EndX=-49.19 EndY=37.5 EndZ=0
    g6: LineSegment StartX=-49.19 StartY=34.5 StartZ=0 EndX=-49.19 EndY=31.5 EndZ=0
    g7: LineSegment StartX=-49.19 StartY=28.75 StartZ=0 EndX=-49.19 EndY=25.75 EndZ=0
    g8: LineSegment StartX=-49.19 StartY=23 StartZ=0 EndX=-49.19 EndY=20 EndZ=0
    g9: LineSegment StartX=-49.19 StartY=17.25 StartZ=0 EndX=-49.19 EndY=14.25 EndZ=0
    g10: LineSegment StartX=-49.19 StartY=11.5 StartZ=0 EndX=-49.19 EndY=8.5 EndZ=0
    g11: LineSegment StartX=-49.19 StartY=5.75 StartZ=0 EndX=-49.19 EndY=2.75 EndZ=0
    g12: ArcOfCircle CenterX=-1.5 CenterY=67.75 CenterZ=0 NormalX=0 NormalY=0 NormalZ=1 AngleXU=0 Radius=1.5 StartAngle=4.71239 EndAngle=7.85398
    g13: ArcOfCircle CenterX=-1.5 CenterY=62 CenterZ=0 NormalX=0 NormalY=0 NormalZ=1 AngleXU=0 Radius=1.5 StartAngle=4.71239 EndAngle=7.85398
    g14: ArcOfCircle CenterX=-1.5 CenterY=56.25 CenterZ=0 NormalX=0 NormalY=0 NormalZ=1 AngleXU=0 Radius=1.5 StartAngle=4.71239 EndAngle=7.85398
    g15: ArcOfCircle CenterX=-11.49 CenterY=50.5 CenterZ=0 NormalX=0 NormalY=0 NormalZ=1 AngleXU=0 Radius=1.5 StartAngle=4.71239 EndAngle=7.85398
    g16: ArcOfCircle CenterX=-16.28 CenterY=44.75 CenterZ=0 NormalX=0 NormalY=0 NormalZ=1 AngleXU=0 Radius=1.5 StartAngle=4.71239 EndAngle=7.85398
    g17: ArcOfCircle CenterX=-18.2337 CenterY=39 CenterZ=0 NormalX=0 NormalY=0 NormalZ=1 AngleXU=0 Radius=1.5 StartAngle=4.71485 EndAngle=7.85398
    g18: ArcOfCircle CenterX=-16.2837 CenterY=27.25 CenterZ=0 NormalX=0 NormalY=0 NormalZ=1 AngleXU=0 Radius=1.5 StartAngle=4.71485 EndAngle=7.85398
    g19: ArcOfCircle CenterX=-18.2337 CenterY=33 CenterZ=0 NormalX=0 NormalY=0 NormalZ=1 AngleXU=0 Radius=1.5 StartAngle=4.71485 EndAngle=7.85398
    g20: ArcOfCircle CenterX=-11.49 CenterY=21.5 CenterZ=0 NormalX=0 NormalY=0 NormalZ=1 AngleXU=0 Radius=1.5 StartAngle=4.71239 EndAngle=7.85398
    g21: ArcOfCircle CenterX=-1.5 CenterY=4.25 CenterZ=0 NormalX=0 NormalY=0 NormalZ=1 AngleXU=0 Radius=1.5 StartAngle=4.71239 EndAngle=7.85398
    g22: ArcOfCircle CenterX=-1.5 CenterY=10 CenterZ=0 NormalX=0 NormalY=0 NormalZ=1 AngleXU=0 Radius=1.5 StartAngle=4.71239 EndAngle=7.85398
    g23: ArcOfCircle CenterX=-1.5 CenterY=15.75 CenterZ=0 NormalX=0 NormalY=0 NormalZ=1 AngleXU=0 Radius=1.5 StartAngle=4.71239 EndAngle=7.85398
    g24: LineSegment StartX=-49.19 StartY=69.25 StartZ=0 EndX=-1.5 EndY=69.25 EndZ=0
    g25: LineSegment StartX=-49.19 StartY=66.25 StartZ=0 EndX=-1.5 EndY=66.25 EndZ=0
    g26: LineSegment StartX=-49.19 StartY=63.5 StartZ=0 EndX=-1.5 EndY=63.5 EndZ=0
    g27: LineSegment StartX=-49.19 StartY=60.5 StartZ=0 EndX=-1.5 EndY=60.5 EndZ=0
    g28: LineSegment StartX=-49.19 StartY=57.75 StartZ=0 EndX=-1.5 EndY=57.75 EndZ=0
    g29: LineSegment StartX=-49.19 StartY=54.75 StartZ=0 EndX=-1.5 EndY=54.75 EndZ=0
    g30: LineSegment StartX=-49.19 StartY=52 StartZ=0 EndX=-11.49 EndY=52 EndZ=0
    g31: LineSegment StartX=-49.19 StartY=49 StartZ=0 EndX=-11.49 EndY=49 EndZ=0
    g32: LineSegment StartX=-49.19 StartY=46.25 StartZ=0 EndX=-16.28 EndY=46.25 EndZ=0
    g33: LineSegment StartX=-49.19 StartY=43.25 StartZ=0 EndX=-16.28 EndY=43.25 EndZ=0
    g34: LineSegment StartX=-49.19 StartY=40.5 StartZ=0 EndX=-18.2337 EndY=40.5 EndZ=0
    g35: LineSegment StartX=-49.19 StartY=37.5 StartZ=0 EndX=-18.23 EndY=37.5 EndZ=0
    g36: LineSegment StartX=-49.19 StartY=34.5 StartZ=0 EndX=-18.2337 EndY=34.5 EndZ=0
    g37: LineSegment StartX=-49.19 StartY=31.5 StartZ=0 EndX=-18.23 EndY=31.5 EndZ=0
    g38: LineSegment StartX=-49.19 StartY=28.75 StartZ=0 EndX=-16.2837 EndY=28.75 EndZ=0
    g39: LineSegment StartX=-49.19 StartY=25.75 StartZ=0 EndX=-16.28 EndY=25.75 EndZ=0
    g40: LineSegment StartX=-49.19 StartY=23 StartZ=0 EndX=-11.49 EndY=23 EndZ=0
    g41: LineSegment StartX=-49.19 StartY=20 StartZ=0 EndX=-11.49 EndY=20 EndZ=0
    g42: LineSegment StartX=-49.19 StartY=17.25 StartZ=0 EndX=-1.5 EndY=17.25 EndZ=0
    g43: LineSegment StartX=-49.19 StartY=14.25 StartZ=0 EndX=-1.5 EndY=14.25 EndZ=0
    g44: LineSegment StartX=-49.19 StartY=11.5 StartZ=0 EndX=-1.5 EndY=11.5 EndZ=0
    g45: LineSegment StartX=-49.19 StartY=8.5 StartZ=0 EndX=-1.5 EndY=8.5 EndZ=0
    g46: LineSegment StartX=-49.19 StartY=5.75 StartZ=0 EndX=-1.5 EndY=5.75 EndZ=0
    g47: LineSegment StartX=-49.19 StartY=2.75 StartZ=0 EndX=-1.5 EndY=2.75 EndZ=0
  constraints (120):
    c: Vertical(g0)
    c: Distance(g0) = 3
    c: Block(g0)
    c: Vertical(g1)
    c: Distance(g1) = 3
    c: Vertical(g2)
    c: Equal(g0,g2) = 3
    c: Block(g2)
    c: Vertical(g3)
    c: Equal(g1,g3) = 3
    c: Vertical(g4)
    c: Equal(g0,g4) = 3
    c: Block(g4)
    c: Vertical(g5)
    c: Equal(g1,g5) = 3
    c: Vertical(g6)
    c: Equal(g0,g6) = 3
    c: Block(g6)
    c: Vertical(g7)
    c: Equal(g1,g7) = 3
    c: Vertical(g8)
    c: Equal(g0,g8) = 3
    c: Block(g8)
    c: Vertical(g9)
    c: Equal(g1,g9) = 3
    c: Vertical(g10)
    c: Equal(g0,g10) = 3
    c: Block(g10)
    c: Vertical(g11)
    c: Equal(g1,g11) = 3
    c: Block(g12)
    c: Block(g13)
    c: Block(g14)
    c: Block(g15)
    c: Block(g16)
    c: Block(g17)
    c: Block(g18)
    c: Block(g19)
    c: Block(g20)
    c: Block(g21)
    c: Block(g22)
    c: Block(g23)
    c: Block(g11)
    c: Block(g9)
    c: Block(g7)
    c: Block(g5)
    c: Block(g3)
    c: Block(g1)
    c: Coincident(g24,g0)
    c: Coincident(g24,g12)
    c: Horizontal(g24)
    c: Coincident(g25,g0)
    c: Coincident(g25,g12)
    c: Horizontal(g25)
    c: Coincident(g26,g1)
    c: Coincident(g26,g13)
    c: Horizontal(g26)
    c: Coincident(g27,g1)
    c: Coincident(g27,g13)
    c: Horizontal(g27)
    c: Coincident(g28,g2)
    c: Coincident(g28,g14)
    c: Horizontal(g28)
    c: Coincident(g29,g2)
    c: Coincident(g29,g14)
    c: Horizontal(g29)
    c: Coincident(g30,g3)
    c: Coincident(g30,g15)
    c: Horizontal(g30)
    c: Coincident(g31,g3)
    c: Coincident(g31,g15)
    c: Horizontal(g31)
    c: Coincident(g32,g4)
    c: Coincident(g32,g16)
    c: Horizontal(g32)
    c: Coincident(g33,g4)
    c: Coincident(g33,g16)
    c: Horizontal(g33)
    c: Coincident(g34,g5)
    c: Coincident(g34,g17)
    c: Horizontal(g34)
    c: Coincident(g35,g5)
    c: Coincident(g35,g17)
    c: Horizontal(g35)
    c: Coincident(g36,g6)
    c: Coincident(g36,g19)
    c: Horizontal(g36)
    c: Coincident(g37,g6)
    c: Coincident(g37,g19)
    c: Horizontal(g37)
    c: Coincident(g38,g7)
    c: Coincident(g38,g18)
    c: Horizontal(g38)
    c: Coincident(g39,g7)
    c: Coincident(g39,g18)
    c: Horizontal(g39)
    c: Coincident(g40,g8)
    c: Coincident(g40,g20)
    c: Horizontal(g40)
    c: Coincident(g41,g8)
    c: Coincident(g41,g20)
    c: Horizontal(g41)
    c: Coincident(g42,g9)
    c: Coincident(g42,g23)
    c: Horizontal(g42)
    c: Coincident(g43,g9)
    c: Coincident(g43,g23)
    c: Horizontal(g43)
    c: Coincident(g44,g10)
    c: Coincident(g44,g22)
    c: Horizontal(g44)
    c: Coincident(g45,g10)
    c: Coincident(g45,g22)
    c: Horizontal(g45)
    c: Coincident(g46,g11)
    c: Coincident(g46,g21)
    c: Horizontal(g46)
    c: Coincident(g47,g11)
    c: Coincident(g47,g21)
    c: Horizontal(g47)
FEATURE [Part::Extrusion] Extrude061
  Base = -> Sketch070
  Dir = (1,0,0)
  DirMode = 2
  FaceMakerClass = Part::FaceMakerBullseye
  LengthFwd = 23
  LengthRev = 0
  Placement = pos=(-19,0,0) rot=(0,0,1;0rad)
  Solid = true
  Symmetric = false
FEATURE [Part::Fillet] Fillet052  label="removeToCreateVentalationHoles002"
  Base = -> Extrude061
  Edges = <same value as first occurrence — deduplicated (x6 in doc)>
  Placement = pos=(7,0.02,0) rot=(0,0,1;0rad)
FEATURE [Part::MultiFuse] Fusion130  label="bottom013"
  Shapes = -> [Cut054,Cut034]
FEATURE [Part::Cut] Cut055
  Base = -> Fusion130
  Tool = -> Fillet052
FEATURE [Part::Cylinder] Cylinder054
  Angle = 360
  AttacherType = Attacher::AttachEngine3D
  Height = 20
  Placement = pos=(0,0,36.15) rot=(0,0,1;0rad)
  Radius = 4
FEATURE [Sketcher::SketchObject] Sketch071  label="bottomSketch002"
  FullyConstrained = true
  sketch-geometry (32):
    g0: LineSegment StartX=3.3 StartY=-6.03275e-07 StartZ=0 EndX=98 EndY=-6.03275e-07 EndZ=0
    g1: ArcOfCircle CenterX=98 CenterY=19 CenterZ=0 NormalX=0 NormalY=0 NormalZ=1 AngleXU=0 Radius=19 StartAngle=4.71239 EndAngle=5.71103
    g2: LineSegment StartX=6.3 StartY=8 StartZ=0 EndX=3.3 EndY=8 EndZ=0
    g3: LineSegment StartX=3.3 StartY=8 StartZ=0 EndX=3.3 EndY=-6.03275e-07 EndZ=0
    g4: ArcOfCircle CenterX=8.3 CenterY=5 CenterZ=0 NormalX=0 NormalY=0 NormalZ=1 AngleXU=0 Radius=2 StartAngle=3.14159 EndAngle=4.71239
    g5: LineSegment StartX=6.3 StartY=8 StartZ=0 EndX=6.3 EndY=5 EndZ=0
    g6: ArcOfCircle CenterX=98 CenterY=19 CenterZ=0 NormalX=0 NormalY=0 NormalZ=1 AngleXU=0 Radius=12.7 StartAngle=4.71239 EndAngle=6.28319
    g7: LineSegment StartX=94.7 StartY=3 StartZ=0 EndX=8.3 EndY=3 EndZ=0
    g8-g12: Circle x5 (B-spline internal-alignment scaffolding for g13; pole/knot coordinates omitted)
    g13: BSplineCurve PolesCount=5 KnotsCount=3 Degree=3 IsPeriodic=0
    g14: GeomPoint X=98 Y=6.3 Z=0
    g15: GeomPoint X=96.3938 Y=4.71946 Z=0
    g16: GeomPoint X=94.7 Y=3 Z=0
    g17-g23: Circle x7 (B-spline internal-alignment scaffolding for g24; pole/knot coordinates omitted)
    g24: BSplineCurve PolesCount=7 KnotsCount=5 Degree=3 IsPeriodic=0
    g25-g29: GeomPoint x5 (B-spline internal-alignment scaffolding for g24; pole/knot coordinates omitted)
    g30: ArcOfCircle CenterX=98 CenterY=19 CenterZ=0 NormalX=0 NormalY=0 NormalZ=1 AngleXU=0 Radius=15.7 StartAngle=5.81226 EndAngle=6.28319
    g31: LineSegment StartX=110.7 StartY=19 StartZ=0 EndX=113.7 EndY=19 EndZ=0
  constraints (41):
    c: Horizontal(g0)
    c: Coincident(g1,g0)
    c: Block(g1)
    c: Horizontal(g2)
    c: Distance(g2) = 3
    c: Coincident(g3,g2)
    c: Vertical(g3)
    c: Coincident(g3,g0)
    c: Block(g4)
    c: Block(g2)
    c: Coincident(g5,g2)
    c: Coincident(g5,g4)
    c: Vertical(g5)
    c: Coincident(g6,g1)
    c: Block(g6)
    c: Coincident(g7,g4)
    c: Horizontal(g7)
    c: Block(g0)
    c: Block(g7)
    c: Block(g3)
    c: Coincident(g13,g6)
    c: Weight(g8) = 1
    c: Equal(g8, g9-g12) x4
    c: Coincident(g13,g7)
    c: InternalAlignment(g8-g12 -> g13) x5
    c: InternalAlignment(g14,g13)
    c: InternalAlignment(g15,g13)
    c: InternalAlignment(g16,g13)
    c: Block(g13)
    c: Weight(g17) = 1
    c: Equal(g17, g18-g23) x6
    c: Coincident(g24,g1)
    c: InternalAlignment(g17-g23 -> g24) x7
    c: InternalAlignment(g25-g29 -> g24) x5
    c: Block(g24)
    c: Coincident(g30,g24)
    c: Coincident(g31,g6)
    c: Coincident(g31,g30)
    c: Horizontal(g31)
    c: Block(g31)
    c: Block(g30)
FEATURE [Part::Extrusion] Extrude062  label="bottom014"
  Base = -> Sketch071
  Dir = (0,0,1)
  DirMode = 2
  FaceMakerClass = Part::FaceMakerBullseye
  LengthFwd = 71.4
  LengthRev = 0
  Placement = pos=(0,0,0.3) rot=(0,0,1;0rad)
  Solid = true
  Symmetric = false
FEATURE [Part::Fillet] Fillet054
  Base = -> Extrude062
  Edges = 1 edges r=2.4: [Edge17]
FEATURE [Part::Fillet] Fillet055  label="bottom015"
  Base = -> Fillet054
  Edges = 1 edges r=2.4: [Edge36]
FEATURE [Part::Cylinder] Cylinder055
  Angle = 360
  AttacherType = Attacher::AttachEngine3D
  Height = 10
  Placement = pos=(0,0,36.15) rot=(0,0,1;0rad)
  Radius = 4
FEATURE [Part::MultiFuse] Fusion131  label="removeToCreateHoleForPlugHousing002"
  Placement = pos=(70,19,36.15) rot=(0,1,0;1.5708rad)
  Shapes = -> [Cylinder054,Cylinder055]
FEATURE [Part::Cut] Cut056  label="Bottom001"
  Base = -> Fillet055
  Placement = pos=(9,0,0) rot=(0,0,1;0rad)
  Tool = -> Fusion131
FEATURE [Part::Cut] Cut057
  Base = -> Cut055
  Tool = -> Cut056
FEATURE [Sketcher::SketchObject] Sketch072  label="topSketch021"
  FullyConstrained = true
  sketch-geometry (4):
    g0: ArcOfCircle CenterX=105 CenterY=19 CenterZ=0 NormalX=0 NormalY=0 NormalZ=1 AngleXU=0 Radius=20.6155 StartAngle=5.54125 EndAngle=6.28319
    g1: ArcOfCircle CenterX=105 CenterY=19 CenterZ=0 NormalX=0 NormalY=0 NormalZ=1 AngleXU=0 Radius=13 StartAngle=5.54125 EndAngle=6.28319
    g2: LineSegment StartX=118 StartY=19 StartZ=0 EndX=125.616 EndY=19 EndZ=0
    g3: LineSegment StartX=114.583 StartY=10.2157 StartZ=0 EndX=120.197 EndY=5.06982 EndZ=0
  constraints (7):
    c: Block(g0)
    c: Block(g1)
    c: Coincident(g2,g1)
    c: Coincident(g2,g0)
    c: Horizontal(g2)
    c: Coincident(g3,g1)
    c: Coincident(g3,g0)
FEATURE [Part::Extrusion] Extrude063  label="bottomPlugHousingBit003"
  Base = -> Sketch072
  Dir = (0,0,1)
  DirMode = 2
  FaceMakerClass = Part::FaceMakerBullseye
  LengthFwd = 72
  LengthRev = 0
  Solid = true
  Symmetric = false
FEATURE [Part::Cylinder] Cylinder056
  Angle = 360
  AttacherType = Attacher::AttachEngine3D
  Height = 20
  Placement = pos=(0,0,36.15) rot=(0,0,1;0rad)
  Radius = 14.3
FEATURE [Part::Cylinder] Cylinder057
  Angle = 360
  AttacherType = Attacher::AttachEngine3D
  Height = 10
  Placement = pos=(0,0,36.15) rot=(0,0,1;0rad)
  Radius = 4
FEATURE [Part::Box] Box034  label="removeToCreteHoleForPlugHousing047"
  AttacherType = Attacher::AttachEngine3D
  Height = 28.6
  Length = 20
  Placement = pos=(106.15,0,21.7) rot=(0,0,1;0rad)
  Width = 19
FEATURE [Part::Cylinder] Cylinder058
  Angle = 360
  AttacherType = Attacher::AttachEngine3D
  Height = 20
  Placement = pos=(0,0,36.15) rot=(0,0,1;0rad)
  Radius = 14.3
FEATURE [Part::Cylinder] Cylinder059
  Angle = 360
  AttacherType = Attacher::AttachEngine3D
  Height = 10
  Placement = pos=(0,0,36.15) rot=(0,0,1;0rad)
  Radius = 4
FEATURE [Part::MultiFuse] Fusion134  label="removeToCreteHoleForPlugHousing046"
  Placement = pos=(70,19,36) rot=(0,1,0;1.5708rad)
  Shapes = -> [Cylinder058,Cylinder059]
FEATURE [Part::Cylinder] Cylinder060
  Angle = 360
  AttacherType = Attacher::AttachEngine3D
  Height = 20
  Placement = pos=(0,0,36.15) rot=(0,0,1;0rad)
  Radius = 14
FEATURE [Part::Cylinder] Cylinder061
  Angle = 360
  AttacherType = Attacher::AttachEngine3D
  Height = 10
  Placement = pos=(0,0,36.15) rot=(0,0,1;0rad)
  Radius = 4
FEATURE [Part::MultiFuse] Fusion135  label="removeToCreteHoleForPlugHousing048"
  Placement = pos=(70,19,36) rot=(0,1,0;1.5708rad)
  Shapes = -> [Cylinder060,Cylinder061]
FEATURE [Part::Box] Box035  label="removeToCreteHoleForPlugHousing049"
  AttacherType = Attacher::AttachEngine3D
  Height = 28.6
  Length = 20
  Placement = pos=(106.15,0,21.7) rot=(0,0,1;0rad)
  Width = 19
FEATURE [Part::MultiFuse] Fusion133  label="removeToCreteHoleForPlugHousing045"
  Placement = pos=(0,0,-28.3) rot=(0,0,1;0rad)
  Shapes = -> [Box035,Fusion134]
FEATURE [Part::MultiFuse] Fusion138  label="removeToCreteHoleForPlugHousing051"
  Placement = pos=(70,19,36) rot=(0,1,0;1.5708rad)
  Shapes = -> [Cylinder056,Cylinder057]
FEATURE [Part::MultiFuse] Fusion137  label="removeToCreteHoleForPlugHousing050"
  Placement = pos=(0,0,28.3) rot=(0,0,1;0rad)
  Shapes = -> [Box034,Fusion138]
FEATURE [Part::MultiFuse] Fusion132  label="removeToCreatePlugHousingBottomBit002"
  Shapes = -> [Fusion133,Fusion137]
FEATURE [Part::MultiFuse] Fusion136  label="removeToCreatePlugHousingBottomBit003"
  Shapes = -> [Fusion135,Fusion132]
FEATURE [Part::Cut] Cut058  label="bottomPlugHousingBit002"
  Base = -> Extrude063
  Placement = pos=(-0.09,0,0) rot=(0,0,1;0rad)
  Tool = -> Fusion136
FEATURE [Sketcher::SketchObject] Sketch073  label="bottomSketch003"
  FullyConstrained = true
  sketch-geometry (45):
    g0: LineSegment StartX=6.29999 StartY=8 StartZ=0 EndX=3.29999 EndY=8 EndZ=0
    g1: LineSegment StartX=3.29999 StartY=8 StartZ=0 EndX=3.29999 EndY=-6.03275e-07 EndZ=0
    g2: ArcOfCircle CenterX=8.29999 CenterY=5 CenterZ=0 NormalX=0 NormalY=0 NormalZ=1 AngleXU=0 Radius=2 StartAngle=3.14159 EndAngle=4.71239
    g3: LineSegment StartX=6.29999 StartY=8 StartZ=0 EndX=6.29999 EndY=5 EndZ=0
    g4: ArcOfCircle CenterX=105 CenterY=19 CenterZ=0 NormalX=0 NormalY=0 NormalZ=1 AngleXU=0 Radius=12.7 StartAngle=4.71239 EndAngle=5.94289
    g5-g11: Circle x7 (B-spline internal-alignment scaffolding for g12; pole/knot coordinates omitted)
    g12: BSplineCurve PolesCount=7 KnotsCount=5 Degree=3 IsPeriodic=0
    g13-g17: GeomPoint x5 (B-spline internal-alignment scaffolding for g12; pole/knot coordinates omitted)
    g18: ArcOfCircle CenterX=105 CenterY=19 CenterZ=0 NormalX=0 NormalY=0 NormalZ=1 AngleXU=0 Radius=15.7 StartAngle=5.81226 EndAngle=6.28319
    g19: BSplineCurve PolesCount=5 KnotsCount=3 Degree=3 IsPeriodic=0
    g20: LineSegment StartX=8.29999 StartY=3 StartZ=0 EndX=101.7 EndY=3 EndZ=0
    g21: LineSegment StartX=3.29999 StartY=-6.03275e-07 StartZ=0 EndX=105 EndY=-6.03275e-07 EndZ=0
    g22: LineSegment StartX=120.974 StartY=8.71251 StartZ=0 EndX=122.332 EndY=7.83778 EndZ=0
    g23: LineSegment StartX=105 StartY=-6.03274e-07 StartZ=0 EndX=113 EndY=-6.03274e-07 EndZ=0
    g24: ArcOfCircle CenterX=105 CenterY=19 CenterZ=0 NormalX=0 NormalY=0 NormalZ=1 AngleXU=0 Radius=20.6155 StartAngle=5.11091 EndAngle=5.71103
    g25: ArcOfCircle CenterX=117.7 CenterY=19 CenterZ=0 NormalX=0 NormalY=0 NormalZ=1 AngleXU=0 Radius=3 StartAngle=1.2e-15 EndAngle=2.10468
    g26: Circle CenterX=116.345 CenterY=16.3232 CenterZ=0 NormalX=0 NormalY=0 NormalZ=1 AngleXU=0 Radius=1
    g27: Circle CenterX=117.24 CenterY=15.7584 CenterZ=0 NormalX=0 NormalY=0 NormalZ=1 AngleXU=0 Radius=1
    g28: Circle CenterX=116.972 CenterY=14.7612 CenterZ=0 NormalX=0 NormalY=0 NormalZ=1 AngleXU=0 Radius=1
    g29: BSplineCurve PolesCount=3 KnotsCount=2 Degree=2 IsPeriodic=0
    g30: GeomPoint X=116.345 Y=16.3232 Z=0
    g31: GeomPoint X=116.972 Y=14.7612 Z=0
    g32: Circle CenterX=115.828 CenterY=17.157 CenterZ=0 NormalX=0 NormalY=0 NormalZ=1 AngleXU=0 Radius=1
    g33: Circle CenterX=115.841 CenterY=16.639 CenterZ=0 NormalX=0 NormalY=0 NormalZ=1 AngleXU=0 Radius=1
    g34: Circle CenterX=116.345 CenterY=16.3232 CenterZ=0 NormalX=0 NormalY=0 NormalZ=1 AngleXU=0 Radius=1
    g35: BSplineCurve PolesCount=3 KnotsCount=2 Degree=2 IsPeriodic=0
    g36: GeomPoint X=115.828 Y=17.157 Z=0
    g37: GeomPoint X=116.345 Y=16.3232 Z=0
    g38: LineSegment StartX=115.828 StartY=17.157 StartZ=0 EndX=115.828 EndY=20.8307 EndZ=0
    g39: Circle CenterX=115.828 CenterY=20.8307 CenterZ=0 NormalX=0 NormalY=0 NormalZ=1 AngleXU=0 Radius=1
    g40: Circle CenterX=115.831 CenterY=21.3396 CenterZ=0 NormalX=0 NormalY=0 NormalZ=1 AngleXU=0 Radius=1
    g41: Circle CenterX=116.173 CenterY=21.5825 CenterZ=0 NormalX=0 NormalY=0 NormalZ=1 AngleXU=0 Radius=1
    g42: BSplineCurve PolesCount=3 KnotsCount=2 Degree=2 IsPeriodic=0
    g43: GeomPoint X=115.828 Y=20.8307 Z=0
    g44: GeomPoint X=116.173 Y=21.5825 Z=0
  constraints (70):
    c: Horizontal(g0)
    c: Distance(g0) = 3
    c: Coincident(g1,g0)
    c: Vertical(g1)
    c: Block(g2)
    c: Block(g0)
    c: Coincident(g3,g0)
    c: Coincident(g3,g2)
    c: Vertical(g3)
    c: Block(g1)
    c: Block(g4)
    c: Coincident(g19,g4)
    c: Block(g19)
    c: Equal(g5, g6-g11) x6
    c: InternalAlignment(g5-g11 -> g12) x7
    c: InternalAlignment(g13-g17 -> g12) x5
    c: Block(g12)
    c: Coincident(g18,g12)
    c: Block(g18)
    c: Coincident(g20,g2)
    c: Coincident(g20,g19)
    c: Horizontal(g20)
    c: Distance(g20) = 93.4
    c: Coincident(g21,g1)
    c: Horizontal(g21)
    c: Distance(g21) = 101.7
    c: Horizontal(g23)
    c: Distance(g23) = 8
    c: Coincident(g24,g23)
    c: Block(g23)
    c: Coincident(g22,g24)
    c: Block(g24)
    c: Block(g22)
    c: Distance(g22) = 1.61553
    c: Coincident(g25,g18)
    c: Block(g25)
    c: Weight(g26) = 1
    c: Equal(g26,g27)
    c: Equal(g26,g28)
    c: Coincident(g29,g4)
    c: InternalAlignment(g26,g29)
    c: InternalAlignment(g27,g29)
    c: InternalAlignment(g28,g29)
    c: InternalAlignment(g30,g29)
    c: InternalAlignment(g31,g29)
    c: Block(g29)
    c: Weight(g32) = 1
    c: Equal(g32,g33)
    c: Equal(g32,g34)
    c: Coincident(g35,g29)
    c: InternalAlignment(g32,g35)
    c: InternalAlignment(g33,g35)
    c: InternalAlignment(g34,g35)
    c: InternalAlignment(g36,g35)
    c: InternalAlignment(g37,g35)
    c: Block(g35)
    c: Coincident(g38,g35)
    c: Vertical(g38)
    c: Block(g38)
    c: Coincident(g42,g38)
    c: Weight(g39) = 1
    c: Equal(g39,g40)
    c: Equal(g39,g41)
    c: Coincident(g42,g25)
    c: InternalAlignment(g39,g42)
    c: InternalAlignment(g40,g42)
    c: InternalAlignment(g41,g42)
    c: InternalAlignment(g43,g42)
    c: InternalAlignment(g44,g42)
    c: Block(g42)
FEATURE [Part::Extrusion] Extrude064  label="bottom016"
  Base = -> Sketch073
  Dir = (0,0,1)
  DirMode = 2
  FaceMakerClass = Part::FaceMakerBullseye
  LengthFwd = 71.4
  LengthRev = 0
  Placement = pos=(0,0,0.3) rot=(0,0,1;0rad)
  Solid = true
  Symmetric = false
FEATURE [Part::Revolution] Revolve157  label="removeToCreateScrewAndThreadedInsertHole063"
  Angle = 360
  Axis = (0,1,0)
  Base = (0,0,0)
  FaceMakerClass = Part::FaceMakerBullseye
  Placement = pos=(12.5,0,10) rot=(0,0,1;0rad)
  Solid = false
  Source = -> Face141
  Symmetric = false
FEATURE [Sketcher::SketchObject] Sketch074
  FullyConstrained = true
  Placement = pos=(117,19,0) rot=(0.57735,0.57735,0.57735;2.0944rad)
  sketch-geometry (48):
    g0: LineSegment StartX=-49.19 StartY=69.25 StartZ=0 EndX=-49.19 EndY=66.25 EndZ=0
    g1: LineSegment StartX=-49.19 StartY=63.5 StartZ=0 EndX=-49.19 EndY=60.5 EndZ=0
    g2: LineSegment StartX=-49.19 StartY=57.75 StartZ=0 EndX=-49.19 EndY=54.75 EndZ=0
    g3: LineSegment StartX=-49.19 StartY=52 StartZ=0 EndX=-49.19 EndY=49 EndZ=0
    g4: LineSegment StartX=-49.19 StartY=46.25 StartZ=0 EndX=-49.19 EndY=43.25 EndZ=0
    g5: LineSegment StartX=-49.19 StartY=40.5 StartZ=0 EndX=-49.19 EndY=37.5 EndZ=0
    g6: LineSegment StartX=-49.19 StartY=34.5 StartZ=0 EndX=-49.19 EndY=31.5 EndZ=0
    g7: LineSegment StartX=-49.19 StartY=28.75 StartZ=0 EndX=-49.19 EndY=25.75 EndZ=0
    g8: LineSegment StartX=-49.19 StartY=23 StartZ=0 EndX=-49.19 EndY=20 EndZ=0
    g9: LineSegment StartX=-49.19 StartY=17.25 StartZ=0 EndX=-49.19 EndY=14.25 EndZ=0
    g10: LineSegment StartX=-49.19 StartY=11.5 StartZ=0 EndX=-49.19 EndY=8.5 EndZ=0
    g11: LineSegment StartX=-49.19 StartY=5.75 StartZ=0 EndX=-49.19 EndY=2.75 EndZ=0
    g12: ArcOfCircle CenterX=-1.5 CenterY=67.75 CenterZ=0 NormalX=0 NormalY=0 NormalZ=1 AngleXU=0 Radius=1.5 StartAngle=4.71239 EndAngle=7.85398
    g13: ArcOfCircle CenterX=-1.5 CenterY=62 CenterZ=0 NormalX=0 NormalY=0 NormalZ=1 AngleXU=0 Radius=1.5 StartAngle=4.71239 EndAngle=7.85398
    g14: ArcOfCircle CenterX=-1.5 CenterY=56.25 CenterZ=0 NormalX=0 NormalY=0 NormalZ=1 AngleXU=0 Radius=1.5 StartAngle=4.71239 EndAngle=7.85398
    g15: ArcOfCircle CenterX=-11.49 CenterY=50.5 CenterZ=0 NormalX=0 NormalY=0 NormalZ=1 AngleXU=0 Radius=1.5 StartAngle=4.71239 EndAngle=7.85398
    g16: ArcOfCircle CenterX=-16.28 CenterY=44.75 CenterZ=0 NormalX=0 NormalY=0 NormalZ=1 AngleXU=0 Radius=1.5 StartAngle=4.71239 EndAngle=7.85398
    g17: ArcOfCircle CenterX=-18.2337 CenterY=39 CenterZ=0 NormalX=0 NormalY=0 NormalZ=1 AngleXU=0 Radius=1.5 StartAngle=4.71485 EndAngle=7.85398
    g18: ArcOfCircle CenterX=-16.2837 CenterY=27.25 CenterZ=0 NormalX=0 NormalY=0 NormalZ=1 AngleXU=0 Radius=1.5 StartAngle=4.71485 EndAngle=7.85398
    g19: ArcOfCircle CenterX=-18.2337 CenterY=33 CenterZ=0 NormalX=0 NormalY=0 NormalZ=1 AngleXU=0 Radius=1.5 StartAngle=4.71485 EndAngle=7.85398
    g20: ArcOfCircle CenterX=-11.49 CenterY=21.5 CenterZ=0 NormalX=0 NormalY=0 NormalZ=1 AngleXU=0 Radius=1.5 StartAngle=4.71239 EndAngle=7.85398
    g21: ArcOfCircle CenterX=-1.5 CenterY=4.25 CenterZ=0 NormalX=0 NormalY=0 NormalZ=1 AngleXU=0 Radius=1.5 StartAngle=4.71239 EndAngle=7.85398
    g22: ArcOfCircle CenterX=-1.5 CenterY=10 CenterZ=0 NormalX=0 NormalY=0 NormalZ=1 AngleXU=0 Radius=1.5 StartAngle=4.71239 EndAngle=7.85398
    g23: ArcOfCircle CenterX=-1.5 CenterY=15.75 CenterZ=0 NormalX=0 NormalY=0 NormalZ=1 AngleXU=0 Radius=1.5 StartAngle=4.71239 EndAngle=7.85398
    g24: LineSegment StartX=-49.19 StartY=69.25 StartZ=0 EndX=-1.5 EndY=69.25 EndZ=0
    g25: LineSegment StartX=-49.19 StartY=66.25 StartZ=0 EndX=-1.5 EndY=66.25 EndZ=0
    g26: LineSegment StartX=-49.19 StartY=63.5 StartZ=0 EndX=-1.5 EndY=63.5 EndZ=0
    g27: LineSegment StartX=-49.19 StartY=60.5 StartZ=0 EndX=-1.5 EndY=60.5 EndZ=0
    g28: LineSegment StartX=-49.19 StartY=57.75 StartZ=0 EndX=-1.5 EndY=57.75 EndZ=0
    g29: LineSegment StartX=-49.19 StartY=54.75 StartZ=0 EndX=-1.5 EndY=54.75 EndZ=0
    g30: LineSegment StartX=-49.19 StartY=52 StartZ=0 EndX=-11.49 EndY=52 EndZ=0
    g31: LineSegment StartX=-49.19 StartY=49 StartZ=0 EndX=-11.49 EndY=49 EndZ=0
    g32: LineSegment StartX=-49.19 StartY=46.25 StartZ=0 EndX=-16.28 EndY=46.25 EndZ=0
    g33: LineSegment StartX=-49.19 StartY=43.25 StartZ=0 EndX=-16.28 EndY=43.25 EndZ=0
    g34: LineSegment StartX=-49.19 StartY=40.5 StartZ=0 EndX=-18.2337 EndY=40.5 EndZ=0
    g35: LineSegment StartX=-49.19 StartY=37.5 StartZ=0 EndX=-18.23 EndY=37.5 EndZ=0
    g36: LineSegment StartX=-49.19 StartY=34.5 StartZ=0 EndX=-18.2337 EndY=34.5 EndZ=0
    g37: LineSegment StartX=-49.19 StartY=31.5 StartZ=0 EndX=-18.23 EndY=31.5 EndZ=0
    g38: LineSegment StartX=-49.19 StartY=28.75 StartZ=0 EndX=-16.2837 EndY=28.75 EndZ=0
    g39: LineSegment StartX=-49.19 StartY=25.75 StartZ=0 EndX=-16.28 EndY=25.75 EndZ=0
    g40: LineSegment StartX=-49.19 StartY=23 StartZ=0 EndX=-11.49 EndY=23 EndZ=0
    g41: LineSegment StartX=-49.19 StartY=20 StartZ=0 EndX=-11.49 EndY=20 EndZ=0
    g42: LineSegment StartX=-49.19 StartY=17.25 StartZ=0 EndX=-1.5 EndY=17.25 EndZ=0
    g43: LineSegment StartX=-49.19 StartY=14.25 StartZ=0 EndX=-1.5 EndY=14.25 EndZ=0
    g44: LineSegment StartX=-49.19 StartY=11.5 StartZ=0 EndX=-1.5 EndY=11.5 EndZ=0
    g45: LineSegment StartX=-49.19 StartY=8.5 StartZ=0 EndX=-1.5 EndY=8.5 EndZ=0
    g46: LineSegment StartX=-49.19 StartY=5.75 StartZ=0 EndX=-1.5 EndY=5.75 EndZ=0
    g47: LineSegment StartX=-49.19 StartY=2.75 StartZ=0 EndX=-1.5 EndY=2.75 EndZ=0
  constraints (120):
    c: Vertical(g0)
    c: Distance(g0) = 3
    c: Block(g0)
    c: Vertical(g1)
    c: Distance(g1) = 3
    c: Vertical(g2)
    c: Equal(g0,g2) = 3
    c: Block(g2)
    c: Vertical(g3)
    c: Equal(g1,g3) = 3
    c: Vertical(g4)
    c: Equal(g0,g4) = 3
    c: Block(g4)
    c: Vertical(g5)
    c: Equal(g1,g5) = 3
    c: Vertical(g6)
    c: Equal(g0,g6) = 3
    c: Block(g6)
    c: Vertical(g7)
    c: Equal(g1,g7) = 3
    c: Vertical(g8)
    c: Equal(g0,g8) = 3
    c: Block(g8)
    c: Vertical(g9)
    c: Equal(g1,g9) = 3
    c: Vertical(g10)
    c: Equal(g0,g10) = 3
    c: Block(g10)
    c: Vertical(g11)
    c: Equal(g1,g11) = 3
    c: Block(g12)
    c: Block(g13)
    c: Block(g14)
    c: Block(g15)
    c: Block(g16)
    c: Block(g17)
    c: Block(g18)
    c: Block(g19)
    c: Block(g20)
    c: Block(g21)
    c: Block(g22)
    c: Block(g23)
    c: Block(g11)
    c: Block(g9)
    c: Block(g7)
    c: Block(g5)
    c: Block(g3)
    c: Block(g1)
    c: Coincident(g24,g0)
    c: Coincident(g24,g12)
    c: Horizontal(g24)
    c: Coincident(g25,g0)
    c: Coincident(g25,g12)
    c: Horizontal(g25)
    c: Coincident(g26,g1)
    c: Coincident(g26,g13)
    c: Horizontal(g26)
    c: Coincident(g27,g1)
    c: Coincident(g27,g13)
    c: Horizontal(g27)
    c: Coincident(g28,g2)
    c: Coincident(g28,g14)
    c: Horizontal(g28)
    c: Coincident(g29,g2)
    c: Coincident(g29,g14)
    c: Horizontal(g29)
    c: Coincident(g30,g3)
    c: Coincident(g30,g15)
    c: Horizontal(g30)
    c: Coincident(g31,g3)
    c: Coincident(g31,g15)
    c: Horizontal(g31)
    c: Coincident(g32,g4)
    c: Coincident(g32,g16)
    c: Horizontal(g32)
    c: Coincident(g33,g4)
    c: Coincident(g33,g16)
    c: Horizontal(g33)
    c: Coincident(g34,g5)
    c: Coincident(g34,g17)
    c: Horizontal(g34)
    c: Coincident(g35,g5)
    c: Coincident(g35,g17)
    c: Horizontal(g35)
    c: Coincident(g36,g6)
    c: Coincident(g36,g19)
    c: Horizontal(g36)
    c: Coincident(g37,g6)
    c: Coincident(g37,g19)
    c: Horizontal(g37)
    c: Coincident(g38,g7)
    c: Coincident(g38,g18)
    c: Horizontal(g38)
    c: Coincident(g39,g7)
    c: Coincident(g39,g18)
    c: Horizontal(g39)
    c: Coincident(g40,g8)
    c: Coincident(g40,g20)
    c: Horizontal(g40)
    c: Coincident(g41,g8)
    c: Coincident(g41,g20)
    c: Horizontal(g41)
    c: Coincident(g42,g9)
    c: Coincident(g42,g23)
    c: Horizontal(g42)
    c: Coincident(g43,g9)
    c: Coincident(g43,g23)
    c: Horizontal(g43)
    c: Coincident(g44,g10)
    c: Coincident(g44,g22)
    c: Horizontal(g44)
    c: Coincident(g45,g10)
    c: Coincident(g45,g22)
    c: Horizontal(g45)
    c: Coincident(g46,g11)
    c: Coincident(g46,g21)
    c: Horizontal(g46)
    c: Coincident(g47,g11)
    c: Coincident(g47,g21)
    c: Horizontal(g47)
FEATURE [Part::Extrusion] Extrude065
  Base = -> Sketch074
  Dir = (1,0,0)
  DirMode = 2
  FaceMakerClass = Part::FaceMakerBullseye
  LengthFwd = 23
  LengthRev = 0
  Placement = pos=(-19,0,0) rot=(0,0,1;0rad)
  Solid = true
  Symmetric = false
FEATURE [Part::Fillet] Fillet056  label="removeToCreateVentalationHoles003"
  Base = -> Extrude065
  Edges = <same value as first occurrence — deduplicated (x6 in doc)>
  Placement = pos=(7,0.02,0) rot=(0,0,1;0rad)
FEATURE [Part::Revolution] Revolve158  label="removeToCreateScrewAndThreadedInsertHole065"
  Angle = 360
  Axis = (0,1,0)
  Base = (0,0,0)
  FaceMakerClass = Part::FaceMakerBullseye
  Placement = pos=(12.5,0,62) rot=(0,0,1;0rad)
  Solid = false
  Source = -> Face146
  Symmetric = false
FEATURE [Part::Revolution] Revolve159  label="removeToCreateScrewAndThreadedInsertHole066"
  Angle = 360
  Axis = (0,1,0)
  Base = (0,0,0)
  FaceMakerClass = Part::FaceMakerBullseye
  Placement = pos=(89.5,0,68.5) rot=(0,0,1;0rad)
  Solid = false
  Source = -> Face143
  Symmetric = false
FEATURE [Part::Revolution] Revolve160  label="removeToCreateScrewAndThreadedInsertHole067"
  Angle = 360
  Axis = (0,1,0)
  Base = (0,0,0)
  FaceMakerClass = Part::FaceMakerBullseye
  Placement = pos=(89.5,0,3.5) rot=(0,0,1;0rad)
  Solid = false
  Source = -> Face142
  Symmetric = false
FEATURE [Part::Revolution] Revolve161  label="removeToCreateScrewAndThreadedInsertHole068"
  Angle = 360
  Axis = (0,1,0)
  Base = (0,0,0)
  FaceMakerClass = Part::FaceMakerBullseye
  Placement = pos=(109.5,4.7,3.5) rot=(0,0,1;0rad)
  Solid = false
  Source = -> Face145
  Symmetric = false
FEATURE [Part::Revolution] Revolve162  label="removeToCreateScrewAndThreadedInsertHole069"
  Angle = 360
  Axis = (0,1,0)
  Base = (0,0,0)
  FaceMakerClass = Part::FaceMakerBullseye
  Placement = pos=(109.5,4.7,68.5) rot=(0,0,1;0rad)
  Solid = false
  Source = -> Face144
  Symmetric = false
FEATURE [Part::MultiFuse] Fusion141  label="removeToCreateScrewAndThreadedInsertHole064"
  Shapes = -> [Revolve162,Revolve161,Revolve160,Revolve159,Revolve158,Revolve157]
FEATURE [Part::Cylinder] Cylinder062
  Angle = 360
  AttacherType = Attacher::AttachEngine3D
  Height = 20
  Placement = pos=(0,0,36.15) rot=(0,0,1;0rad)
  Radius = 14
FEATURE [Part::Cylinder] Cylinder063
  Angle = 360
  AttacherType = Attacher::AttachEngine3D
  Height = 10
  Placement = pos=(0,0,36.15) rot=(0,0,1;0rad)
  Radius = 4
FEATURE [Part::MultiFuse] Fusion139  label="removeToCreteHoleForPlugHousing052"
  Placement = pos=(70,19,36) rot=(0,1,0;1.5708rad)
  Shapes = -> [Cylinder062,Cylinder063]
FEATURE [Part::Cut] Cut060  label="bottom017"
  Base = -> Extrude064
  Tool = -> Fusion139
FEATURE [Part::Cut] Cut061  label="bottom019"
  Base = -> Cut060
  Tool = -> Fusion141
FEATURE [Part::MultiFuse] Fusion140  label="bottom018"
  Shapes = -> [Cut061,Cut058]
FEATURE [Part::Cut] Cut059  label="bottom020"
  Base = -> Fusion140
  Tool = -> Fillet056
FEATURE [Part::Box] Box036  label="Cube021"
  AttacherType = Attacher::AttachEngine3D
  Height = 80
  Length = 26
  Placement = pos=(0,-1,-5) rot=(0,0,1;0rad)
  Width = 11
FEATURE [Part::Cut] Cut062  label="removeFromBottom002"
  Base = -> Cut057
  Tool = -> Box036
FEATURE [Part::Cut] Cut063
  Base = -> Cut059
  Tool = -> Cut062
FEATURE [Part::Cut] Cut064  label="pcbStands"
  Base = -> Fusion095
  Tool = -> Fusion127
FEATURE [Sketcher::SketchObject] Sketch075  label="topSketch022"
  FullyConstrained = true
  sketch-geometry (6):
    g0: LineSegment StartX=19 StartY=38 StartZ=0 EndX=117 EndY=38 EndZ=0
    g1: ArcOfCircle CenterX=19 CenterY=19 CenterZ=0 NormalX=0 NormalY=0 NormalZ=1 AngleXU=0 Radius=19 StartAngle=1.5708 EndAngle=3.14159
    g2: LineSegment StartX=117 StartY=38 StartZ=0 EndX=117 EndY=19 EndZ=0
    g3: LineSegment StartX=98 StartY=1.0161e-12 StartZ=0 EndX=5.22862e-06 EndY=1.0161e-12 EndZ=0
    g4: LineSegment StartX=5.22862e-06 StartY=19 StartZ=0 EndX=5.22862e-06 EndY=1.0161e-12 EndZ=0
    g5: ArcOfCircle CenterX=98 CenterY=19 CenterZ=0 NormalX=0 NormalY=0 NormalZ=1 AngleXU=0 Radius=19 StartAngle=4.71239 EndAngle=6.28319
  constraints (16):
    c: Horizontal(g0)
    c: Distance(g0) = 98
    c: Coincident(g1,g0)
    c: Block(g1)
    c: Coincident(g2,g0)
    c: Vertical(g2)
    c: Distance(g2) = 19
    c: Horizontal(g3)
    c: Coincident(g4,g1)
    c: Vertical(g4)
    c: Coincident(g3,g4)
    c: Block(g3)
    c: Coincident(g5,g2)
    c: Coincident(g5,g3)
    c: Block(g0)
    c: Block(g5)
FEATURE [Part::Extrusion] Extrude067  label="sideB003"
  Base = -> Sketch075
  Dir = (0,0,1)
  DirMode = 2
  FaceMakerClass = Part::FaceMakerBullseye
  LengthFwd = 3
  LengthRev = 0
  Placement = pos=(0,0,71.7) rot=(0,0,1;0rad)
  Solid = true
  Symmetric = false
FEATURE [Sketcher::SketchObject] Sketch076  label="topSketch023"
  FullyConstrained = true
  sketch-geometry (6):
    g0: LineSegment StartX=19 StartY=38 StartZ=0 EndX=117 EndY=38 EndZ=0
    g1: ArcOfCircle CenterX=19 CenterY=19 CenterZ=0 NormalX=0 NormalY=0 NormalZ=1 AngleXU=0 Radius=19 StartAngle=1.5708 EndAngle=3.14159
    g2: LineSegment StartX=117 StartY=38 StartZ=0 EndX=117 EndY=19 EndZ=0
    g3: LineSegment StartX=98 StartY=1.0161e-12 StartZ=0 EndX=5.22862e-06 EndY=1.0161e-12 EndZ=0
    g4: LineSegment StartX=5.22862e-06 StartY=19 StartZ=0 EndX=5.22862e-06 EndY=1.0161e-12 EndZ=0
    g5: ArcOfCircle CenterX=98 CenterY=19 CenterZ=0 NormalX=0 NormalY=0 NormalZ=1 AngleXU=0 Radius=19 StartAngle=4.71239 EndAngle=6.28319
  constraints (16):
    c: Horizontal(g0)
    c: Distance(g0) = 98
    c: Coincident(g1,g0)
    c: Block(g1)
    c: Coincident(g2,g0)
    c: Vertical(g2)
    c: Distance(g2) = 19
    c: Horizontal(g3)
    c: Coincident(g4,g1)
    c: Vertical(g4)
    c: Coincident(g3,g4)
    c: Block(g3)
    c: Coincident(g5,g2)
    c: Coincident(g5,g3)
    c: Block(g0)
    c: Block(g5)
FEATURE [Part::Extrusion] Extrude066  label="sideA003"
  Base = -> Sketch076
  Dir = (0,0,1)
  DirMode = 2
  FaceMakerClass = Part::FaceMakerBullseye
  LengthFwd = 3
  LengthRev = 0
  Placement = pos=(0,0,-2.7) rot=(0,0,1;0rad)
  Solid = true
  Symmetric = false
FEATURE [Part::MultiFuse] Fusion142  label="removeFromBottom003"
  Placement = pos=(2,0,0) rot=(0,0,1;0rad)
  Shapes = -> [Extrude066,Extrude067]
FEATURE [Part::Cut] Cut065  label="screwRetainers002"
  Base = -> Fusion096
  Tool = -> Fusion142
FEATURE [Sketcher::SketchObject] Sketch077
  FullyConstrained = true
  Placement = pos=(117,19,0) rot=(0.57735,0.57735,0.57735;2.0944rad)
  sketch-geometry (8):
    g0: LineSegment StartX=-49.19 StartY=63.5 StartZ=0 EndX=-49.19 EndY=60.5 EndZ=0
    g1: LineSegment StartX=-49.19 StartY=11.5 StartZ=0 EndX=-49.19 EndY=8.5 EndZ=0
    g2: ArcOfCircle CenterX=-1.5 CenterY=62 CenterZ=0 NormalX=0 NormalY=0 NormalZ=1 AngleXU=0 Radius=1.5 StartAngle=4.71239 EndAngle=7.85398
    g3: ArcOfCircle CenterX=-1.5 CenterY=10 CenterZ=0 NormalX=0 NormalY=0 NormalZ=1 AngleXU=0 Radius=1.5 StartAngle=4.71239 EndAngle=7.85398
    g4: LineSegment StartX=-49.19 StartY=63.5 StartZ=0 EndX=-1.5 EndY=63.5 EndZ=0
    g5: LineSegment StartX=-49.19 StartY=60.5 StartZ=0 EndX=-1.5 EndY=60.5 EndZ=0
    g6: LineSegment StartX=-49.19 StartY=11.5 StartZ=0 EndX=-1.5 EndY=11.5 EndZ=0
    g7: LineSegment StartX=-49.19 StartY=8.5 StartZ=0 EndX=-1.5 EndY=8.5 EndZ=0
  constraints (19):
    c: Vertical(g0)
    c: Distance(g0) = 3
    c: Vertical(g1)
    c: Block(g1)
    c: Block(g2)
    c: Block(g3)
    c: Block(g0)
    c: Coincident(g4,g0)
    c: Coincident(g4,g2)
    c: Horizontal(g4)
    c: Coincident(g5,g0)
    c: Coincident(g5,g2)
    c: Horizontal(g5)
    c: Coincident(g6,g1)
    c: Coincident(g6,g3)
    c: Horizontal(g6)
    c: Coincident(g7,g1)
    c: Coincident(g7,g3)
    c: Horizontal(g7)
FEATURE [Part::Extrusion] Extrude068
  Base = -> Sketch077
  Dir = (1,0,0)
  DirMode = 2
  FaceMakerClass = Part::FaceMakerBullseye
  LengthFwd = 10
  LengthRev = 0
  Solid = true
  Symmetric = false
FEATURE [Part::Fillet] Fillet057  label="removeFromtMoreFrontCaseScrewRetainers002"
  Base = -> Extrude068
  Edges = 4 edges r=1.49: [Edge6,Edge11,Edge18,Edge23]
  Placement = pos=(-12,0,0) rot=(0,0,1;0rad)
FEATURE [Sketcher::SketchObject] Sketch078
  FullyConstrained = true
  Placement = pos=(117,19,0) rot=(0.57735,0.57735,0.57735;2.0944rad)
  sketch-geometry (8):
    g0: LineSegment StartX=-49.19 StartY=69.25 StartZ=0 EndX=-49.19 EndY=66.25 EndZ=0
    g1: LineSegment StartX=-49.19 StartY=5.75 StartZ=0 EndX=-49.19 EndY=2.75 EndZ=0
    g2: ArcOfCircle CenterX=-1.5 CenterY=67.75 CenterZ=0 NormalX=0 NormalY=0 NormalZ=1 AngleXU=0 Radius=1.5 StartAngle=4.71239 EndAngle=7.85398
    g3: ArcOfCircle CenterX=-1.5 CenterY=4.25 CenterZ=0 NormalX=0 NormalY=0 NormalZ=1 AngleXU=0 Radius=1.5 StartAngle=4.71239 EndAngle=7.85398
    g4: LineSegment StartX=-49.19 StartY=69.25 StartZ=0 EndX=-1.5 EndY=69.25 EndZ=0
    g5: LineSegment StartX=-49.19 StartY=66.25 StartZ=0 EndX=-1.5 EndY=66.25 EndZ=0
    g6: LineSegment StartX=-49.19 StartY=5.75 StartZ=0 EndX=-1.5 EndY=5.75 EndZ=0
    g7: LineSegment StartX=-49.19 StartY=2.75 StartZ=0 EndX=-1.5 EndY=2.75 EndZ=0
  constraints (19):
    c: Vertical(g0)
    c: Distance(g0) = 3
    c: Block(g0)
    c: Vertical(g1)
    c: Block(g2)
    c: Block(g3)
    c: Block(g1)
    c: Coincident(g4,g0)
    c: Coincident(g4,g2)
    c: Horizontal(g4)
    c: Coincident(g5,g0)
    c: Coincident(g5,g2)
    c: Horizontal(g5)
    c: Coincident(g6,g1)
    c: Coincident(g6,g3)
    c: Horizontal(g6)
    c: Coincident(g7,g1)
    c: Coincident(g7,g3)
    c: Horizontal(g7)
FEATURE [Part::Extrusion] Extrude069
  Base = -> Sketch078
  Dir = (1,0,0)
  DirMode = 2
  FaceMakerClass = Part::FaceMakerBullseye
  LengthFwd = 10
  LengthRev = 0
  Solid = true
  Symmetric = false
FEATURE [Part::Fillet] Fillet058  label="removeFromtMoreFrontCaseScrewRetainers003"
  Base = -> Extrude069
  Edges = 4 edges r=1.49: [Edge6,Edge11,Edge18,Edge23]
  Placement = pos=(-4,0,0) rot=(0,0,1;0rad)
FEATURE [Part::Cut] Cut066
  Base = -> Cut065
  Tool = -> Fillet058
FEATURE [Part::Cut] Cut067  label="screwPillars"
  Base = -> Cut066
  Tool = -> Fillet057
FEATURE [Part::MultiFuse] Fusion143  label="bottom021"
  Shapes = -> [Cut031,Cut063]
FEATURE [Part::Cylinder] Cylinder
  Angle = 360
  AttacherType = Attacher::AttachEngine3D
  Height = 10
  Placement = pos=(20.65,12,4.68) rot=(1,0,0;1.5708rad)
  Radius = 2
FEATURE [Part::Cylinder] Cylinder064
  Angle = 360
  AttacherType = Attacher::AttachEngine3D
  Height = 10
  Placement = pos=(20.65,12,67.38) rot=(1,0,0;1.5708rad)
  Radius = 2
FEATURE [Part::Cylinder] Cylinder065
  Angle = 360
  AttacherType = Attacher::AttachEngine3D
  Height = 10
  Placement = pos=(77.15,12,67.38) rot=(1,0,0;1.5708rad)
  Radius = 2
FEATURE [Part::Cylinder] Cylinder066
  Angle = 360
  AttacherType = Attacher::AttachEngine3D
  Height = 10
  Placement = pos=(77.15,12,4.68) rot=(1,0,0;1.5708rad)
  Radius = 2
FEATURE [Part::MultiFuse] Fusion144  label="removeFromThreadedInsertHousing"
  Shapes = -> [Cylinder065,Cylinder064,Cylinder,Cylinder066]
FEATURE [Part::Cut] Cut068  label="pcbStands001"
  Base = -> Cut064
  Tool = -> Fusion144
FEATURE [Part::MultiFuse] Fusion145
  Shapes = -> [Cut068,Fusion143]
FEATURE [Part::MultiFuse] Fusion146
  Shapes = -> [Fusion145]
FEATURE [Part::MultiFuse] Fusion147  label="bottom022"
  Shapes = -> [Cut067,Fusion146]
FEATURE [Part::MultiFuse] Fusion148  label="casePillars005"
  Shapes = -> [Cut047,Fusion092]
FEATURE [Part::MultiFuse] Fusion149  label="bottom023"
  Shapes = -> [Fusion124,Fusion113,Fusion147]
FEATURE [Part::MultiFuse] Fusion150  label="topBits"
  Shapes = -> [Cut025,Fusion148,Cut030,Fillet034]
FEATURE [Part::Feature] Face149 .. Face152  x4 (patterned run collapsed; names and placements below)
  shape: bbox 3.2 x 1.5 x 2e-07 mm, 1 faces, 0 solids (baked)
FEATURE [Part::Feature] Face153
  shape: bbox 3.6 x 3.2 x 2e-07 mm, 1 faces, 0 solids (baked)
FEATURE [Part::Feature] Face154
  shape: bbox 3.6 x 3.2 x 2e-07 mm, 1 faces, 0 solids (baked)
FEATURE [Sketcher::SketchObject] Sketch079  label="topSketch024"
  FullyConstrained = true
  sketch-geometry (6):
    g0: LineSegment StartX=19 StartY=38 StartZ=0 EndX=117 EndY=38 EndZ=0
    g1: ArcOfCircle CenterX=19 CenterY=19 CenterZ=0 NormalX=0 NormalY=0 NormalZ=1 AngleXU=0 Radius=19 StartAngle=1.5708 EndAngle=3.14159
    g2: LineSegment StartX=117 StartY=38 StartZ=0 EndX=117 EndY=19 EndZ=0
    g3: LineSegment StartX=98 StartY=1.0161e-12 StartZ=0 EndX=5.22862e-06 EndY=1.0161e-12 EndZ=0
    g4: LineSegment StartX=5.22862e-06 StartY=19 StartZ=0 EndX=5.22862e-06 EndY=1.0161e-12 EndZ=0
    g5: ArcOfCircle CenterX=98 CenterY=19 CenterZ=0 NormalX=0 NormalY=0 NormalZ=1 AngleXU=0 Radius=19 StartAngle=4.71239 EndAngle=6.28319
  constraints (16):
    c: Horizontal(g0)
    c: Distance(g0) = 98
    c: Coincident(g1,g0)
    c: Block(g1)
    c: Coincident(g2,g0)
    c: Vertical(g2)
    c: Distance(g2) = 19
    c: Horizontal(g3)
    c: Coincident(g4,g1)
    c: Vertical(g4)
    c: Coincident(g3,g4)
    c: Block(g3)
    c: Coincident(g5,g2)
    c: Coincident(g5,g3)
    c: Block(g0)
    c: Block(g5)
FEATURE [Sketcher::SketchObject] Sketch080  label="topSketch025"
  FullyConstrained = true
  sketch-geometry (6):
    g0: LineSegment StartX=19 StartY=38 StartZ=0 EndX=117 EndY=38 EndZ=0
    g1: ArcOfCircle CenterX=19 CenterY=19 CenterZ=0 NormalX=0 NormalY=0 NormalZ=1 AngleXU=0 Radius=19 StartAngle=1.5708 EndAngle=3.14159
    g2: LineSegment StartX=117 StartY=38 StartZ=0 EndX=117 EndY=19 EndZ=0
    g3: LineSegment StartX=98 StartY=1.0161e-12 StartZ=0 EndX=5.22862e-06 EndY=1.0161e-12 EndZ=0
    g4: LineSegment StartX=5.22862e-06 StartY=19 StartZ=0 EndX=5.22862e-06 EndY=1.0161e-12 EndZ=0
    g5: ArcOfCircle CenterX=98 CenterY=19 CenterZ=0 NormalX=0 NormalY=0 NormalZ=1 AngleXU=0 Radius=19 StartAngle=4.71239 EndAngle=6.28319
  constraints (16):
    c: Horizontal(g0)
    c: Distance(g0) = 98
    c: Coincident(g1,g0)
    c: Block(g1)
    c: Coincident(g2,g0)
    c: Vertical(g2)
    c: Distance(g2) = 19
    c: Horizontal(g3)
    c: Coincident(g4,g1)
    c: Vertical(g4)
    c: Coincident(g3,g4)
    c: Block(g3)
    c: Coincident(g5,g2)
    c: Coincident(g5,g3)
    c: Block(g0)
    c: Block(g5)
FEATURE [Part::Extrusion] Extrude070  label="sideA004"
  Base = -> Sketch080
  Dir = (0,0,1)
  DirMode = 2
  FaceMakerClass = Part::FaceMakerBullseye
  LengthFwd = 3
  LengthRev = 0
  Placement = pos=(0,0,-2.7) rot=(0,0,1;0rad)
  Solid = true
  Symmetric = false
FEATURE [Sketcher::SketchObject] Sketch081
  FullyConstrained = true
  Placement = pos=(117,19,0) rot=(0.57735,0.57735,0.57735;2.0944rad)
  sketch-geometry (8):
    g0: LineSegment StartX=-49.19 StartY=63.5 StartZ=0 EndX=-49.19 EndY=60.5 EndZ=0
    g1: LineSegment StartX=-49.19 StartY=11.5 StartZ=0 EndX=-49.19 EndY=8.5 EndZ=0
    g2: ArcOfCircle CenterX=-1.5 CenterY=62 CenterZ=0 NormalX=0 NormalY=0 NormalZ=1 AngleXU=0 Radius=1.5 StartAngle=4.71239 EndAngle=7.85398
    g3: ArcOfCircle CenterX=-1.5 CenterY=10 CenterZ=0 NormalX=0 NormalY=0 NormalZ=1 AngleXU=0 Radius=1.5 StartAngle=4.71239 EndAngle=7.85398
    g4: LineSegment StartX=-49.19 StartY=63.5 StartZ=0 EndX=-1.5 EndY=63.5 EndZ=0
    g5: LineSegment StartX=-49.19 StartY=60.5 StartZ=0 EndX=-1.5 EndY=60.5 EndZ=0
    g6: LineSegment StartX=-49.19 StartY=11.5 StartZ=0 EndX=-1.5 EndY=11.5 EndZ=0
    g7: LineSegment StartX=-49.19 StartY=8.5 StartZ=0 EndX=-1.5 EndY=8.5 EndZ=0
  constraints (19):
    c: Vertical(g0)
    c: Distance(g0) = 3
    c: Vertical(g1)
    c: Block(g1)
    c: Block(g2)
    c: Block(g3)
    c: Block(g0)
    c: Coincident(g4,g0)
    c: Coincident(g4,g2)
    c: Horizontal(g4)
    c: Coincident(g5,g0)
    c: Coincident(g5,g2)
    c: Horizontal(g5)
    c: Coincident(g6,g1)
    c: Coincident(g6,g3)
    c: Horizontal(g6)
    c: Coincident(g7,g1)
    c: Coincident(g7,g3)
    c: Horizontal(g7)
FEATURE [Part::Extrusion] Extrude071  label="sideB004"
  Base = -> Sketch079
  Dir = (0,0,1)
  DirMode = 2
  FaceMakerClass = Part::FaceMakerBullseye
  LengthFwd = 3
  LengthRev = 0
  Placement = pos=(0,0,71.7) rot=(0,0,1;0rad)
  Solid = true
  Symmetric = false
FEATURE [Part::MultiFuse] Fusion152  label="removeFromBottom004"
  Placement = pos=(2,0,0) rot=(0,0,1;0rad)
  Shapes = -> [Extrude070,Extrude071]
FEATURE [Part::Extrusion] Extrude072
  Base = -> Sketch081
  Dir = (1,0,0)
  DirMode = 2
  FaceMakerClass = Part::FaceMakerBullseye
  LengthFwd = 10
  LengthRev = 0
  Solid = true
  Symmetric = false
FEATURE [Part::Fillet] Fillet059  label="removeFromtMoreFrontCaseScrewRetainers004"
  Base = -> Extrude072
  Edges = 4 edges r=1.49: [Edge6,Edge11,Edge18,Edge23]
  Placement = pos=(-12,0,0) rot=(0,0,1;0rad)
FEATURE [Sketcher::SketchObject] Sketch082
  FullyConstrained = true
  Placement = pos=(117,19,0) rot=(0.57735,0.57735,0.57735;2.0944rad)
  sketch-geometry (8):
    g0: LineSegment StartX=-49.19 StartY=69.25 StartZ=0 EndX=-49.19 EndY=66.25 EndZ=0
    g1: LineSegment StartX=-49.19 StartY=5.75 StartZ=0 EndX=-49.19 EndY=2.75 EndZ=0
    g2: ArcOfCircle CenterX=-1.5 CenterY=67.75 CenterZ=0 NormalX=0 NormalY=0 NormalZ=1 AngleXU=0 Radius=1.5 StartAngle=4.71239 EndAngle=7.85398
    g3: ArcOfCircle CenterX=-1.5 CenterY=4.25 CenterZ=0 NormalX=0 NormalY=0 NormalZ=1 AngleXU=0 Radius=1.5 StartAngle=4.71239 EndAngle=7.85398
    g4: LineSegment StartX=-49.19 StartY=69.25 StartZ=0 EndX=-1.5 EndY=69.25 EndZ=0
    g5: LineSegment StartX=-49.19 StartY=66.25 StartZ=0 EndX=-1.5 EndY=66.25 EndZ=0
    g6: LineSegment StartX=-49.19 StartY=5.75 StartZ=0 EndX=-1.5 EndY=5.75 EndZ=0
    g7: LineSegment StartX=-49.19 StartY=2.75 StartZ=0 EndX=-1.5 EndY=2.75 EndZ=0
  constraints (19):
    c: Vertical(g0)
    c: Distance(g0) = 3
    c: Block(g0)
    c: Vertical(g1)
    c: Block(g2)
    c: Block(g3)
    c: Block(g1)
    c: Coincident(g4,g0)
    c: Coincident(g4,g2)
    c: Horizontal(g4)
    c: Coincident(g5,g0)
    c: Coincident(g5,g2)
    c: Horizontal(g5)
    c: Coincident(g6,g1)
    c: Coincident(g6,g3)
    c: Horizontal(g6)
    c: Coincident(g7,g1)
    c: Coincident(g7,g3)
    c: Horizontal(g7)
FEATURE [Part::Extrusion] Extrude073
  Base = -> Sketch082
  Dir = (1,0,0)
  DirMode = 2
  FaceMakerClass = Part::FaceMakerBullseye
  LengthFwd = 10
  LengthRev = 0
  Solid = true
  Symmetric = false
FEATURE [Part::Fillet] Fillet060  label="removeFromtMoreFrontCaseScrewRetainers005"
  Base = -> Extrude073
  Edges = 4 edges r=1.49: [Edge6,Edge11,Edge18,Edge23]
  Placement = pos=(-4,0,0) rot=(0,0,1;0rad)
FEATURE [Part::Revolution] Revolve163  label="backCaseScrewRetainer004"
  Angle = 360
  Axis = (0,1,0)
  Base = (0,0,0)
  FaceMakerClass = Part::FaceMakerBullseye
  Placement = pos=(12.5,3,62) rot=(0,0,1;0rad)
  Solid = false
  Source = -> Face149
  Symmetric = false
FEATURE [Part::Revolution] Revolve164  label="frontCaseScrewRetainer006"
  Angle = 360
  Axis = (0,1,0)
  Base = (0,0,0)
  FaceMakerClass = Part::FaceMakerBullseye
  Placement = pos=(89.5,3,68.5) rot=(0,0,1;0rad)
  Solid = false
  Source = -> Face151
  Symmetric = false
FEATURE [Part::Revolution] Revolve165  label="frontCaseScrewRetainer007"
  Angle = 360
  Axis = (0,1,0)
  Base = (0,0,0)
  FaceMakerClass = Part::FaceMakerBullseye
  Placement = pos=(89.5,3,3.5) rot=(0,0,1;0rad)
  Solid = false
  Source = -> Face152
  Symmetric = false
FEATURE [Part::Revolution] Revolve166  label="backCaseScrewRetainer005"
  Angle = 360
  Axis = (0,1,0)
  Base = (0,0,0)
  FaceMakerClass = Part::FaceMakerBullseye
  Placement = pos=(12.5,3,10) rot=(0,0,1;0rad)
  Solid = false
  Source = -> Face150
  Symmetric = false
FEATURE [Part::Revolution] Revolve167  label="moreFrontCaseScrewRetainer006"
  Angle = 360
  Axis = (0,1,0)
  Base = (0,0,0)
  FaceMakerClass = Part::FaceMakerBullseye
  Placement = pos=(109.5,4.5,68.5) rot=(0,0,1;0rad)
  Solid = false
  Source = -> Face153
  Symmetric = false
FEATURE [Part::Revolution] Revolve168  label="moreFrontCaseScrewRetainer007"
  Angle = 360
  Axis = (0,1,0)
  Base = (0,0,0)
  FaceMakerClass = Part::FaceMakerBullseye
  Placement = pos=(109.5,4.5,3.5) rot=(0,0,1;0rad)
  Solid = false
  Source = -> Face154
  Symmetric = false
FEATURE [Part::MultiFuse] Fusion151  label="screwRetainers003"
  Shapes = -> [Revolve168,Revolve167,Revolve166,Revolve165,Revolve164,Revolve163]
FEATURE [Part::Cut] Cut069  label="screwRetainers004"
  Base = -> Fusion151
  Tool = -> Fusion152
FEATURE [Part::Cut] Cut070
  Base = -> Cut069
  Tool = -> Fillet060
FEATURE [Part::Cut] Cut071  label="screwPillars001"
  Base = -> Cut070
  Tool = -> Fillet059
FEATURE [Part::MultiFuse] Fusion153  label="bottom024"
  Shapes = -> [Fusion149,Cut071]
FEATURE [Part::Cylinder] Cylinder067
  Angle = 360
  AttacherType = Attacher::AttachEngine3D
  Height = 10
  Placement = pos=(20.65,12,4.68) rot=(1,0,0;1.5708rad)
  Radius = 2
FEATURE [Part::Cylinder] Cylinder068
  Angle = 360
  AttacherType = Attacher::AttachEngine3D
  Height = 10
  Placement = pos=(20.65,12,67.38) rot=(1,0,0;1.5708rad)
  Radius = 2
FEATURE [Part::Cylinder] Cylinder069
  Angle = 360
  AttacherType = Attacher::AttachEngine3D
  Height = 10
  Placement = pos=(77.15,12,67.38) rot=(1,0,0;1.5708rad)
  Radius = 2
FEATURE [Part::Cylinder] Cylinder070
  Angle = 360
  AttacherType = Attacher::AttachEngine3D
  Height = 10
  Placement = pos=(77.15,12,4.68) rot=(1,0,0;1.5708rad)
  Radius = 2
FEATURE [Part::MultiFuse] Fusion154  label="removeFromThreadedInsertHousing001"
  Shapes = -> [Cylinder069,Cylinder068,Cylinder067,Cylinder070]
FEATURE [Part::Cut] Cut072  label="bottom025"
  Base = -> Fusion153
  Tool = -> Fusion154
FEATURE [Image::ImagePlane] ImagePlane
  XSize = 339
  YSize = 72
FEATURE [Sketcher::SketchObject] Sketch083
  FullyConstrained = true
  MapMode = 5
  Support = -> [XY_Plane]
  sketch-geometry (242):
    g0: LineSegment StartX=-151.619 StartY=28.8932 StartZ=0 EndX=-140.819 EndY=28.8932 EndZ=0
    g1: LineSegment StartX=-151.619 StartY=24.0313 StartZ=0 EndX=-151.619 EndY=28.8932 EndZ=0
    g2: LineSegment StartX=-140.819 StartY=17.7713 StartZ=0 EndX=-151.619 EndY=17.7713 EndZ=0
    g3: LineSegment StartX=-151.619 StartY=17.7713 StartZ=0 EndX=-151.619 EndY=22.6313 EndZ=0
    g4: LineSegment StartX=-151.619 StartY=22.6313 StartZ=0 EndX=-145.128 EndY=22.6313 EndZ=0
    g5: LineSegment StartX=-145.128 StartY=24.0313 StartZ=0 EndX=-140.819 EndY=28.8932 EndZ=0
    g6: LineSegment StartX=-145.128 StartY=22.6313 StartZ=0 EndX=-140.819 EndY=17.7713 EndZ=0
    g7: ArcOfCircle CenterX=-155.157 CenterY=23.3323 CenterZ=0 NormalX=0 NormalY=0 NormalZ=1 AngleXU=0 Radius=6.92354 StartAngle=1.03434 EndAngle=5.24885
    g8: ArcOfCircle CenterX=-155.157 CenterY=23.3323 CenterZ=0 NormalX=0 NormalY=0 NormalZ=1 AngleXU=0 Radius=12.6269 StartAngle=1.28675 EndAngle=4.99643
    g9: LineSegment StartX=-151.619 StartY=35.4532 StartZ=0 EndX=-151.619 EndY=29.2832 EndZ=0
    g10: LineSegment StartX=-151.619 StartY=17.3813 StartZ=0 EndX=-151.619 EndY=11.2113 EndZ=0
    g11-g21: Circle x11 (B-spline internal-alignment scaffolding for g22; pole/knot coordinates omitted)
    g22: BSplineCurve PolesCount=11 KnotsCount=9 Degree=3 IsPeriodic=0
    g23-g31: GeomPoint x9 (B-spline internal-alignment scaffolding for g22; pole/knot coordinates omitted)
    g32-g49: Circle x18 (B-spline internal-alignment scaffolding for g50; pole/knot coordinates omitted)
    g50: BSplineCurve PolesCount=18 KnotsCount=16 Degree=3 IsPeriodic=0
    g51-g66: GeomPoint x16 (B-spline internal-alignment scaffolding for g50; pole/knot coordinates omitted)
    g67: LineSegment StartX=-117.124 StartY=30.093 StartZ=0 EndX=-117.603 EndY=26.5272 EndZ=0
    g68: LineSegment StartX=-117.603 StartY=17.8472 StartZ=0 EndX=-117.124 EndY=14.2659 EndZ=0
    g69: Ellipse CenterX=-109.671 CenterY=20.025 CenterZ=0 NormalX=0 NormalY=0 NormalZ=1 MajorRadius=3.34798 MinorRadius=2.71052 AngleXU=-1.56793
    g70: GeomPoint X=-109.666 Y=18.0598 Z=0
    g71: GeomPoint X=-109.677 Y=21.9902 Z=0
    g72: Ellipse CenterX=-109.671 CenterY=20.0123 CenterZ=0 NormalX=0 NormalY=0 NormalZ=1 MajorRadius=6.93002 MinorRadius=6.36273 AngleXU=-3.13976
    g73: GeomPoint X=-112.417 Y=20.0073 Z=0
    g74: GeomPoint X=-106.925 Y=20.0173 Z=0
    g75: Ellipse CenterX=-51.7682 CenterY=20.1463 CenterZ=0 NormalX=0 NormalY=0 NormalZ=1 MajorRadius=3.19279 MinorRadius=2.71052 AngleXU=-1.52774
    g76: GeomPoint X=-51.6955 Y=18.4606 Z=0
    g77: GeomPoint X=-51.8408 Y=21.832 Z=0
    g78: GeomPoint X=-54.5142 Y=20.1413 Z=0
    g79: GeomPoint X=-49.0221 Y=20.1513 Z=0
    g80: Ellipse CenterX=-51.7682 CenterY=20.1463 CenterZ=0 NormalX=0 NormalY=0 NormalZ=1 MajorRadius=6.93002 MinorRadius=6.36273 AngleXU=-3.13976
    g81: Ellipse CenterX=-22.8436 CenterY=20.1783 CenterZ=0 NormalX=0 NormalY=0 NormalZ=1 MajorRadius=3.31512 MinorRadius=2.71052 AngleXU=-1.60214
    g82: GeomPoint X=-22.9034 Y=18.2706 Z=0
    g83: GeomPoint X=-22.7838 Y=22.0861 Z=0
    g84: GeomPoint X=-25.5897 Y=20.1733 Z=0
    g85: GeomPoint X=-20.0976 Y=20.1833 Z=0
    g86: Ellipse CenterX=-22.8436 CenterY=20.1783 CenterZ=0 NormalX=0 NormalY=0 NormalZ=1 MajorRadius=6.93002 MinorRadius=6.36273 AngleXU=-3.13976
    g87: LineSegment StartX=-101.889 StartY=14.1107 StartZ=0 EndX=-97.7455 EndY=14.1107 EndZ=0
    g88: LineSegment StartX=-93.8155 StartY=14.1107 StartZ=0 EndX=-89.6755 EndY=14.1107 EndZ=0
    g89: LineSegment StartX=-85.7455 StartY=14.1107 StartZ=0 EndX=-81.6055 EndY=14.1107 EndZ=0
    g90: LineSegment StartX=-101.889 StartY=14.1107 StartZ=0 EndX=-101.889 EndY=25.9907 EndZ=0
    g91: LineSegment StartX=-101.889 StartY=25.9907 StartZ=0 EndX=-97.8594 EndY=25.9907 EndZ=0
    g92: LineSegment StartX=-97.8594 StartY=25.9907 StartZ=0 EndX=-97.8594 EndY=24.0907 EndZ=0
    g93: LineSegment StartX=-97.7455 StartY=14.1107 StartZ=0 EndX=-97.7455 EndY=19.9107 EndZ=0
    g94: LineSegment StartX=-89.6755 StartY=14.1107 StartZ=0 EndX=-89.6755 EndY=19.9107 EndZ=0
    g95: LineSegment StartX=-93.8155 StartY=14.1107 StartZ=0 EndX=-93.8155 EndY=21.0107 EndZ=0
    g96-g106: Circle x11 (B-spline internal-alignment scaffolding for g107; pole/knot coordinates omitted)
    g107: BSplineCurve PolesCount=11 KnotsCount=9 Degree=3 IsPeriodic=0
    g108-g116: GeomPoint x9 (B-spline internal-alignment scaffolding for g107; pole/knot coordinates omitted)
    g117: BSplineCurve PolesCount=11 KnotsCount=9 Degree=3 IsPeriodic=0
    g118-g125: Circle x8 (B-spline internal-alignment scaffolding for g126; pole/knot coordinates omitted)
    g126: BSplineCurve PolesCount=8 KnotsCount=6 Degree=3 IsPeriodic=0
    g127-g132: GeomPoint x6 (B-spline internal-alignment scaffolding for g126; pole/knot coordinates omitted)
    g133: BSplineCurve PolesCount=8 KnotsCount=6 Degree=3 IsPeriodic=0
    g134: LineSegment StartX=-85.7455 StartY=21.0107 StartZ=0 EndX=-85.7455 EndY=14.1107 EndZ=0
    g135: LineSegment StartX=-80.0879 StartY=14.1107 StartZ=0 EndX=-75.944 EndY=14.1107 EndZ=0
    g136: LineSegment StartX=-72.014 StartY=14.1107 StartZ=0 EndX=-67.874 EndY=14.1107 EndZ=0
    g137: LineSegment StartX=-63.944 StartY=14.1107 StartZ=0 EndX=-59.804 EndY=14.1107 EndZ=0
    g138: LineSegment StartX=-80.0879 StartY=14.1107 StartZ=0 EndX=-80.0879 EndY=25.9907 EndZ=0
    g139: LineSegment StartX=-80.0879 StartY=25.9907 StartZ=0 EndX=-76.0579 EndY=25.9907 EndZ=0
    g140: LineSegment StartX=-76.0579 StartY=25.9907 StartZ=0 EndX=-76.0579 EndY=24.0907 EndZ=0
    g141: LineSegment StartX=-75.944 StartY=14.1107 StartZ=0 EndX=-75.944 EndY=19.9107 EndZ=0
    g142: LineSegment StartX=-67.874 StartY=14.1107 StartZ=0 EndX=-67.874 EndY=19.9107 EndZ=0
    g143: LineSegment StartX=-72.014 StartY=14.1107 StartZ=0 EndX=-72.014 EndY=21.0107 EndZ=0
    g144-g148: Circle x5 (B-spline internal-alignment scaffolding for g149; pole/knot coordinates omitted)
    g149: BSplineCurve PolesCount=11 KnotsCount=9 Degree=3 IsPeriodic=0
    g150-g158: GeomPoint x9 (B-spline internal-alignment scaffolding for g149; pole/knot coordinates omitted)
    g159: BSplineCurve PolesCount=11 KnotsCount=9 Degree=3 IsPeriodic=0
    g160-g167: Circle x8 (B-spline internal-alignment scaffolding for g168; pole/knot coordinates omitted)
    g168: BSplineCurve PolesCount=8 KnotsCount=6 Degree=3 IsPeriodic=0
    g169-g174: GeomPoint x6 (B-spline internal-alignment scaffolding for g168; pole/knot coordinates omitted)
    g175: BSplineCurve PolesCount=8 KnotsCount=6 Degree=3 IsPeriodic=0
    g176: LineSegment StartX=-63.944 StartY=21.0107 StartZ=0 EndX=-63.944 EndY=14.1107 EndZ=0
    g177: LineSegment StartX=-59.804 StartY=14.1107 StartZ=0 EndX=-59.804 EndY=21.5868 EndZ=0
    g178: BSplineCurve PolesCount=4 KnotsCount=2 Degree=3 IsPeriodic=0
    g179: GeomPoint X=-59.804 Y=21.5868 Z=0
    g180: GeomPoint X=-60.2379 Y=24.0907 Z=0
    g181: LineSegment StartX=-81.6055 StartY=14.1107 StartZ=0 EndX=-81.6055 EndY=21.5868 EndZ=0
    g182: LineSegment StartX=-151.619 StartY=24.0313 StartZ=0 EndX=-145.128 EndY=24.0313 EndZ=0
    g183: Circle CenterX=-82.0394 CenterY=24.0907 CenterZ=0 NormalX=0 NormalY=0 NormalZ=1 AngleXU=0 Radius=1
    g184: Circle CenterX=-81.7131 CenterY=23.2736 CenterZ=0 NormalX=0 NormalY=0 NormalZ=1 AngleXU=0 Radius=1
    g185: Circle CenterX=-81.6055 CenterY=21.5868 CenterZ=0 NormalX=0 NormalY=0 NormalZ=1 AngleXU=0 Radius=1
    g186: BSplineCurve PolesCount=3 KnotsCount=2 Degree=2 IsPeriodic=0
    g187: GeomPoint X=-82.0394 Y=24.0907 Z=0
    g188: GeomPoint X=-81.6055 Y=21.5868 Z=0
    g189: Ellipse CenterX=-37.3522 CenterY=19.9515 CenterZ=0 NormalX=0 NormalY=0 NormalZ=1 MajorRadius=2.99755 MinorRadius=2.49 AngleXU=1.5708
    g190: GeomPoint X=-37.3522 Y=21.6203 Z=0
    g191: GeomPoint X=-37.3522 Y=18.2826 Z=0
    g192: ArcOfEllipse CenterX=-38.7647 CenterY=20.06 CenterZ=0 NormalX=0 NormalY=0 NormalZ=1 MajorRadius=6.30025 MinorRadius=5.3849 AngleXU=1.57276 StartAngle=5.50632 EndAngle=10.3035
    g193: GeomPoint X=-38.7711 Y=23.3304 Z=0
    g194: GeomPoint X=-38.7583 Y=16.7895 Z=0
    g195: LineSegment StartX=-34.6109 StartY=14.1107 StartZ=0 EndX=-30.8984 EndY=14.1107 EndZ=0
    g196: LineSegment StartX=-30.8984 StartY=14.1107 StartZ=0 EndX=-30.8984 EndY=31.1784 EndZ=0
    g197: LineSegment StartX=-30.8984 StartY=31.1784 StartZ=0 EndX=-34.9984 EndY=31.1784 EndZ=0
    g198: LineSegment StartX=-34.9984 StartY=24.5602 StartZ=0 EndX=-34.9984 EndY=31.1784 EndZ=0
    g199: LineSegment StartX=-34.6109 StartY=16.0476 StartZ=0 EndX=-34.6109 EndY=14.1107 EndZ=0
    g200: LineSegment StartX=-14.8781 StartY=14.1107 StartZ=0 EndX=-10.5106 EndY=14.1107 EndZ=0
    g201: LineSegment StartX=-14.8781 StartY=14.1107 StartZ=0 EndX=-14.8781 EndY=25.8504 EndZ=0
    g202: LineSegment StartX=-14.8781 StartY=25.8504 StartZ=0 EndX=-10.8534 EndY=25.8504 EndZ=0
    g203: LineSegment StartX=-10.8534 StartY=25.8504 StartZ=0 EndX=-10.8534 EndY=24.0923 EndZ=0
    g204: LineSegment StartX=-10.5106 StartY=14.1107 StartZ=0 EndX=-10.5106 EndY=19.7752 EndZ=0
    g205: LineSegment StartX=-5.98735 StartY=25.9939 StartZ=0 EndX=-6.26019 EndY=22.6375 EndZ=0
    g206-g214: Circle x9 (B-spline internal-alignment scaffolding for g215; pole/knot coordinates omitted)
    g215: BSplineCurve PolesCount=9 KnotsCount=7 Degree=3 IsPeriodic=0
    g216-g222: GeomPoint x7 (B-spline internal-alignment scaffolding for g215; pole/knot coordinates omitted)
    g223-g232: Circle x10 (B-spline internal-alignment scaffolding for g233; pole/knot coordinates omitted)
    g233: BSplineCurve PolesCount=10 KnotsCount=8 Degree=3 IsPeriodic=0
    g234-g241: GeomPoint x8 (B-spline internal-alignment scaffolding for g233; pole/knot coordinates omitted)
  constraints (224):
    c: Coincident(g1,g0)
    c: Horizontal(g0)
    c: Vertical(g1)
    c: Coincident(g2,g3)
    c: Coincident(g3,g4)
    c: Horizontal(g4)
    c: Horizontal(g2)
    c: Vertical(g3)
    c: Block(g1)
    c: Distance(g3) = 4.86
    c: Block(g4)
    c: Distance(g0) = 10.8
    c: Distance(g2) = 10.8
    c: Coincident(g5,g0)
    c: Coincident(g6,g4)
    c: Coincident(g6,g2)
    c: Block(g8)
    c: Block(g7)
    c: Coincident(g9,g8)
    c: Coincident(g9,g7)
    c: Vertical(g9)
    c: Coincident(g10,g7)
    c: Coincident(g10,g8)
    c: Vertical(g10)
    c: Weight(g11) = 1
    c: Equal(g11, g12-g21) x10
    c: InternalAlignment(g11-g21 -> g22) x11
    c: InternalAlignment(g23-g31 -> g22) x9
    c: Block(g22)
    c: Weight(g32) = 1
    c: Equal(g32, g33-g49) x17
    c: InternalAlignment(g32-g49 -> g50) x18
    c: InternalAlignment(g51-g66 -> g50) x16
    c: Block(g50)
    c: Coincident(g67,g50)
    c: Coincident(g67,g22)
    c: Coincident(g68,g22)
    c: Coincident(g68,g50)
    c: InternalAlignment(g70,g69)
    c: InternalAlignment(g71,g69)
    c: Block(g69)
    c: InternalAlignment(g73,g72)
    c: InternalAlignment(g74,g72)
    c: Block(g72)
    c: InternalAlignment(g76,g75)
    c: InternalAlignment(g77,g75)
    c: InternalAlignment(g78,g80)
    c: InternalAlignment(g79,g80)
    c: Block(g80)
    c: Coincident(g75,g80)
    c: Block(g75)
    c: InternalAlignment(g82,g81)
    c: InternalAlignment(g83,g81)
    c: InternalAlignment(g84,g86)
    c: InternalAlignment(g85,g86)
    c: Block(g86)
    c: Coincident(g81,g86)
    c: Block(g81)
    c: Horizontal(g87)
    c: Block(g87)
    c: Horizontal(g88)
    c: Distance(g88) = 4.14
    c: Horizontal(g89)
    c: Equal(g88,g89) = 4.14
    c: Block(g89)
    c: Block(g88)
    c: Coincident(g90,g87)
    c: Vertical(g90)
    c: Distance(g90) = 11.88
    c: Coincident(g91,g90)
    c: Horizontal(g91)
    c: Coincident(g92,g91)
    c: Vertical(g92)
    c: Distance(g91) = 4.03
    c: Distance(g92) = 1.9
    c: Coincident(g93,g87)
    c: Vertical(g93)
    c: Vertical(g94)
    c: Coincident(g94,g88)
    c: Distance(g93) = 5.8
    c: Distance(g94) = 5.8
    c: Vertical(g95)
    c: Coincident(g95,g88)
    c: Distance(g95) = 6.9
    c: Coincident(g107,g92)
    c: Weight(g96) = 1
    c: Equal(g96, g97-g106) x10
    c: InternalAlignment(g96-g106 -> g107) x11
    c: InternalAlignment(g108-g116 -> g107) x9
    c: Block(g107)
    c: Block(g117)
    c: Coincident(g126,g93)
    c: Weight(g118) = 1
    c: Equal(g118, g119-g125) x7
    c: Coincident(g126,g95)
    c: InternalAlignment(g118-g125 -> g126) x8
    c: InternalAlignment(g127-g132 -> g126) x6
    c: Coincident(g133,g94)
    c: Block(g126)
    c: Block(g133)
    c: Coincident(g134,g133)
    c: Coincident(g134,g89)
    c: Vertical(g134)
    c: Horizontal(g135)
    c: Block(g135)
    c: Horizontal(g136)
    c: Equal(g88,g136) = 4.14
    c: Horizontal(g137)
    c: Equal(g136,g137) = 4.14
    c: Block(g137)
    c: Block(g136)
    c: Coincident(g138,g135)
    c: Vertical(g138)
    c: Equal(g90,g138) = 11.88
    c: Coincident(g139,g138)
    c: Horizontal(g139)
    c: Coincident(g140,g139)
    c: Vertical(g140)
    c: Equal(g91,g139) = 4.03
    c: Equal(g92,g140) = 1.9
    c: Coincident(g141,g135)
    c: Vertical(g141)
    c: Vertical(g142)
    c: Coincident(g142,g136)
    c: Equal(g93,g141) = 5.8
    c: Equal(g94,g142) = 5.8
    c: Vertical(g143)
    c: Coincident(g143,g136)
    c: Equal(g95,g143) = 6.9
    c: Coincident(g149,g140)
    c: Equal(g96,g144) = 1
    c: Equal(g144, g145-g148) x4
    c: InternalAlignment(g144-g148 -> g149) x5
    c: InternalAlignment(g150-g158 -> g149) x9
    c: Block(g149)
    c: Block(g159)
    c: Coincident(g168,g141)
    c: Equal(g118,g160) = 1
    c: Equal(g160, g161-g167) x7
    c: Coincident(g168,g143)
    c: InternalAlignment(g160-g167 -> g168) x8
    c: InternalAlignment(g169-g174 -> g168) x6
    c: Coincident(g175,g142)
    c: Block(g168)
    c: Block(g175)
    c: Coincident(g176,g175)
    c: Coincident(g176,g137)
    c: Vertical(g176)
    c: Coincident(g177,g137)
    c: Vertical(g177)
    c: Coincident(g178,g177)
    c: Coincident(g178,g159)
    c: InternalAlignment(g179,g178)
    c: InternalAlignment(g180,g178)
    c: Block(g178)
    c: Vertical(g181)
    c: Coincident(g181,g89)
    c: Block(g5)
    c: Coincident(g182,g1)
    c: Coincident(g182,g5)
    c: Horizontal(g182)
    c: Coincident(g186,g117)
    c: Weight(g183) = 1
    c: Equal(g183,g184)
    c: Equal(g183,g185)
    c: Coincident(g186,g181)
    c: InternalAlignment(g183,g186)
    c: InternalAlignment(g184,g186)
    c: InternalAlignment(g185,g186)
    c: InternalAlignment(g187,g186)
    c: InternalAlignment(g188,g186)
    c: Block(g186)
    c: InternalAlignment(g190,g189)
    c: InternalAlignment(g191,g189)
    c: Block(g189)
    c: InternalAlignment(g193,g192)
    c: InternalAlignment(g194,g192)
    c: Block(g192)
    c: Horizontal(g195)
    c: Block(g195)
    c: Coincident(g196,g195)
    c: Vertical(g196)
    c: Block(g196)
    c: Distance(g195) = 3.71244
    c: Coincident(g197,g196)
    c: Horizontal(g197)
    c: Distance(g197) = 4.1
    c: Coincident(g198,g192)
    c: Coincident(g198,g197)
    c: Vertical(g198)
    c: Block(g198)
    c: Coincident(g199,g192)
    c: Coincident(g199,g195)
    c: Vertical(g199)
    c: Block(g199)
    c: Horizontal(g200)
    c: Block(g200)
    c: Coincident(g201,g200)
    c: Vertical(g201)
    c: Block(g201)
    c: Coincident(g202,g201)
    c: Horizontal(g202)
    c: Block(g202)
    c: Coincident(g203,g202)
    c: Vertical(g203)
    c: Block(g203)
    c: Coincident(g204,g200)
    c: Vertical(g204)
    c: Block(g204)
    c: Block(g205)
    c: Coincident(g215,g203)
    c: Weight(g206) = 1
    c: Equal(g206, g207-g214) x8
    c: Coincident(g215,g205)
    c: InternalAlignment(g206-g214 -> g215) x9
    c: InternalAlignment(g216-g222 -> g215) x7
    c: Block(g215)
    c: Coincident(g233,g204)
    c: Weight(g223) = 1
    c: Equal(g223, g224-g232) x9
    c: Coincident(g233,g205)
    c: InternalAlignment(g223-g232 -> g233) x10
    c: InternalAlignment(g234-g241 -> g233) x8
    c: Block(g233)
FEATURE [PartDesign::Body] Body
  Group = -> [Sketch083]
  Origin = -> Origin
FEATURE [Sketcher::SketchObject] Sketch084
  FullyConstrained = true
  MapMode = 5
  Support = -> [XY_Plane001]
FEATURE [PartDesign::Body] Body001
  Group = -> [Sketch084]
  Origin = -> Origin001
